FCSTD DOCUMENT  (FreeCAD 0.18.4R)
Label: SRM 2020
License: All rights reserved
LicenseURL: http://en.wikipedia.org/wiki/All_rights_reserved
objects: Part::Feature×163, App::Part×73, Sketcher::SketchObject×30, PartDesign::Pad×19, PartDesign::Body×17, Part::Fillet×15, PartDesign::Pocket×11, Part::MultiFuse×1, Mesh::Feature×1, Part::Cut×1
note: 287 computed .brp shape members not serialized (recipe doc carries the construction recipe); baked Part::Feature solids carry a one-line shape summary decoded from their .brp

FEATURE [Sketcher::SketchObject] Sketch005  label="Sketch_L_Bracket"
  MapMode = 5
  Placement = pos=(-195.5,0,1.5) rot=(0,1,0;3.14159rad)
  sketch-geometry (46):
    g0: LineSegment StartX=0 StartY=36 StartZ=0 EndX=12 EndY=36 EndZ=0
    g1: LineSegment StartX=12 StartY=36 StartZ=0 EndX=28 EndY=12 EndZ=0
    g2: LineSegment StartX=28 StartY=12 StartZ=0 EndX=28 EndY=0 EndZ=0
    g3: LineSegment StartX=28 StartY=0 StartZ=0 EndX=26 EndY=0 EndZ=0
    g4: LineSegment StartX=26 StartY=0 StartZ=0 EndX=26 EndY=-3 EndZ=0
    g5: LineSegment StartX=26 StartY=-3 StartZ=0 EndX=18 EndY=-3 EndZ=0
    g6: LineSegment StartX=18 StartY=-3 StartZ=0 EndX=18 EndY=0 EndZ=0
    g7: LineSegment StartX=18 StartY=0 StartZ=0 EndX=15.5 EndY=0 EndZ=0
    g8: LineSegment StartX=15.5 StartY=0 StartZ=0 EndX=15.5 EndY=4 EndZ=0
    g9: LineSegment StartX=15.5 StartY=4 StartZ=0 EndX=16.75 EndY=4 EndZ=0
    g10: LineSegment StartX=16.75 StartY=4 StartZ=0 EndX=16.75 EndY=6.3 EndZ=0
    g11: LineSegment StartX=11.25 StartY=6.3 StartZ=0 EndX=11.25 EndY=4 EndZ=0
    g12: LineSegment StartX=11.25 StartY=4 StartZ=0 EndX=12.5 EndY=4 EndZ=0
    g13: LineSegment StartX=12.5 StartY=4 StartZ=0 EndX=12.5 EndY=0 EndZ=0
    g14: LineSegment StartX=12.5 StartY=1e-16 StartZ=0 EndX=10 EndY=1e-16 EndZ=0
    g15: LineSegment StartX=10 StartY=1e-16 StartZ=0 EndX=10 EndY=-3 EndZ=0
    g16: LineSegment StartX=10 StartY=-3 StartZ=0 EndX=2 EndY=-3 EndZ=0
    g17: LineSegment StartX=2 StartY=-3 StartZ=0 EndX=2 EndY=0 EndZ=0
    g18: LineSegment StartX=2 StartY=0 StartZ=0 EndX=0 EndY=0 EndZ=0
    g19: LineSegment StartX=0 StartY=0 StartZ=0 EndX=0 EndY=10 EndZ=0
    g20: LineSegment StartX=0 StartY=10 StartZ=0 EndX=-3 EndY=10 EndZ=0
    g21: LineSegment StartX=-3 StartY=10 StartZ=0 EndX=-3 EndY=18 EndZ=0
    g22: LineSegment StartX=-3 StartY=18 StartZ=0 EndX=0 EndY=18 EndZ=0
    g23: LineSegment StartX=0 StartY=18 StartZ=0 EndX=0 EndY=20.5 EndZ=0
    g24: LineSegment StartX=0 StartY=20.5 StartZ=0 EndX=4 EndY=20.5 EndZ=0
    g25: LineSegment StartX=4 StartY=20.5 StartZ=0 EndX=4 EndY=19.25 EndZ=0
    g26: LineSegment StartX=4 StartY=19.25 StartZ=0 EndX=6.3 EndY=19.25 EndZ=0
    g27: LineSegment StartX=6.3 StartY=24.75 StartZ=0 EndX=4 EndY=24.75 EndZ=0
    g28: LineSegment StartX=4 StartY=24.75 StartZ=0 EndX=4 EndY=23.5 EndZ=0
    g29: LineSegment StartX=4 StartY=23.5 StartZ=0 EndX=0 EndY=23.5 EndZ=0
    g30: LineSegment StartX=0 StartY=23.5 StartZ=0 EndX=0 EndY=26 EndZ=0
    g31: LineSegment StartX=0 StartY=26 StartZ=0 EndX=-3 EndY=26 EndZ=0
    g32: LineSegment StartX=-3 StartY=26 StartZ=0 EndX=-3 EndY=34 EndZ=0
    g33: LineSegment StartX=-3 StartY=34 StartZ=0 EndX=0 EndY=34 EndZ=0
    g34: LineSegment StartX=0 StartY=34 StartZ=0 EndX=0 EndY=36 EndZ=0
    g35: LineSegment StartX=12.5 StartY=6.3 StartZ=0 EndX=12.5 EndY=9.3 EndZ=0
    g36: LineSegment StartX=12.5 StartY=9.3 StartZ=0 EndX=15.5 EndY=9.3 EndZ=0
    g37: LineSegment StartX=15.5 StartY=9.3 StartZ=0 EndX=15.5 EndY=6.3 EndZ=0
    g38: LineSegment StartX=11.25 StartY=6.3 StartZ=0 EndX=12.5 EndY=6.3 EndZ=0
    g39: LineSegment StartX=15.5 StartY=6.3 StartZ=0 EndX=16.75 EndY=6.3 EndZ=0
    g40: LineSegment StartX=6.3 StartY=24.75 StartZ=0 EndX=6.3 EndY=23.5 EndZ=0
    g41: LineSegment StartX=6.3 StartY=23.5 StartZ=0 EndX=9.3 EndY=23.5 EndZ=0
    g42: LineSegment StartX=9.3 StartY=23.5 StartZ=0 EndX=9.3 EndY=20.5 EndZ=0
    g43: LineSegment StartX=9.3 StartY=20.5 StartZ=0 EndX=6.3 EndY=20.5 EndZ=0
    g44: LineSegment StartX=6.3 StartY=20.5 StartZ=0 EndX=6.3 EndY=19.25 EndZ=0
    g45: GeomPoint X=0 Y=22 Z=0
  constraints (135):
    c: Horizontal(g0)
    c: Coincident(g1,g0)
    c: Coincident(g2,g1)
    c: Vertical(g2)
    c: Coincident(g3,g2)
    c: Horizontal(g3)
    c: Coincident(g4,g3)
    c: Vertical(g4)
    c: Coincident(g5,g4)
    c: Horizontal(g5)
    c: Coincident(g6,g5)
    c: Vertical(g6)
    c: Horizontal(g7)
    c: Coincident(g8,g7)
    c: Vertical(g8)
    c: Coincident(g9,g8)
    c: Coincident(g10,g9)
    c: Vertical(g10)
    c: Horizontal(g9)
    c: Vertical(g11)
    c: Coincident(g12,g11)
    c: Horizontal(g12)
    c: Coincident(g13,g12)
    c: Vertical(g13)
    c: Horizontal(g14)
    c: Coincident(g15,g14)
    c: Vertical(g15)
    c: Coincident(g16,g15)
    c: Horizontal(g16)
    c: Coincident(g17,g16)
    c: Vertical(g17)
    c: Coincident(g18,g17)
    c: Horizontal(g18)
    c: Coincident(g19,g18)
    c: Vertical(g19)
    c: Coincident(g20,g19)
    c: Horizontal(g20)
    c: Coincident(g21,g20)
    c: Vertical(g21)
    c: Coincident(g22,g21)
    c: Horizontal(g22)
    c: Coincident(g23,g22)
    c: Vertical(g23)
    c: Coincident(g24,g23)
    c: Horizontal(g24)
    c: Coincident(g25,g24)
    c: Vertical(g25)
    c: Coincident(g26,g25)
    c: Horizontal(g26)
    c: Horizontal(g27)
    c: Coincident(g28,g27)
    c: Vertical(g28)
    c: Coincident(g29,g28)
    c: Horizontal(g29)
    c: Coincident(g30,g29)
    c: Vertical(g30)
    c: Coincident(g31,g30)
    c: Coincident(g32,g31)
    c: Vertical(g32)
    c: Coincident(g33,g32)
    c: Coincident(g34,g33)
    c: Coincident(g34,g0)
    c: Horizontal(g33)
    c: Horizontal(g31)
    c: Vertical(g34)
    c: Coincident(g13,g14)
    c: Coincident(g6,g7)
    c: Vertical(g35)
    c: Coincident(g36,g35)
    c: Horizontal(g36)
    c: Coincident(g37,g36)
    c: Vertical(g37)
    c: Coincident(g38,g11)
    c: Coincident(g38,g35)
    c: Horizontal(g38)
    c: Coincident(g39,g10)
    c: Horizontal(g39)
    c: Coincident(g39,g37)
    c: Coincident(g40,g27)
    c: Vertical(g40)
    c: Coincident(g41,g40)
    c: Horizontal(g41)
    c: Coincident(g42,g41)
    c: Vertical(g42)
    c: Coincident(g43,g42)
    c: Horizontal(g43)
    c: Coincident(g44,g43)
    c: Vertical(g44)
    c: Coincident(g44,g26)
    c: DistanceY(g32,g32) = 8
    c: Equal(g32,g21)
    c: Equal(g21,g16)
    c: Equal(g16,g5)
    c: Equal(g42,g36)
    c: Equal(g27,g26)
    c: Equal(g26,g11)
    c: Equal(g11,g10)
    c: Equal(g41,g43)
    c: Equal(g43,g35)
    c: Equal(g35,g37)
    c: Equal(g29,g24)
    c: Equal(g24,g13)
    c: Equal(g13,g8)
    c: Equal(g30,g23)
    c: Equal(g23,g14)
    c: Equal(g14,g7)
    c: DistanceX(g33,g33) = 3
    c: Equal(g33,g31)
    c: Equal(g31,g22)
    c: Equal(g22,g20)
    c: Equal(g20,g17)
    c: Equal(g17,g15)
    c: Equal(g15,g6)
    c: Equal(g6,g4)
    c: Equal(g3,g34)
    c: Equal(g0,g2)
    c: DistanceX(g27,g27) = 2.3
    c: DistanceY(g42,g42) = 3
    c: DistanceX(g41,g41) = 3
    c: Equal(g28,g40)
    c: Equal(g40,g44)
    c: Equal(g44,g25)
    c: Equal(g38,g39)
    c: Equal(g39,g9)
    c: Equal(g9,g12)
    c: Equal(g38,g25)
    c: DistanceY(g28,g28) = 1.25
    c: DistanceX(g29,g29) = 4
    c: DistanceY(g30,g30) = 2.5
    c: DistanceY(g34,g34) = 2
    c: DistanceX(g0,g0) = 12
    c: DistanceX(g18,g18) = 2
    c: Coincident(g18,g-1)
    c: Symmetric(g29,g23,g45)
    c: DistanceY(g18,g45) = 22
FEATURE [PartDesign::Pad] Pad006
  Length = 3
  Length2 = 100
  Placement = pos=(-195.5,0,1.5) rot=(0,1,0;3.14159rad)
  Profile = -> Sketch005
  Refine = true
  Type = 0
FEATURE [PartDesign::Body] Body006  label="Body Bracket L"
  Group = -> [Sketch005,Pad006]
  Origin = -> Origin006
  Tip = -> Pad006
FEATURE [Part::Fillet] Fillet010  label="Fillet001"
  Base = -> Body006
  Edges = 2 edges r=6: [Edge26,Edge29]
FEATURE [Sketcher::SketchObject] Sketch006  label="Sketch_R_Bracket"
  MapMode = 5
  Placement = pos=(195.5,0,-1.5) rot=(0,1,0;0rad)
  sketch-geometry (46):
    g0: LineSegment StartX=0 StartY=36 StartZ=0 EndX=12 EndY=36 EndZ=0
    g1: LineSegment StartX=12 StartY=36 StartZ=0 EndX=28 EndY=12 EndZ=0
    g2: LineSegment StartX=28 StartY=12 StartZ=0 EndX=28 EndY=0 EndZ=0
    g3: LineSegment StartX=28 StartY=0 StartZ=0 EndX=26 EndY=0 EndZ=0
    g4: LineSegment StartX=26 StartY=0 StartZ=0 EndX=26 EndY=-3 EndZ=0
    g5: LineSegment StartX=26 StartY=-3 StartZ=0 EndX=18 EndY=-3 EndZ=0
    g6: LineSegment StartX=18 StartY=-3 StartZ=0 EndX=18 EndY=0 EndZ=0
    g7: LineSegment StartX=18 StartY=0 StartZ=0 EndX=15.5 EndY=0 EndZ=0
    g8: LineSegment StartX=15.5 StartY=0 StartZ=0 EndX=15.5 EndY=4 EndZ=0
    g9: LineSegment StartX=15.5 StartY=4 StartZ=0 EndX=16.75 EndY=4 EndZ=0
    g10: LineSegment StartX=16.75 StartY=4 StartZ=0 EndX=16.75 EndY=6.3 EndZ=0
    g11: LineSegment StartX=11.25 StartY=6.3 StartZ=0 EndX=11.25 EndY=4 EndZ=0
    g12: LineSegment StartX=11.25 StartY=4 StartZ=0 EndX=12.5 EndY=4 EndZ=0
    g13: LineSegment StartX=12.5 StartY=4 StartZ=0 EndX=12.5 EndY=0 EndZ=0
    g14: LineSegment StartX=12.5 StartY=0 StartZ=0 EndX=10 EndY=0 EndZ=0
    g15: LineSegment StartX=10 StartY=0 StartZ=0 EndX=10 EndY=-3 EndZ=0
    g16: LineSegment StartX=10 StartY=-3 StartZ=0 EndX=2 EndY=-3 EndZ=0
    g17: LineSegment StartX=2 StartY=-3 StartZ=0 EndX=2 EndY=0 EndZ=0
    g18: LineSegment StartX=2 StartY=0 StartZ=0 EndX=0 EndY=0 EndZ=0
    g19: LineSegment StartX=0 StartY=0 StartZ=0 EndX=0 EndY=10 EndZ=0
    g20: LineSegment StartX=0 StartY=10 StartZ=0 EndX=-3 EndY=10 EndZ=0
    g21: LineSegment StartX=-3 StartY=10 StartZ=0 EndX=-3 EndY=18 EndZ=0
    g22: LineSegment StartX=-3 StartY=18 StartZ=0 EndX=0 EndY=18 EndZ=0
    g23: LineSegment StartX=0 StartY=18 StartZ=0 EndX=0 EndY=20.5 EndZ=0
    g24: LineSegment StartX=0 StartY=20.5 StartZ=0 EndX=4 EndY=20.5 EndZ=0
    g25: LineSegment StartX=4 StartY=20.5 StartZ=0 EndX=4 EndY=19.25 EndZ=0
    g26: LineSegment StartX=4 StartY=19.25 StartZ=0 EndX=6.3 EndY=19.25 EndZ=0
    g27: LineSegment StartX=6.3 StartY=24.75 StartZ=0 EndX=4 EndY=24.75 EndZ=0
    g28: LineSegment StartX=4 StartY=24.75 StartZ=0 EndX=4 EndY=23.5 EndZ=0
    g29: LineSegment StartX=4 StartY=23.5 StartZ=0 EndX=0 EndY=23.5 EndZ=0
    g30: LineSegment StartX=0 StartY=23.5 StartZ=0 EndX=0 EndY=26 EndZ=0
    g31: LineSegment StartX=0 StartY=26 StartZ=0 EndX=-3 EndY=26 EndZ=0
    g32: LineSegment StartX=-3 StartY=26 StartZ=0 EndX=-3 EndY=34 EndZ=0
    g33: LineSegment StartX=-3 StartY=34 StartZ=0 EndX=0 EndY=34 EndZ=0
    g34: LineSegment StartX=0 StartY=34 StartZ=0 EndX=0 EndY=36 EndZ=0
    g35: LineSegment StartX=12.5 StartY=6.3 StartZ=0 EndX=12.5 EndY=9.3 EndZ=0
    g36: LineSegment StartX=12.5 StartY=9.3 StartZ=0 EndX=15.5 EndY=9.3 EndZ=0
    g37: LineSegment StartX=15.5 StartY=9.3 StartZ=0 EndX=15.5 EndY=6.3 EndZ=0
    g38: LineSegment StartX=11.25 StartY=6.3 StartZ=0 EndX=12.5 EndY=6.3 EndZ=0
    g39: LineSegment StartX=15.5 StartY=6.3 StartZ=0 EndX=16.75 EndY=6.3 EndZ=0
    g40: LineSegment StartX=6.3 StartY=24.75 StartZ=0 EndX=6.3 EndY=23.5 EndZ=0
    g41: LineSegment StartX=6.3 StartY=23.5 StartZ=0 EndX=9.3 EndY=23.5 EndZ=0
    g42: LineSegment StartX=9.3 StartY=23.5 StartZ=0 EndX=9.3 EndY=20.5 EndZ=0
    g43: LineSegment StartX=9.3 StartY=20.5 StartZ=0 EndX=6.3 EndY=20.5 EndZ=0
    g44: LineSegment StartX=6.3 StartY=20.5 StartZ=0 EndX=6.3 EndY=19.25 EndZ=0
    g45: GeomPoint X=0 Y=22 Z=0
  constraints (135):
    c: Horizontal(g0)
    c: Coincident(g1,g0)
    c: Coincident(g2,g1)
    c: Vertical(g2)
    c: Coincident(g3,g2)
    c: Horizontal(g3)
    c: Coincident(g4,g3)
    c: Vertical(g4)
    c: Coincident(g5,g4)
    c: Horizontal(g5)
    c: Coincident(g6,g5)
    c: Vertical(g6)
    c: Horizontal(g7)
    c: Coincident(g8,g7)
    c: Vertical(g8)
    c: Coincident(g9,g8)
    c: Coincident(g10,g9)
    c: Vertical(g10)
    c: Horizontal(g9)
    c: Vertical(g11)
    c: Coincident(g12,g11)
    c: Horizontal(g12)
    c: Coincident(g13,g12)
    c: Vertical(g13)
    c: Horizontal(g14)
    c: Coincident(g15,g14)
    c: Vertical(g15)
    c: Coincident(g16,g15)
    c: Horizontal(g16)
    c: Coincident(g17,g16)
    c: Vertical(g17)
    c: Coincident(g18,g17)
    c: Horizontal(g18)
    c: Coincident(g19,g18)
    c: Vertical(g19)
    c: Coincident(g20,g19)
    c: Horizontal(g20)
    c: Coincident(g21,g20)
    c: Vertical(g21)
    c: Coincident(g22,g21)
    c: Horizontal(g22)
    c: Coincident(g23,g22)
    c: Vertical(g23)
    c: Coincident(g24,g23)
    c: Horizontal(g24)
    c: Coincident(g25,g24)
    c: Vertical(g25)
    c: Coincident(g26,g25)
    c: Horizontal(g26)
    c: Horizontal(g27)
    c: Coincident(g28,g27)
    c: Vertical(g28)
    c: Coincident(g29,g28)
    c: Horizontal(g29)
    c: Coincident(g30,g29)
    c: Vertical(g30)
    c: Coincident(g31,g30)
    c: Coincident(g32,g31)
    c: Vertical(g32)
    c: Coincident(g33,g32)
    c: Coincident(g34,g33)
    c: Coincident(g34,g0)
    c: Horizontal(g33)
    c: Horizontal(g31)
    c: Vertical(g34)
    c: Coincident(g13,g14)
    c: Coincident(g6,g7)
    c: Vertical(g35)
    c: Coincident(g36,g35)
    c: Horizontal(g36)
    c: Coincident(g37,g36)
    c: Vertical(g37)
    c: Coincident(g38,g11)
    c: Coincident(g38,g35)
    c: Horizontal(g38)
    c: Coincident(g39,g10)
    c: Horizontal(g39)
    c: Coincident(g39,g37)
    c: Coincident(g40,g27)
    c: Vertical(g40)
    c: Coincident(g41,g40)
    c: Horizontal(g41)
    c: Coincident(g42,g41)
    c: Vertical(g42)
    c: Coincident(g43,g42)
    c: Horizontal(g43)
    c: Coincident(g44,g43)
    c: Vertical(g44)
    c: Coincident(g44,g26)
    c: DistanceY(g32,g32) = 8
    c: Equal(g32,g21)
    c: Equal(g21,g16)
    c: Equal(g16,g5)
    c: Equal(g42,g36)
    c: Equal(g27,g26)
    c: Equal(g26,g11)
    c: Equal(g11,g10)
    c: Equal(g41,g43)
    c: Equal(g43,g35)
    c: Equal(g35,g37)
    c: Equal(g29,g24)
    c: Equal(g24,g13)
    c: Equal(g13,g8)
    c: Equal(g30,g23)
    c: Equal(g23,g14)
    c: Equal(g14,g7)
    c: DistanceX(g33,g33) = 3
    c: Equal(g33,g31)
    c: Equal(g31,g22)
    c: Equal(g22,g20)
    c: Equal(g20,g17)
    c: Equal(g17,g15)
    c: Equal(g15,g6)
    c: Equal(g6,g4)
    c: Equal(g3,g34)
    c: Equal(g0,g2)
    c: DistanceX(g27,g27) = 2.3
    c: DistanceY(g42,g42) = 3
    c: DistanceX(g41,g41) = 3
    c: Equal(g28,g40)
    c: Equal(g40,g44)
    c: Equal(g44,g25)
    c: Equal(g38,g39)
    c: Equal(g39,g9)
    c: Equal(g9,g12)
    c: Equal(g38,g25)
    c: DistanceY(g28,g28) = 1.25
    c: DistanceX(g29,g29) = 4
    c: DistanceY(g30,g30) = 2.5
    c: DistanceY(g34,g34) = 2
    c: DistanceX(g0,g0) = 12
    c: Coincident(g18,g-1)
    c: Symmetric(g29,g23,g45)
    c: DistanceY(g18,g45) = 22
    c: DistanceX(g18,g18) = 2
FEATURE [PartDesign::Pad] Pad007
  Length = 3
  Length2 = 100
  Placement = pos=(195.5,0,-1.5) rot=(0,1,0;0rad)
  Profile = -> Sketch006
  Refine = true
  Type = 0
FEATURE [PartDesign::Body] Body007  label="Body Bracket R"
  Group = -> [Sketch006,Pad007]
  Origin = -> Origin007
  Tip = -> Pad007
FEATURE [Part::Fillet] Fillet011  label="Fillet"
  Base = -> Body007
  Edges = 2 edges r=6: [Edge26,Edge29]
FEATURE [Part::Fillet] Fillet  label="Bracket L"
  Base = -> Fillet010
  Edges = 4 edges r=1.5: [Edge107,Edge109,Edge139,Edge141]
FEATURE [Part::Fillet] Fillet012  label="Bracket R"
  Base = -> Fillet011
  Edges = 4 edges r=1.5: [Edge107,Edge109,Edge139,Edge141]
FEATURE [Sketcher::SketchObject] Sketch001002007  label="Sketch Seite L001"
  Placement = pos=(-192.5,0,0) rot=(0.707107,0,-0.707107;3.14159rad)
  sketch-geometry (104):
    g0: LineSegment StartX=-22 StartY=0 StartZ=0 EndX=-14 EndY=0 EndZ=0
    g1: LineSegment StartX=-14 StartY=0 StartZ=0 EndX=-14 EndY=3 EndZ=0
    g2: LineSegment StartX=-14 StartY=3 StartZ=0 EndX=-4 EndY=3 EndZ=0
    g3: LineSegment StartX=-4 StartY=3 StartZ=0 EndX=-4 EndY=0 EndZ=0
    g4: LineSegment StartX=-4 StartY=0 StartZ=0 EndX=4 EndY=0 EndZ=0
    g5: LineSegment StartX=4 StartY=0 StartZ=0 EndX=4 EndY=3 EndZ=0
    g6: LineSegment StartX=4 StartY=3 StartZ=0 EndX=14 EndY=3 EndZ=0
    g7: LineSegment StartX=14 StartY=3 StartZ=0 EndX=14 EndY=0 EndZ=0
    g8: LineSegment StartX=14 StartY=0 StartZ=0 EndX=22 EndY=0 EndZ=0
    g9: LineSegment StartX=14 StartY=-106 StartZ=0 EndX=14 EndY=-109 EndZ=0
    g10: LineSegment StartX=14 StartY=-109 StartZ=0 EndX=4 EndY=-109 EndZ=0
    g11: LineSegment StartX=4 StartY=-109 StartZ=0 EndX=4 EndY=-106 EndZ=0
    g12: LineSegment StartX=-4 StartY=-106 StartZ=0 EndX=-4 EndY=-109 EndZ=0
    g13: LineSegment StartX=-4 StartY=-109 StartZ=0 EndX=-14 EndY=-109 EndZ=0
    g14: LineSegment StartX=-14 StartY=-109 StartZ=0 EndX=-14 EndY=-106 EndZ=0
    g15: LineSegment StartX=16.5 StartY=-102 StartZ=0 EndX=19.5 EndY=-102 EndZ=0
    g16: LineSegment StartX=19.5 StartY=-102 StartZ=0 EndX=19.5 EndY=-92 EndZ=0
    g17: LineSegment StartX=19.5 StartY=-92 StartZ=0 EndX=16.5 EndY=-92 EndZ=0
    g18: LineSegment StartX=16.5 StartY=-59 StartZ=0 EndX=19.5 EndY=-59 EndZ=0
    g19: LineSegment StartX=19.5 StartY=-59 StartZ=0 EndX=19.5 EndY=-49 EndZ=0
    g20: LineSegment StartX=19.5 StartY=-49 StartZ=0 EndX=16.5 EndY=-49 EndZ=0
    g21: LineSegment StartX=16.5 StartY=-45 StartZ=0 EndX=22 EndY=-45 EndZ=0
    g22: LineSegment StartX=22 StartY=-45 StartZ=0 EndX=22 EndY=0 EndZ=0
    g23: LineSegment StartX=-4 StartY=-106 StartZ=0 EndX=-1.5 EndY=-106 EndZ=0
    g24: LineSegment StartX=-1.5 StartY=-106 StartZ=0 EndX=-1.5 EndY=-101 EndZ=0
    g25: LineSegment StartX=-1.5 StartY=-101 StartZ=0 EndX=-2.75 EndY=-101 EndZ=0
    g26: LineSegment StartX=-2.75 StartY=-101 StartZ=0 EndX=-2.75 EndY=-98.7 EndZ=0
    g27: LineSegment StartX=-2.75 StartY=-98.7 StartZ=0 EndX=-1.5 EndY=-98.7 EndZ=0
    g28: LineSegment StartX=-1.5 StartY=-98.7 StartZ=0 EndX=-1.5 EndY=-95.7 EndZ=0
    g29: LineSegment StartX=-1.5 StartY=-95.7 StartZ=0 EndX=1.5 EndY=-95.7 EndZ=0
    g30: LineSegment StartX=1.5 StartY=-95.7 StartZ=0 EndX=1.5 EndY=-98.7 EndZ=0
    g31: LineSegment StartX=1.5 StartY=-98.7 StartZ=0 EndX=2.75 EndY=-98.7 EndZ=0
    g32: LineSegment StartX=2.75 StartY=-98.7 StartZ=0 EndX=2.75 EndY=-101 EndZ=0
    g33: LineSegment StartX=2.75 StartY=-101 StartZ=0 EndX=1.5 EndY=-101 EndZ=0
    g34: LineSegment StartX=1.5 StartY=-101 StartZ=0 EndX=1.5 EndY=-106 EndZ=0
    g35: LineSegment StartX=1.5 StartY=-106 StartZ=0 EndX=4 EndY=-106 EndZ=0
    g36: LineSegment StartX=16.5 StartY=-59 StartZ=0 EndX=16.5 EndY=-74 EndZ=0
    g37: LineSegment StartX=16.5 StartY=-45 StartZ=0 EndX=16.5 EndY=-49 EndZ=0
    g38: LineSegment StartX=16.5 StartY=-102 StartZ=0 EndX=16.5 EndY=-106 EndZ=0
    g39: LineSegment StartX=16.5 StartY=-74 StartZ=0 EndX=11.5 EndY=-74 EndZ=0
    g40: LineSegment StartX=11.5 StartY=-74 StartZ=0 EndX=11.5 EndY=-72.75 EndZ=0
    g41: LineSegment StartX=11.5 StartY=-72.75 StartZ=0 EndX=9.2 EndY=-72.75 EndZ=0
    g42: LineSegment StartX=9.2 StartY=-72.75 StartZ=0 EndX=9.2 EndY=-74 EndZ=0
    g43: LineSegment StartX=9.2 StartY=-74 StartZ=0 EndX=6.2 EndY=-74 EndZ=0
    g44: LineSegment StartX=6.2 StartY=-74 StartZ=0 EndX=6.2 EndY=-77 EndZ=0
    g45: LineSegment StartX=6.2 StartY=-77 StartZ=0 EndX=9.2 EndY=-77 EndZ=0
    g46: LineSegment StartX=9.2 StartY=-77 StartZ=0 EndX=9.2 EndY=-78.25 EndZ=0
    g47: LineSegment StartX=9.2 StartY=-78.25 StartZ=0 EndX=11.5 EndY=-78.25 EndZ=0
    g48: LineSegment StartX=11.5 StartY=-78.25 StartZ=0 EndX=11.5 EndY=-77 EndZ=0
    g49: LineSegment StartX=11.5 StartY=-77 StartZ=0 EndX=16.5 EndY=-77 EndZ=0
    g50: Circle CenterX=-17.5 CenterY=-5.5 CenterZ=0 NormalX=0 NormalY=0 NormalZ=1 AngleXU=0 Radius=1.5
    g51: Circle CenterX=17.5 CenterY=-5.5 CenterZ=0 NormalX=0 NormalY=0 NormalZ=1 AngleXU=0 Radius=1.5
    g52: Circle CenterX=-12.5 CenterY=-13 CenterZ=0 NormalX=0 NormalY=0 NormalZ=1 AngleXU=0 Radius=1.5
    g53: Circle CenterX=12.5 CenterY=-13 CenterZ=0 NormalX=0 NormalY=0 NormalZ=1 AngleXU=0 Radius=1.5
    g54: Circle CenterX=-10 CenterY=-18 CenterZ=0 NormalX=0 NormalY=0 NormalZ=1 AngleXU=0 Radius=1.5
    g55: Circle CenterX=10 CenterY=-18 CenterZ=0 NormalX=0 NormalY=0 NormalZ=1 AngleXU=0 Radius=1.5
    g56: Circle CenterX=0 CenterY=-22 CenterZ=0 NormalX=0 NormalY=0 NormalZ=1 AngleXU=0 Radius=1.5
    g57: Circle CenterX=-10 CenterY=-28 CenterZ=0 NormalX=0 NormalY=0 NormalZ=1 AngleXU=0 Radius=1.5
    g58: Circle CenterX=-12.5 CenterY=-33 CenterZ=0 NormalX=0 NormalY=0 NormalZ=1 AngleXU=0 Radius=1.5
    g59: Circle CenterX=-17.5 CenterY=-40.5 CenterZ=0 NormalX=0 NormalY=0 NormalZ=1 AngleXU=0 Radius=1.5
    g60: Circle CenterX=10 CenterY=-28 CenterZ=0 NormalX=0 NormalY=0 NormalZ=1 AngleXU=0 Radius=1.5
    g61: Circle CenterX=12.5 CenterY=-33 CenterZ=0 NormalX=0 NormalY=0 NormalZ=1 AngleXU=0 Radius=1.5
    g62: Circle CenterX=17.5 CenterY=-40.5 CenterZ=0 NormalX=0 NormalY=0 NormalZ=1 AngleXU=0 Radius=1.5
    g63: LineSegment [constr] StartX=-10 StartY=-18 StartZ=0 EndX=10 EndY=-18 EndZ=0
    g64: LineSegment [constr] StartX=10 StartY=-18 StartZ=0 EndX=10 EndY=-28 EndZ=0
    g65: LineSegment [constr] StartX=10 StartY=-28 StartZ=0 EndX=-10 EndY=-28 EndZ=0
    g66: LineSegment [constr] StartX=-10 StartY=-28 StartZ=0 EndX=-10 EndY=-18 EndZ=0
    g67: LineSegment [constr] StartX=-12.5 StartY=-13 StartZ=0 EndX=12.5 EndY=-13 EndZ=0
    g68: LineSegment [constr] StartX=12.5 StartY=-13 StartZ=0 EndX=12.5 EndY=-33 EndZ=0
    g69: LineSegment [constr] StartX=12.5 StartY=-33 StartZ=0 EndX=-12.5 EndY=-33 EndZ=0
    g70: LineSegment [constr] StartX=-12.5 StartY=-33 StartZ=0 EndX=-12.5 EndY=-13 EndZ=0
    g71: LineSegment [constr] StartX=-17.5 StartY=-5.5 StartZ=0 EndX=17.5 EndY=-5.5 EndZ=0
    g72: LineSegment [constr] StartX=17.5 StartY=-5.5 StartZ=0 EndX=17.5 EndY=-40.5 EndZ=0
    g73: LineSegment [constr] StartX=17.5 StartY=-40.5 StartZ=0 EndX=-17.5 EndY=-40.5 EndZ=0
    g74: LineSegment [constr] StartX=-17.5 StartY=-40.5 StartZ=0 EndX=-17.5 EndY=-5.5 EndZ=0
    g75: LineSegment StartX=-1.5 StartY=-10.1 StartZ=0 EndX=1.5 EndY=-10.1 EndZ=0
    g76: LineSegment StartX=1.5 StartY=-10.1 StartZ=0 EndX=1.5 EndY=-17.9 EndZ=0
    g77: LineSegment StartX=1.5 StartY=-17.9 StartZ=0 EndX=-1.5 EndY=-17.9 EndZ=0
    g78: LineSegment StartX=-1.5 StartY=-17.9 StartZ=0 EndX=-1.5 EndY=-10.1 EndZ=0
    g79: LineSegment StartX=-1.5 StartY=-26.1 StartZ=0 EndX=1.5 EndY=-26.1 EndZ=0
    g80: LineSegment StartX=1.5 StartY=-26.1 StartZ=0 EndX=1.5 EndY=-33.9 EndZ=0
    g81: LineSegment StartX=1.5 StartY=-33.9 StartZ=0 EndX=-1.5 EndY=-33.9 EndZ=0
    g82: LineSegment StartX=-1.5 StartY=-33.9 StartZ=0 EndX=-1.5 EndY=-26.1 EndZ=0
    g83: LineSegment [constr] StartX=0 StartY=-22 StartZ=0 EndX=0 EndY=-14 EndZ=0
    g84: LineSegment [constr] StartX=0 StartY=-22 StartZ=0 EndX=0 EndY=-30 EndZ=0
    g85: LineSegment StartX=-22 StartY=0 StartZ=0 EndX=-22 EndY=-45 EndZ=0
    g86: LineSegment StartX=-22 StartY=-45 StartZ=0 EndX=-17.5 EndY=-45 EndZ=0
    g87: LineSegment StartX=-17.5 StartY=-45 StartZ=0 EndX=-17.5 EndY=-70.5 EndZ=0
    g88: LineSegment StartX=-17.5 StartY=-70.5 StartZ=0 EndX=-20.5 EndY=-70.5 EndZ=0
    g89: LineSegment StartX=-20.5 StartY=-70.5 StartZ=0 EndX=-20.5 EndY=-80.5 EndZ=0
    g90: LineSegment StartX=-20.5 StartY=-80.5 StartZ=0 EndX=-17.5 EndY=-80.5 EndZ=0
    g91: LineSegment [constr] StartX=-10 StartY=-18 StartZ=0 EndX=-10 EndY=-13 EndZ=0
    g92: LineSegment [constr] StartX=-10 StartY=-28 StartZ=0 EndX=-10 EndY=-33 EndZ=0
    g93: LineSegment [constr] StartX=-10 StartY=-18 StartZ=0 EndX=-12.5 EndY=-18 EndZ=0
    g94: LineSegment [constr] StartX=10 StartY=-18 StartZ=0 EndX=12.5 EndY=-18 EndZ=0
    g95: LineSegment [constr] StartX=-12.5 StartY=-13 StartZ=0 EndX=-12.5 EndY=-5.5 EndZ=0
    g96: LineSegment [constr] StartX=-12.5 StartY=-33 StartZ=0 EndX=-12.5 EndY=-40.5 EndZ=0
    g97: LineSegment [constr] StartX=-12.5 StartY=-13 StartZ=0 EndX=-17.5 EndY=-13 EndZ=0
    g98: LineSegment [constr] StartX=12.5 StartY=-13 StartZ=0 EndX=17.5 EndY=-13 EndZ=0
    g99: LineSegment StartX=14 StartY=-106 StartZ=0 EndX=16.5 EndY=-106 EndZ=0
    g100: LineSegment StartX=-17.5 StartY=-80.5 StartZ=0 EndX=-17.5 EndY=-106 EndZ=0
    g101: LineSegment StartX=-17.5 StartY=-106 StartZ=0 EndX=-14 EndY=-106 EndZ=0
    g102: LineSegment StartX=16.5 StartY=-92 StartZ=0 EndX=16.5 EndY=-77 EndZ=0
    g103: LineSegment [constr] StartX=-17.5 StartY=-5.5 StartZ=0 EndX=-17.5 EndY=0 EndZ=0
  constraints (297):
    c: Horizontal(g0)
    c: Coincident(g0,g1)
    c: Vertical(g1)
    c: Coincident(g1,g2)
    c: Horizontal(g2)
    c: Coincident(g2,g3)
    c: Vertical(g3)
    c: Coincident(g3,g4)
    c: Horizontal(g4)
    c: Coincident(g4,g5)
    c: Vertical(g5)
    c: Coincident(g5,g6)
    c: Horizontal(g6)
    c: Coincident(g6,g7)
    c: Vertical(g7)
    c: Coincident(g7,g8)
    c: Horizontal(g8)
    c: Vertical(g9)
    c: Coincident(g9,g10)
    c: Horizontal(g10)
    c: Coincident(g10,g11)
    c: Vertical(g11)
    c: Vertical(g12)
    c: Coincident(g12,g13)
    c: Coincident(g13,g14)
    c: Vertical(g14)
    c: Horizontal(g13)
    c: Equal(g2,g6)
    c: Equal(g6,g10)
    c: Equal(g10,g13)
    c: Equal(g0,g8)
    c: Equal(g1,g3)
    c: Equal(g3,g5)
    c: Equal(g5,g7)
    c: Equal(g7,g9)
    c: Equal(g9,g11)
    c: Equal(g11,g12)
    c: Equal(g12,g14)
    c: Horizontal(g15)
    c: Coincident(g15,g16)
    c: Vertical(g16)
    c: Coincident(g16,g17)
    c: Horizontal(g17)
    c: Horizontal(g18)
    c: Coincident(g18,g19)
    c: Vertical(g19)
    c: Coincident(g19,g20)
    c: Horizontal(g20)
    c: Horizontal(g21)
    c: Coincident(g21,g22)
    c: Coincident(g22,g8)
    c: Vertical(g22)
    c: Equal(g20,g18)
    c: Equal(g18,g17)
    c: Equal(g17,g15)
    c: Equal(g16,g19)
    c: DistanceY(g1,g1) = 3
    c: DistanceX(g0,g0) = 8
    c: DistanceX(g4,g4) = 8
    c: DistanceX(g2,g2) = 10
    c: DistanceX(g20,g20) = 3
    c: Coincident(g12,g23)
    c: Horizontal(g23)
    c: Coincident(g23,g24)
    c: Vertical(g24)
    c: Coincident(g24,g25)
    c: Horizontal(g25)
    c: Coincident(g25,g26)
    c: Vertical(g26)
    c: Coincident(g26,g27)
    c: Horizontal(g27)
    c: Coincident(g27,g28)
    c: Coincident(g28,g29)
    c: Horizontal(g29)
    c: Coincident(g29,g30)
    c: Vertical(g30)
    c: Coincident(g30,g31)
    c: Horizontal(g31)
    c: Coincident(g31,g32)
    c: Vertical(g32)
    c: Coincident(g32,g33)
    c: Horizontal(g33)
    c: Coincident(g33,g34)
    c: Vertical(g34)
    c: Coincident(g34,g35)
    c: Coincident(g35,g11)
    c: Horizontal(g35)
    c: Equal(g23,g35)
    c: Equal(g34,g24)
    c: Equal(g25,g27)
    c: Equal(g27,g31)
    c: Equal(g31,g33)
    c: Vertical(g28)
    c: DistanceX(g29,g29) = 3
    c: DistanceY(g19,g19) = 10
    c: Vertical(g36)
    c: Coincident(g37,g20)
    c: Vertical(g37)
    c: Coincident(g15,g38)
    c: Vertical(g38)
    c: Horizontal(g39)
    c: Coincident(g39,g40)
    c: Vertical(g40)
    c: Coincident(g40,g41)
    c: Horizontal(g41)
    c: Coincident(g41,g42)
    c: Vertical(g42)
    c: Coincident(g42,g43)
    c: Horizontal(g43)
    c: Coincident(g43,g44)
    c: Vertical(g44)
    c: Coincident(g44,g45)
    c: Horizontal(g45)
    c: Coincident(g45,g46)
    c: Vertical(g46)
    c: Coincident(g46,g47)
    c: Horizontal(g47)
    c: Coincident(g47,g48)
    c: Vertical(g48)
    c: Coincident(g48,g49)
    c: Horizontal(g49)
    c: Equal(g39,g49)
    c: Equal(g48,g46)
    c: Equal(g46,g42)
    c: Equal(g42,g40)
    c: Equal(g41,g47)
    c: Equal(g26,g32)
    c: Equal(g28,g30)
    c: Equal(g43,g45)
    c: DistanceY(g26,g26) = 2.3
    c: DistanceX(g27,g27) = 1.25
    c: Equal(g32,g47)
    c: DistanceY(g24,g24) = 5
    c: DistanceY(g28,g28) = 3
    c: Equal(g30,g45)
    c: Equal(g34,g49)
    c: Equal(g33,g48)
    c: DistanceX(g21,g21) = 5.5
    c: Equal(g50,g51)
    c: Equal(g51,g53)
    c: Equal(g53,g52)
    c: Equal(g52,g54)
    c: Equal(g54,g55)
    c: Equal(g55,g56)
    c: Equal(g56,g57)
    c: Equal(g57,g60)
    c: Equal(g60,g61)
    c: Equal(g61,g58)
    c: Equal(g58,g59)
    c: Equal(g59,g62)
    c: Coincident(g63,g64)
    c: Coincident(g64,g65)
    c: Coincident(g65,g66)
    c: Coincident(g66,g63)
    c: Horizontal(g63)
    c: Horizontal(g65)
    c: Vertical(g64)
    c: Vertical(g66)
    c: Coincident(g63,g54)
    c: Coincident(g64,g60)
    c: Coincident(g67,g68)
    c: Coincident(g68,g69)
    c: Coincident(g69,g70)
    c: Coincident(g70,g67)
    c: Horizontal(g67)
    c: Horizontal(g69)
    c: Vertical(g68)
    c: Vertical(g70)
    c: Coincident(g67,g52)
    c: Coincident(g68,g61)
    c: Coincident(g71,g72)
    c: Coincident(g72,g73)
    c: Coincident(g73,g74)
    c: Coincident(g74,g71)
    c: Horizontal(g71)
    c: Horizontal(g73)
    c: Vertical(g72)
    c: Vertical(g74)
    c: Coincident(g71,g50)
    c: Coincident(g72,g62)
    c: Coincident(g67,g53)
    c: Coincident(g58,g69)
    c: Coincident(g59,g73)
    c: Coincident(g57,g65)
    c: Coincident(g55,g63)
    c: Coincident(g51,g71)
    c: DistanceX(g67,g67) = 25
    c: DistanceY(g70,g70) = 20
    c: Radius(g50) = 1.5
    c: DistanceY(g66,g66) = 10
    c: DistanceX(g63,g63) = 20
    c: Equal(g74,g71)
    c: DistanceX(g71,g71) = 35
    c: PointOnObject(g56,g-2)
    c: DistanceY(g56,g4) = 22
    c: Coincident(g75,g76)
    c: Coincident(g76,g77)
    c: Coincident(g77,g78)
    c: Coincident(g78,g75)
    c: Horizontal(g75)
    c: Horizontal(g77)
    c: Vertical(g76)
    c: Vertical(g78)
    c: Coincident(g79,g80)
    c: Coincident(g80,g81)
    c: Coincident(g81,g82)
    c: Coincident(g82,g79)
    c: Horizontal(g79)
    c: Horizontal(g81)
    c: Vertical(g80)
    c: Vertical(g82)
    c: Coincident(g83,g56)
    c: Coincident(g84,g56)
    c: Vertical(g84)
    c: Equal(g83,g84)
    c: Symmetric(g79,g80,g84)
    c: Symmetric(g75,g76,g83)
    c: Equal(g78,g82)
    c: Equal(g77,g79)
    c: DistanceX(g75,g75) = 3
    c: DistanceY(g78,g78) = 7.8
    c: DistanceY(g83,g83) = 8
    c: DistanceY(g22,g22) = 45
    c: Coincident(g0,g85)
    c: Vertical(g85)
    c: Coincident(g85,g86)
    c: Horizontal(g86)
    c: Coincident(g86,g87)
    c: Vertical(g87)
    c: Horizontal(g88)
    c: Coincident(g88,g89)
    c: Vertical(g89)
    c: Coincident(g89,g90)
    c: Horizontal(g90)
    c: Equal(g89,g16)
    c: Equal(g85,g22)
    c: Equal(g88,g90)
    c: Equal(g90,g15)
    c: DistanceY(g56,g55) = 4
    c: Coincident(g91,g54)
    c: PointOnObject(g91,g67)
    c: Vertical(g91)
    c: Coincident(g92,g57)
    c: PointOnObject(g92,g69)
    c: Vertical(g92)
    c: Coincident(g93,g54)
    c: PointOnObject(g93,g70)
    c: Horizontal(g93)
    c: Coincident(g94,g55)
    c: PointOnObject(g94,g68)
    c: Horizontal(g94)
    c: Coincident(g95,g52)
    c: PointOnObject(g95,g71)
    c: Vertical(g95)
    c: Coincident(g96,g58)
    c: PointOnObject(g96,g73)
    c: Vertical(g96)
    c: Equal(g92,g91)
    c: Equal(g93,g94)
    c: Equal(g95,g96)
    c: Coincident(g97,g52)
    c: PointOnObject(g97,g74)
    c: Horizontal(g97)
    c: Coincident(g98,g53)
    c: PointOnObject(g98,g72)
    c: Horizontal(g98)
    c: Equal(g97,g98)
    c: Symmetric(g55,g54,g83)
    c: Symmetric(g4,g3,g-1)
    c: Coincident(g9,g99)
    c: Horizontal(g99)
    c: Coincident(g90,g100)
    c: Vertical(g100)
    c: Coincident(g101,g14)
    c: Horizontal(g101)
    c: Coincident(g102,g17)
    c: Coincident(g102,g49)
    c: Vertical(g102)
    c: DistanceY(g44,g44) = 3
    c: DistanceY(g38,g38) = 4
    c: Coincident(g37,g21)
    c: Coincident(g18,g36)
    c: Equal(g36,g102)
    c: DistanceY(g37,g37) = 4
    c: Equal(g87,g100)
    c: DistanceX(g23,g23) = 2.5
    c: Coincident(g103,g50)
    c: PointOnObject(g103,g0)
    c: Vertical(g103)
    c: Coincident(g36,g39)
    c: Coincident(g101,g100)
    c: Coincident(g99,g38)
    c: DistanceY(g100,g0) = 106
    c: Coincident(g87,g88)
    c: DistanceX(g101,g101) = 3.5
    c: DistanceX(g86,g86) = 4.5
    c: DistanceX(g99,g99) = 2.5
FEATURE [PartDesign::Pad] Pad012
  Length = 3
  Length2 = 100
  Placement = pos=(-192.5,0,0) rot=(0.707107,0,-0.707107;3.14159rad)
  Profile = -> Sketch001002007
  Refine = true
  Type = 0
FEATURE [PartDesign::Body] Body012  label="Body L001"
  Group = -> [Sketch001002007,Pad012]
  Origin = -> Origin015
  Tip = -> Pad012
FEATURE [Part::Fillet] Fillet020  label="Fillet L"
  Base = -> Body012
  Edges = 8 edges r=1.5: [Edge5,Edge8,Edge17,Edge20,Edge29,Edge164,Edge167,Edge176]
FEATURE [Sketcher::SketchObject] Sketch001002010  label="Sketch_Back001"
  MapMode = 5
  Placement = pos=(0,106,0) rot=(1,0,0;1.5708rad)
  sketch-geometry (85):
    g0: LineSegment StartX=200.5 StartY=22 StartZ=0 EndX=200.5 EndY=-22 EndZ=0
    g1: LineSegment StartX=-200.5 StartY=22 StartZ=0 EndX=-200.5 EndY=-22 EndZ=0
    g2: LineSegment StartX=-200.5 StartY=22 StartZ=0 EndX=200.5 EndY=22 EndZ=0
    g3: LineSegment StartX=-200.5 StartY=-22 StartZ=0 EndX=200.5 EndY=-22 EndZ=0
    g4: Circle CenterX=-194 CenterY=0 CenterZ=0 NormalX=0 NormalY=0 NormalZ=1 AngleXU=0 Radius=1.5
    g5: Circle CenterX=194 CenterY=0 CenterZ=0 NormalX=0 NormalY=0 NormalZ=1 AngleXU=0 Radius=1.5
    g6: Circle CenterX=-121.5 CenterY=-5.2e-15 CenterZ=0 NormalX=0 NormalY=0 NormalZ=1 AngleXU=0 Radius=15
    g7: LineSegment StartX=192.5 StartY=14 StartZ=0 EndX=195.5 EndY=14 EndZ=0
    g8: LineSegment StartX=195.5 StartY=14 StartZ=0 EndX=195.5 EndY=4.2 EndZ=0
    g9: LineSegment StartX=195.5 StartY=4.2 StartZ=0 EndX=192.5 EndY=4.2 EndZ=0
    g10: LineSegment StartX=192.5 StartY=4.2 StartZ=0 EndX=192.5 EndY=14 EndZ=0
    g11: LineSegment StartX=192.5 StartY=-4.2 StartZ=0 EndX=195.5 EndY=-4.2 EndZ=0
    g12: LineSegment StartX=195.5 StartY=-4.2 StartZ=0 EndX=195.5 EndY=-14 EndZ=0
    g13: LineSegment StartX=195.5 StartY=-14 StartZ=0 EndX=192.5 EndY=-14 EndZ=0
    g14: LineSegment StartX=192.5 StartY=-14 StartZ=0 EndX=192.5 EndY=-4.2 EndZ=0
    g15: LineSegment StartX=-195.5 StartY=14 StartZ=0 EndX=-192.5 EndY=14 EndZ=0
    g16: LineSegment StartX=-192.5 StartY=14 StartZ=0 EndX=-192.5 EndY=4.2 EndZ=0
    g17: LineSegment StartX=-192.5 StartY=4.2 StartZ=0 EndX=-195.5 EndY=4.2 EndZ=0
    g18: LineSegment StartX=-195.5 StartY=4.2 StartZ=0 EndX=-195.5 EndY=14 EndZ=0
    g19: LineSegment StartX=-195.5 StartY=-4.2 StartZ=0 EndX=-192.5 EndY=-4.2 EndZ=0
    g20: LineSegment StartX=-192.5 StartY=-4.2 StartZ=0 EndX=-192.5 EndY=-14 EndZ=0
    g21: LineSegment StartX=-192.5 StartY=-14 StartZ=0 EndX=-195.5 EndY=-14 EndZ=0
    g22: LineSegment StartX=-195.5 StartY=-14 StartZ=0 EndX=-195.5 EndY=-4.2 EndZ=0
    g23: LineSegment [constr] StartX=-194 StartY=0 StartZ=0 EndX=-200.5 EndY=0 EndZ=0
    g24: LineSegment [constr] StartX=194 StartY=0 StartZ=0 EndX=200.5 EndY=0 EndZ=0
    g25: LineSegment [constr] StartX=-194 StartY=4.2 StartZ=0 EndX=-194 EndY=0 EndZ=0
    g26: LineSegment [constr] StartX=-194 StartY=0 StartZ=0 EndX=-194 EndY=-4.2 EndZ=0
    g27: LineSegment [constr] StartX=194 StartY=0 StartZ=0 EndX=194 EndY=4.2 EndZ=0
    g28: LineSegment [constr] StartX=194 StartY=0 StartZ=0 EndX=194 EndY=-4.2 EndZ=0
    g29: LineSegment StartX=-178.4 StartY=-16.5 StartZ=0 EndX=-168.6 EndY=-16.5 EndZ=0
    g30: LineSegment StartX=-168.6 StartY=-16.5 StartZ=0 EndX=-168.6 EndY=-19.5 EndZ=0
    g31: LineSegment StartX=-168.6 StartY=-19.5 StartZ=0 EndX=-178.4 EndY=-19.5 EndZ=0
    g32: LineSegment StartX=-178.4 StartY=-19.5 StartZ=0 EndX=-178.4 EndY=-16.5 EndZ=0
    g33: LineSegment StartX=88.6 StartY=-16.5 StartZ=0 EndX=98.4 EndY=-16.5 EndZ=0
    g34: LineSegment StartX=98.4 StartY=-16.5 StartZ=0 EndX=98.4 EndY=-19.5 EndZ=0
    g35: LineSegment StartX=98.4 StartY=-19.5 StartZ=0 EndX=88.6 EndY=-19.5 EndZ=0
    g36: LineSegment StartX=88.6 StartY=-19.5 StartZ=0 EndX=88.6 EndY=-16.5 EndZ=0
    g37: LineSegment [constr] StartX=-168.6 StartY=-19.5 StartZ=0 EndX=88.6 EndY=-19.5 EndZ=0
    g38: LineSegment StartX=-178.4 StartY=20.5 StartZ=0 EndX=-168.6 EndY=20.5 EndZ=0
    g39: LineSegment StartX=-168.6 StartY=20.5 StartZ=0 EndX=-168.6 EndY=17.5 EndZ=0
    g40: LineSegment StartX=-168.6 StartY=17.5 StartZ=0 EndX=-178.4 EndY=17.5 EndZ=0
    g41: LineSegment StartX=-178.4 StartY=17.5 StartZ=0 EndX=-178.4 EndY=20.5 EndZ=0
    g42: LineSegment StartX=88.6 StartY=20.5 StartZ=0 EndX=98.4 EndY=20.5 EndZ=0
    g43: LineSegment StartX=98.4 StartY=20.5 StartZ=0 EndX=98.4 EndY=17.5 EndZ=0
    g44: LineSegment StartX=98.4 StartY=17.5 StartZ=0 EndX=88.6 EndY=17.5 EndZ=0
    g45: LineSegment StartX=88.6 StartY=17.5 StartZ=0 EndX=88.6 EndY=20.5 EndZ=0
    g46: LineSegment [constr] StartX=-178.4 StartY=17.5 StartZ=0 EndX=-178.4 EndY=-16.5 EndZ=0
    g47: LineSegment [constr] StartX=88.6 StartY=17.5 StartZ=0 EndX=88.6 EndY=-16.5 EndZ=0
    g48: LineSegment [constr] StartX=-178.4 StartY=-19.5 StartZ=0 EndX=-178.4 EndY=-22 EndZ=0
    g49: LineSegment [constr] StartX=-178.4 StartY=20.5 StartZ=0 EndX=-178.4 EndY=22 EndZ=0
    g50: LineSegment [constr] StartX=-186.5 StartY=10 StartZ=0 EndX=-146.5 EndY=10 EndZ=0
    g51: LineSegment [constr] StartX=-146.5 StartY=10 StartZ=0 EndX=-146.5 EndY=-10 EndZ=0
    g52: LineSegment [constr] StartX=-146.5 StartY=-10 StartZ=0 EndX=-186.5 EndY=-10 EndZ=0
    g53: LineSegment [constr] StartX=-186.5 StartY=-10 StartZ=0 EndX=-186.5 EndY=10 EndZ=0
    g54: LineSegment [constr] StartX=87.5 StartY=10 StartZ=0 EndX=147.5 EndY=10 EndZ=0
    g55: LineSegment [constr] StartX=147.5 StartY=10 StartZ=0 EndX=147.5 EndY=-10 EndZ=0
    g56: LineSegment [constr] StartX=147.5 StartY=-10 StartZ=0 EndX=87.5 EndY=-10 EndZ=0
    g57: LineSegment [constr] StartX=87.5 StartY=-10 StartZ=0 EndX=87.5 EndY=10 EndZ=0
    g58: LineSegment [constr] StartX=147.5 StartY=10 StartZ=0 EndX=192.5 EndY=10 EndZ=0
    g59: LineSegment [constr] StartX=-186.5 StartY=10 StartZ=0 EndX=-192.5 EndY=10 EndZ=0
    g60: Circle CenterX=-146.5 CenterY=10 CenterZ=0 NormalX=0 NormalY=0 NormalZ=1 AngleXU=0 Radius=1.5
    g61: Circle CenterX=-186.5 CenterY=-10 CenterZ=0 NormalX=0 NormalY=0 NormalZ=1 AngleXU=0 Radius=1.5
    g62: Circle CenterX=87.5 CenterY=-10 CenterZ=0 NormalX=0 NormalY=0 NormalZ=1 AngleXU=0 Radius=1.5
    g63: Circle CenterX=147.5 CenterY=10 CenterZ=0 NormalX=0 NormalY=0 NormalZ=1 AngleXU=0 Radius=1.5
    g64: Circle CenterX=-38 CenterY=0 CenterZ=0 NormalX=0 NormalY=0 NormalZ=1 AngleXU=0 Radius=1.5
    g65: LineSegment StartX=-39.5 StartY=14 StartZ=0 EndX=-36.5 EndY=14 EndZ=0
    g66: LineSegment StartX=-36.5 StartY=14 StartZ=0 EndX=-36.5 EndY=4.2 EndZ=0
    g67: LineSegment StartX=-36.5 StartY=4.2 StartZ=0 EndX=-39.5 EndY=4.2 EndZ=0
    g68: LineSegment StartX=-39.5 StartY=4.2 StartZ=0 EndX=-39.5 EndY=14 EndZ=0
    g69: LineSegment StartX=-39.5 StartY=-4.2 StartZ=0 EndX=-36.5 EndY=-4.2 EndZ=0
    g70: LineSegment StartX=-36.5 StartY=-4.2 StartZ=0 EndX=-36.5 EndY=-14 EndZ=0
    g71: LineSegment StartX=-36.5 StartY=-14 StartZ=0 EndX=-39.5 EndY=-14 EndZ=0
    g72: LineSegment StartX=-39.5 StartY=-14 StartZ=0 EndX=-39.5 EndY=-4.2 EndZ=0
    g73: LineSegment [constr] StartX=-39.5 StartY=4.2 StartZ=0 EndX=-39.5 EndY=-4.2 EndZ=0
    g74: LineSegment [constr] StartX=-192.5 StartY=4.2 StartZ=0 EndX=-39.5 EndY=4.2 EndZ=0
    g75: LineSegment [constr] StartX=-96.5 StartY=10 StartZ=0 EndX=-46.5 EndY=10 EndZ=0
    g76: LineSegment [constr] StartX=-46.5 StartY=10 StartZ=0 EndX=-46.5 EndY=-10 EndZ=0
    g77: LineSegment [constr] StartX=-46.5 StartY=-10 StartZ=0 EndX=-96.5 EndY=-10 EndZ=0
    g78: LineSegment [constr] StartX=-96.5 StartY=-10 StartZ=0 EndX=-96.5 EndY=10 EndZ=0
    g79: LineSegment [constr] StartX=-146.5 StartY=10 StartZ=0 EndX=-96.5 EndY=10 EndZ=0
    g80: Circle CenterX=-96.5 CenterY=-10 CenterZ=0 NormalX=0 NormalY=0 NormalZ=1 AngleXU=0 Radius=1.5
    g81: Circle CenterX=-46.5 CenterY=10 CenterZ=0 NormalX=0 NormalY=0 NormalZ=1 AngleXU=0 Radius=1.5
    g82: LineSegment [constr] StartX=-121.5 StartY=-5.2e-15 StartZ=0 EndX=-96.5 EndY=-5.2e-15 EndZ=0
    g83: Circle CenterX=62.5 CenterY=-2e-16 CenterZ=0 NormalX=0 NormalY=0 NormalZ=1 AngleXU=0 Radius=10
    g84: LineSegment [constr] StartX=62.5 StartY=-2e-16 StartZ=0 EndX=87.5 EndY=-2e-16 EndZ=0
  constraints (233):
    c: Vertical(g0)
    c: DistanceY(g-1,g0) = 22
    c: Vertical(g1)
    c: Coincident(g2,g1)
    c: Coincident(g2,g0)
    c: Coincident(g3,g1)
    c: Coincident(g3,g0)
    c: Horizontal(g3)
    c: PointOnObject(g5,g-1)
    c: PointOnObject(g4,g-1)
    c: Coincident(g7,g8)
    c: Coincident(g8,g9)
    c: Coincident(g9,g10)
    c: Coincident(g10,g7)
    c: Horizontal(g7)
    c: Horizontal(g9)
    c: Vertical(g8)
    c: Vertical(g10)
    c: Coincident(g11,g12)
    c: Coincident(g12,g13)
    c: Coincident(g13,g14)
    c: Coincident(g14,g11)
    c: Horizontal(g11)
    c: Horizontal(g13)
    c: Vertical(g12)
    c: Vertical(g14)
    c: Coincident(g15,g16)
    c: Coincident(g16,g17)
    c: Coincident(g17,g18)
    c: Coincident(g18,g15)
    c: Horizontal(g15)
    c: Horizontal(g17)
    c: Vertical(g16)
    c: Vertical(g18)
    c: Coincident(g19,g20)
    c: Coincident(g20,g21)
    c: Coincident(g21,g22)
    c: Coincident(g22,g19)
    c: Horizontal(g19)
    c: Horizontal(g21)
    c: Vertical(g20)
    c: Vertical(g22)
    c: Equal(g5,g4)
    c: Radius(g6) = 15
    c: Coincident(g23,g4)
    c: PointOnObject(g23,g1)
    c: Horizontal(g23)
    c: Coincident(g24,g5)
    c: PointOnObject(g24,g0)
    c: Horizontal(g24)
    c: Equal(g24,g23)
    c: DistanceX(g23,g23) = 6.5
    c: DistanceY(g18,g18) = 9.8
    c: DistanceX(g15,g15) = 3
    c: Coincident(g25,g4)
    c: Vertical(g25)
    c: Coincident(g26,g4)
    c: Vertical(g26)
    c: Symmetric(g16,g17,g25)
    c: Symmetric(g19,g19,g26)
    c: DistanceY(g25,g25) = 4.2
    c: Coincident(g27,g5)
    c: Vertical(g27)
    c: Coincident(g28,g5)
    c: Vertical(g28)
    c: Symmetric(g9,g8,g27)
    c: Symmetric(g11,g11,g28)
    c: Equal(g17,g9)
    c: Equal(g9,g11)
    c: Equal(g11,g19)
    c: Equal(g16,g10)
    c: Equal(g10,g14)
    c: Equal(g14,g20)
    c: Equal(g25,g26)
    c: Equal(g26,g27)
    c: Equal(g27,g28)
    c: DistanceY(g1,g1) = 44
    c: DistanceX(g2,g2) = 401
    c: Coincident(g29,g30)
    c: Coincident(g30,g31)
    c: Coincident(g31,g32)
    c: Coincident(g32,g29)
    c: Horizontal(g29)
    c: Horizontal(g31)
    c: Vertical(g30)
    c: Vertical(g32)
    c: Coincident(g33,g34)
    c: Coincident(g34,g35)
    c: Coincident(g35,g36)
    c: Coincident(g36,g33)
    c: Horizontal(g33)
    c: Horizontal(g35)
    c: Vertical(g34)
    c: Vertical(g36)
    c: Equal(g29,g33)
    c: Equal(g20,g29)
    c: Equal(g21,g32)
    c: Coincident(g37,g30)
    c: Coincident(g37,g35)
    c: Horizontal(g37)
    c: DistanceY(g29,g20) = 2.5
    c: Coincident(g38,g39)
    c: Coincident(g39,g40)
    c: Coincident(g40,g41)
    c: Coincident(g41,g38)
    c: Horizontal(g38)
    c: Horizontal(g40)
    c: Vertical(g39)
    c: Vertical(g41)
    c: Coincident(g42,g43)
    c: Coincident(g43,g44)
    c: Coincident(g44,g45)
    c: Coincident(g45,g42)
    c: Horizontal(g42)
    c: Horizontal(g44)
    c: Vertical(g43)
    c: Vertical(g45)
    c: Equal(g33,g44)
    c: Equal(g44,g40)
    c: Equal(g30,g39)
    c: Equal(g39,g45)
    c: Coincident(g46,g40)
    c: Coincident(g46,g29)
    c: Vertical(g46)
    c: Coincident(g47,g44)
    c: Coincident(g47,g33)
    c: Vertical(g47)
    c: Coincident(g48,g31)
    c: PointOnObject(g48,g3)
    c: Vertical(g48)
    c: Coincident(g49,g38)
    c: PointOnObject(g49,g2)
    c: Vertical(g49)
    c: Equal(g47,g46)
    c: Coincident(g50,g51)
    c: Coincident(g51,g52)
    c: Coincident(g52,g53)
    c: Coincident(g53,g50)
    c: Horizontal(g50)
    c: Horizontal(g52)
    c: Vertical(g51)
    c: Coincident(g54,g55)
    c: Coincident(g55,g56)
    c: Coincident(g56,g57)
    c: Coincident(g57,g54)
    c: Horizontal(g54)
    c: Horizontal(g56)
    c: Vertical(g55)
    c: Coincident(g58,g54)
    c: PointOnObject(g58,g10)
    c: Horizontal(g58)
    c: Coincident(g59,g50)
    c: Horizontal(g59)
    c: DistanceY(g53,g53) = 20
    c: Symmetric(g50,g52,g-1)
    c: Coincident(g60,g50)
    c: Coincident(g61,g52)
    c: Coincident(g62,g56)
    c: Coincident(g63,g54)
    c: Radius(g4) = 1.5
    c: Equal(g4,g61)
    c: Equal(g61,g60)
    c: Equal(g60,g62)
    c: Equal(g62,g63)
    c: Equal(g51,g57)
    c: Symmetric(g1,g0,g-1)
    c: PointOnObject(g59,g16)
    c: PointOnObject(g64,g-1)
    c: Coincident(g65,g66)
    c: Coincident(g66,g67)
    c: Coincident(g67,g68)
    c: Coincident(g68,g65)
    c: Horizontal(g65)
    c: Horizontal(g67)
    c: Vertical(g66)
    c: Vertical(g68)
    c: Coincident(g69,g70)
    c: Coincident(g70,g71)
    c: Coincident(g71,g72)
    c: Coincident(g72,g69)
    c: Horizontal(g69)
    c: Horizontal(g71)
    c: Vertical(g70)
    c: Vertical(g72)
    c: Equal(g69,g67)
    c: Equal(g66,g70)
    c: Symmetric(g67,g69,g64)
    c: Coincident(g73,g67)
    c: Coincident(g73,g69)
    c: Vertical(g73)
    c: Coincident(g74,g16)
    c: Coincident(g74,g67)
    c: Horizontal(g74)
    c: Equal(g68,g16)
    c: Equal(g15,g65)
    c: Coincident(g75,g76)
    c: Coincident(g76,g77)
    c: Coincident(g77,g78)
    c: Coincident(g78,g75)
    c: Horizontal(g75)
    c: Horizontal(g77)
    c: Vertical(g76)
    c: Vertical(g78)
    c: Coincident(g79,g60)
    c: Coincident(g79,g75)
    c: Horizontal(g79)
    c: Coincident(g80,g77)
    c: Coincident(g81,g75)
    c: Equal(g60,g80)
    c: Equal(g80,g81)
    c: Symmetric(g60,g80,g6)
    c: Equal(g51,g78)
    c: DistanceX(g50,g50) = 40
    c: DistanceX(g59,g59) = 6
    c: Equal(g64,g4)
    c: DistanceX(g75,g75) = 50
    c: Coincident(g82,g6)
    c: PointOnObject(g82,g78)
    c: Horizontal(g82)
    c: DistanceX(g79,g79) = 50
    c: Symmetric(g54,g62,g-1)
    c: Coincident(g84,g83)
    c: Horizontal(g84)
    c: Symmetric(g54,g62,g84)
    c: Equal(g84,g82)
    c: Radius(g83) = 10
    c: DistanceX(g54,g54) = 60
    c: DistanceX(g58,g58) = 45
    c: DistanceX(g64,g-1) = 38
    c: DistanceY(g49,g49) = 1.5
    c: Equal(g30,g36)
    c: DistanceX(g-1,g33) = 88.6
    c: DistanceX(g37,g37) = 257.2
FEATURE [PartDesign::Pad] Pad015
  Length = 3
  Length2 = 100
  Placement = pos=(0,106,0) rot=(1,0,0;1.5708rad)
  Profile = -> Sketch001002010
  Refine = true
  Reversed = true
  Type = 0
FEATURE [Sketcher::SketchObject] Sketch001002011  label="Sketch Seite R001"
  Placement = pos=(192.5,0,0) rot=(0.707107,0,-0.707107;3.14159rad)
  sketch-geometry (100):
    g0: LineSegment StartX=-22 StartY=0 StartZ=0 EndX=-14 EndY=0 EndZ=0
    g1: LineSegment StartX=-14 StartY=0 StartZ=0 EndX=-14 EndY=3 EndZ=0
    g2: LineSegment StartX=-14 StartY=3 StartZ=0 EndX=-4 EndY=3 EndZ=0
    g3: LineSegment StartX=-4 StartY=3 StartZ=0 EndX=-4 EndY=0 EndZ=0
    g4: LineSegment StartX=-4 StartY=0 StartZ=0 EndX=4 EndY=0 EndZ=0
    g5: LineSegment StartX=4 StartY=0 StartZ=0 EndX=4 EndY=3 EndZ=0
    g6: LineSegment StartX=4 StartY=3 StartZ=0 EndX=14 EndY=3 EndZ=0
    g7: LineSegment StartX=14 StartY=3 StartZ=0 EndX=14 EndY=0 EndZ=0
    g8: LineSegment StartX=14 StartY=0 StartZ=0 EndX=22 EndY=0 EndZ=0
    g9: LineSegment StartX=14 StartY=-106 StartZ=0 EndX=14 EndY=-109 EndZ=0
    g10: LineSegment StartX=14 StartY=-109 StartZ=0 EndX=4 EndY=-109 EndZ=0
    g11: LineSegment StartX=4 StartY=-109 StartZ=0 EndX=4 EndY=-106 EndZ=0
    g12: LineSegment StartX=-4 StartY=-106 StartZ=0 EndX=-4 EndY=-109 EndZ=0
    g13: LineSegment StartX=-4 StartY=-109 StartZ=0 EndX=-14 EndY=-109 EndZ=0
    g14: LineSegment StartX=-14 StartY=-109 StartZ=0 EndX=-14 EndY=-106 EndZ=0
    g15: LineSegment StartX=16.5 StartY=-57 StartZ=0 EndX=19.5 EndY=-57 EndZ=0
    g16: LineSegment StartX=19.5 StartY=-57 StartZ=0 EndX=19.5 EndY=-47 EndZ=0
    g17: LineSegment StartX=19.5 StartY=-47 StartZ=0 EndX=16.5 EndY=-47 EndZ=0
    g18: LineSegment StartX=16.5 StartY=-24 StartZ=0 EndX=19.5 EndY=-24 EndZ=0
    g19: LineSegment StartX=19.5 StartY=-24 StartZ=0 EndX=19.5 EndY=-14 EndZ=0
    g20: LineSegment StartX=19.5 StartY=-14 StartZ=0 EndX=16.5 EndY=-14 EndZ=0
    g21: LineSegment StartX=16.5 StartY=-10 StartZ=0 EndX=22 EndY=-10 EndZ=0
    g22: LineSegment StartX=22 StartY=-10 StartZ=0 EndX=22 EndY=0 EndZ=0
    g23: LineSegment StartX=-4 StartY=-106 StartZ=0 EndX=-1.5 EndY=-106 EndZ=0
    g24: LineSegment StartX=-1.5 StartY=-106 StartZ=0 EndX=-1.5 EndY=-101 EndZ=0
    g25: LineSegment StartX=-1.5 StartY=-101 StartZ=0 EndX=-2.75 EndY=-101 EndZ=0
    g26: LineSegment StartX=-2.75 StartY=-101 StartZ=0 EndX=-2.75 EndY=-98.7 EndZ=0
    g27: LineSegment StartX=-2.75 StartY=-98.7 StartZ=0 EndX=-1.5 EndY=-98.7 EndZ=0
    g28: LineSegment StartX=-1.5 StartY=-98.7 StartZ=0 EndX=-1.5 EndY=-95.7 EndZ=0
    g29: LineSegment StartX=-1.5 StartY=-95.7 StartZ=0 EndX=1.5 EndY=-95.7 EndZ=0
    g30: LineSegment StartX=1.5 StartY=-95.7 StartZ=0 EndX=1.5 EndY=-98.7 EndZ=0
    g31: LineSegment StartX=1.5 StartY=-98.7 StartZ=0 EndX=2.75 EndY=-98.7 EndZ=0
    g32: LineSegment StartX=2.75 StartY=-98.7 StartZ=0 EndX=2.75 EndY=-101 EndZ=0
    g33: LineSegment StartX=2.75 StartY=-101 StartZ=0 EndX=1.5 EndY=-101 EndZ=0
    g34: LineSegment StartX=1.5 StartY=-101 StartZ=0 EndX=1.5 EndY=-106 EndZ=0
    g35: LineSegment StartX=1.5 StartY=-106 StartZ=0 EndX=4 EndY=-106 EndZ=0
    g36: LineSegment StartX=16.5 StartY=-24 StartZ=0 EndX=16.5 EndY=-34 EndZ=0
    g37: LineSegment StartX=16.5 StartY=-34 StartZ=0 EndX=11.5 EndY=-34 EndZ=0
    g38: LineSegment StartX=11.5 StartY=-34 StartZ=0 EndX=11.5 EndY=-32.75 EndZ=0
    g39: LineSegment StartX=11.5 StartY=-32.75 StartZ=0 EndX=9.2 EndY=-32.75 EndZ=0
    g40: LineSegment StartX=9.2 StartY=-32.75 StartZ=0 EndX=9.2 EndY=-34 EndZ=0
    g41: LineSegment StartX=9.2 StartY=-34 StartZ=0 EndX=6.2 EndY=-34 EndZ=0
    g42: LineSegment StartX=6.2 StartY=-34 StartZ=0 EndX=6.2 EndY=-37 EndZ=0
    g43: LineSegment StartX=6.2 StartY=-37 StartZ=0 EndX=9.2 EndY=-37 EndZ=0
    g44: LineSegment StartX=9.2 StartY=-37 StartZ=0 EndX=9.2 EndY=-38.25 EndZ=0
    g45: LineSegment StartX=9.2 StartY=-38.25 StartZ=0 EndX=11.5 EndY=-38.25 EndZ=0
    g46: LineSegment StartX=11.5 StartY=-38.25 StartZ=0 EndX=11.5 EndY=-37 EndZ=0
    g47: LineSegment StartX=11.5 StartY=-37 StartZ=0 EndX=16.5 EndY=-37 EndZ=0
    g48: LineSegment StartX=16.5 StartY=-10 StartZ=0 EndX=16.5 EndY=-14 EndZ=0
    g49: LineSegment StartX=16.5 StartY=-57 StartZ=0 EndX=16.5 EndY=-61 EndZ=0
    g50: Circle CenterX=0 CenterY=-22 CenterZ=0 NormalX=0 NormalY=0 NormalZ=1 AngleXU=0 Radius=1.5
    g51: LineSegment StartX=-1.5 StartY=-10.1 StartZ=0 EndX=1.5 EndY=-10.1 EndZ=0
    g52: LineSegment StartX=1.5 StartY=-10.1 StartZ=0 EndX=1.5 EndY=-17.9 EndZ=0
    g53: LineSegment StartX=1.5 StartY=-17.9 StartZ=0 EndX=-1.5 EndY=-17.9 EndZ=0
    g54: LineSegment StartX=-1.5 StartY=-17.9 StartZ=0 EndX=-1.5 EndY=-10.1 EndZ=0
    g55: LineSegment StartX=-1.5 StartY=-26.1 StartZ=0 EndX=1.5 EndY=-26.1 EndZ=0
    g56: LineSegment StartX=1.5 StartY=-26.1 StartZ=0 EndX=1.5 EndY=-33.9 EndZ=0
    g57: LineSegment StartX=1.5 StartY=-33.9 StartZ=0 EndX=-1.5 EndY=-33.9 EndZ=0
    g58: LineSegment StartX=-1.5 StartY=-33.9 StartZ=0 EndX=-1.5 EndY=-26.1 EndZ=0
    g59: LineSegment [constr] StartX=0 StartY=-22 StartZ=0 EndX=0 EndY=-14 EndZ=0
    g60: LineSegment [constr] StartX=0 StartY=-22 StartZ=0 EndX=0 EndY=-30 EndZ=0
    g61: LineSegment StartX=-22 StartY=0 StartZ=0 EndX=-22 EndY=-10 EndZ=0
    g62: LineSegment StartX=-22 StartY=-10 StartZ=0 EndX=-17.5 EndY=-10 EndZ=0
    g63: LineSegment StartX=-17.5 StartY=-10 StartZ=0 EndX=-17.5 EndY=-30.5 EndZ=0
    g64: LineSegment StartX=-17.5 StartY=-30.5 StartZ=0 EndX=-20.5 EndY=-30.5 EndZ=0
    g65: LineSegment StartX=-20.5 StartY=-30.5 StartZ=0 EndX=-20.5 EndY=-40.5 EndZ=0
    g66: LineSegment StartX=-20.5 StartY=-40.5 StartZ=0 EndX=-17.5 EndY=-40.5 EndZ=0
    g67: LineSegment StartX=-17.5 StartY=-40.5 StartZ=0 EndX=-17.5 EndY=-61 EndZ=0
    g68: LineSegment StartX=14 StartY=-106 StartZ=0 EndX=22 EndY=-106 EndZ=0
    g69: LineSegment StartX=-22 StartY=-106 StartZ=0 EndX=-14 EndY=-106 EndZ=0
    g70: LineSegment StartX=16.5 StartY=-47 StartZ=0 EndX=16.5 EndY=-37 EndZ=0
    g71: LineSegment StartX=-22 StartY=-106 StartZ=0 EndX=-22 EndY=-61 EndZ=0
    g72: LineSegment StartX=-22 StartY=-61 StartZ=0 EndX=-17.5 EndY=-61 EndZ=0
    g73: LineSegment StartX=22 StartY=-106 StartZ=0 EndX=22 EndY=-61 EndZ=0
    g74: LineSegment StartX=22 StartY=-61 StartZ=0 EndX=16.5 EndY=-61 EndZ=0
    g75: Circle CenterX=-17.5 CenterY=-65.5 CenterZ=0 NormalX=0 NormalY=0 NormalZ=1 AngleXU=0 Radius=1.5
    g76: Circle CenterX=17.5 CenterY=-65.5 CenterZ=0 NormalX=0 NormalY=0 NormalZ=1 AngleXU=0 Radius=1.5
    g77: Circle CenterX=12.5 CenterY=-73 CenterZ=0 NormalX=0 NormalY=0 NormalZ=1 AngleXU=0 Radius=1.5
    g78: Circle CenterX=10 CenterY=-78 CenterZ=0 NormalX=0 NormalY=0 NormalZ=1 AngleXU=0 Radius=1.5
    g79: Circle CenterX=-10 CenterY=-78 CenterZ=0 NormalX=0 NormalY=0 NormalZ=1 AngleXU=0 Radius=1.5
    g80: Circle CenterX=-12.5 CenterY=-73 CenterZ=0 NormalX=0 NormalY=0 NormalZ=1 AngleXU=0 Radius=1.5
    g81: Circle CenterX=12.5 CenterY=-93 CenterZ=0 NormalX=0 NormalY=0 NormalZ=1 AngleXU=0 Radius=1.5
    g82: Circle CenterX=10 CenterY=-88 CenterZ=0 NormalX=0 NormalY=0 NormalZ=1 AngleXU=0 Radius=1.5
    g83: Circle CenterX=-10 CenterY=-88 CenterZ=0 NormalX=0 NormalY=0 NormalZ=1 AngleXU=0 Radius=1.5
    g84: Circle CenterX=-12.5 CenterY=-93 CenterZ=0 NormalX=0 NormalY=0 NormalZ=1 AngleXU=0 Radius=1.5
    g85: Circle CenterX=-17.5 CenterY=-100.5 CenterZ=0 NormalX=0 NormalY=0 NormalZ=1 AngleXU=0 Radius=1.5
    g86: Circle CenterX=17.5 CenterY=-100.5 CenterZ=0 NormalX=0 NormalY=0 NormalZ=1 AngleXU=0 Radius=1.5
    g87: LineSegment [constr] StartX=-17.5 StartY=-65.5 StartZ=0 EndX=17.5 EndY=-65.5 EndZ=0
    g88: LineSegment [constr] StartX=17.5 StartY=-65.5 StartZ=0 EndX=17.5 EndY=-100.5 EndZ=0
    g89: LineSegment [constr] StartX=17.5 StartY=-100.5 StartZ=0 EndX=-17.5 EndY=-100.5 EndZ=0
    g90: LineSegment [constr] StartX=-17.5 StartY=-100.5 StartZ=0 EndX=-17.5 EndY=-65.5 EndZ=0
    g91: LineSegment [constr] StartX=-12.5 StartY=-73 StartZ=0 EndX=12.5 EndY=-73 EndZ=0
    g92: LineSegment [constr] StartX=12.5 StartY=-73 StartZ=0 EndX=12.5 EndY=-93 EndZ=0
    g93: LineSegment [constr] StartX=12.5 StartY=-93 StartZ=0 EndX=-12.5 EndY=-93 EndZ=0
    g94: LineSegment [constr] StartX=-12.5 StartY=-93 StartZ=0 EndX=-12.5 EndY=-73 EndZ=0
    g95: LineSegment [constr] StartX=-10 StartY=-78 StartZ=0 EndX=10 EndY=-78 EndZ=0
    g96: LineSegment [constr] StartX=10 StartY=-78 StartZ=0 EndX=10 EndY=-88 EndZ=0
    g97: LineSegment [constr] StartX=10 StartY=-88 StartZ=0 EndX=-10 EndY=-88 EndZ=0
    g98: LineSegment [constr] StartX=-10 StartY=-88 StartZ=0 EndX=-10 EndY=-78 EndZ=0
    g99: GeomPoint X=0 Y=-83 Z=0
  constraints (282):
    c: Horizontal(g0)
    c: Coincident(g0,g1)
    c: Vertical(g1)
    c: Coincident(g1,g2)
    c: Horizontal(g2)
    c: Coincident(g2,g3)
    c: Vertical(g3)
    c: Coincident(g3,g4)
    c: Horizontal(g4)
    c: Coincident(g4,g5)
    c: Vertical(g5)
    c: Coincident(g5,g6)
    c: Horizontal(g6)
    c: Coincident(g6,g7)
    c: Vertical(g7)
    c: Coincident(g7,g8)
    c: Horizontal(g8)
    c: Vertical(g9)
    c: Coincident(g9,g10)
    c: Horizontal(g10)
    c: Coincident(g10,g11)
    c: Vertical(g11)
    c: Vertical(g12)
    c: Coincident(g12,g13)
    c: Coincident(g13,g14)
    c: Vertical(g14)
    c: Horizontal(g13)
    c: Equal(g2,g6)
    c: Equal(g6,g10)
    c: Equal(g10,g13)
    c: Equal(g0,g8)
    c: Equal(g1,g3)
    c: Equal(g3,g5)
    c: Equal(g5,g7)
    c: Equal(g7,g9)
    c: Equal(g9,g11)
    c: Equal(g11,g12)
    c: Equal(g12,g14)
    c: Horizontal(g15)
    c: Coincident(g15,g16)
    c: Vertical(g16)
    c: Coincident(g16,g17)
    c: Horizontal(g17)
    c: Horizontal(g18)
    c: Coincident(g18,g19)
    c: Vertical(g19)
    c: Coincident(g19,g20)
    c: Horizontal(g20)
    c: Horizontal(g21)
    c: Coincident(g21,g22)
    c: Coincident(g22,g8)
    c: Vertical(g22)
    c: Equal(g20,g18)
    c: Equal(g18,g17)
    c: Equal(g17,g15)
    c: Equal(g16,g19)
    c: DistanceY(g1,g1) = 3
    c: DistanceX(g0,g0) = 8
    c: DistanceX(g4,g4) = 8
    c: DistanceX(g2,g2) = 10
    c: DistanceX(g20,g20) = 3
    c: Coincident(g12,g23)
    c: Horizontal(g23)
    c: Coincident(g23,g24)
    c: Vertical(g24)
    c: Coincident(g24,g25)
    c: Horizontal(g25)
    c: Coincident(g25,g26)
    c: Vertical(g26)
    c: Coincident(g26,g27)
    c: Horizontal(g27)
    c: Coincident(g27,g28)
    c: Coincident(g28,g29)
    c: Horizontal(g29)
    c: Coincident(g29,g30)
    c: Vertical(g30)
    c: Coincident(g30,g31)
    c: Horizontal(g31)
    c: Coincident(g31,g32)
    c: Vertical(g32)
    c: Coincident(g32,g33)
    c: Horizontal(g33)
    c: Coincident(g33,g34)
    c: Vertical(g34)
    c: Coincident(g34,g35)
    c: Coincident(g35,g11)
    c: Horizontal(g35)
    c: Equal(g23,g35)
    c: Equal(g34,g24)
    c: Equal(g25,g27)
    c: Equal(g27,g31)
    c: Equal(g31,g33)
    c: Vertical(g28)
    c: DistanceX(g29,g29) = 3
    c: DistanceY(g19,g19) = 10
    c: Vertical(g36)
    c: Coincident(g36,g37)
    c: Horizontal(g37)
    c: Coincident(g37,g38)
    c: Vertical(g38)
    c: Coincident(g38,g39)
    c: Horizontal(g39)
    c: Coincident(g39,g40)
    c: Vertical(g40)
    c: Coincident(g40,g41)
    c: Horizontal(g41)
    c: Coincident(g41,g42)
    c: Vertical(g42)
    c: Coincident(g42,g43)
    c: Horizontal(g43)
    c: Coincident(g43,g44)
    c: Vertical(g44)
    c: Coincident(g44,g45)
    c: Horizontal(g45)
    c: Coincident(g45,g46)
    c: Vertical(g46)
    c: Coincident(g46,g47)
    c: Horizontal(g47)
    c: Coincident(g48,g20)
    c: Vertical(g48)
    c: Equal(g37,g47)
    c: Equal(g46,g44)
    c: Equal(g44,g40)
    c: Equal(g40,g38)
    c: DistanceY(g42,g42) = 3
    c: Coincident(g15,g49)
    c: Vertical(g49)
    c: Equal(g26,g32)
    c: Equal(g39,g45)
    c: Equal(g28,g30)
    c: Equal(g41,g43)
    c: DistanceY(g26,g26) = 2.3
    c: DistanceX(g27,g27) = 1.25
    c: DistanceY(g24,g24) = 5
    c: DistanceY(g28,g28) = 3
    c: DistanceX(g21,g21) = 5.5
    c: PointOnObject(g50,g-2)
    c: DistanceY(g50,g4) = 22
    c: Coincident(g51,g52)
    c: Coincident(g52,g53)
    c: Coincident(g53,g54)
    c: Coincident(g54,g51)
    c: Horizontal(g51)
    c: Horizontal(g53)
    c: Vertical(g52)
    c: Vertical(g54)
    c: Coincident(g55,g56)
    c: Coincident(g56,g57)
    c: Coincident(g57,g58)
    c: Coincident(g58,g55)
    c: Horizontal(g55)
    c: Horizontal(g57)
    c: Vertical(g56)
    c: Vertical(g58)
    c: Coincident(g59,g50)
    c: Coincident(g60,g50)
    c: Vertical(g60)
    c: Equal(g59,g60)
    c: Symmetric(g55,g56,g60)
    c: Symmetric(g51,g52,g59)
    c: Equal(g54,g58)
    c: Equal(g53,g55)
    c: DistanceX(g51,g51) = 3
    c: DistanceY(g54,g54) = 7.8
    c: DistanceY(g59,g59) = 8
    c: DistanceY(g22,g22) = 10
    c: Coincident(g0,g61)
    c: Vertical(g61)
    c: Coincident(g61,g62)
    c: Horizontal(g62)
    c: Coincident(g62,g63)
    c: Vertical(g63)
    c: Coincident(g63,g64)
    c: Horizontal(g64)
    c: Coincident(g64,g65)
    c: Vertical(g65)
    c: Coincident(g65,g66)
    c: Horizontal(g66)
    c: Equal(g61,g22)
    c: Equal(g19,g65)
    c: Equal(g64,g66)
    c: Coincident(g66,g67)
    c: Vertical(g67)
    c: Symmetric(g4,g3,g-1)
    c: Coincident(g9,g68)
    c: Horizontal(g68)
    c: Coincident(g69,g14)
    c: Horizontal(g69)
    c: Coincident(g70,g17)
    c: Vertical(g70)
    c: DistanceY(g49,g49) = 4
    c: Coincident(g48,g21)
    c: Coincident(g18,g36)
    c: Equal(g36,g70)
    c: DistanceY(g48,g48) = 4
    c: Equal(g68,g69)
    c: DistanceX(g23,g23) = 2.5
    c: Vertical(g59)
    c: Radius(g50) = 1.5
    c: DistanceY(g69,g0) = 106
    c: Coincident(g71,g69)
    c: Vertical(g71)
    c: Coincident(g72,g71)
    c: Coincident(g73,g68)
    c: Vertical(g73)
    c: Coincident(g74,g73)
    c: Horizontal(g74)
    c: Horizontal(g72)
    c: Equal(g0,g69)
    c: Coincident(g74,g49)
    c: DistanceY(g73,g73) = 45
    c: Coincident(g47,g70)
    c: Equal(g62,g72)
    c: Equal(g45,g32)
    c: Equal(g43,g30)
    c: Equal(g46,g33)
    c: Equal(g47,g34)
    c: Coincident(g87,g88)
    c: Coincident(g88,g89)
    c: Coincident(g89,g90)
    c: Coincident(g90,g87)
    c: Horizontal(g87)
    c: Horizontal(g89)
    c: Vertical(g88)
    c: Vertical(g90)
    c: Coincident(g87,g75)
    c: Coincident(g86,g88)
    c: Coincident(g85,g89)
    c: Coincident(g76,g87)
    c: Equal(g75,g76)
    c: Equal(g76,g77)
    c: Equal(g77,g80)
    c: Equal(g80,g79)
    c: Equal(g79,g78)
    c: Equal(g78,g82)
    c: Equal(g82,g83)
    c: Equal(g83,g84)
    c: Equal(g84,g81)
    c: Equal(g81,g86)
    c: Equal(g86,g85)
    c: Coincident(g91,g92)
    c: Coincident(g92,g93)
    c: Coincident(g93,g94)
    c: Coincident(g94,g91)
    c: Horizontal(g91)
    c: Horizontal(g93)
    c: Vertical(g92)
    c: Vertical(g94)
    c: Coincident(g91,g80)
    c: Coincident(g92,g81)
    c: Coincident(g95,g96)
    c: Coincident(g96,g97)
    c: Coincident(g97,g98)
    c: Coincident(g98,g95)
    c: Horizontal(g95)
    c: Horizontal(g97)
    c: Vertical(g96)
    c: Vertical(g98)
    c: Coincident(g95,g79)
    c: Coincident(g96,g82)
    c: Coincident(g77,g91)
    c: Coincident(g84,g93)
    c: Coincident(g83,g97)
    c: Coincident(g78,g95)
    c: PointOnObject(g99,g-2)
    c: Symmetric(g79,g82,g99)
    c: Symmetric(g80,g81,g99)
    c: Symmetric(g75,g86,g99)
    c: Equal(g87,g90)
    c: DistanceX(g87,g87) = 35
    c: Radius(g75) = 1.5
    c: DistanceX(g91,g91) = 25
    c: DistanceX(g95,g95) = 20
    c: DistanceY(g98,g98) = 10
    c: DistanceY(g94,g94) = 20
    c: DistanceY(g69,g99) = 23
    c: Coincident(g72,g67)
    c: Equal(g74,g21)
    c: DistanceX(g62,g62) = 4.5
    c: Equal(g64,g1)
    c: Equal(g71,g73)
    c: Equal(g63,g67)
FEATURE [PartDesign::Pad] Pad016
  Length = 3
  Length2 = 100
  Placement = pos=(192.5,0,0) rot=(0.707107,0,-0.707107;3.14159rad)
  Profile = -> Sketch001002011
  Refine = true
  Reversed = true
  Type = 0
FEATURE [PartDesign::Body] Body016  label="Body R001"
  Group = -> [Sketch001002011,Pad016]
  Origin = -> Origin019
  Tip = -> Pad016
FEATURE [Sketcher::SketchObject] Sketch001002018  label="Sketch Deckel"
  Placement = pos=(0,45,17.5) rot=(0,0,-1;1.5708rad)
  sketch-geometry (120):
    g0: LineSegment StartX=-61 StartY=-198.5 StartZ=0 EndX=0 EndY=-198.5 EndZ=0
    g1: LineSegment [constr] StartX=0 StartY=-198.5 StartZ=0 EndX=0 EndY=198.5 EndZ=0
    g2: LineSegment [constr] StartX=0 StartY=198.5 StartZ=0 EndX=-16 EndY=198.5 EndZ=0
    g3: LineSegment StartX=-35.4 StartY=-192.5 StartZ=0 EndX=-25.6 EndY=-192.5 EndZ=0
    g4: LineSegment StartX=-25.6 StartY=-192.5 StartZ=0 EndX=-25.6 EndY=-195.5 EndZ=0
    g5: LineSegment StartX=-25.6 StartY=-195.5 StartZ=0 EndX=-35.4 EndY=-195.5 EndZ=0
    g6: LineSegment StartX=-35.4 StartY=-195.5 StartZ=0 EndX=-35.4 EndY=-192.5 EndZ=0
    g7: LineSegment StartX=4.6 StartY=195.5 StartZ=0 EndX=14.4 EndY=195.5 EndZ=0
    g8: LineSegment StartX=14.4 StartY=195.5 StartZ=0 EndX=14.4 EndY=192.5 EndZ=0
    g9: LineSegment StartX=14.4 StartY=192.5 StartZ=0 EndX=4.6 EndY=192.5 EndZ=0
    g10: LineSegment StartX=4.6 StartY=192.5 StartZ=0 EndX=4.6 EndY=195.5 EndZ=0
    g11: LineSegment [constr] StartX=-16 StartY=198.5 StartZ=0 EndX=-16 EndY=195.5 EndZ=0
    g12: LineSegment [constr] StartX=-16 StartY=195.5 StartZ=0 EndX=4.6 EndY=195.5 EndZ=0
    g13: LineSegment [constr] StartX=14.4 StartY=195.5 StartZ=0 EndX=35 EndY=195.5 EndZ=0
    g14: LineSegment [constr] StartX=35 StartY=195.5 StartZ=0 EndX=35 EndY=198.5 EndZ=0
    g15: LineSegment [constr] StartX=-25.6 StartY=-195.5 StartZ=0 EndX=0 EndY=-195.5 EndZ=0
    g16: LineSegment [constr] StartX=0 StartY=-195.5 StartZ=0 EndX=0 EndY=-198.5 EndZ=0
    g17: LineSegment [constr] StartX=-35.4 StartY=-195.5 StartZ=0 EndX=-61 EndY=-195.5 EndZ=0
    g18: LineSegment [constr] StartX=-61 StartY=-195.5 StartZ=0 EndX=-61 EndY=-198.5 EndZ=0
    g19: LineSegment StartX=-18.6 StartY=-7.5 StartZ=0 EndX=-18.6 EndY=-5.5 EndZ=0
    g20: LineSegment StartX=-18.6 StartY=-5.5 StartZ=0 EndX=9.4 EndY=-5.5 EndZ=0
    g21: LineSegment StartX=9.4 StartY=-5.5 StartZ=0 EndX=9.4 EndY=27.5 EndZ=0
    g22: LineSegment StartX=9.4 StartY=27.5 StartZ=0 EndX=11.4 EndY=27.5 EndZ=0
    g23: LineSegment StartX=11.4 StartY=27.5 StartZ=0 EndX=11.4 EndY=-7.5 EndZ=0
    g24: LineSegment StartX=11.4 StartY=-7.5 StartZ=0 EndX=-18.6 EndY=-7.5 EndZ=0
    g25: LineSegment StartX=-21.6 StartY=-7.5 StartZ=0 EndX=-23.6 EndY=-7.5 EndZ=0
    g26: LineSegment StartX=-23.6 StartY=-7.5 StartZ=0 EndX=-23.6 EndY=27.5 EndZ=0
    g27: LineSegment StartX=-23.6 StartY=27.5 StartZ=0 EndX=6.4 EndY=27.5 EndZ=0
    g28: LineSegment StartX=6.4 StartY=27.5 StartZ=0 EndX=6.4 EndY=25.5 EndZ=0
    g29: LineSegment StartX=6.4 StartY=25.5 StartZ=0 EndX=-21.6 EndY=25.5 EndZ=0
    g30: LineSegment StartX=-21.6 StartY=25.5 StartZ=0 EndX=-21.6 EndY=-7.5 EndZ=0
    g31: LineSegment [constr] StartX=-21.6 StartY=-7.5 StartZ=0 EndX=-18.6 EndY=-7.5 EndZ=0
    g32: LineSegment [constr] StartX=6.4 StartY=27.5 StartZ=0 EndX=9.4 EndY=27.5 EndZ=0
    g33: LineSegment StartX=-13.6 StartY=-1 StartZ=0 EndX=-17.1 EndY=-1 EndZ=0
    g34: LineSegment StartX=-17.1 StartY=-1 StartZ=0 EndX=-17.1 EndY=21 EndZ=0
    g35: LineSegment StartX=-17.1 StartY=21 StartZ=0 EndX=-13.6 EndY=21 EndZ=0
    g36: LineSegment StartX=-13.6 StartY=21 StartZ=0 EndX=-13.6 EndY=8 EndZ=0
    g37: LineSegment StartX=-13.6 StartY=8 StartZ=0 EndX=4.9 EndY=8 EndZ=0
    g38: LineSegment StartX=4.9 StartY=8 StartZ=0 EndX=4.9 EndY=4.5 EndZ=0
    g39: LineSegment StartX=4.9 StartY=4.5 StartZ=0 EndX=-13.6 EndY=4.5 EndZ=0
    g40: LineSegment StartX=-13.6 StartY=4.5 StartZ=0 EndX=-13.6 EndY=-1 EndZ=0
    g41: LineSegment StartX=-9.6 StartY=12 StartZ=0 EndX=4.9 EndY=12 EndZ=0
    g42: LineSegment StartX=4.9 StartY=12 StartZ=0 EndX=4.9 EndY=15.5 EndZ=0
    g43: LineSegment StartX=4.9 StartY=15.5 StartZ=0 EndX=-2.6 EndY=15.5 EndZ=0
    g44: LineSegment StartX=-2.6 StartY=15.5 StartZ=0 EndX=-2.6 EndY=21 EndZ=0
    g45: LineSegment StartX=-2.6 StartY=21 StartZ=0 EndX=-6.1 EndY=21 EndZ=0
    g46: LineSegment StartX=-6.1 StartY=21 StartZ=0 EndX=-6.1 EndY=15.5 EndZ=0
    g47: LineSegment StartX=-6.1 StartY=15.5 StartZ=0 EndX=-9.6 EndY=15.5 EndZ=0
    g48: LineSegment StartX=-9.6 StartY=15.5 StartZ=0 EndX=-9.6 EndY=12 EndZ=0
    g49: LineSegment [constr] StartX=4.9 StartY=12 StartZ=0 EndX=4.9 EndY=8 EndZ=0
    g50: LineSegment [constr] StartX=-17.1 StartY=-1 StartZ=0 EndX=-21.6 EndY=-1 EndZ=0
    g51: LineSegment [constr] StartX=-17.1 StartY=-1 StartZ=0 EndX=-17.1 EndY=-5.5 EndZ=0
    g52: LineSegment [constr] StartX=4.9 StartY=4.5 StartZ=0 EndX=9.4 EndY=4.5 EndZ=0
    g53: LineSegment [constr] StartX=-17.1 StartY=21 StartZ=0 EndX=-17.1 EndY=25.5 EndZ=0
    g54: LineSegment [constr] StartX=-9.6 StartY=12 StartZ=0 EndX=-13.6 EndY=12 EndZ=0
    g55: LineSegment [constr] StartX=-13.6 StartY=21 StartZ=0 EndX=-6.1 EndY=21 EndZ=0
    g56: LineSegment [constr] StartX=-23.6 StartY=-7.5 StartZ=0 EndX=11.4 EndY=-7.5 EndZ=0
    g57: LineSegment StartX=-61 StartY=108.5 StartZ=0 EndX=-61 EndY=98.5 EndZ=0
    g58: LineSegment StartX=-61 StartY=98.5 StartZ=0 EndX=-63.5 EndY=98.5 EndZ=0
    g59: LineSegment StartX=-63.5 StartY=98.5 StartZ=0 EndX=-63.5 EndY=88.5 EndZ=0
    g60: LineSegment StartX=-63.5 StartY=88.5 StartZ=0 EndX=-61 EndY=88.5 EndZ=0
    g61: LineSegment StartX=-61 StartY=88.5 StartZ=0 EndX=-61 EndY=-168.5 EndZ=0
    g62: LineSegment StartX=-61 StartY=-168.5 StartZ=0 EndX=-63.5 EndY=-168.5 EndZ=0
    g63: LineSegment StartX=-63.5 StartY=-168.5 StartZ=0 EndX=-63.5 EndY=-178.5 EndZ=0
    g64: LineSegment StartX=-63.5 StartY=-178.5 StartZ=0 EndX=-61 EndY=-178.5 EndZ=0
    g65: LineSegment StartX=-61 StartY=-178.5 StartZ=0 EndX=-61 EndY=-198.5 EndZ=0
    g66: LineSegment StartX=0 StartY=-198.5 StartZ=0 EndX=0 EndY=-108.5 EndZ=0
    g67: LineSegment StartX=0 StartY=-108.5 StartZ=0 EndX=35 EndY=-108.5 EndZ=0
    g68: LineSegment StartX=35 StartY=-108.5 StartZ=0 EndX=35 EndY=198.5 EndZ=0
    g69: LineSegment StartX=35 StartY=198.5 StartZ=0 EndX=-16 EndY=198.5 EndZ=0
    g70: LineSegment [constr] StartX=35 StartY=10 StartZ=0 EndX=21.4 EndY=10 EndZ=0
    g71: LineSegment [constr] StartX=21.4 StartY=10 StartZ=0 EndX=11.4 EndY=10 EndZ=0
    g72: LineSegment [constr] StartX=-36.6 StartY=34.5 StartZ=0 EndX=21.4 EndY=34.5 EndZ=0
    g73: LineSegment [constr] StartX=21.4 StartY=34.5 StartZ=0 EndX=21.4 EndY=-14.5 EndZ=0
    g74: LineSegment [constr] StartX=21.4 StartY=-14.5 StartZ=0 EndX=-36.6 EndY=-14.5 EndZ=0
    g75: LineSegment [constr] StartX=-36.6 StartY=-14.5 StartZ=0 EndX=-36.6 EndY=34.5 EndZ=0
    g76: Circle [constr] CenterX=-36.6 CenterY=34.5 CenterZ=0 NormalX=0 NormalY=0 NormalZ=1 AngleXU=0 Radius=1.375
    g77: Circle [constr] CenterX=21.4 CenterY=34.5 CenterZ=0 NormalX=0 NormalY=0 NormalZ=1 AngleXU=0 Radius=1.375
    g78: Circle [constr] CenterX=21.4 CenterY=-14.5 CenterZ=0 NormalX=0 NormalY=0 NormalZ=1 AngleXU=0 Radius=1.375
    g79: Circle [constr] CenterX=-36.6 CenterY=-14.5 CenterZ=0 NormalX=0 NormalY=0 NormalZ=1 AngleXU=0 Radius=1.375
    g80: LineSegment StartX=-16 StartY=198.5 StartZ=0 EndX=-16 EndY=108.5 EndZ=0
    g81: LineSegment StartX=-16 StartY=108.5 StartZ=0 EndX=-61 EndY=108.5 EndZ=0
    g82: LineSegment [constr] StartX=22.1 StartY=-13.5 StartZ=0 EndX=31.9 EndY=-13.5 EndZ=0
    g83: LineSegment [constr] StartX=31.9 StartY=-13.5 StartZ=0 EndX=31.9 EndY=-16.5 EndZ=0
    g84: LineSegment [constr] StartX=31.9 StartY=-16.5 StartZ=0 EndX=22.1 EndY=-16.5 EndZ=0
    g85: LineSegment [constr] StartX=22.1 StartY=-16.5 StartZ=0 EndX=22.1 EndY=-13.5 EndZ=0
    g86: LineSegment [constr] StartX=-33.9 StartY=-13.5 StartZ=0 EndX=-24.1 EndY=-13.5 EndZ=0
    g87: LineSegment [constr] StartX=-24.1 StartY=-13.5 StartZ=0 EndX=-24.1 EndY=-16.5 EndZ=0
    g88: LineSegment [constr] StartX=-24.1 StartY=-16.5 StartZ=0 EndX=-33.9 EndY=-16.5 EndZ=0
    g89: LineSegment [constr] StartX=-33.9 StartY=-16.5 StartZ=0 EndX=-33.9 EndY=-13.5 EndZ=0
    g90: LineSegment [constr] StartX=-24.1 StartY=-13.5 StartZ=0 EndX=22.1 EndY=-13.5 EndZ=0
    g91: LineSegment [constr] StartX=-50.1 StartY=-37.5 StartZ=0 EndX=24.9 EndY=-37.5 EndZ=0
    g92: LineSegment [constr] StartX=24.9 StartY=-37.5 StartZ=0 EndX=24.9 EndY=-97.5 EndZ=0
    g93: LineSegment [constr] StartX=24.9 StartY=-97.5 StartZ=0 EndX=-50.1 EndY=-97.5 EndZ=0
    g94: LineSegment [constr] StartX=-50.1 StartY=-97.5 StartZ=0 EndX=-50.1 EndY=-37.5 EndZ=0
    g95: LineSegment [constr] StartX=-5.1 StartY=182.5 StartZ=0 EndX=24.9 EndY=182.5 EndZ=0
    g96: LineSegment [constr] StartX=24.9 StartY=182.5 StartZ=0 EndX=24.9 EndY=77.5 EndZ=0
    g97: LineSegment [constr] StartX=24.9 StartY=77.5 StartZ=0 EndX=-50.1 EndY=77.5 EndZ=0
    g98: LineSegment [constr] StartX=-50.1 StartY=77.5 StartZ=0 EndX=-50.1 EndY=97.5 EndZ=0
    g99: LineSegment [constr] StartX=-50.1 StartY=97.5 StartZ=0 EndX=-5.1 EndY=97.5 EndZ=0
    g100: LineSegment [constr] StartX=-5.1 StartY=97.5 StartZ=0 EndX=-5.1 EndY=182.5 EndZ=0
    g101: Circle CenterX=-50.1 CenterY=97.5 CenterZ=0 NormalX=0 NormalY=0 NormalZ=1 AngleXU=0 Radius=1.5
    g102: Circle CenterX=-5.1 CenterY=182.5 CenterZ=0 NormalX=0 NormalY=0 NormalZ=1 AngleXU=0 Radius=1.5
    g103: Circle CenterX=24.9 CenterY=77.5 CenterZ=0 NormalX=0 NormalY=0 NormalZ=1 AngleXU=0 Radius=1.5
    g104: Circle CenterX=-10.1 CenterY=-182.5 CenterZ=0 NormalX=0 NormalY=0 NormalZ=1 AngleXU=0 Radius=1.5
    g105: Circle CenterX=24.9 CenterY=-97.5 CenterZ=0 NormalX=0 NormalY=0 NormalZ=1 AngleXU=0 Radius=1.5
    g106: LineSegment [constr] StartX=-5.1 StartY=182.5 StartZ=0 EndX=-5.1 EndY=198.5 EndZ=0
    g107: LineSegment [constr] StartX=-50.1 StartY=97.5 StartZ=0 EndX=-50.1 EndY=108.5 EndZ=0
    g108: LineSegment [constr] StartX=24.9 StartY=-97.5 StartZ=0 EndX=24.9 EndY=-108.5 EndZ=0
    g109: LineSegment [constr] StartX=-50.1 StartY=77.5 StartZ=0 EndX=-50.1 EndY=-37.5 EndZ=0
    g110: LineSegment [constr] StartX=-5.1 StartY=182.5 StartZ=0 EndX=-16 EndY=182.5 EndZ=0
    g111: LineSegment [constr] StartX=24.9 StartY=182.5 StartZ=0 EndX=35 EndY=182.5 EndZ=0
    g112: LineSegment [constr] StartX=24.9 StartY=-97.5 StartZ=0 EndX=35 EndY=-97.5 EndZ=0
    g113: LineSegment [constr] StartX=-50.1 StartY=97.5 StartZ=0 EndX=-61 EndY=97.5 EndZ=0
    g114: GeomPoint X=22.1 Y=-15 Z=0
    g115: LineSegment [constr] StartX=-50.1 StartY=-97.5 StartZ=0 EndX=-50.1 EndY=-182.5 EndZ=0
    g116: LineSegment [constr] StartX=-50.1 StartY=-182.5 StartZ=0 EndX=-10.1 EndY=-182.5 EndZ=0
    g117: LineSegment [constr] StartX=-10.1 StartY=-182.5 StartZ=0 EndX=0 EndY=-182.5 EndZ=0
    g118: LineSegment [constr] StartX=-50.1 StartY=-182.5 StartZ=0 EndX=-50.1 EndY=-198.5 EndZ=0
    g119: LineSegment [constr] StartX=31.9 StartY=-13.5 StartZ=0 EndX=35 EndY=-13.5 EndZ=0
  constraints (335):
    c: Coincident(g0,g1)
    c: Horizontal(g0)
    c: Horizontal(g2)
    c: Vertical(g1)
    c: Coincident(g3,g4)
    c: Coincident(g4,g5)
    c: Coincident(g5,g6)
    c: Coincident(g6,g3)
    c: Horizontal(g3)
    c: Horizontal(g5)
    c: Vertical(g4)
    c: Vertical(g6)
    c: Coincident(g7,g8)
    c: Coincident(g8,g9)
    c: Coincident(g9,g10)
    c: Coincident(g10,g7)
    c: Horizontal(g7)
    c: Horizontal(g9)
    c: Vertical(g8)
    c: Vertical(g10)
    c: Equal(g10,g6)
    c: Equal(g9,g3)
    c: Coincident(g12,g11)
    c: Coincident(g13,g7)
    c: Horizontal(g13)
    c: Coincident(g14,g13)
    c: Coincident(g15,g4)
    c: Horizontal(g15)
    c: Coincident(g16,g15)
    c: Coincident(g16,g0)
    c: Coincident(g18,g17)
    c: Horizontal(g12)
    c: Equal(g11,g14)
    c: Equal(g14,g16)
    c: Equal(g16,g18)
    c: Vertical(g11)
    c: Vertical(g14)
    c: Vertical(g16)
    c: Vertical(g18)
    c: Equal(g12,g13)
    c: Equal(g15,g17)
    c: Coincident(g19,g20)
    c: Coincident(g20,g21)
    c: Coincident(g21,g22)
    c: Coincident(g24,g19)
    c: Coincident(g27,g28)
    c: Coincident(g28,g29)
    c: Coincident(g29,g30)
    c: Coincident(g30,g25)
    c: Coincident(g31,g25)
    c: Coincident(g31,g19)
    c: Coincident(g32,g27)
    c: Coincident(g32,g21)
    c: Equal(g25,g19)
    c: Equal(g19,g28)
    c: Equal(g28,g22)
    c: Equal(g31,g32)
    c: Coincident(g33,g34)
    c: Coincident(g34,g35)
    c: Coincident(g35,g36)
    c: Coincident(g36,g37)
    c: Coincident(g37,g38)
    c: Coincident(g38,g39)
    c: Coincident(g39,g40)
    c: Coincident(g40,g33)
    c: Coincident(g41,g42)
    c: Coincident(g42,g43)
    c: Coincident(g43,g44)
    c: Coincident(g44,g45)
    c: Coincident(g45,g46)
    c: Coincident(g46,g47)
    c: Coincident(g47,g48)
    c: Coincident(g48,g41)
    c: Coincident(g49,g41)
    c: Coincident(g49,g37)
    c: Coincident(g50,g33)
    c: PointOnObject(g50,g30)
    c: Coincident(g51,g33)
    c: PointOnObject(g51,g20)
    c: Coincident(g52,g38)
    c: PointOnObject(g52,g21)
    c: Coincident(g53,g34)
    c: PointOnObject(g53,g29)
    c: Equal(g51,g50)
    c: Equal(g50,g53)
    c: Equal(g53,g52)
    c: Coincident(g54,g41)
    c: PointOnObject(g54,g36)
    c: Coincident(g55,g35)
    c: Coincident(g45,g55)
    c: Equal(g54,g49)
    c: Equal(g33,g35)
    c: Equal(g35,g48)
    c: Equal(g48,g45)
    c: Equal(g45,g42)
    c: Equal(g42,g38)
    c: Equal(g40,g46)
    c: Equal(g56,g26)
    c: Coincident(g25,g26)
    c: Coincident(g25,g56)
    c: Coincident(g23,g24)
    c: Coincident(g23,g56)
    c: Coincident(g22,g23)
    c: Coincident(g26,g27)
    c: DistanceY(g26,g26) = 35
    c: Vertical(g26)
    c: Vertical(g30)
    c: Horizontal(g27)
    c: Horizontal(g29)
    c: Horizontal(g32)
    c: Horizontal(g22)
    c: Horizontal(g35)
    c: Horizontal(g55)
    c: Horizontal(g45)
    c: Horizontal(g47)
    c: Horizontal(g43)
    c: Horizontal(g41)
    c: Horizontal(g54)
    c: Horizontal(g52)
    c: Horizontal(g37)
    c: Horizontal(g39)
    c: Horizontal(g33)
    c: Horizontal(g50)
    c: Horizontal(g31)
    c: Horizontal(g25)
    c: Horizontal(g24)
    c: Vertical(g34)
    c: Vertical(g36)
    c: Vertical(g40)
    c: Vertical(g51)
    c: Vertical(g19)
    c: Vertical(g21)
    c: Vertical(g38)
    c: Vertical(g42)
    c: Vertical(g48)
    c: Vertical(g46)
    c: Vertical(g44)
    c: Vertical(g28)
    c: Horizontal(g20)
    c: Vertical(g49)
    c: Vertical(g53)
    c: DistanceX(g22,g22) = 2
    c: DistanceX(g32,g32) = 3
    c: DistanceX(g35,g35) = 3.5
    c: DistanceX(g54,g54) = 4
    c: DistanceX(g47,g47) = 3.5
    c: DistanceY(g53,g53) = 4.5
    c: Symmetric(g1,g0,g-1)
    c: Vertical(g57)
    c: Coincident(g57,g58)
    c: Horizontal(g58)
    c: Coincident(g58,g59)
    c: Vertical(g59)
    c: Coincident(g59,g60)
    c: Horizontal(g60)
    c: Coincident(g60,g61)
    c: Coincident(g61,g62)
    c: Horizontal(g62)
    c: Coincident(g62,g63)
    c: Vertical(g63)
    c: Coincident(g63,g64)
    c: Horizontal(g64)
    c: Coincident(g64,g65)
    c: Vertical(g65)
    c: Equal(g58,g60)
    c: Equal(g60,g62)
    c: Equal(g62,g64)
    c: DistanceY(g59,g59) = 10
    c: DistanceX(g58,g58) = 2.5
    c: Equal(g59,g63)
    c: Coincident(g0,g66)
    c: Vertical(g66)
    c: Coincident(g66,g67)
    c: Horizontal(g67)
    c: Coincident(g67,g68)
    c: Vertical(g68)
    c: Coincident(g68,g69)
    c: Coincident(g1,g2)
    c: Coincident(g14,g68)
    c: Vertical(g23)
    c: PointOnObject(g70,g68)
    c: Horizontal(g70)
    c: DistanceY(g70,g68) = 188.5
    c: DistanceX(g70,g70) = 13.6
    c: Horizontal(g71)
    c: Symmetric(g22,g23,g71)
    c: DistanceX(g71,g71) = 10
    c: Coincident(g72,g73)
    c: Coincident(g73,g74)
    c: Coincident(g74,g75)
    c: Coincident(g75,g72)
    c: Horizontal(g72)
    c: Horizontal(g74)
    c: Vertical(g73)
    c: Vertical(g75)
    c: DistanceX(g72,g72) = 58
    c: DistanceY(g75,g75) = 49
    c: Symmetric(g72,g73,g70)
    c: Coincident(g76,g72)
    c: Coincident(g77,g72)
    c: Coincident(g78,g73)
    c: Coincident(g79,g74)
    c: Equal(g76,g77)
    c: Equal(g77,g78)
    c: Equal(g78,g79)
    c: Radius(g76) = 1.375
    c: DistanceX(g0,g0) = 61
    c: DistanceX(g67,g67) = 35
    c: Vertical(g80)
    c: Coincident(g80,g81)
    c: Horizontal(g81)
    c: DistanceX(g81,g81) = 45
    c: DistanceY(g66,g66) = 90
    c: Coincident(g82,g83)
    c: Coincident(g83,g84)
    c: Coincident(g84,g85)
    c: Coincident(g85,g82)
    c: Horizontal(g82)
    c: Horizontal(g84)
    c: Vertical(g83)
    c: Vertical(g85)
    c: Coincident(g86,g87)
    c: Coincident(g87,g88)
    c: Coincident(g88,g89)
    c: Coincident(g89,g86)
    c: Horizontal(g86)
    c: Horizontal(g88)
    c: Vertical(g87)
    c: Vertical(g89)
    c: Coincident(g90,g86)
    c: Coincident(g90,g82)
    c: Horizontal(g90)
    c: Equal(g86,g82)
    c: Equal(g87,g85)
    c: Coincident(g0,g18)
    c: Coincident(g2,g11)
    c: Coincident(g2,g69)
    c: DistanceY(g-1,g1) = 198.5
    c: Coincident(g57,g81)
    c: Coincident(g80,g69)
    c: Coincident(g65,g0)
    c: Equal(g80,g66)
    c: Coincident(g91,g92)
    c: Coincident(g92,g93)
    c: Coincident(g93,g94)
    c: Horizontal(g91)
    c: Horizontal(g93)
    c: Vertical(g92)
    c: Vertical(g94)
    c: Horizontal(g95)
    c: Coincident(g95,g96)
    c: Vertical(g96)
    c: Coincident(g96,g97)
    c: Horizontal(g97)
    c: Coincident(g97,g98)
    c: Vertical(g98)
    c: Coincident(g98,g99)
    c: Horizontal(g99)
    c: Coincident(g99,g100)
    c: Coincident(g100,g95)
    c: Vertical(g100)
    c: Coincident(g101,g98)
    c: Coincident(g102,g95)
    c: Coincident(g103,g96)
    c: Coincident(g105,g92)
    c: Equal(g102,g101)
    c: Equal(g101,g103)
    c: Equal(g103,g105)
    c: Equal(g105,g104)
    c: DistanceX(g69,g102) = 10.9
    c: Coincident(g106,g102)
    c: PointOnObject(g106,g69)
    c: Vertical(g106)
    c: DistanceY(g106,g106) = 16
    c: Coincident(g107,g101)
    c: PointOnObject(g107,g81)
    c: Vertical(g107)
    c: DistanceY(g98,g98) = 20
    c: Coincident(g108,g105)
    c: PointOnObject(g108,g67)
    c: Vertical(g108)
    c: DistanceY(g94,g94) = 60
    c: Coincident(g109,g97)
    c: Vertical(g109)
    c: Coincident(g110,g102)
    c: PointOnObject(g110,g80)
    c: Horizontal(g110)
    c: Coincident(g111,g95)
    c: PointOnObject(g111,g68)
    c: Horizontal(g111)
    c: Coincident(g112,g105)
    c: PointOnObject(g112,g68)
    c: Horizontal(g112)
    c: Coincident(g113,g101)
    c: PointOnObject(g113,g57)
    c: Horizontal(g113)
    c: Equal(g111,g112)
    c: Equal(g110,g113)
    c: DistanceX(g111,g111) = 10.1
    c: Symmetric(g82,g84,g114)
    c: DistanceY(g114,g-1) = 15
    c: Equal(g107,g108)
    c: Coincident(g71,g70)
    c: DistanceY(g107,g107) = 11
    c: Coincident(g91,g94)
    c: Coincident(g91,g109)
    c: Coincident(g115,g93)
    c: Vertical(g115)
    c: Coincident(g116,g115)
    c: Coincident(g116,g104)
    c: Horizontal(g116)
    c: Coincident(g117,g104)
    c: PointOnObject(g117,g66)
    c: Horizontal(g117)
    c: Coincident(g118,g115)
    c: PointOnObject(g118,g0)
    c: Vertical(g118)
    c: Equal(g117,g112)
    c: Equal(g118,g106)
    c: DistanceX(g86,g86) = 9.8
    c: DistanceX(g90,g90) = 46.2
    c: Coincident(g119,g82)
    c: PointOnObject(g119,g68)
    c: Horizontal(g119)
    c: DistanceX(g119,g119) = 3.1
    c: Coincident(g5,g17)
    c: Radius(g102) = 1.5
    c: Equal(g89,g4)
    c: DistanceX(g7,g7) = 9.8
    c: DistanceY(g10,g10) = 3
    c: Coincident(g7,g12)
    c: DistanceY(g11,g69) = 3
    c: DistanceY(g57,g57) = 10
    c: Vertical(g61)
    c: DistanceY(g65,g65) = 20
FEATURE [PartDesign::Pad] Pad020
  Length = 3
  Length2 = 100
  Placement = pos=(0,45,17.5) rot=(0,0,-1;1.5708rad)
  Profile = -> Sketch001002018
  Refine = true
  Type = 0
FEATURE [PartDesign::Body] Body020  label="Body Deckel"
  Group = -> [Sketch001002018,Pad020]
  Origin = -> Origin026
  Tip = -> Pad020
FEATURE [Part::Fillet] Fillet025  label="Fillet R"
  Base = -> Body016
  Edges = 10 edges r=1.5: [Edge5,Edge8,Edge17,Edge20,Edge29,Edge98,Edge167,Edge176,Edge179,Edge188]
FEATURE [Sketcher::SketchObject] Sketch001002026  label="Sketch Back RP"
  Placement = pos=(0,106,0) rot=(1,0,0;1.5708rad)
  sketch-geometry (84):
    g0: LineSegment [constr] StartX=-241 StartY=22 StartZ=0 EndX=241 EndY=22 EndZ=0
    g1: LineSegment [constr] StartX=241 StartY=22 StartZ=0 EndX=241 EndY=-22 EndZ=0
    g2: LineSegment [constr] StartX=241 StartY=-22 StartZ=0 EndX=-241 EndY=-22 EndZ=0
    g3: LineSegment [constr] StartX=-241 StartY=-22 StartZ=0 EndX=-241 EndY=22 EndZ=0
    g4: LineSegment [constr] StartX=-237 StartY=19 StartZ=0 EndX=-225 EndY=19 EndZ=0
    g5: LineSegment [constr] StartX=-225 StartY=19 StartZ=0 EndX=-225 EndY=13 EndZ=0
    g6: LineSegment [constr] StartX=-225 StartY=13 StartZ=0 EndX=-237 EndY=13 EndZ=0
    g7: LineSegment [constr] StartX=-237 StartY=13 StartZ=0 EndX=-237 EndY=19 EndZ=0
    g8: LineSegment [constr] StartX=-237 StartY=-13 StartZ=0 EndX=-225 EndY=-13 EndZ=0
    g9: LineSegment [constr] StartX=-225 StartY=-13 StartZ=0 EndX=-225 EndY=-19 EndZ=0
    g10: LineSegment [constr] StartX=-225 StartY=-19 StartZ=0 EndX=-237 EndY=-19 EndZ=0
    g11: LineSegment [constr] StartX=-237 StartY=-19 StartZ=0 EndX=-237 EndY=-13 EndZ=0
    g12: LineSegment [constr] StartX=225 StartY=19 StartZ=0 EndX=237 EndY=19 EndZ=0
    g13: LineSegment [constr] StartX=237 StartY=19 StartZ=0 EndX=237 EndY=13 EndZ=0
    g14: LineSegment [constr] StartX=237 StartY=13 StartZ=0 EndX=225 EndY=13 EndZ=0
    g15: LineSegment [constr] StartX=225 StartY=13 StartZ=0 EndX=225 EndY=19 EndZ=0
    g16: LineSegment [constr] StartX=225 StartY=-13 StartZ=0 EndX=237 EndY=-13 EndZ=0
    g17: LineSegment [constr] StartX=237 StartY=-13 StartZ=0 EndX=237 EndY=-19 EndZ=0
    g18: LineSegment [constr] StartX=237 StartY=-19 StartZ=0 EndX=225 EndY=-19 EndZ=0
    g19: LineSegment [constr] StartX=225 StartY=-19 StartZ=0 EndX=225 EndY=-13 EndZ=0
    g20: LineSegment [constr] StartX=-237 StartY=19 StartZ=0 EndX=-237 EndY=22 EndZ=0
    g21: LineSegment [constr] StartX=-237 StartY=19 StartZ=0 EndX=-241 EndY=19 EndZ=0
    g22: LineSegment [constr] StartX=-237 StartY=-19 StartZ=0 EndX=-237 EndY=-22 EndZ=0
    g23: LineSegment [constr] StartX=-237 StartY=-19 StartZ=0 EndX=-241 EndY=-19 EndZ=0
    g24: LineSegment [constr] StartX=237 StartY=-19 StartZ=0 EndX=241 EndY=-19 EndZ=0
    g25: LineSegment [constr] StartX=237 StartY=-19 StartZ=0 EndX=237 EndY=-22 EndZ=0
    g26: LineSegment [constr] StartX=237 StartY=19 StartZ=0 EndX=241 EndY=19 EndZ=0
    g27: LineSegment [constr] StartX=237 StartY=19 StartZ=0 EndX=237 EndY=22 EndZ=0
    g28: LineSegment [constr] StartX=-221.85 StartY=1.55 StartZ=0 EndX=-211.65 EndY=1.55 EndZ=0
    g29: LineSegment [constr] StartX=-211.65 StartY=1.55 StartZ=0 EndX=-211.65 EndY=-1.55 EndZ=0
    g30: LineSegment [constr] StartX=-211.65 StartY=-1.55 StartZ=0 EndX=-221.85 EndY=-1.55 EndZ=0
    g31: LineSegment [constr] StartX=-221.85 StartY=-1.55 StartZ=0 EndX=-221.85 EndY=1.55 EndZ=0
    g32: LineSegment [constr] StartX=-203.65 StartY=1.55 StartZ=0 EndX=-193.45 EndY=1.55 EndZ=0
    g33: LineSegment [constr] StartX=-193.45 StartY=1.55 StartZ=0 EndX=-193.45 EndY=-1.55 EndZ=0
    g34: LineSegment [constr] StartX=-193.45 StartY=-1.55 StartZ=0 EndX=-203.65 EndY=-1.55 EndZ=0
    g35: LineSegment [constr] StartX=-203.65 StartY=-1.55 StartZ=0 EndX=-203.65 EndY=1.55 EndZ=0
    g36: LineSegment [constr] StartX=-185.6 StartY=14.1 StartZ=0 EndX=-182.5 EndY=14.1 EndZ=0
    g37: LineSegment [constr] StartX=-182.5 StartY=14.1 StartZ=0 EndX=-182.5 EndY=3.9 EndZ=0
    g38: LineSegment [constr] StartX=-182.5 StartY=3.9 StartZ=0 EndX=-185.6 EndY=3.9 EndZ=0
    g39: LineSegment [constr] StartX=-185.6 StartY=3.9 StartZ=0 EndX=-185.6 EndY=14.1 EndZ=0
    g40: LineSegment [constr] StartX=-185.6 StartY=-3.9 StartZ=0 EndX=-182.5 EndY=-3.9 EndZ=0
    g41: LineSegment [constr] StartX=-182.5 StartY=-3.9 StartZ=0 EndX=-182.5 EndY=-14.1 EndZ=0
    g42: LineSegment [constr] StartX=-182.5 StartY=-14.1 StartZ=0 EndX=-185.6 EndY=-14.1 EndZ=0
    g43: LineSegment [constr] StartX=-185.6 StartY=-14.1 StartZ=0 EndX=-185.6 EndY=-3.9 EndZ=0
    g44: LineSegment [constr] StartX=221.85 StartY=1.55 StartZ=0 EndX=211.65 EndY=1.55 EndZ=0
    g45: LineSegment [constr] StartX=211.65 StartY=1.55 StartZ=0 EndX=211.65 EndY=-1.55 EndZ=0
    g46: LineSegment [constr] StartX=211.65 StartY=-1.55 StartZ=0 EndX=221.85 EndY=-1.55 EndZ=0
    g47: LineSegment [constr] StartX=221.85 StartY=-1.55 StartZ=0 EndX=221.85 EndY=1.55 EndZ=0
    g48: LineSegment [constr] StartX=203.65 StartY=1.55 StartZ=0 EndX=193.45 EndY=1.55 EndZ=0
    g49: LineSegment [constr] StartX=193.45 StartY=1.55 StartZ=0 EndX=193.45 EndY=-1.55 EndZ=0
    g50: LineSegment [constr] StartX=193.45 StartY=-1.55 StartZ=0 EndX=203.65 EndY=-1.55 EndZ=0
    g51: LineSegment [constr] StartX=203.65 StartY=-1.55 StartZ=0 EndX=203.65 EndY=1.55 EndZ=0
    g52: LineSegment [constr] StartX=182.5 StartY=14.1 StartZ=0 EndX=185.6 EndY=14.1 EndZ=0
    g53: LineSegment [constr] StartX=185.6 StartY=14.1 StartZ=0 EndX=185.6 EndY=3.9 EndZ=0
    g54: LineSegment [constr] StartX=185.6 StartY=3.9 StartZ=0 EndX=182.5 EndY=3.9 EndZ=0
    g55: LineSegment [constr] StartX=182.5 StartY=3.9 StartZ=0 EndX=182.5 EndY=14.1 EndZ=0
    g56: LineSegment [constr] StartX=182.5 StartY=-3.9 StartZ=0 EndX=185.6 EndY=-3.9 EndZ=0
    g57: LineSegment [constr] StartX=185.6 StartY=-3.9 StartZ=0 EndX=185.6 EndY=-14.1 EndZ=0
    g58: LineSegment [constr] StartX=185.6 StartY=-14.1 StartZ=0 EndX=182.5 EndY=-14.1 EndZ=0
    g59: LineSegment [constr] StartX=182.5 StartY=-14.1 StartZ=0 EndX=182.5 EndY=-3.9 EndZ=0
    g60: Circle [constr] CenterX=207.65 CenterY=0 CenterZ=0 NormalX=0 NormalY=0 NormalZ=1 AngleXU=0 Radius=1.6
    g61: Circle [constr] CenterX=-207.65 CenterY=0 CenterZ=0 NormalX=0 NormalY=0 NormalZ=1 AngleXU=0 Radius=1.6
    g62: LineSegment [constr] StartX=-211.65 StartY=1.55 StartZ=0 EndX=-203.65 EndY=1.55 EndZ=0
    g63: LineSegment [constr] StartX=-185.6 StartY=3.9 StartZ=0 EndX=-185.6 EndY=-3.9 EndZ=0
    g64: LineSegment [constr] StartX=203.65 StartY=1.55 StartZ=0 EndX=211.65 EndY=1.55 EndZ=0
    g65: LineSegment [constr] StartX=185.6 StartY=3.9 StartZ=0 EndX=185.6 EndY=-3.9 EndZ=0
    g66: LineSegment [constr] StartX=-193.45 StartY=-8.6e-15 StartZ=0 EndX=-185.6 EndY=-8.6e-15 EndZ=0
    g67: LineSegment [constr] StartX=193.45 StartY=-8e-16 StartZ=0 EndX=185.6 EndY=8.6e-15 EndZ=0
    g68: LineSegment [constr] StartX=-15 StartY=5.05 StartZ=0 EndX=-15 EndY=3.05 EndZ=0
    g69: LineSegment [constr] StartX=-15 StartY=3.05 StartZ=0 EndX=-17 EndY=3.05 EndZ=0
    g70: LineSegment StartX=-17 StartY=3.05 StartZ=0 EndX=-17 EndY=-11.05 EndZ=0
    g71: LineSegment [constr] StartX=-17 StartY=-11.05 StartZ=0 EndX=-15 EndY=-11.05 EndZ=0
    g72: LineSegment [constr] StartX=-15 StartY=-11.05 StartZ=0 EndX=-15 EndY=-13.05 EndZ=0
    g73: LineSegment StartX=-15 StartY=-13.05 StartZ=0 EndX=34.6 EndY=-13.05 EndZ=0
    g74: LineSegment [constr] StartX=34.6 StartY=-13.05 StartZ=0 EndX=34.6 EndY=-11.05 EndZ=0
    g75: LineSegment [constr] StartX=34.6 StartY=-11.05 StartZ=0 EndX=36.6 EndY=-11.05 EndZ=0
    g76: LineSegment StartX=36.6 StartY=-11.05 StartZ=0 EndX=36.6 EndY=3.05 EndZ=0
    g77: LineSegment [constr] StartX=36.6 StartY=3.05 StartZ=0 EndX=34.6 EndY=3.05 EndZ=0
    g78: LineSegment [constr] StartX=34.6 StartY=3.05 StartZ=0 EndX=34.6 EndY=5.05 EndZ=0
    g79: LineSegment StartX=34.6 StartY=5.05 StartZ=0 EndX=-15 EndY=5.05 EndZ=0
    g80: ArcOfCircle CenterX=-15 CenterY=3.05 CenterZ=0 NormalX=0 NormalY=0 NormalZ=1 AngleXU=0 Radius=2 StartAngle=1.5708 EndAngle=3.14159
    g81: ArcOfCircle CenterX=-15 CenterY=-11.05 CenterZ=0 NormalX=0 NormalY=0 NormalZ=1 AngleXU=0 Radius=2 StartAngle=3.14159 EndAngle=4.71239
    g82: ArcOfCircle CenterX=34.6 CenterY=-11.05 CenterZ=0 NormalX=0 NormalY=0 NormalZ=1 AngleXU=0 Radius=2 StartAngle=4.71239 EndAngle=6.28319
    g83: ArcOfCircle CenterX=34.6 CenterY=3.05 CenterZ=0 NormalX=0 NormalY=0 NormalZ=1 AngleXU=0 Radius=2 StartAngle=0 EndAngle=1.5708
  constraints (238):
    c: Coincident(g0,g1)
    c: Coincident(g1,g2)
    c: Coincident(g2,g3)
    c: Coincident(g3,g0)
    c: Horizontal(g0)
    c: Horizontal(g2)
    c: Vertical(g1)
    c: Vertical(g3)
    c: DistanceX(g0,g0) = 482
    c: DistanceY(g3,g3) = 44
    c: Coincident(g4,g5)
    c: Coincident(g5,g6)
    c: Coincident(g6,g7)
    c: Coincident(g7,g4)
    c: Horizontal(g4)
    c: Horizontal(g6)
    c: Vertical(g5)
    c: Vertical(g7)
    c: Coincident(g8,g9)
    c: Coincident(g9,g10)
    c: Coincident(g10,g11)
    c: Coincident(g11,g8)
    c: Horizontal(g8)
    c: Horizontal(g10)
    c: Vertical(g9)
    c: Vertical(g11)
    c: Coincident(g12,g13)
    c: Coincident(g13,g14)
    c: Coincident(g14,g15)
    c: Coincident(g15,g12)
    c: Horizontal(g12)
    c: Horizontal(g14)
    c: Vertical(g13)
    c: Vertical(g15)
    c: Coincident(g16,g17)
    c: Coincident(g17,g18)
    c: Coincident(g18,g19)
    c: Coincident(g19,g16)
    c: Horizontal(g16)
    c: Horizontal(g18)
    c: Vertical(g17)
    c: Vertical(g19)
    c: Equal(g5,g15)
    c: Equal(g15,g19)
    c: Equal(g19,g9)
    c: Equal(g6,g14)
    c: Equal(g14,g16)
    c: Equal(g16,g8)
    c: DistanceX(g4,g4) = 12
    c: DistanceY(g7,g7) = 6
    c: Coincident(g20,g4)
    c: PointOnObject(g20,g0)
    c: Vertical(g20)
    c: Coincident(g21,g4)
    c: PointOnObject(g21,g3)
    c: Horizontal(g21)
    c: Coincident(g22,g10)
    c: PointOnObject(g22,g2)
    c: Vertical(g22)
    c: Coincident(g23,g10)
    c: PointOnObject(g23,g3)
    c: Horizontal(g23)
    c: Coincident(g24,g17)
    c: PointOnObject(g24,g1)
    c: Horizontal(g24)
    c: Coincident(g25,g17)
    c: PointOnObject(g25,g2)
    c: Vertical(g25)
    c: Coincident(g26,g12)
    c: PointOnObject(g26,g1)
    c: Horizontal(g26)
    c: Coincident(g27,g12)
    c: PointOnObject(g27,g0)
    c: Vertical(g27)
    c: Equal(g21,g26)
    c: Equal(g26,g24)
    c: Equal(g24,g23)
    c: Equal(g20,g27)
    c: Equal(g27,g25)
    c: Equal(g25,g22)
    c: DistanceX(g21,g21) = 4
    c: DistanceY(g20,g20) = 3
    c: Coincident(g28,g29)
    c: Coincident(g29,g30)
    c: Coincident(g30,g31)
    c: Coincident(g31,g28)
    c: Horizontal(g28)
    c: Horizontal(g30)
    c: Vertical(g29)
    c: Vertical(g31)
    c: Coincident(g32,g33)
    c: Coincident(g33,g34)
    c: Coincident(g34,g35)
    c: Coincident(g35,g32)
    c: Horizontal(g32)
    c: Horizontal(g34)
    c: Vertical(g33)
    c: Vertical(g35)
    c: Coincident(g36,g37)
    c: Coincident(g37,g38)
    c: Coincident(g38,g39)
    c: Coincident(g39,g36)
    c: Horizontal(g36)
    c: Horizontal(g38)
    c: Vertical(g37)
    c: Vertical(g39)
    c: Coincident(g40,g41)
    c: Coincident(g41,g42)
    c: Coincident(g42,g43)
    c: Coincident(g43,g40)
    c: Horizontal(g40)
    c: Horizontal(g42)
    c: Vertical(g41)
    c: Vertical(g43)
    c: Coincident(g44,g45)
    c: Coincident(g45,g46)
    c: Coincident(g46,g47)
    c: Coincident(g47,g44)
    c: Horizontal(g44)
    c: Horizontal(g46)
    c: Vertical(g45)
    c: Vertical(g47)
    c: Coincident(g48,g49)
    c: Coincident(g49,g50)
    c: Coincident(g50,g51)
    c: Coincident(g51,g48)
    c: Horizontal(g48)
    c: Horizontal(g50)
    c: Vertical(g49)
    c: Vertical(g51)
    c: Coincident(g52,g53)
    c: Coincident(g53,g54)
    c: Coincident(g54,g55)
    c: Coincident(g55,g52)
    c: Horizontal(g52)
    c: Horizontal(g54)
    c: Vertical(g53)
    c: Vertical(g55)
    c: Coincident(g56,g57)
    c: Coincident(g57,g58)
    c: Coincident(g58,g59)
    c: Coincident(g59,g56)
    c: Horizontal(g56)
    c: Horizontal(g58)
    c: Vertical(g57)
    c: Vertical(g59)
    c: PointOnObject(g60,g-1)
    c: PointOnObject(g61,g-1)
    c: Equal(g28,g32)
    c: Equal(g32,g39)
    c: Equal(g39,g43)
    c: Equal(g43,g53)
    c: Equal(g53,g57)
    c: Equal(g57,g48)
    c: Equal(g48,g44)
    c: DistanceX(g28,g28) = 10.2
    c: DistanceY(g31,g31) = 3.1
    c: Equal(g29,g35)
    c: Equal(g35,g38)
    c: Equal(g38,g40)
    c: Equal(g40,g54)
    c: Equal(g54,g56)
    c: Equal(g56,g51)
    c: Equal(g51,g45)
    c: Symmetric(g34,g28,g61)
    c: Coincident(g62,g28)
    c: Coincident(g62,g32)
    c: Horizontal(g62)
    c: Coincident(g63,g38)
    c: Coincident(g63,g40)
    c: Vertical(g63)
    c: Coincident(g64,g48)
    c: Coincident(g64,g44)
    c: Horizontal(g64)
    c: Symmetric(g45,g48,g60)
    c: Coincident(g65,g53)
    c: Coincident(g65,g56)
    c: Vertical(g65)
    c: Equal(g64,g62)
    c: Equal(g65,g63)
    c: Horizontal(g66)
    c: Symmetric(g38,g40,g66)
    c: Symmetric(g32,g33,g66)
    c: Symmetric(g48,g49,g67)
    c: Symmetric(g53,g56,g67)
    c: DistanceX(g62,g62) = 8
    c: DistanceY(g63,g63) = 7.8
    c: Radius(g61) = 1.6
    c: DistanceX(g66,g66) = 7.85
    c: Equal(g66,g67)
    c: DistanceX(g36,g52) = 365
    c: Symmetric(g67,g66,g-1)
    c: Equal(g61,g60)
    c: Symmetric(g0,g1,g-1)
    c: Vertical(g68)
    c: Coincident(g68,g69)
    c: Horizontal(g69)
    c: Coincident(g69,g70)
    c: Vertical(g70)
    c: Coincident(g70,g71)
    c: Horizontal(g71)
    c: Coincident(g71,g72)
    c: Vertical(g72)
    c: Coincident(g72,g73)
    c: Horizontal(g73)
    c: Coincident(g73,g74)
    c: Vertical(g74)
    c: Coincident(g74,g75)
    c: Horizontal(g75)
    c: Coincident(g75,g76)
    c: Vertical(g76)
    c: Coincident(g76,g77)
    c: Horizontal(g77)
    c: Coincident(g77,g78)
    c: Vertical(g78)
    c: Coincident(g78,g79)
    c: Coincident(g79,g68)
    c: Horizontal(g79)
    c: Coincident(g80,g68)
    c: Coincident(g80,g79)
    c: Coincident(g80,g70)
    c: Coincident(g81,g71)
    c: Coincident(g81,g70)
    c: Coincident(g81,g73)
    c: Coincident(g82,g74)
    c: Coincident(g82,g76)
    c: Coincident(g82,g73)
    c: Coincident(g83,g77)
    c: Coincident(g83,g79)
    c: Coincident(g83,g76)
    c: Equal(g80,g83)
    c: Equal(g83,g82)
    c: Equal(g82,g81)
    c: Radius(g80) = 2
    c: DistanceX(g70,g76) = 53.6
    c: DistanceY(g73,g79) = 18.1
    c: DistanceY(g67,g79) = 5.05
    c: DistanceX(g70,g-1) = 17
FEATURE [Sketcher::SketchObject] Sketch001002027  label="Sketch Back Stack"
  Placement = pos=(0,109,0) rot=(0,0.707107,0.707107;3.14159rad)
  sketch-geometry (76):
    g0: LineSegment [constr] StartX=-241 StartY=22 StartZ=0 EndX=241 EndY=22 EndZ=0
    g1: LineSegment [constr] StartX=241 StartY=22 StartZ=0 EndX=241 EndY=-22 EndZ=0
    g2: LineSegment [constr] StartX=241 StartY=-22 StartZ=0 EndX=-241 EndY=-22 EndZ=0
    g3: LineSegment [constr] StartX=-241 StartY=-22 StartZ=0 EndX=-241 EndY=22 EndZ=0
    g4: LineSegment [constr] StartX=-237 StartY=19 StartZ=0 EndX=-225 EndY=19 EndZ=0
    g5: LineSegment [constr] StartX=-225 StartY=19 StartZ=0 EndX=-225 EndY=13 EndZ=0
    g6: LineSegment [constr] StartX=-225 StartY=13 StartZ=0 EndX=-237 EndY=13 EndZ=0
    g7: LineSegment [constr] StartX=-237 StartY=13 StartZ=0 EndX=-237 EndY=19 EndZ=0
    g8: LineSegment [constr] StartX=-237 StartY=-13 StartZ=0 EndX=-225 EndY=-13 EndZ=0
    g9: LineSegment [constr] StartX=-225 StartY=-13 StartZ=0 EndX=-225 EndY=-19 EndZ=0
    g10: LineSegment [constr] StartX=-225 StartY=-19 StartZ=0 EndX=-237 EndY=-19 EndZ=0
    g11: LineSegment [constr] StartX=-237 StartY=-19 StartZ=0 EndX=-237 EndY=-13 EndZ=0
    g12: LineSegment [constr] StartX=225 StartY=19 StartZ=0 EndX=237 EndY=19 EndZ=0
    g13: LineSegment [constr] StartX=237 StartY=19 StartZ=0 EndX=237 EndY=13 EndZ=0
    g14: LineSegment [constr] StartX=237 StartY=13 StartZ=0 EndX=225 EndY=13 EndZ=0
    g15: LineSegment [constr] StartX=225 StartY=13 StartZ=0 EndX=225 EndY=19 EndZ=0
    g16: LineSegment [constr] StartX=225 StartY=-13 StartZ=0 EndX=237 EndY=-13 EndZ=0
    g17: LineSegment [constr] StartX=237 StartY=-13 StartZ=0 EndX=237 EndY=-19 EndZ=0
    g18: LineSegment [constr] StartX=237 StartY=-19 StartZ=0 EndX=225 EndY=-19 EndZ=0
    g19: LineSegment [constr] StartX=225 StartY=-19 StartZ=0 EndX=225 EndY=-13 EndZ=0
    g20: LineSegment [constr] StartX=-237 StartY=19 StartZ=0 EndX=-237 EndY=22 EndZ=0
    g21: LineSegment [constr] StartX=-237 StartY=19 StartZ=0 EndX=-241 EndY=19 EndZ=0
    g22: LineSegment [constr] StartX=-237 StartY=-19 StartZ=0 EndX=-237 EndY=-22 EndZ=0
    g23: LineSegment [constr] StartX=-237 StartY=-19 StartZ=0 EndX=-241 EndY=-19 EndZ=0
    g24: LineSegment [constr] StartX=237 StartY=-19 StartZ=0 EndX=241 EndY=-19 EndZ=0
    g25: LineSegment [constr] StartX=237 StartY=-19 StartZ=0 EndX=237 EndY=-22 EndZ=0
    g26: LineSegment [constr] StartX=237 StartY=19 StartZ=0 EndX=241 EndY=19 EndZ=0
    g27: LineSegment [constr] StartX=237 StartY=19 StartZ=0 EndX=237 EndY=22 EndZ=0
    g28: LineSegment [constr] StartX=-195.6 StartY=14.1 StartZ=0 EndX=-192.5 EndY=14.1 EndZ=0
    g29: LineSegment [constr] StartX=-192.5 StartY=14.1 StartZ=0 EndX=-192.5 EndY=3.9 EndZ=0
    g30: LineSegment [constr] StartX=-192.5 StartY=3.9 StartZ=0 EndX=-195.6 EndY=3.9 EndZ=0
    g31: LineSegment [constr] StartX=-195.6 StartY=3.9 StartZ=0 EndX=-195.6 EndY=14.1 EndZ=0
    g32: LineSegment [constr] StartX=-195.6 StartY=-3.9 StartZ=0 EndX=-192.5 EndY=-3.9 EndZ=0
    g33: LineSegment [constr] StartX=-192.5 StartY=-3.9 StartZ=0 EndX=-192.5 EndY=-14.1 EndZ=0
    g34: LineSegment [constr] StartX=-192.5 StartY=-14.1 StartZ=0 EndX=-195.6 EndY=-14.1 EndZ=0
    g35: LineSegment [constr] StartX=-195.6 StartY=-14.1 StartZ=0 EndX=-195.6 EndY=-3.9 EndZ=0
    g36: LineSegment [constr] StartX=-195.6 StartY=3.9 StartZ=0 EndX=-195.6 EndY=-3.9 EndZ=0
    g37: LineSegment StartX=-185.35 StartY=7 StartZ=0 EndX=-185.35 EndY=-4.5 EndZ=0
    g38: LineSegment [constr] StartX=-185.35 StartY=-4.5 StartZ=0 EndX=-184.35 EndY=-4.5 EndZ=0
    g39: LineSegment [constr] StartX=-184.35 StartY=-4.5 StartZ=0 EndX=-184.35 EndY=-5.5 EndZ=0
    g40: LineSegment StartX=-184.35 StartY=-5.5 StartZ=0 EndX=-175.35 EndY=-5.5 EndZ=0
    g41: LineSegment [constr] StartX=-175.35 StartY=-5.5 StartZ=0 EndX=-175.35 EndY=-4.5 EndZ=0
    g42: LineSegment [constr] StartX=-175.35 StartY=-4.5 StartZ=0 EndX=-174.35 EndY=-4.5 EndZ=0
    g43: LineSegment StartX=-174.35 StartY=-4.5 StartZ=0 EndX=-174.35 EndY=4.5 EndZ=0
    g44: LineSegment [constr] StartX=-174.35 StartY=4.5 StartZ=0 EndX=-175.35 EndY=4.5 EndZ=0
    g45: LineSegment [constr] StartX=-175.35 StartY=4.5 StartZ=0 EndX=-175.35 EndY=5.5 EndZ=0
    g46: LineSegment StartX=-175.35 StartY=5.5 StartZ=0 EndX=-181.35 EndY=5.5 EndZ=0
    g47: LineSegment [constr] StartX=-181.35 StartY=5.5 StartZ=0 EndX=-181.35 EndY=7 EndZ=0
    g48: LineSegment [constr] StartX=-181.35 StartY=7 StartZ=0 EndX=-182.85 EndY=7 EndZ=0
    g49: LineSegment [constr] StartX=-182.85 StartY=7 StartZ=0 EndX=-185.35 EndY=7 EndZ=0
    g50: ArcOfCircle CenterX=-181.35 CenterY=7 CenterZ=0 NormalX=0 NormalY=0 NormalZ=1 AngleXU=0 Radius=1.5 StartAngle=3.14159 EndAngle=4.71239
    g51: ArcOfCircle CenterX=-175.35 CenterY=4.5 CenterZ=0 NormalX=0 NormalY=0 NormalZ=1 AngleXU=0 Radius=1 StartAngle=0 EndAngle=1.5708
    g52: ArcOfCircle CenterX=-175.35 CenterY=-4.5 CenterZ=0 NormalX=0 NormalY=0 NormalZ=1 AngleXU=0 Radius=1 StartAngle=4.71239 EndAngle=6.28319
    g53: ArcOfCircle CenterX=-184.35 CenterY=-4.5 CenterZ=0 NormalX=0 NormalY=0 NormalZ=1 AngleXU=0 Radius=1 StartAngle=3.14159 EndAngle=4.71239
    g54: ArcOfCircle CenterX=-184.1 CenterY=7 CenterZ=0 NormalX=0 NormalY=0 NormalZ=1 AngleXU=0 Radius=1.25 StartAngle=-2.22e-14 EndAngle=3.14159
    g55: Circle CenterX=-179.85 CenterY=11.5 CenterZ=0 NormalX=0 NormalY=0 NormalZ=1 AngleXU=0 Radius=2.5
    g56: Circle CenterX=-179.85 CenterY=-11.5 CenterZ=0 NormalX=0 NormalY=0 NormalZ=1 AngleXU=0 Radius=2.5
    g57: LineSegment [constr] StartX=-179.85 StartY=11.5 StartZ=0 EndX=-179.85 EndY=-11.5 EndZ=0
    g58: LineSegment [constr] StartX=-192.5 StartY=14.1 StartZ=0 EndX=-175.35 EndY=4.5 EndZ=0
    g59: LineSegment [constr] StartX=-175.35 StartY=-4.5 StartZ=0 EndX=-192.5 EndY=-14.1 EndZ=0
    g60: LineSegment StartX=-169.85 StartY=3 StartZ=0 EndX=-169.85 EndY=-11 EndZ=0
    g61: LineSegment [constr] StartX=-169.85 StartY=-11 StartZ=0 EndX=-168.85 EndY=-11 EndZ=0
    g62: LineSegment [constr] StartX=-168.85 StartY=-11 StartZ=0 EndX=-168.85 EndY=-12 EndZ=0
    g63: LineSegment StartX=-168.85 StartY=-12 StartZ=0 EndX=-158.85 EndY=-12 EndZ=0
    g64: LineSegment [constr] StartX=-158.85 StartY=-12 StartZ=0 EndX=-158.85 EndY=-11 EndZ=0
    g65: LineSegment [constr] StartX=-158.85 StartY=-11 StartZ=0 EndX=-157.85 EndY=-11 EndZ=0
    g66: LineSegment StartX=-157.85 StartY=-11 StartZ=0 EndX=-157.85 EndY=3 EndZ=0
    g67: LineSegment [constr] StartX=-157.85 StartY=3 StartZ=0 EndX=-158.85 EndY=3 EndZ=0
    g68: LineSegment [constr] StartX=-158.85 StartY=3 StartZ=0 EndX=-158.85 EndY=4 EndZ=0
    g69: LineSegment StartX=-158.85 StartY=4 StartZ=0 EndX=-168.85 EndY=4 EndZ=0
    g70: LineSegment [constr] StartX=-168.85 StartY=4 StartZ=0 EndX=-168.85 EndY=3 EndZ=0
    g71: LineSegment [constr] StartX=-168.85 StartY=3 StartZ=0 EndX=-169.85 EndY=3 EndZ=0
    g72: ArcOfCircle CenterX=-168.85 CenterY=3 CenterZ=0 NormalX=0 NormalY=0 NormalZ=1 AngleXU=0 Radius=1 StartAngle=1.5708 EndAngle=3.14159
    g73: ArcOfCircle CenterX=-158.85 CenterY=3 CenterZ=0 NormalX=0 NormalY=0 NormalZ=1 AngleXU=0 Radius=1 StartAngle=0 EndAngle=1.5708
    g74: ArcOfCircle CenterX=-158.85 CenterY=-11 CenterZ=0 NormalX=0 NormalY=0 NormalZ=1 AngleXU=0 Radius=1 StartAngle=4.71239 EndAngle=6.28319
    g75: ArcOfCircle CenterX=-168.85 CenterY=-11 CenterZ=0 NormalX=0 NormalY=0 NormalZ=1 AngleXU=0 Radius=1 StartAngle=3.14159 EndAngle=4.71239
  constraints (214):
    c: Coincident(g0,g1)
    c: Coincident(g1,g2)
    c: Coincident(g2,g3)
    c: Coincident(g3,g0)
    c: Horizontal(g0)
    c: Horizontal(g2)
    c: Vertical(g1)
    c: Vertical(g3)
    c: DistanceX(g0,g0) = 482
    c: DistanceY(g3,g3) = 44
    c: Coincident(g4,g5)
    c: Coincident(g5,g6)
    c: Coincident(g6,g7)
    c: Coincident(g7,g4)
    c: Horizontal(g4)
    c: Horizontal(g6)
    c: Vertical(g5)
    c: Vertical(g7)
    c: Coincident(g8,g9)
    c: Coincident(g9,g10)
    c: Coincident(g10,g11)
    c: Coincident(g11,g8)
    c: Horizontal(g8)
    c: Horizontal(g10)
    c: Vertical(g9)
    c: Vertical(g11)
    c: Coincident(g12,g13)
    c: Coincident(g13,g14)
    c: Coincident(g14,g15)
    c: Coincident(g15,g12)
    c: Horizontal(g12)
    c: Horizontal(g14)
    c: Vertical(g13)
    c: Vertical(g15)
    c: Coincident(g16,g17)
    c: Coincident(g17,g18)
    c: Coincident(g18,g19)
    c: Coincident(g19,g16)
    c: Horizontal(g16)
    c: Horizontal(g18)
    c: Vertical(g17)
    c: Vertical(g19)
    c: Equal(g5,g15)
    c: Equal(g15,g19)
    c: Equal(g19,g9)
    c: Equal(g6,g14)
    c: Equal(g14,g16)
    c: Equal(g16,g8)
    c: DistanceX(g4,g4) = 12
    c: DistanceY(g7,g7) = 6
    c: Coincident(g20,g4)
    c: PointOnObject(g20,g0)
    c: Vertical(g20)
    c: Coincident(g21,g4)
    c: PointOnObject(g21,g3)
    c: Horizontal(g21)
    c: Coincident(g22,g10)
    c: PointOnObject(g22,g2)
    c: Vertical(g22)
    c: Coincident(g23,g10)
    c: PointOnObject(g23,g3)
    c: Horizontal(g23)
    c: Coincident(g24,g17)
    c: PointOnObject(g24,g1)
    c: Horizontal(g24)
    c: Coincident(g25,g17)
    c: PointOnObject(g25,g2)
    c: Vertical(g25)
    c: Coincident(g26,g12)
    c: PointOnObject(g26,g1)
    c: Horizontal(g26)
    c: Coincident(g27,g12)
    c: PointOnObject(g27,g0)
    c: Vertical(g27)
    c: Equal(g21,g26)
    c: Equal(g26,g24)
    c: Equal(g24,g23)
    c: Equal(g20,g27)
    c: Equal(g27,g25)
    c: Equal(g25,g22)
    c: DistanceX(g21,g21) = 4
    c: DistanceY(g20,g20) = 3
    c: Coincident(g28,g29)
    c: Coincident(g29,g30)
    c: Coincident(g30,g31)
    c: Coincident(g31,g28)
    c: Horizontal(g28)
    c: Horizontal(g30)
    c: Vertical(g29)
    c: Vertical(g31)
    c: Coincident(g32,g33)
    c: Coincident(g33,g34)
    c: Coincident(g34,g35)
    c: Coincident(g35,g32)
    c: Horizontal(g32)
    c: Horizontal(g34)
    c: Vertical(g33)
    c: Vertical(g35)
    c: Equal(g31,g35)
    c: Equal(g30,g32)
    c: Coincident(g36,g30)
    c: Coincident(g36,g32)
    c: Vertical(g37)
    c: Coincident(g37,g38)
    c: Horizontal(g38)
    c: Coincident(g38,g39)
    c: Vertical(g39)
    c: Coincident(g39,g40)
    c: Horizontal(g40)
    c: Coincident(g40,g41)
    c: Vertical(g41)
    c: Coincident(g41,g42)
    c: Horizontal(g42)
    c: Coincident(g42,g43)
    c: Vertical(g43)
    c: Coincident(g43,g44)
    c: Horizontal(g44)
    c: Coincident(g44,g45)
    c: Vertical(g45)
    c: Coincident(g45,g46)
    c: Horizontal(g46)
    c: Coincident(g46,g47)
    c: Vertical(g47)
    c: Coincident(g47,g48)
    c: Horizontal(g48)
    c: Coincident(g49,g37)
    c: Horizontal(g49)
    c: Coincident(g50,g47)
    c: Coincident(g50,g46)
    c: Coincident(g51,g44)
    c: Coincident(g51,g46)
    c: Coincident(g51,g43)
    c: Coincident(g52,g41)
    c: Coincident(g52,g43)
    c: Coincident(g52,g40)
    c: Coincident(g53,g38)
    c: Coincident(g53,g37)
    c: Coincident(g53,g40)
    c: DistanceY(g40,g46) = 11
    c: DistanceX(g49,g49) = 2.5
    c: Equal(g51,g52)
    c: Equal(g52,g53)
    c: PointOnObject(g54,g49)
    c: Coincident(g54,g37)
    c: Radius(g51) = 1
    c: Radius(g50) = 1.5
    c: Coincident(g57,g55)
    c: Coincident(g57,g56)
    c: Vertical(g57)
    c: DistanceY(g57,g57) = 23
    c: DistanceY(g46,g55) = 6
    c: DistanceX(g55,g43) = 5.5
    c: DistanceX(g37,g43) = 11
    c: Coincident(g58,g28)
    c: Coincident(g58,g51)
    c: Coincident(g59,g52)
    c: Coincident(g59,g33)
    c: Equal(g59,g58)
    c: Radius(g55) = 2.5
    c: Equal(g56,g55)
    c: DistanceX(g32,g37) = 7.15
    c: Vertical(g60)
    c: Coincident(g60,g61)
    c: Horizontal(g61)
    c: Coincident(g61,g62)
    c: Vertical(g62)
    c: Coincident(g62,g63)
    c: Horizontal(g63)
    c: Coincident(g63,g64)
    c: Vertical(g64)
    c: Coincident(g64,g65)
    c: Horizontal(g65)
    c: Coincident(g65,g66)
    c: Vertical(g66)
    c: Coincident(g66,g67)
    c: Coincident(g67,g68)
    c: Vertical(g68)
    c: Coincident(g68,g69)
    c: Horizontal(g69)
    c: Coincident(g69,g70)
    c: Vertical(g70)
    c: Coincident(g70,g71)
    c: Coincident(g71,g60)
    c: Horizontal(g71)
    c: Horizontal(g67)
    c: Coincident(g72,g70)
    c: Coincident(g72,g69)
    c: Coincident(g72,g60)
    c: Coincident(g73,g67)
    c: Coincident(g73,g69)
    c: Coincident(g73,g66)
    c: Coincident(g74,g64)
    c: Coincident(g74,g66)
    c: Coincident(g74,g63)
    c: Coincident(g75,g61)
    c: Coincident(g75,g60)
    c: Coincident(g75,g63)
    c: Equal(g72,g73)
    c: Equal(g73,g74)
    c: Equal(g74,g75)
    c: Equal(g51,g72)
    c: DistanceY(g63,g69) = 16
    c: DistanceX(g60,g66) = 12
    c: DistanceX(g55,g60) = 10
    c: DistanceY(g60,g43) = 1.5
    c: Coincident(g48,g49)
    c: Coincident(g48,g50)
    c: Coincident(g48,g54)
    c: Symmetric(g0,g1,g-1)
    c: DistanceX(g30,g30) = 3.1
    c: DistanceY(g31,g31) = 10.2
    c: DistanceY(g36,g36) = 7.8
    c: Symmetric(g29,g32,g-1)
    c: DistanceX(g5,g28) = 32.5
FEATURE [PartDesign::Pocket] Pocket009  label="Pocket RP001"
  BaseFeature = -> Pad015
  Length = 3
  Length2 = 100
  Placement = pos=(0,106,0) rot=(1,0,0;1.5708rad)
  Profile = -> Sketch001002026
  Type = 0
FEATURE [PartDesign::Pocket] Pocket010  label="Pocket Stack001"
  BaseFeature = -> Pocket009
  Length = 3
  Length2 = 100
  Placement = pos=(0,106,0) rot=(1,0,0;1.5708rad)
  Profile = -> Sketch001002027
  Type = 0
FEATURE [PartDesign::Body] Body015  label="Body Back001"
  Group = -> [Sketch001002010,Pad015,Sketch001002026,Sketch001002027,Pocket009,Pocket010]
  Origin = -> Origin018
  Tip = -> Pocket010
FEATURE [Part::Fillet] Fillet028  label="Fillet Back"
  Base = -> Body015
  Edges = 4 edges r=5: [Edge1,Edge2,Edge5,Edge8]
  Placement = pos=(0,0,0) rot=(-1,0,0;1.5708rad)
FEATURE [Part::Fillet] Fillet031  label="Fillet032"
  Base = -> Body020
  Edges = 3 edges r=3: [Edge2,Edge11,Edge14]
FEATURE [Part::Fillet] Fillet032  label="Fillet Deckel"
  Base = -> Fillet031
  Edges = 3 edges r=10: [Edge125,Edge127,Edge137]
FEATURE [Sketcher::SketchObject] Sketch001002008  label="Sketch Boden001"
  Placement = pos=(0,45,-16.5) rot=(0,0,-1;1.5708rad)
  sketch-geometry (160):
    g0: LineSegment StartX=-61 StartY=-198.5 StartZ=0 EndX=0 EndY=-198.5 EndZ=0
    g1: LineSegment [constr] StartX=0 StartY=-198.5 StartZ=0 EndX=0 EndY=198.5 EndZ=0
    g2: LineSegment [constr] StartX=0 StartY=198.5 StartZ=0 EndX=-16 EndY=198.5 EndZ=0
    g3: LineSegment StartX=-56.9 StartY=-192.5 StartZ=0 EndX=-47.1 EndY=-192.5 EndZ=0
    g4: LineSegment StartX=-47.1 StartY=-192.5 StartZ=0 EndX=-47.1 EndY=-195.5 EndZ=0
    g5: LineSegment StartX=-47.1 StartY=-195.5 StartZ=0 EndX=-56.9 EndY=-195.5 EndZ=0
    g6: LineSegment StartX=-56.9 StartY=-195.5 StartZ=0 EndX=-56.9 EndY=-192.5 EndZ=0
    g7: LineSegment StartX=-13.9 StartY=-192.5 StartZ=0 EndX=-4.1 EndY=-192.5 EndZ=0
    g8: LineSegment StartX=-4.1 StartY=-192.5 StartZ=0 EndX=-4.1 EndY=-195.5 EndZ=0
    g9: LineSegment StartX=-4.1 StartY=-195.5 StartZ=0 EndX=-13.9 EndY=-195.5 EndZ=0
    g10: LineSegment StartX=-13.9 StartY=-195.5 StartZ=0 EndX=-13.9 EndY=-192.5 EndZ=0
    g11: LineSegment StartX=-11.9 StartY=195.5 StartZ=0 EndX=-2.1 EndY=195.5 EndZ=0
    g12: LineSegment StartX=-2.1 StartY=195.5 StartZ=0 EndX=-2.1 EndY=192.5 EndZ=0
    g13: LineSegment StartX=-2.1 StartY=192.5 StartZ=0 EndX=-11.9 EndY=192.5 EndZ=0
    g14: LineSegment StartX=-11.9 StartY=192.5 StartZ=0 EndX=-11.9 EndY=195.5 EndZ=0
    g15: LineSegment StartX=21.1 StartY=195.5 StartZ=0 EndX=30.9 EndY=195.5 EndZ=0
    g16: LineSegment StartX=30.9 StartY=195.5 StartZ=0 EndX=30.9 EndY=192.5 EndZ=0
    g17: LineSegment StartX=30.9 StartY=192.5 StartZ=0 EndX=21.1 EndY=192.5 EndZ=0
    g18: LineSegment StartX=21.1 StartY=192.5 StartZ=0 EndX=21.1 EndY=195.5 EndZ=0
    g19: LineSegment [constr] StartX=-16 StartY=198.5 StartZ=0 EndX=-16 EndY=195.5 EndZ=0
    g20: LineSegment [constr] StartX=-16 StartY=195.5 StartZ=0 EndX=-11.9 EndY=195.5 EndZ=0
    g21: LineSegment [constr] StartX=30.9 StartY=195.5 StartZ=0 EndX=35 EndY=195.5 EndZ=0
    g22: LineSegment [constr] StartX=35 StartY=195.5 StartZ=0 EndX=35 EndY=198.5 EndZ=0
    g23: LineSegment [constr] StartX=-4.1 StartY=-195.5 StartZ=0 EndX=0 EndY=-195.5 EndZ=0
    g24: LineSegment [constr] StartX=0 StartY=-195.5 StartZ=0 EndX=0 EndY=-198.5 EndZ=0
    g25: LineSegment [constr] StartX=-56.9 StartY=-195.5 StartZ=0 EndX=-61 EndY=-195.5 EndZ=0
    g26: LineSegment [constr] StartX=-61 StartY=-195.5 StartZ=0 EndX=-61 EndY=-198.5 EndZ=0
    g27: Circle CenterX=9.5 CenterY=194 CenterZ=0 NormalX=0 NormalY=0 NormalZ=1 AngleXU=0 Radius=1.5
    g28: Circle CenterX=-30.5 CenterY=-194 CenterZ=0 NormalX=0 NormalY=0 NormalZ=1 AngleXU=0 Radius=1.5
    g29: LineSegment [constr] StartX=-30.5 StartY=-194 StartZ=0 EndX=-47.1 EndY=-194 EndZ=0
    g30: LineSegment [constr] StartX=9.5 StartY=194 StartZ=0 EndX=-2.1 EndY=194 EndZ=0
    g31: LineSegment [constr] StartX=21.1 StartY=194 StartZ=0 EndX=9.5 EndY=194 EndZ=0
    g32: LineSegment [constr] StartX=-30.5 StartY=-194 StartZ=0 EndX=-13.9 EndY=-194 EndZ=0
    g33: Circle CenterX=-5.1 CenterY=182.5 CenterZ=0 NormalX=0 NormalY=0 NormalZ=1 AngleXU=0 Radius=1.5
    g34: LineSegment StartX=-16 StartY=198.5 StartZ=0 EndX=35 EndY=198.5 EndZ=0
    g35: LineSegment StartX=35 StartY=198.5 StartZ=0 EndX=35 EndY=-108.5 EndZ=0
    g36: LineSegment StartX=35 StartY=-108.5 StartZ=0 EndX=0 EndY=-108.5 EndZ=0
    g37: LineSegment StartX=0 StartY=-108.5 StartZ=0 EndX=0 EndY=-198.5 EndZ=0
    g38: LineSegment StartX=-61 StartY=108.5 StartZ=0 EndX=-61 EndY=98.5 EndZ=0
    g39: LineSegment StartX=-61 StartY=88.5 StartZ=0 EndX=-61 EndY=-168.5 EndZ=0
    g40: LineSegment StartX=-61 StartY=-178.5 StartZ=0 EndX=-61 EndY=-198.5 EndZ=0
    g41: LineSegment StartX=-61 StartY=98.5 StartZ=0 EndX=-64 EndY=98.5 EndZ=0
    g42: LineSegment StartX=-64 StartY=98.5 StartZ=0 EndX=-64 EndY=88.5 EndZ=0
    g43: LineSegment StartX=-64 StartY=88.5 StartZ=0 EndX=-61 EndY=88.5 EndZ=0
    g44: LineSegment StartX=-61 StartY=-168.5 StartZ=0 EndX=-64 EndY=-168.5 EndZ=0
    g45: LineSegment StartX=-64 StartY=-168.5 StartZ=0 EndX=-64 EndY=-178.5 EndZ=0
    g46: LineSegment StartX=-64 StartY=-178.5 StartZ=0 EndX=-61 EndY=-178.5 EndZ=0
    g47: Circle CenterX=-36.6 CenterY=34.5 CenterZ=0 NormalX=0 NormalY=0 NormalZ=1 AngleXU=0 Radius=2.5
    g48: Circle CenterX=21.4 CenterY=34.5 CenterZ=0 NormalX=0 NormalY=0 NormalZ=1 AngleXU=0 Radius=2.5
    g49: Circle CenterX=21.4 CenterY=-14.5 CenterZ=0 NormalX=0 NormalY=0 NormalZ=1 AngleXU=0 Radius=2.5
    g50: Circle CenterX=-36.6 CenterY=-14.5 CenterZ=0 NormalX=0 NormalY=0 NormalZ=1 AngleXU=0 Radius=2.5
    g51: LineSegment [constr] StartX=-36.6 StartY=34.5 StartZ=0 EndX=21.4 EndY=34.5 EndZ=0
    g52: LineSegment [constr] StartX=21.4 StartY=34.5 StartZ=0 EndX=21.4 EndY=-14.5 EndZ=0
    g53: LineSegment [constr] StartX=21.4 StartY=-14.5 StartZ=0 EndX=-36.6 EndY=-14.5 EndZ=0
    g54: LineSegment [constr] StartX=-36.6 StartY=-14.5 StartZ=0 EndX=-36.6 EndY=34.5 EndZ=0
    g55: Circle CenterX=-50.1 CenterY=97.5 CenterZ=0 NormalX=0 NormalY=0 NormalZ=1 AngleXU=0 Radius=1.5
    g56: Circle CenterX=-50.1 CenterY=-182.5 CenterZ=0 NormalX=0 NormalY=0 NormalZ=1 AngleXU=0 Radius=1.5
    g57: Circle CenterX=24.9 CenterY=-97.5 CenterZ=0 NormalX=0 NormalY=0 NormalZ=1 AngleXU=0 Radius=1.5
    g58: LineSegment [constr] StartX=19.1 StartY=-36.5 StartZ=0 EndX=31.9 EndY=-36.5 EndZ=0
    g59: LineSegment [constr] StartX=31.9 StartY=-36.5 StartZ=0 EndX=31.9 EndY=-33.5 EndZ=0
    g60: LineSegment [constr] StartX=31.9 StartY=-33.5 StartZ=0 EndX=19.1 EndY=-33.5 EndZ=0
    g61: LineSegment [constr] StartX=19.1 StartY=-33.5 StartZ=0 EndX=19.1 EndY=-36.5 EndZ=0
    g62: LineSegment StartX=-50.9 StartY=-36.5 StartZ=0 EndX=-38.1 EndY=-36.5 EndZ=0
    g63: LineSegment StartX=-38.1 StartY=-36.5 StartZ=0 EndX=-38.1 EndY=-39.5 EndZ=0
    g64: LineSegment StartX=-38.1 StartY=-39.5 StartZ=0 EndX=-50.9 EndY=-39.5 EndZ=0
    g65: LineSegment StartX=-50.9 StartY=-39.5 StartZ=0 EndX=-50.9 EndY=-36.5 EndZ=0
    g66: LineSegment [constr] StartX=-38.1 StartY=-36.5 StartZ=0 EndX=19.1 EndY=-36.5 EndZ=0
    g67: Circle CenterX=-50.1 CenterY=32.5 CenterZ=0 NormalX=0 NormalY=0 NormalZ=1 AngleXU=0 Radius=1.5
    g68: LineSegment [constr] StartX=-61 StartY=98.5 StartZ=0 EndX=-61 EndY=88.5 EndZ=0
    g69: LineSegment [constr] StartX=-61 StartY=-168.5 StartZ=0 EndX=-61 EndY=-178.5 EndZ=0
    g70: LineSegment StartX=-61 StartY=108.5 StartZ=0 EndX=-16 EndY=108.5 EndZ=0
    g71: LineSegment StartX=-16 StartY=108.5 StartZ=0 EndX=-16 EndY=198.5 EndZ=0
    g72: Circle CenterX=-10.1 CenterY=-97.5 CenterZ=0 NormalX=0 NormalY=0 NormalZ=1 AngleXU=0 Radius=1.5
    g73: LineSegment [constr] StartX=-50.1 StartY=-182.5 StartZ=0 EndX=-10.1 EndY=-182.5 EndZ=0
    g74: LineSegment [constr] StartX=-10.1 StartY=-182.5 StartZ=0 EndX=-10.1 EndY=-97.5 EndZ=0
    g75: LineSegment [constr] StartX=-10.1 StartY=-97.5 StartZ=0 EndX=24.9 EndY=-97.5 EndZ=0
    g76: LineSegment [constr] StartX=24.9 StartY=-97.5 StartZ=0 EndX=24.9 EndY=32.5 EndZ=0
    g77: LineSegment [constr] StartX=24.9 StartY=32.5 StartZ=0 EndX=-50.1 EndY=32.5 EndZ=0
    g78: LineSegment [constr] StartX=-50.1 StartY=32.5 StartZ=0 EndX=-50.1 EndY=-182.5 EndZ=0
    g79: LineSegment [constr] StartX=-50.1 StartY=-182.5 StartZ=0 EndX=-50.1 EndY=-198.5 EndZ=0
    g80: LineSegment [constr] StartX=-5.1 StartY=182.5 StartZ=0 EndX=24.9 EndY=182.5 EndZ=0
    g81: LineSegment [constr] StartX=24.9 StartY=182.5 StartZ=0 EndX=24.9 EndY=77.5 EndZ=0
    g82: LineSegment [constr] StartX=24.9 StartY=77.5 StartZ=0 EndX=-50.1 EndY=77.5 EndZ=0
    g83: LineSegment [constr] StartX=-50.1 StartY=77.5 StartZ=0 EndX=-50.1 EndY=97.5 EndZ=0
    g84: LineSegment [constr] StartX=-5.1 StartY=97.5 StartZ=0 EndX=-5.1 EndY=182.5 EndZ=0
    g85: LineSegment [constr] StartX=-5.1 StartY=182.5 StartZ=0 EndX=-5.1 EndY=198.5 EndZ=0
    g86: Circle CenterX=24.9 CenterY=77.5 CenterZ=0 NormalX=0 NormalY=0 NormalZ=1 AngleXU=0 Radius=1.5
    g87: LineSegment [constr] StartX=24.9 StartY=-97.5 StartZ=0 EndX=24.9 EndY=-108.5 EndZ=0
    g88: LineSegment [constr] StartX=-50.1 StartY=97.5 StartZ=0 EndX=-45.1 EndY=97.5 EndZ=0
    g89: Circle CenterX=-45.1 CenterY=97.5 CenterZ=0 NormalX=0 NormalY=0 NormalZ=1 AngleXU=0 Radius=1.5
    g90: LineSegment [constr] StartX=-45.1 StartY=97.5 StartZ=0 EndX=-40.1 EndY=97.5 EndZ=0
    g91: Circle CenterX=-40.1 CenterY=97.5 CenterZ=0 NormalX=0 NormalY=0 NormalZ=1 AngleXU=0 Radius=1.5
    g92: LineSegment [constr] StartX=-5.1 StartY=97.5 StartZ=0 EndX=-40.1 EndY=97.5 EndZ=0
    g93: Circle CenterX=24.9 CenterY=97.5 CenterZ=0 NormalX=0 NormalY=0 NormalZ=1 AngleXU=0 Radius=1.5
    g94: LineSegment [constr] StartX=-5.1 StartY=97.5 StartZ=0 EndX=24.9 EndY=97.5 EndZ=0
    g95: LineSegment [constr] StartX=24.9 StartY=182.5 StartZ=0 EndX=35 EndY=182.5 EndZ=0
    g96: LineSegment [constr] StartX=-5.1 StartY=182.5 StartZ=0 EndX=-16 EndY=182.5 EndZ=0
    g97: LineSegment [constr] StartX=-50.1 StartY=97.5 StartZ=0 EndX=-61 EndY=97.5 EndZ=0
    g98: LineSegment [constr] StartX=24.9 StartY=-97.5 StartZ=0 EndX=35 EndY=-97.5 EndZ=0
    g99: LineSegment [constr] StartX=-10.1 StartY=-182.5 StartZ=0 EndX=0 EndY=-182.5 EndZ=0
    g100: LineSegment [constr] StartX=-50.1 StartY=-182.5 StartZ=0 EndX=-61 EndY=-182.5 EndZ=0
    g101: LineSegment [constr] StartX=-50.1 StartY=97.5 StartZ=0 EndX=-50.1 EndY=108.5 EndZ=0
    g102: LineSegment [constr] StartX=-40.1 StartY=97.5 StartZ=0 EndX=-40.1 EndY=42.5 EndZ=0
    g103: Circle CenterX=-40.1 CenterY=42.5 CenterZ=0 NormalX=0 NormalY=0 NormalZ=1 AngleXU=0 Radius=1.5
    g104: LineSegment [constr] StartX=-40.1 StartY=42.5 StartZ=0 EndX=-40.1 EndY=27.5 EndZ=0
    g105: ArcOfCircle CenterX=-35.1 CenterY=27.5 CenterZ=0 NormalX=0 NormalY=0 NormalZ=1 AngleXU=0 Radius=1.5 StartAngle=9e-16 EndAngle=3.14159
    g106: ArcOfCircle CenterX=-35.1 CenterY=-7.5 CenterZ=0 NormalX=0 NormalY=0 NormalZ=1 AngleXU=0 Radius=1.5 StartAngle=3.14159 EndAngle=6.28319
    g107: LineSegment StartX=-36.6 StartY=27.5 StartZ=0 EndX=-36.6 EndY=-7.5 EndZ=0
    g108: LineSegment StartX=-33.6 StartY=27.5 StartZ=0 EndX=-33.6 EndY=-7.5 EndZ=0
    g109: LineSegment [constr] StartX=-40.1 StartY=27.5 StartZ=0 EndX=-35.1 EndY=27.5 EndZ=0
    g110: LineSegment [constr] StartX=-35.1 StartY=27.5 StartZ=0 EndX=-30.1 EndY=27.5 EndZ=0
    g111: LineSegment [constr] StartX=-30.1 StartY=27.5 StartZ=0 EndX=-30.1 EndY=32.5 EndZ=0
    g112: LineSegment [constr] StartX=-30.1 StartY=32.5 StartZ=0 EndX=-25.1 EndY=32.5 EndZ=0
    g113: LineSegment [constr] StartX=-25.1 StartY=32.5 StartZ=0 EndX=-20.1 EndY=32.5 EndZ=0
    g114: LineSegment [constr] StartX=-20.1 StartY=32.5 StartZ=0 EndX=-15.1 EndY=32.5 EndZ=0
    g115: LineSegment [constr] StartX=-15.1 StartY=32.5 StartZ=0 EndX=-10.1 EndY=32.5 EndZ=0
    g116: LineSegment [constr] StartX=-10.1 StartY=32.5 StartZ=0 EndX=-5.1 EndY=32.5 EndZ=0
    g117: LineSegment [constr] StartX=-5.1 StartY=32.5 StartZ=0 EndX=-0.1 EndY=32.5 EndZ=0
    g118: LineSegment [constr] StartX=-0.1 StartY=32.5 StartZ=0 EndX=4.9 EndY=32.5 EndZ=0
    g119: LineSegment [constr] StartX=4.9 StartY=32.5 StartZ=0 EndX=9.9 EndY=32.5 EndZ=0
    g120: LineSegment [constr] StartX=14.9 StartY=32.5 StartZ=0 EndX=9.9 EndY=32.5 EndZ=0
    g121: LineSegment [constr] StartX=14.9 StartY=32.5 StartZ=0 EndX=14.9 EndY=27.5 EndZ=0
    g122: LineSegment [constr] StartX=14.9 StartY=27.5 StartZ=0 EndX=19.9 EndY=27.5 EndZ=0
    g123: ArcOfCircle CenterX=-25.1 CenterY=32.5 CenterZ=0 NormalX=0 NormalY=0 NormalZ=1 AngleXU=0 Radius=1.5 StartAngle=-1.8e-15 EndAngle=3.14159
    g124: ArcOfCircle CenterX=-25.1 CenterY=-12.5 CenterZ=0 NormalX=0 NormalY=0 NormalZ=1 AngleXU=0 Radius=1.5 StartAngle=3.14159 EndAngle=6.28319
    g125: LineSegment StartX=-26.6 StartY=32.5 StartZ=0 EndX=-26.6 EndY=-12.5 EndZ=0
    g126: LineSegment StartX=-23.6 StartY=32.5 StartZ=0 EndX=-23.6 EndY=-12.5 EndZ=0
    g127: ArcOfCircle CenterX=-15.1 CenterY=32.5 CenterZ=0 NormalX=0 NormalY=0 NormalZ=1 AngleXU=0 Radius=1.5 StartAngle=0 EndAngle=3.14159
    g128: ArcOfCircle CenterX=-15.1 CenterY=-12.5 CenterZ=0 NormalX=0 NormalY=0 NormalZ=1 AngleXU=0 Radius=1.5 StartAngle=3.14159 EndAngle=6.28319
    g129: LineSegment StartX=-16.6 StartY=32.5 StartZ=0 EndX=-16.6 EndY=-12.5 EndZ=0
    g130: LineSegment StartX=-13.6 StartY=32.5 StartZ=0 EndX=-13.6 EndY=-12.5 EndZ=0
    g131: ArcOfCircle CenterX=-0.1 CenterY=32.5 CenterZ=0 NormalX=0 NormalY=0 NormalZ=1 AngleXU=0 Radius=1.5 StartAngle=2.2e-15 EndAngle=3.14159
    g132: ArcOfCircle CenterX=-0.1 CenterY=-12.5 CenterZ=0 NormalX=0 NormalY=0 NormalZ=1 AngleXU=0 Radius=1.5 StartAngle=3.14159 EndAngle=6.28319
    g133: LineSegment StartX=-1.6 StartY=32.5 StartZ=0 EndX=-1.6 EndY=-12.5 EndZ=0
    g134: LineSegment StartX=1.4 StartY=32.5 StartZ=0 EndX=1.4 EndY=-12.5 EndZ=0
    g135: ArcOfCircle CenterX=9.9 CenterY=32.5 CenterZ=0 NormalX=0 NormalY=0 NormalZ=1 AngleXU=0 Radius=1.5 StartAngle=-1.8e-15 EndAngle=3.14159
    g136: ArcOfCircle CenterX=9.9 CenterY=-12.5 CenterZ=0 NormalX=0 NormalY=0 NormalZ=1 AngleXU=0 Radius=1.5 StartAngle=3.14159 EndAngle=6.28319
    g137: LineSegment StartX=8.4 StartY=32.5 StartZ=0 EndX=8.4 EndY=-12.5 EndZ=0
    g138: LineSegment StartX=11.4 StartY=32.5 StartZ=0 EndX=11.4 EndY=-12.5 EndZ=0
    g139: ArcOfCircle CenterX=19.9 CenterY=27.5 CenterZ=0 NormalX=0 NormalY=0 NormalZ=1 AngleXU=0 Radius=1.5 StartAngle=1e-15 EndAngle=3.14159
    g140: ArcOfCircle CenterX=19.9 CenterY=-7.5 CenterZ=0 NormalX=0 NormalY=0 NormalZ=1 AngleXU=0 Radius=1.5 StartAngle=3.14159 EndAngle=6.28319
    g141: LineSegment StartX=18.4 StartY=27.5 StartZ=0 EndX=18.4 EndY=-7.5 EndZ=0
    g142: LineSegment StartX=21.4 StartY=27.5 StartZ=0 EndX=21.4 EndY=-7.5 EndZ=0
    g143: LineSegment [constr] StartX=31.9 StartY=-36.5 StartZ=0 EndX=35 EndY=-36.5 EndZ=0
    g144: GeomPoint X=19.1 Y=-35 Z=0
    g145: LineSegment [constr] StartX=-50.9 StartY=-36.5 StartZ=0 EndX=-61 EndY=-36.5 EndZ=0
    g146: GeomPoint X=-7.6 Y=10 Z=0
    g147: ArcOfCircle [constr] CenterX=-10.1 CenterY=32.5 CenterZ=0 NormalX=0 NormalY=0 NormalZ=1 AngleXU=0 Radius=1.5 StartAngle=1.5708 EndAngle=4.71239
    g148: ArcOfCircle [constr] CenterX=-5.1 CenterY=32.5 CenterZ=0 NormalX=0 NormalY=0 NormalZ=1 AngleXU=0 Radius=1.5 StartAngle=4.71239 EndAngle=7.85398
    g149: LineSegment [constr] StartX=-10.1 StartY=31 StartZ=0 EndX=-5.1 EndY=31 EndZ=0
    g150: LineSegment [constr] StartX=-10.1 StartY=34 StartZ=0 EndX=-5.1 EndY=34 EndZ=0
    g151: LineSegment [constr] StartX=-10.1 StartY=32.5 StartZ=0 EndX=-10.1 EndY=27.5 EndZ=0
    g152: LineSegment [constr] StartX=-10.1 StartY=27.5 StartZ=0 EndX=-10.1 EndY=22.5 EndZ=0
    g153: LineSegment [constr] StartX=-10.1 StartY=22.5 StartZ=0 EndX=-10.1 EndY=17.5 EndZ=0
    g154: LineSegment [constr] StartX=-10.1 StartY=17.5 StartZ=0 EndX=-10.1 EndY=12.5 EndZ=0
    g155: LineSegment [constr] StartX=-10.1 StartY=12.5 StartZ=0 EndX=-10.1 EndY=7.5 EndZ=0
    g156: LineSegment [constr] StartX=-10.1 StartY=7.5 StartZ=0 EndX=-10.1 EndY=2.5 EndZ=0
    g157: LineSegment [constr] StartX=-10.1 StartY=2.5 StartZ=0 EndX=-10.1 EndY=-2.5 EndZ=0
    g158: LineSegment [constr] StartX=-10.1 StartY=-2.5 StartZ=0 EndX=-10.1 EndY=-7.5 EndZ=0
    g159: LineSegment [constr] StartX=-10.1 StartY=-7.5 StartZ=0 EndX=-10.1 EndY=-12.5 EndZ=0
  constraints (429):
    c: Coincident(g0,g1)
    c: Horizontal(g0)
    c: Horizontal(g2)
    c: Vertical(g1)
    c: Coincident(g3,g4)
    c: Coincident(g4,g5)
    c: Coincident(g5,g6)
    c: Coincident(g6,g3)
    c: Horizontal(g3)
    c: Horizontal(g5)
    c: Vertical(g4)
    c: Vertical(g6)
    c: Coincident(g7,g8)
    c: Coincident(g8,g9)
    c: Coincident(g9,g10)
    c: Coincident(g10,g7)
    c: Horizontal(g7)
    c: Horizontal(g9)
    c: Vertical(g8)
    c: Vertical(g10)
    c: Coincident(g11,g12)
    c: Coincident(g12,g13)
    c: Coincident(g13,g14)
    c: Coincident(g14,g11)
    c: Horizontal(g11)
    c: Horizontal(g13)
    c: Vertical(g12)
    c: Vertical(g14)
    c: Coincident(g15,g16)
    c: Coincident(g16,g17)
    c: Coincident(g17,g18)
    c: Coincident(g18,g15)
    c: Horizontal(g15)
    c: Horizontal(g17)
    c: Vertical(g16)
    c: Vertical(g18)
    c: Equal(g12,g18)
    c: Equal(g18,g10)
    c: Equal(g10,g4)
    c: Equal(g13,g17)
    c: Equal(g17,g7)
    c: Equal(g7,g3)
    c: Equal(g13,g17)
    c: Equal(g17,g7)
    c: Equal(g7,g3)
    c: Coincident(g20,g19)
    c: Coincident(g20,g11)
    c: Coincident(g21,g15)
    c: Horizontal(g21)
    c: Coincident(g22,g21)
    c: Coincident(g23,g8)
    c: Horizontal(g23)
    c: Coincident(g24,g23)
    c: Coincident(g24,g0)
    c: Coincident(g25,g5)
    c: Horizontal(g25)
    c: Coincident(g26,g25)
    c: Horizontal(g20)
    c: Equal(g19,g22)
    c: Equal(g22,g24)
    c: Equal(g24,g26)
    c: Vertical(g19)
    c: Vertical(g22)
    c: Vertical(g24)
    c: Vertical(g26)
    c: Equal(g20,g21)
    c: Equal(g21,g23)
    c: Equal(g23,g25)
    c: DistanceY(g11,g2) = 3
    c: DistanceX(g20,g20) = 4.1
    c: DistanceX(g11,g11) = 9.8
    c: DistanceY(g14,g14) = 3
    c: Equal(g27,g28)
    c: Radius(g27) = 1.5
    c: Coincident(g29,g28)
    c: Horizontal(g29)
    c: Coincident(g30,g27)
    c: Horizontal(g30)
    c: Symmetric(g1,g0,g-1)
    c: Horizontal(g31)
    c: Equal(g27,g33)
    c: Coincident(g1,g2)
    c: Coincident(g34,g22)
    c: Coincident(g34,g35)
    c: Vertical(g35)
    c: Coincident(g35,g36)
    c: Horizontal(g36)
    c: Coincident(g36,g37)
    c: Coincident(g37,g0)
    c: Vertical(g37)
    c: DistanceY(g37,g37) = 90
    c: Vertical(g38)
    c: Vertical(g40)
    c: Horizontal(g41)
    c: Coincident(g41,g42)
    c: Vertical(g42)
    c: Coincident(g42,g43)
    c: Horizontal(g43)
    c: Horizontal(g44)
    c: Coincident(g44,g45)
    c: Vertical(g45)
    c: Coincident(g45,g46)
    c: Horizontal(g46)
    c: DistanceY(g42,g42) = 10
    c: Equal(g42,g45)
    c: Equal(g44,g43)
    c: DistanceX(g41,g41) = 3
    c: Coincident(g46,g40)
    c: Coincident(g44,g39)
    c: Coincident(g43,g39)
    c: Coincident(g38,g41)
    c: Symmetric(g3,g4,g29)
    c: Symmetric(g7,g9,g32)
    c: Symmetric(g15,g17,g31)
    c: Symmetric(g11,g12,g30)
    c: Equal(g30,g31)
    c: Equal(g32,g29)
    c: Coincident(g51,g52)
    c: Coincident(g52,g53)
    c: Coincident(g53,g54)
    c: Coincident(g54,g51)
    c: Horizontal(g51)
    c: Horizontal(g53)
    c: Vertical(g52)
    c: Vertical(g54)
    c: Coincident(g51,g47)
    c: Coincident(g52,g49)
    c: Coincident(g50,g53)
    c: Coincident(g48,g51)
    c: Equal(g47,g48)
    c: Equal(g48,g49)
    c: Equal(g49,g50)
    c: DistanceY(g54,g54) = 49
    c: DistanceX(g51,g51) = 58
    c: Radius(g47) = 2.5
    c: Equal(g55,g33)
    c: Equal(g56,g55)
    c: Equal(g57,g55)
    c: Coincident(g58,g59)
    c: Coincident(g59,g60)
    c: Coincident(g60,g61)
    c: Coincident(g61,g58)
    c: Horizontal(g58)
    c: Horizontal(g60)
    c: Vertical(g59)
    c: Vertical(g61)
    c: Coincident(g62,g63)
    c: Coincident(g63,g64)
    c: Coincident(g64,g65)
    c: Coincident(g65,g62)
    c: Horizontal(g62)
    c: Horizontal(g64)
    c: Vertical(g63)
    c: Vertical(g65)
    c: Coincident(g66,g62)
    c: Coincident(g66,g58)
    c: Horizontal(g66)
    c: DistanceX(g62,g62) = 12.8
    c: DistanceY(g65,g65) = 3
    c: Equal(g64,g60)
    c: Equal(g63,g61)
    c: DistanceX(g36,g36) = 35
    c: Equal(g67,g56)
    c: DistanceY(g-1,g1) = 198.5
    c: Coincident(g68,g38)
    c: Coincident(g68,g39)
    c: Vertical(g68)
    c: Coincident(g69,g39)
    c: Coincident(g69,g40)
    c: Vertical(g69)
    c: Horizontal(g70)
    c: Coincident(g70,g71)
    c: Vertical(g71)
    c: Equal(g72,g57)
    c: DistanceX(g70,g70) = 45
    c: Coincident(g32,g28)
    c: Coincident(g0,g26)
    c: Coincident(g2,g19)
    c: Coincident(g2,g34)
    c: Coincident(g71,g34)
    c: Coincident(g38,g70)
    c: Equal(g37,g71)
    c: DistanceX(g34,g34) = 51
    c: Coincident(g40,g0)
    c: Coincident(g73,g56)
    c: Horizontal(g73)
    c: Vertical(g74)
    c: Coincident(g74,g75)
    c: Coincident(g75,g57)
    c: Horizontal(g75)
    c: Coincident(g75,g76)
    c: Vertical(g76)
    c: Coincident(g76,g77)
    c: Horizontal(g77)
    c: Coincident(g77,g78)
    c: Coincident(g78,g73)
    c: Vertical(g78)
    c: Coincident(g67,g77)
    c: Coincident(g72,g74)
    c: Coincident(g73,g74)
    c: Coincident(g79,g56)
    c: Vertical(g79)
    c: Coincident(g80,g33)
    c: Horizontal(g80)
    c: Coincident(g80,g81)
    c: Vertical(g81)
    c: Coincident(g81,g82)
    c: Horizontal(g82)
    c: Coincident(g82,g83)
    c: Vertical(g83)
    c: Coincident(g84,g80)
    c: Vertical(g84)
    c: Coincident(g85,g33)
    c: Vertical(g85)
    c: Coincident(g55,g83)
    c: Coincident(g86,g81)
    c: Equal(g86,g55)
    c: Equal(g85,g79)
    c: DistanceY(g83,g83) = 20
    c: Coincident(g27,g31)
    c: PointOnObject(g85,g34)
    c: DistanceY(g3,g56) = 10
    c: DistanceY(g78,g78) = 215
    c: PointOnObject(g79,g0)
    c: Coincident(g87,g57)
    c: PointOnObject(g87,g36)
    c: Vertical(g87)
    c: DistanceX(g38,g55) = 10.9
    c: Coincident(g88,g55)
    c: Horizontal(g88)
    c: Coincident(g89,g88)
    c: DistanceX(g88,g88) = 5
    c: Radius(g89) = 1.5
    c: Coincident(g90,g88)
    c: Horizontal(g90)
    c: Equal(g88,g90)
    c: Coincident(g91,g90)
    c: Equal(g89,g91)
    c: Coincident(g92,g84)
    c: Coincident(g92,g90)
    c: Horizontal(g92)
    c: PointOnObject(g93,g81)
    c: Coincident(g94,g84)
    c: Coincident(g94,g93)
    c: Horizontal(g94)
    c: Equal(g91,g93)
    c: Coincident(g95,g80)
    c: PointOnObject(g95,g35)
    c: Horizontal(g95)
    c: Coincident(g96,g33)
    c: PointOnObject(g96,g71)
    c: Horizontal(g96)
    c: Coincident(g97,g55)
    c: PointOnObject(g97,g38)
    c: Horizontal(g97)
    c: Coincident(g98,g57)
    c: PointOnObject(g98,g35)
    c: Horizontal(g98)
    c: Coincident(g99,g73)
    c: PointOnObject(g99,g37)
    c: Horizontal(g99)
    c: Coincident(g100,g56)
    c: PointOnObject(g100,g40)
    c: Horizontal(g100)
    c: Equal(g100,g97)
    c: Equal(g97,g96)
    c: Equal(g99,g98)
    c: Equal(g98,g95)
    c: DistanceX(g95,g95) = 10.1
    c: Coincident(g101,g55)
    c: PointOnObject(g101,g70)
    c: Vertical(g101)
    c: Equal(g101,g87)
    c: Coincident(g102,g91)
    c: Vertical(g102)
    c: DistanceY(g102,g102) = 55
    c: Coincident(g103,g102)
    c: Equal(g103,g91)
    c: Vertical(g104)
    c: DistanceY(g104,g104) = 15
    c: Tangent(g105,g108) = 1.5708
    c: Tangent(g105,g107) = -1.5708
    c: Tangent(g107,g106) = -1.5708
    c: Tangent(g108,g106) = 1.5708
    c: Vertical(g107)
    c: Equal(g105,g106)
    c: Equal(g103,g105)
    c: DistanceY(g106,g104) = 35
    c: Coincident(g104,g103)
    c: Horizontal(g109)
    c: Coincident(g110,g109)
    c: Horizontal(g110)
    c: Coincident(g111,g110)
    c: Vertical(g111)
    c: Coincident(g112,g111)
    c: Horizontal(g112)
    c: Coincident(g113,g112)
    c: Horizontal(g113)
    c: Coincident(g114,g113)
    c: Horizontal(g114)
    c: Coincident(g115,g114)
    c: Horizontal(g115)
    c: Coincident(g116,g115)
    c: Horizontal(g116)
    c: Coincident(g117,g116)
    c: Horizontal(g117)
    c: Coincident(g118,g117)
    c: Horizontal(g118)
    c: Coincident(g119,g118)
    c: Horizontal(g119)
    c: Coincident(g120,g119)
    c: Horizontal(g120)
    c: Coincident(g121,g120)
    c: Vertical(g121)
    c: Coincident(g122,g121)
    c: Horizontal(g122)
    c: DistanceX(g109,g109) = 5
    c: Equal(g109,g110)
    c: Equal(g110,g111)
    c: Equal(g111,g112)
    c: Equal(g112,g113)
    c: Equal(g113,g114)
    c: Equal(g114,g115)
    c: Equal(g115,g116)
    c: Equal(g116,g117)
    c: Equal(g117,g118)
    c: Equal(g118,g119)
    c: Equal(g119,g120)
    c: Equal(g120,g121)
    c: Equal(g121,g122)
    c: Coincident(g104,g109)
    c: Coincident(g105,g109)
    c: Tangent(g123,g126) = 1.5708
    c: Tangent(g123,g125) = -1.5708
    c: Tangent(g125,g124) = -1.5708
    c: Tangent(g126,g124) = 1.5708
    c: Vertical(g125)
    c: Equal(g123,g124)
    c: Coincident(g123,g112)
    c: Tangent(g127,g130) = 1.5708
    c: Tangent(g127,g129) = -1.5708
    c: Tangent(g129,g128) = -1.5708
    c: Tangent(g130,g128) = 1.5708
    c: Vertical(g129)
    c: Equal(g127,g128)
    c: Coincident(g127,g114)
    c: Tangent(g131,g134) = 1.5708
    c: Tangent(g131,g133) = -1.5708
    c: Tangent(g133,g132) = -1.5708
    c: Tangent(g134,g132) = 1.5708
    c: Vertical(g133)
    c: Equal(g131,g132)
    c: Coincident(g131,g117)
    c: Tangent(g135,g138) = 1.5708
    c: Tangent(g135,g137) = -1.5708
    c: Tangent(g137,g136) = -1.5708
    c: Tangent(g138,g136) = 1.5708
    c: Vertical(g137)
    c: Equal(g135,g136)
    c: Coincident(g135,g119)
    c: Tangent(g139,g142) = 1.5708
    c: Tangent(g139,g141) = -1.5708
    c: Tangent(g141,g140) = -1.5708
    c: Tangent(g142,g140) = 1.5708
    c: Vertical(g141)
    c: Equal(g139,g140)
    c: Coincident(g139,g122)
    c: Equal(g124,g128)
    c: Equal(g128,g132)
    c: Equal(g132,g136)
    c: Equal(g136,g140)
    c: Equal(g108,g141)
    c: Equal(g126,g129)
    c: Equal(g130,g133)
    c: Equal(g134,g137)
    c: Coincident(g143,g58)
    c: PointOnObject(g143,g35)
    c: Horizontal(g143)
    c: DistanceX(g143,g143) = 3.1
    c: DistanceY(g124,g123) = 45
    c: Equal(g106,g124)
    c: Symmetric(g58,g60,g144)
    c: DistanceY(g144,g-1) = 35
    c: Coincident(g145,g62)
    c: PointOnObject(g145,g39)
    c: Horizontal(g145)
    c: DistanceX(g145,g145) = 10.1
    c: Symmetric(g47,g49,g146)
    c: DistanceX(g146,g-1) = 7.6
    c: DistanceY(g-1,g146) = 10
    c: Vertical(g39)
    c: DistanceY(g38,g38) = 10
    c: DistanceY(g101,g101) = 11
    c: DistanceY(g40,g40) = 20
    c: Tangent(g147,g150) = 1.5708
    c: Tangent(g147,g149) = -1.5708
    c: Tangent(g149,g148) = -1.5708
    c: Tangent(g150,g148) = 1.5708
    c: Horizontal(g149)
    c: Coincident(g147,g115)
    c: Equal(g127,g147)
    c: Coincident(g116,g148)
    c: Coincident(g151,g147)
    c: Vertical(g151)
    c: Coincident(g152,g151)
    c: Vertical(g152)
    c: Coincident(g153,g152)
    c: Vertical(g153)
    c: Coincident(g154,g153)
    c: Vertical(g154)
    c: Coincident(g155,g154)
    c: Vertical(g155)
    c: Coincident(g156,g155)
    c: Vertical(g156)
    c: Coincident(g157,g156)
    c: Vertical(g157)
    c: Coincident(g158,g157)
    c: Vertical(g158)
    c: Coincident(g159,g158)
    c: Vertical(g159)
    c: Equal(g116,g151)
    c: Equal(g151,g152)
    c: Equal(g152,g153)
    c: Equal(g153,g154)
    c: Equal(g154,g155)
    c: Equal(g155,g156)
    c: Equal(g156,g157)
    c: Equal(g157,g158)
    c: Equal(g158,g159)
FEATURE [PartDesign::Pad] Pad013
  Length = 3
  Length2 = 100
  Placement = pos=(0,45,-16.5) rot=(0,0,-1;1.5708rad)
  Profile = -> Sketch001002008
  Refine = true
  Reversed = true
  Type = 0
FEATURE [PartDesign::Body] Body013  label="Body Boden"
  Group = -> [Sketch001002008,Pad013]
  Origin = -> Origin016
  Tip = -> Pad013
FEATURE [Part::Fillet] Fillet027  label="Fillet031"
  Base = -> Body013
  Edges = 3 edges r=3: [Edge29,Edge38,Edge41]
FEATURE [Part::Fillet] Fillet030  label="Fillet Boden"
  Base = -> Fillet027
  Edges = 3 edges r=10: [Edge165,Edge167,Edge177]
FEATURE [Sketcher::SketchObject] Sketch001002028  label="Sketch Boden RP"
  Placement = pos=(0,45,-16.5) rot=(0,0,-1;1.5708rad)
  sketch-geometry (86):
    g0: Circle CenterX=-36.6 CenterY=54.6 CenterZ=0 NormalX=0 NormalY=0 NormalZ=1 AngleXU=0 Radius=1.375
    g1: Circle CenterX=21.4 CenterY=54.6 CenterZ=0 NormalX=0 NormalY=0 NormalZ=1 AngleXU=0 Radius=1.375
    g2: Circle [constr] CenterX=21.4 CenterY=5.6 CenterZ=0 NormalX=0 NormalY=0 NormalZ=1 AngleXU=0 Radius=1.375
    g3: Circle [constr] CenterX=-36.6 CenterY=5.6 CenterZ=0 NormalX=0 NormalY=0 NormalZ=1 AngleXU=0 Radius=1.375
    g4: LineSegment [constr] StartX=-36.6 StartY=54.6 StartZ=0 EndX=21.4 EndY=54.6 EndZ=0
    g5: LineSegment [constr] StartX=21.4 StartY=54.6 StartZ=0 EndX=21.4 EndY=5.6 EndZ=0
    g6: LineSegment [constr] StartX=21.4 StartY=5.6 StartZ=0 EndX=-36.6 EndY=5.6 EndZ=0
    g7: LineSegment [constr] StartX=-36.6 StartY=5.6 StartZ=0 EndX=-36.6 EndY=54.6 EndZ=0
    g8: LineSegment [constr] StartX=29.8 StartY=-5.8 StartZ=0 EndX=29.8 EndY=1.2 EndZ=0
    g9: LineSegment [constr] StartX=29.8 StartY=59 StartZ=0 EndX=29.8 EndY=66 EndZ=0
    g10: LineSegment [constr] StartX=29.8 StartY=1.2 StartZ=0 EndX=25.4 EndY=1.2 EndZ=0
    g11: LineSegment [constr] StartX=25.4 StartY=1.2 StartZ=0 EndX=25.4 EndY=5.6 EndZ=0
    g12: LineSegment [constr] StartX=25.4 StartY=5.6 StartZ=0 EndX=17.4 EndY=5.6 EndZ=0
    g13: LineSegment [constr] StartX=17.4 StartY=5.6 StartZ=0 EndX=17.4 EndY=1.2 EndZ=0
    g14: LineSegment [constr] StartX=17.4 StartY=1.2 StartZ=0 EndX=-32.6 EndY=1.2 EndZ=0
    g15: LineSegment [constr] StartX=-32.6 StartY=1.2 StartZ=0 EndX=-32.6 EndY=5.6 EndZ=0
    g16: LineSegment [constr] StartX=-32.6 StartY=5.6 StartZ=0 EndX=-40.6 EndY=5.6 EndZ=0
    g17: LineSegment [constr] StartX=-40.6 StartY=5.6 StartZ=0 EndX=-40.6 EndY=1.2 EndZ=0
    g18: LineSegment [constr] StartX=-40.6 StartY=1.2 StartZ=0 EndX=-58.6 EndY=1.2 EndZ=0
    g19: LineSegment [constr] StartX=-58.6 StartY=1.2 StartZ=0 EndX=-58.6 EndY=59 EndZ=0
    g20: LineSegment [constr] StartX=-58.6 StartY=59 StartZ=0 EndX=-40.6 EndY=59 EndZ=0
    g21: LineSegment [constr] StartX=-40.6 StartY=59 StartZ=0 EndX=-40.6 EndY=54.6 EndZ=0
    g22: LineSegment [constr] StartX=-40.6 StartY=54.6 StartZ=0 EndX=-32.6 EndY=54.6 EndZ=0
    g23: LineSegment [constr] StartX=-32.6 StartY=54.6 StartZ=0 EndX=-32.6 EndY=59 EndZ=0
    g24: LineSegment [constr] StartX=-32.6 StartY=59 StartZ=0 EndX=17.4 EndY=59 EndZ=0
    g25: LineSegment [constr] StartX=17.4 StartY=59 StartZ=0 EndX=17.4 EndY=54.6 EndZ=0
    g26: LineSegment [constr] StartX=17.4 StartY=54.6 StartZ=0 EndX=25.4 EndY=54.6 EndZ=0
    g27: LineSegment [constr] StartX=25.4 StartY=54.6 StartZ=0 EndX=25.4 EndY=59 EndZ=0
    g28: LineSegment [constr] StartX=25.4 StartY=59 StartZ=0 EndX=29.8 EndY=59 EndZ=0
    g29: LineSegment [constr] StartX=-40.6 StartY=59 StartZ=0 EndX=-32.6 EndY=59 EndZ=0
    g30: LineSegment [constr] StartX=-40.6 StartY=1.2 StartZ=0 EndX=-32.6 EndY=1.2 EndZ=0
    g31: LineSegment [constr] StartX=17.4 StartY=1.2 StartZ=0 EndX=25.4 EndY=1.2 EndZ=0
    g32: LineSegment [constr] StartX=17.4 StartY=59 StartZ=0 EndX=25.4 EndY=59 EndZ=0
    g33: ArcOfCircle CenterX=-36.6 CenterY=54.6 CenterZ=0 NormalX=0 NormalY=0 NormalZ=1 AngleXU=0 Radius=4 StartAngle=3.14159 EndAngle=6.28319
    g34: ArcOfCircle [constr] CenterX=21.4 CenterY=5.6 CenterZ=0 NormalX=0 NormalY=0 NormalZ=1 AngleXU=0 Radius=4 StartAngle=1e-16 EndAngle=3.14159
    g35: ArcOfCircle [constr] CenterX=-36.6 CenterY=5.6 CenterZ=0 NormalX=0 NormalY=0 NormalZ=1 AngleXU=0 Radius=4 StartAngle=3e-16 EndAngle=3.14159
    g36: ArcOfCircle CenterX=21.4 CenterY=54.6 CenterZ=0 NormalX=0 NormalY=0 NormalZ=1 AngleXU=0 Radius=4 StartAngle=3.14159 EndAngle=6.28319
    g37: LineSegment [constr] StartX=29.8 StartY=1.2 StartZ=0 EndX=29.8 EndY=5.6 EndZ=0
    g38: LineSegment [constr] StartX=29.8 StartY=5.6 StartZ=0 EndX=25.4 EndY=5.6 EndZ=0
    g39: LineSegment [constr] StartX=17.4 StartY=5.6 StartZ=0 EndX=14.4 EndY=5.6 EndZ=0
    g40: LineSegment [constr] StartX=14.4 StartY=5.6 StartZ=0 EndX=14.4 EndY=2.6 EndZ=0
    g41: LineSegment [constr] StartX=14.4 StartY=2.6 StartZ=0 EndX=-29.6 EndY=2.6 EndZ=0
    g42: LineSegment [constr] StartX=-29.6 StartY=2.6 StartZ=0 EndX=-29.6 EndY=5.6 EndZ=0
    g43: LineSegment [constr] StartX=-29.6 StartY=5.6 StartZ=0 EndX=-32.6 EndY=5.6 EndZ=0
    g44: LineSegment [constr] StartX=-40.6 StartY=5.6 StartZ=0 EndX=-45 EndY=5.6 EndZ=0
    g45: LineSegment [constr] StartX=-45 StartY=5.6 StartZ=0 EndX=-45 EndY=1.2 EndZ=0
    g46: LineSegment [constr] StartX=-45 StartY=59 StartZ=0 EndX=-45 EndY=54.6 EndZ=0
    g47: LineSegment [constr] StartX=-45 StartY=54.6 StartZ=0 EndX=-40.6 EndY=54.6 EndZ=0
    g48: LineSegment [constr] StartX=-32.6 StartY=54.6 StartZ=0 EndX=-29.6 EndY=54.6 EndZ=0
    g49: LineSegment [constr] StartX=-29.6 StartY=54.6 StartZ=0 EndX=-29.6 EndY=57.6 EndZ=0
    g50: LineSegment StartX=-29.6 StartY=57.6 StartZ=0 EndX=14.4 EndY=57.6 EndZ=0
    g51: LineSegment [constr] StartX=14.4 StartY=57.6 StartZ=0 EndX=14.4 EndY=54.6 EndZ=0
    g52: LineSegment [constr] StartX=14.4 StartY=54.6 StartZ=0 EndX=17.4 EndY=54.6 EndZ=0
    g53: LineSegment [constr] StartX=29.8 StartY=59 StartZ=0 EndX=29.8 EndY=54.6 EndZ=0
    g54: LineSegment [constr] StartX=29.8 StartY=54.6 StartZ=0 EndX=25.4 EndY=54.6 EndZ=0
    g55: ArcOfCircle CenterX=29.8 CenterY=54.6 CenterZ=0 NormalX=0 NormalY=0 NormalZ=1 AngleXU=0 Radius=4.4 StartAngle=1.5708 EndAngle=3.14159
    g56: ArcOfCircle CenterX=14.4 CenterY=54.6 CenterZ=0 NormalX=0 NormalY=0 NormalZ=1 AngleXU=0 Radius=3 StartAngle=0 EndAngle=1.5708
    g57: ArcOfCircle CenterX=-29.6 CenterY=54.6 CenterZ=0 NormalX=0 NormalY=0 NormalZ=1 AngleXU=0 Radius=3 StartAngle=1.5708 EndAngle=3.14159
    g58: ArcOfCircle CenterX=-45 CenterY=54.6 CenterZ=0 NormalX=0 NormalY=0 NormalZ=1 AngleXU=0 Radius=4.4 StartAngle=0 EndAngle=1.5708
    g59: ArcOfCircle [constr] CenterX=-45 CenterY=5.6 CenterZ=0 NormalX=0 NormalY=0 NormalZ=1 AngleXU=0 Radius=4.4 StartAngle=4.71239 EndAngle=6.28319
    g60: ArcOfCircle [constr] CenterX=-29.6 CenterY=5.6 CenterZ=0 NormalX=0 NormalY=0 NormalZ=1 AngleXU=0 Radius=3 StartAngle=3.14159 EndAngle=4.71239
    g61: ArcOfCircle [constr] CenterX=14.4 CenterY=5.6 CenterZ=0 NormalX=0 NormalY=0 NormalZ=1 AngleXU=0 Radius=3 StartAngle=4.71239 EndAngle=6.28319
    g62: ArcOfCircle [constr] CenterX=29.8 CenterY=5.6 CenterZ=0 NormalX=0 NormalY=0 NormalZ=1 AngleXU=0 Radius=4.4 StartAngle=3.14159 EndAngle=4.71239
    g63: LineSegment [constr] StartX=-45 StartY=1.2 StartZ=0 EndX=-45 EndY=-5.8 EndZ=0
    g64: LineSegment [constr] StartX=-45 StartY=-5.8 StartZ=0 EndX=29.8 EndY=-5.8 EndZ=0
    g65: LineSegment StartX=29.8 StartY=66 StartZ=0 EndX=-45 EndY=66 EndZ=0
    g66: LineSegment [constr] StartX=-45 StartY=66 StartZ=0 EndX=-45 EndY=59 EndZ=0
    g67: ArcOfCircle CenterX=-45 CenterY=62.5 CenterZ=0 NormalX=0 NormalY=0 NormalZ=1 AngleXU=0 Radius=3.5 StartAngle=1.5708 EndAngle=4.71239
    g68: ArcOfCircle CenterX=29.8 CenterY=62.5 CenterZ=0 NormalX=0 NormalY=0 NormalZ=1 AngleXU=0 Radius=3.5 StartAngle=4.71239 EndAngle=7.85398
    g69: ArcOfCircle [constr] CenterX=29.8 CenterY=-2.3 CenterZ=0 NormalX=0 NormalY=0 NormalZ=1 AngleXU=0 Radius=3.5 StartAngle=4.71239 EndAngle=7.85398
    g70: ArcOfCircle [constr] CenterX=-45 CenterY=-2.3 CenterZ=0 NormalX=0 NormalY=0 NormalZ=1 AngleXU=0 Radius=3.5 StartAngle=1.5708 EndAngle=4.71239
    g71: Circle CenterX=-40.1 CenterY=62.5 CenterZ=0 NormalX=0 NormalY=0 NormalZ=1 AngleXU=0 Radius=1.5
    g72: Circle CenterX=24.9 CenterY=62.5 CenterZ=0 NormalX=0 NormalY=0 NormalZ=1 AngleXU=0 Radius=1.5
    g73: Circle [constr] CenterX=24.9 CenterY=-2.3 CenterZ=0 NormalX=0 NormalY=0 NormalZ=1 AngleXU=0 Radius=1.5
    g74: Circle [constr] CenterX=-40.1 CenterY=-2.3 CenterZ=0 NormalX=0 NormalY=0 NormalZ=1 AngleXU=0 Radius=1.5
    g75: LineSegment [constr] StartX=-40.1 StartY=62.5 StartZ=0 EndX=24.9 EndY=62.5 EndZ=0
    g76: LineSegment [constr] StartX=24.9 StartY=62.5 StartZ=0 EndX=24.9 EndY=-2.3 EndZ=0
    g77: LineSegment [constr] StartX=24.9 StartY=-2.3 StartZ=0 EndX=-40.1 EndY=-2.3 EndZ=0
    g78: LineSegment [constr] StartX=-40.1 StartY=-2.3 StartZ=0 EndX=-40.1 EndY=62.5 EndZ=0
    g79: LineSegment [constr] StartX=-40.1 StartY=62.5 StartZ=0 EndX=-36.6 EndY=54.6 EndZ=0
    g80: LineSegment [constr] StartX=21.4 StartY=54.6 StartZ=0 EndX=24.9 EndY=62.5 EndZ=0
    g81: LineSegment [constr] StartX=21.4 StartY=5.6 StartZ=0 EndX=24.9 EndY=-2.3 EndZ=0
    g82: LineSegment [constr] StartX=-40.1 StartY=-2.3 StartZ=0 EndX=-36.6 EndY=5.6 EndZ=0
    g83: LineSegment [constr] StartX=24.9 StartY=-2.3 StartZ=0 EndX=29.8 EndY=-2.3 EndZ=0
    g84: LineSegment [constr] StartX=-40.1 StartY=62.5 StartZ=0 EndX=-40.1 EndY=64 EndZ=0
    g85: LineSegment [constr] StartX=-40.1 StartY=64 StartZ=0 EndX=-40.1 EndY=66 EndZ=0
  constraints (224):
    c: Coincident(g4,g5)
    c: Coincident(g5,g6)
    c: Coincident(g6,g7)
    c: Coincident(g7,g4)
    c: Horizontal(g4)
    c: Horizontal(g6)
    c: Vertical(g5)
    c: Vertical(g7)
    c: Coincident(g4,g0)
    c: Coincident(g5,g2)
    c: Coincident(g3,g6)
    c: Coincident(g1,g4)
    c: Equal(g0,g1)
    c: Equal(g1,g2)
    c: Equal(g2,g3)
    c: DistanceY(g7,g7) = 49
    c: DistanceX(g4,g4) = 58
    c: Radius(g0) = 1.375
    c: Vertical(g8)
    c: Vertical(g9)
    c: Equal(g8,g9)
    c: Coincident(g8,g10)
    c: Horizontal(g10)
    c: Coincident(g10,g11)
    c: Vertical(g11)
    c: Coincident(g11,g12)
    c: Horizontal(g12)
    c: Coincident(g12,g13)
    c: Vertical(g13)
    c: Coincident(g13,g14)
    c: Horizontal(g14)
    c: Coincident(g14,g15)
    c: Vertical(g15)
    c: Coincident(g15,g16)
    c: Horizontal(g16)
    c: Coincident(g16,g17)
    c: Vertical(g17)
    c: Coincident(g17,g18)
    c: Horizontal(g18)
    c: DistanceX(g18,g3) = 22
    c: Coincident(g18,g19)
    c: Vertical(g19)
    c: Coincident(g19,g20)
    c: Horizontal(g20)
    c: Coincident(g20,g21)
    c: Vertical(g21)
    c: Coincident(g21,g22)
    c: Horizontal(g22)
    c: Coincident(g22,g23)
    c: Vertical(g23)
    c: Coincident(g23,g24)
    c: Horizontal(g24)
    c: Coincident(g24,g25)
    c: Vertical(g25)
    c: Coincident(g25,g26)
    c: Horizontal(g26)
    c: Coincident(g26,g27)
    c: Vertical(g27)
    c: Coincident(g27,g28)
    c: Coincident(g28,g9)
    c: Horizontal(g28)
    c: Coincident(g29,g20)
    c: Coincident(g29,g23)
    c: Horizontal(g29)
    c: Coincident(g30,g17)
    c: Coincident(g30,g14)
    c: Horizontal(g30)
    c: Coincident(g31,g13)
    c: Coincident(g31,g10)
    c: Horizontal(g31)
    c: Coincident(g32,g24)
    c: Coincident(g32,g27)
    c: Horizontal(g32)
    c: PointOnObject(g33,g22)
    c: Coincident(g33,g21)
    c: Coincident(g33,g23)
    c: PointOnObject(g34,g12)
    c: Coincident(g34,g11)
    c: Coincident(g34,g13)
    c: PointOnObject(g35,g16)
    c: Coincident(g35,g17)
    c: Coincident(g35,g15)
    c: PointOnObject(g36,g26)
    c: Coincident(g36,g27)
    c: Coincident(g25,g36)
    c: Coincident(g36,g1)
    c: Radius(g36) = 4
    c: Equal(g33,g36)
    c: Equal(g36,g34)
    c: Equal(g34,g35)
    c: Coincident(g34,g2)
    c: Coincident(g35,g3)
    c: Coincident(g33,g0)
    c: Equal(g27,g11)
    c: Vertical(g37)
    c: Coincident(g37,g38)
    c: Coincident(g38,g34)
    c: Horizontal(g38)
    c: Horizontal(g39)
    c: Coincident(g39,g40)
    c: Vertical(g40)
    c: Coincident(g40,g41)
    c: Horizontal(g41)
    c: Coincident(g41,g42)
    c: Vertical(g42)
    c: Coincident(g42,g43)
    c: Coincident(g43,g35)
    c: Horizontal(g43)
    c: Horizontal(g44)
    c: Coincident(g44,g45)
    c: Vertical(g45)
    c: Vertical(g46)
    c: Coincident(g46,g47)
    c: Coincident(g47,g33)
    c: Horizontal(g47)
    c: Horizontal(g48)
    c: Coincident(g48,g49)
    c: Vertical(g49)
    c: Coincident(g49,g50)
    c: Horizontal(g50)
    c: Coincident(g50,g51)
    c: Vertical(g51)
    c: Coincident(g51,g52)
    c: Coincident(g52,g36)
    c: Horizontal(g52)
    c: Vertical(g53)
    c: Coincident(g53,g54)
    c: Coincident(g54,g36)
    c: Horizontal(g54)
    c: Coincident(g22,g48)
    c: Coincident(g16,g44)
    c: Coincident(g12,g39)
    c: Coincident(g55,g53)
    c: Coincident(g55,g36)
    c: Coincident(g56,g51)
    c: Coincident(g56,g36)
    c: Coincident(g56,g50)
    c: Coincident(g57,g48)
    c: Coincident(g57,g33)
    c: Coincident(g57,g50)
    c: Coincident(g58,g46)
    c: Coincident(g58,g33)
    c: Coincident(g59,g44)
    c: Coincident(g59,g35)
    c: Coincident(g60,g42)
    c: Coincident(g60,g35)
    c: Coincident(g60,g41)
    c: Coincident(g61,g39)
    c: Coincident(g61,g41)
    c: Coincident(g61,g34)
    c: Coincident(g62,g37)
    c: Coincident(g62,g34)
    c: DistanceX(g-1,g2) = 21.4
    c: Vertical(g63)
    c: Horizontal(g64)
    c: Horizontal(g65)
    c: PointOnObject(g67,g66)
    c: PointOnObject(g68,g9)
    c: PointOnObject(g69,g8)
    c: PointOnObject(g70,g63)
    c: Equal(g65,g64)
    c: Coincident(g8,g69)
    c: Coincident(g63,g70)
    c: Coincident(g9,g68)
    c: Coincident(g66,g67)
    c: Equal(g71,g72)
    c: Equal(g72,g73)
    c: Equal(g73,g74)
    c: Radius(g71) = 1.5
    c: Coincident(g65,g66)
    c: Coincident(g63,g64)
    c: Coincident(g64,g69)
    c: Coincident(g9,g65)
    c: Coincident(g75,g76)
    c: Coincident(g76,g77)
    c: Coincident(g77,g78)
    c: Coincident(g78,g75)
    c: Horizontal(g75)
    c: Horizontal(g77)
    c: Vertical(g76)
    c: Coincident(g75,g71)
    c: Coincident(g76,g73)
    c: Coincident(g72,g75)
    c: Coincident(g74,g77)
    c: DistanceY(g78,g78) = 64.8
    c: DistanceX(g75,g75) = 65
    c: Coincident(g79,g71)
    c: Coincident(g79,g0)
    c: Coincident(g80,g1)
    c: Coincident(g80,g72)
    c: Coincident(g81,g2)
    c: Coincident(g81,g73)
    c: Coincident(g82,g74)
    c: Coincident(g82,g3)
    c: Equal(g82,g81)
    c: Equal(g81,g80)
    c: Equal(g80,g79)
    c: Coincident(g8,g37)
    c: Coincident(g8,g62)
    c: Coincident(g8,g69)
    c: Coincident(g9,g53)
    c: Coincident(g9,g55)
    c: Coincident(g9,g68)
    c: Coincident(g46,g58)
    c: Coincident(g46,g66)
    c: Coincident(g46,g67)
    c: Coincident(g45,g59)
    c: Coincident(g45,g63)
    c: Coincident(g45,g70)
    c: DistanceY(g-1,g72) = 62.5
    c: DistanceY(g51,g51) = 3
    c: Equal(g51,g40)
    c: Coincident(g83,g73)
    c: Coincident(g83,g69)
    c: Horizontal(g83)
    c: Equal(g62,g59)
    c: Equal(g59,g58)
    c: Coincident(g84,g71)
    c: PointOnObject(g84,g71)
    c: Vertical(g84)
    c: Coincident(g85,g84)
    c: PointOnObject(g85,g65)
    c: Vertical(g85)
    c: DistanceY(g85,g85) = 2
FEATURE [Sketcher::SketchObject] Sketch001002030  label="Sketch Boden RP001"
  Placement = pos=(0,45,-16.5) rot=(0,0,-1;1.5708rad)
  sketch-geometry (86):
    g0: Circle [constr] CenterX=-36.6 CenterY=54.6 CenterZ=0 NormalX=0 NormalY=0 NormalZ=1 AngleXU=0 Radius=1.375
    g1: Circle [constr] CenterX=21.4 CenterY=54.6 CenterZ=0 NormalX=0 NormalY=0 NormalZ=1 AngleXU=0 Radius=1.375
    g2: Circle CenterX=21.4 CenterY=5.6 CenterZ=0 NormalX=0 NormalY=0 NormalZ=1 AngleXU=0 Radius=1.375
    g3: Circle CenterX=-36.6 CenterY=5.6 CenterZ=0 NormalX=0 NormalY=0 NormalZ=1 AngleXU=0 Radius=1.375
    g4: LineSegment [constr] StartX=-36.6 StartY=54.6 StartZ=0 EndX=21.4 EndY=54.6 EndZ=0
    g5: LineSegment [constr] StartX=21.4 StartY=54.6 StartZ=0 EndX=21.4 EndY=5.6 EndZ=0
    g6: LineSegment [constr] StartX=21.4 StartY=5.6 StartZ=0 EndX=-36.6 EndY=5.6 EndZ=0
    g7: LineSegment [constr] StartX=-36.6 StartY=5.6 StartZ=0 EndX=-36.6 EndY=54.6 EndZ=0
    g8: LineSegment [constr] StartX=29.8 StartY=-5.8 StartZ=0 EndX=29.8 EndY=1.2 EndZ=0
    g9: LineSegment [constr] StartX=29.8 StartY=59 StartZ=0 EndX=29.8 EndY=66 EndZ=0
    g10: LineSegment [constr] StartX=29.8 StartY=1.2 StartZ=0 EndX=25.4 EndY=1.2 EndZ=0
    g11: LineSegment [constr] StartX=25.4 StartY=1.2 StartZ=0 EndX=25.4 EndY=5.6 EndZ=0
    g12: LineSegment [constr] StartX=25.4 StartY=5.6 StartZ=0 EndX=17.4 EndY=5.6 EndZ=0
    g13: LineSegment [constr] StartX=17.4 StartY=5.6 StartZ=0 EndX=17.4 EndY=1.2 EndZ=0
    g14: LineSegment [constr] StartX=17.4 StartY=1.2 StartZ=0 EndX=-32.6 EndY=1.2 EndZ=0
    g15: LineSegment [constr] StartX=-32.6 StartY=1.2 StartZ=0 EndX=-32.6 EndY=5.6 EndZ=0
    g16: LineSegment [constr] StartX=-32.6 StartY=5.6 StartZ=0 EndX=-40.6 EndY=5.6 EndZ=0
    g17: LineSegment [constr] StartX=-40.6 StartY=5.6 StartZ=0 EndX=-40.6 EndY=1.2 EndZ=0
    g18: LineSegment [constr] StartX=-40.6 StartY=1.2 StartZ=0 EndX=-58.6 EndY=1.2 EndZ=0
    g19: LineSegment [constr] StartX=-58.6 StartY=1.2 StartZ=0 EndX=-58.6 EndY=59 EndZ=0
    g20: LineSegment [constr] StartX=-58.6 StartY=59 StartZ=0 EndX=-40.6 EndY=59 EndZ=0
    g21: LineSegment [constr] StartX=-40.6 StartY=59 StartZ=0 EndX=-40.6 EndY=54.6 EndZ=0
    g22: LineSegment [constr] StartX=-40.6 StartY=54.6 StartZ=0 EndX=-32.6 EndY=54.6 EndZ=0
    g23: LineSegment [constr] StartX=-32.6 StartY=54.6 StartZ=0 EndX=-32.6 EndY=59 EndZ=0
    g24: LineSegment [constr] StartX=-32.6 StartY=59 StartZ=0 EndX=17.4 EndY=59 EndZ=0
    g25: LineSegment [constr] StartX=17.4 StartY=59 StartZ=0 EndX=17.4 EndY=54.6 EndZ=0
    g26: LineSegment [constr] StartX=17.4 StartY=54.6 StartZ=0 EndX=25.4 EndY=54.6 EndZ=0
    g27: LineSegment [constr] StartX=25.4 StartY=54.6 StartZ=0 EndX=25.4 EndY=59 EndZ=0
    g28: LineSegment [constr] StartX=25.4 StartY=59 StartZ=0 EndX=29.8 EndY=59 EndZ=0
    g29: LineSegment [constr] StartX=-40.6 StartY=59 StartZ=0 EndX=-32.6 EndY=59 EndZ=0
    g30: LineSegment [constr] StartX=-40.6 StartY=1.2 StartZ=0 EndX=-32.6 EndY=1.2 EndZ=0
    g31: LineSegment [constr] StartX=17.4 StartY=1.2 StartZ=0 EndX=25.4 EndY=1.2 EndZ=0
    g32: LineSegment [constr] StartX=17.4 StartY=59 StartZ=0 EndX=25.4 EndY=59 EndZ=0
    g33: ArcOfCircle [constr] CenterX=-36.6 CenterY=54.6 CenterZ=0 NormalX=0 NormalY=0 NormalZ=1 AngleXU=0 Radius=4 StartAngle=3.14159 EndAngle=6.28319
    g34: ArcOfCircle CenterX=21.4 CenterY=5.6 CenterZ=0 NormalX=0 NormalY=0 NormalZ=1 AngleXU=0 Radius=4 StartAngle=0 EndAngle=3.14159
    g35: ArcOfCircle CenterX=-36.6 CenterY=5.6 CenterZ=0 NormalX=0 NormalY=0 NormalZ=1 AngleXU=0 Radius=4 StartAngle=2e-16 EndAngle=3.14159
    g36: ArcOfCircle [constr] CenterX=21.4 CenterY=54.6 CenterZ=0 NormalX=0 NormalY=0 NormalZ=1 AngleXU=0 Radius=4 StartAngle=3.14159 EndAngle=6.28319
    g37: LineSegment [constr] StartX=29.8 StartY=1.2 StartZ=0 EndX=29.8 EndY=5.6 EndZ=0
    g38: LineSegment [constr] StartX=29.8 StartY=5.6 StartZ=0 EndX=25.4 EndY=5.6 EndZ=0
    g39: LineSegment [constr] StartX=17.4 StartY=5.6 StartZ=0 EndX=14.4 EndY=5.6 EndZ=0
    g40: LineSegment [constr] StartX=14.4 StartY=5.6 StartZ=0 EndX=14.4 EndY=2.6 EndZ=0
    g41: LineSegment StartX=14.4 StartY=2.6 StartZ=0 EndX=-29.6 EndY=2.6 EndZ=0
    g42: LineSegment [constr] StartX=-29.6 StartY=2.6 StartZ=0 EndX=-29.6 EndY=5.6 EndZ=0
    g43: LineSegment [constr] StartX=-29.6 StartY=5.6 StartZ=0 EndX=-32.6 EndY=5.6 EndZ=0
    g44: LineSegment [constr] StartX=-40.6 StartY=5.6 StartZ=0 EndX=-45 EndY=5.6 EndZ=0
    g45: LineSegment [constr] StartX=-45 StartY=5.6 StartZ=0 EndX=-45 EndY=1.2 EndZ=0
    g46: LineSegment [constr] StartX=-45 StartY=59 StartZ=0 EndX=-45 EndY=54.6 EndZ=0
    g47: LineSegment [constr] StartX=-45 StartY=54.6 StartZ=0 EndX=-40.6 EndY=54.6 EndZ=0
    g48: LineSegment [constr] StartX=-32.6 StartY=54.6 StartZ=0 EndX=-29.6 EndY=54.6 EndZ=0
    g49: LineSegment [constr] StartX=-29.6 StartY=54.6 StartZ=0 EndX=-29.6 EndY=57.6 EndZ=0
    g50: LineSegment [constr] StartX=-29.6 StartY=57.6 StartZ=0 EndX=14.4 EndY=57.6 EndZ=0
    g51: LineSegment [constr] StartX=14.4 StartY=57.6 StartZ=0 EndX=14.4 EndY=54.6 EndZ=0
    g52: LineSegment [constr] StartX=14.4 StartY=54.6 StartZ=0 EndX=17.4 EndY=54.6 EndZ=0
    g53: LineSegment [constr] StartX=29.8 StartY=59 StartZ=0 EndX=29.8 EndY=54.6 EndZ=0
    g54: LineSegment [constr] StartX=29.8 StartY=54.6 StartZ=0 EndX=25.4 EndY=54.6 EndZ=0
    g55: ArcOfCircle [constr] CenterX=29.8 CenterY=54.6 CenterZ=0 NormalX=0 NormalY=0 NormalZ=1 AngleXU=0 Radius=4.4 StartAngle=1.5708 EndAngle=3.14159
    g56: ArcOfCircle [constr] CenterX=14.4 CenterY=54.6 CenterZ=0 NormalX=0 NormalY=0 NormalZ=1 AngleXU=0 Radius=3 StartAngle=0 EndAngle=1.5708
    g57: ArcOfCircle [constr] CenterX=-29.6 CenterY=54.6 CenterZ=0 NormalX=0 NormalY=0 NormalZ=1 AngleXU=0 Radius=3 StartAngle=1.5708 EndAngle=3.14159
    g58: ArcOfCircle [constr] CenterX=-45 CenterY=54.6 CenterZ=0 NormalX=0 NormalY=0 NormalZ=1 AngleXU=0 Radius=4.4 StartAngle=0 EndAngle=1.5708
    g59: ArcOfCircle CenterX=-45 CenterY=5.6 CenterZ=0 NormalX=0 NormalY=0 NormalZ=1 AngleXU=0 Radius=4.4 StartAngle=4.71239 EndAngle=6.28319
    g60: ArcOfCircle CenterX=-29.6 CenterY=5.6 CenterZ=0 NormalX=0 NormalY=0 NormalZ=1 AngleXU=0 Radius=3 StartAngle=3.14159 EndAngle=4.71239
    g61: ArcOfCircle CenterX=14.4 CenterY=5.6 CenterZ=0 NormalX=0 NormalY=0 NormalZ=1 AngleXU=0 Radius=3 StartAngle=4.71239 EndAngle=6.28319
    g62: ArcOfCircle CenterX=29.8 CenterY=5.6 CenterZ=0 NormalX=0 NormalY=0 NormalZ=1 AngleXU=0 Radius=4.4 StartAngle=3.14159 EndAngle=4.71239
    g63: LineSegment [constr] StartX=-45 StartY=1.2 StartZ=0 EndX=-45 EndY=-5.8 EndZ=0
    g64: LineSegment StartX=-45 StartY=-5.8 StartZ=0 EndX=29.8 EndY=-5.8 EndZ=0
    g65: LineSegment [constr] StartX=29.8 StartY=66 StartZ=0 EndX=-45 EndY=66 EndZ=0
    g66: LineSegment [constr] StartX=-45 StartY=66 StartZ=0 EndX=-45 EndY=59 EndZ=0
    g67: ArcOfCircle [constr] CenterX=-45 CenterY=62.5 CenterZ=0 NormalX=0 NormalY=0 NormalZ=1 AngleXU=0 Radius=3.5 StartAngle=1.5708 EndAngle=4.71239
    g68: ArcOfCircle [constr] CenterX=29.8 CenterY=62.5 CenterZ=0 NormalX=0 NormalY=0 NormalZ=1 AngleXU=0 Radius=3.5 StartAngle=4.71239 EndAngle=7.85398
    g69: ArcOfCircle CenterX=29.8 CenterY=-2.3 CenterZ=0 NormalX=0 NormalY=0 NormalZ=1 AngleXU=0 Radius=3.5 StartAngle=4.71239 EndAngle=7.85398
    g70: ArcOfCircle CenterX=-45 CenterY=-2.3 CenterZ=0 NormalX=0 NormalY=0 NormalZ=1 AngleXU=0 Radius=3.5 StartAngle=1.5708 EndAngle=4.71239
    g71: Circle [constr] CenterX=-40.1 CenterY=62.5 CenterZ=0 NormalX=0 NormalY=0 NormalZ=1 AngleXU=0 Radius=1.5
    g72: Circle [constr] CenterX=24.9 CenterY=62.5 CenterZ=0 NormalX=0 NormalY=0 NormalZ=1 AngleXU=0 Radius=1.5
    g73: Circle CenterX=24.9 CenterY=-2.3 CenterZ=0 NormalX=0 NormalY=0 NormalZ=1 AngleXU=0 Radius=1.5
    g74: Circle CenterX=-40.1 CenterY=-2.3 CenterZ=0 NormalX=0 NormalY=0 NormalZ=1 AngleXU=0 Radius=1.5
    g75: LineSegment [constr] StartX=-40.1 StartY=62.5 StartZ=0 EndX=24.9 EndY=62.5 EndZ=0
    g76: LineSegment [constr] StartX=24.9 StartY=62.5 StartZ=0 EndX=24.9 EndY=-2.3 EndZ=0
    g77: LineSegment [constr] StartX=24.9 StartY=-2.3 StartZ=0 EndX=-40.1 EndY=-2.3 EndZ=0
    g78: LineSegment [constr] StartX=-40.1 StartY=-2.3 StartZ=0 EndX=-40.1 EndY=62.5 EndZ=0
    g79: LineSegment [constr] StartX=-40.1 StartY=62.5 StartZ=0 EndX=-36.6 EndY=54.6 EndZ=0
    g80: LineSegment [constr] StartX=21.4 StartY=54.6 StartZ=0 EndX=24.9 EndY=62.5 EndZ=0
    g81: LineSegment [constr] StartX=21.4 StartY=5.6 StartZ=0 EndX=24.9 EndY=-2.3 EndZ=0
    g82: LineSegment [constr] StartX=-40.1 StartY=-2.3 StartZ=0 EndX=-36.6 EndY=5.6 EndZ=0
    g83: LineSegment [constr] StartX=24.9 StartY=-2.3 StartZ=0 EndX=29.8 EndY=-2.3 EndZ=0
    g84: LineSegment [constr] StartX=-40.1 StartY=62.5 StartZ=0 EndX=-40.1 EndY=64 EndZ=0
    g85: LineSegment [constr] StartX=-40.1 StartY=64 StartZ=0 EndX=-40.1 EndY=66 EndZ=0
  constraints (224):
    c: Coincident(g4,g5)
    c: Coincident(g5,g6)
    c: Coincident(g6,g7)
    c: Coincident(g7,g4)
    c: Horizontal(g4)
    c: Horizontal(g6)
    c: Vertical(g5)
    c: Vertical(g7)
    c: Coincident(g4,g0)
    c: Coincident(g5,g2)
    c: Coincident(g3,g6)
    c: Coincident(g1,g4)
    c: Equal(g0,g1)
    c: Equal(g1,g2)
    c: Equal(g2,g3)
    c: DistanceY(g7,g7) = 49
    c: DistanceX(g4,g4) = 58
    c: Radius(g0) = 1.375
    c: Vertical(g8)
    c: Vertical(g9)
    c: Equal(g8,g9)
    c: Coincident(g8,g10)
    c: Horizontal(g10)
    c: Coincident(g10,g11)
    c: Vertical(g11)
    c: Coincident(g11,g12)
    c: Horizontal(g12)
    c: Coincident(g12,g13)
    c: Vertical(g13)
    c: Coincident(g13,g14)
    c: Horizontal(g14)
    c: Coincident(g14,g15)
    c: Vertical(g15)
    c: Coincident(g15,g16)
    c: Horizontal(g16)
    c: Coincident(g16,g17)
    c: Vertical(g17)
    c: Coincident(g17,g18)
    c: Horizontal(g18)
    c: DistanceX(g18,g3) = 22
    c: Coincident(g18,g19)
    c: Vertical(g19)
    c: Coincident(g19,g20)
    c: Horizontal(g20)
    c: Coincident(g20,g21)
    c: Vertical(g21)
    c: Coincident(g21,g22)
    c: Horizontal(g22)
    c: Coincident(g22,g23)
    c: Vertical(g23)
    c: Coincident(g23,g24)
    c: Horizontal(g24)
    c: Coincident(g24,g25)
    c: Vertical(g25)
    c: Coincident(g25,g26)
    c: Horizontal(g26)
    c: Coincident(g26,g27)
    c: Vertical(g27)
    c: Coincident(g27,g28)
    c: Coincident(g28,g9)
    c: Horizontal(g28)
    c: Coincident(g29,g20)
    c: Coincident(g29,g23)
    c: Horizontal(g29)
    c: Coincident(g30,g17)
    c: Coincident(g30,g14)
    c: Horizontal(g30)
    c: Coincident(g31,g13)
    c: Coincident(g31,g10)
    c: Horizontal(g31)
    c: Coincident(g32,g24)
    c: Coincident(g32,g27)
    c: Horizontal(g32)
    c: PointOnObject(g33,g22)
    c: Coincident(g33,g21)
    c: Coincident(g33,g23)
    c: PointOnObject(g34,g12)
    c: Coincident(g34,g11)
    c: Coincident(g34,g13)
    c: PointOnObject(g35,g16)
    c: Coincident(g35,g17)
    c: Coincident(g35,g15)
    c: PointOnObject(g36,g26)
    c: Coincident(g36,g27)
    c: Coincident(g25,g36)
    c: Coincident(g36,g1)
    c: Radius(g36) = 4
    c: Equal(g33,g36)
    c: Equal(g36,g34)
    c: Equal(g34,g35)
    c: Coincident(g34,g2)
    c: Coincident(g35,g3)
    c: Coincident(g33,g0)
    c: Equal(g27,g11)
    c: Vertical(g37)
    c: Coincident(g37,g38)
    c: Coincident(g38,g34)
    c: Horizontal(g38)
    c: Horizontal(g39)
    c: Coincident(g39,g40)
    c: Vertical(g40)
    c: Coincident(g40,g41)
    c: Horizontal(g41)
    c: Coincident(g41,g42)
    c: Vertical(g42)
    c: Coincident(g42,g43)
    c: Coincident(g43,g35)
    c: Horizontal(g43)
    c: Horizontal(g44)
    c: Coincident(g44,g45)
    c: Vertical(g45)
    c: Vertical(g46)
    c: Coincident(g46,g47)
    c: Coincident(g47,g33)
    c: Horizontal(g47)
    c: Horizontal(g48)
    c: Coincident(g48,g49)
    c: Vertical(g49)
    c: Coincident(g49,g50)
    c: Horizontal(g50)
    c: Coincident(g50,g51)
    c: Vertical(g51)
    c: Coincident(g51,g52)
    c: Coincident(g52,g36)
    c: Horizontal(g52)
    c: Vertical(g53)
    c: Coincident(g53,g54)
    c: Coincident(g54,g36)
    c: Horizontal(g54)
    c: Coincident(g22,g48)
    c: Coincident(g16,g44)
    c: Coincident(g12,g39)
    c: Coincident(g55,g53)
    c: Coincident(g55,g36)
    c: Coincident(g56,g51)
    c: Coincident(g56,g36)
    c: Coincident(g56,g50)
    c: Coincident(g57,g48)
    c: Coincident(g57,g33)
    c: Coincident(g57,g50)
    c: Coincident(g58,g46)
    c: Coincident(g58,g33)
    c: Coincident(g59,g44)
    c: Coincident(g59,g35)
    c: Coincident(g60,g42)
    c: Coincident(g60,g35)
    c: Coincident(g60,g41)
    c: Coincident(g61,g39)
    c: Coincident(g61,g41)
    c: Coincident(g61,g34)
    c: Coincident(g62,g37)
    c: Coincident(g62,g34)
    c: DistanceX(g-1,g2) = 21.4
    c: Vertical(g63)
    c: Horizontal(g64)
    c: Horizontal(g65)
    c: PointOnObject(g67,g66)
    c: PointOnObject(g68,g9)
    c: PointOnObject(g69,g8)
    c: PointOnObject(g70,g63)
    c: Equal(g65,g64)
    c: Coincident(g8,g69)
    c: Coincident(g63,g70)
    c: Coincident(g9,g68)
    c: Coincident(g66,g67)
    c: Equal(g71,g72)
    c: Equal(g72,g73)
    c: Equal(g73,g74)
    c: Radius(g71) = 1.5
    c: Coincident(g65,g66)
    c: Coincident(g63,g64)
    c: Coincident(g64,g69)
    c: Coincident(g9,g65)
    c: Coincident(g75,g76)
    c: Coincident(g76,g77)
    c: Coincident(g77,g78)
    c: Coincident(g78,g75)
    c: Horizontal(g75)
    c: Horizontal(g77)
    c: Vertical(g76)
    c: Coincident(g75,g71)
    c: Coincident(g76,g73)
    c: Coincident(g72,g75)
    c: Coincident(g74,g77)
    c: DistanceY(g78,g78) = 64.8
    c: DistanceX(g75,g75) = 65
    c: Coincident(g79,g71)
    c: Coincident(g79,g0)
    c: Coincident(g80,g1)
    c: Coincident(g80,g72)
    c: Coincident(g81,g2)
    c: Coincident(g81,g73)
    c: Coincident(g82,g74)
    c: Coincident(g82,g3)
    c: Equal(g82,g81)
    c: Equal(g81,g80)
    c: Equal(g80,g79)
    c: Coincident(g8,g37)
    c: Coincident(g8,g62)
    c: Coincident(g8,g69)
    c: Coincident(g9,g53)
    c: Coincident(g9,g55)
    c: Coincident(g9,g68)
    c: Coincident(g46,g58)
    c: Coincident(g46,g66)
    c: Coincident(g46,g67)
    c: Coincident(g45,g59)
    c: Coincident(g45,g63)
    c: Coincident(g45,g70)
    c: DistanceY(g-1,g72) = 62.5
    c: DistanceY(g51,g51) = 3
    c: Equal(g51,g40)
    c: Coincident(g83,g73)
    c: Coincident(g83,g69)
    c: Horizontal(g83)
    c: Equal(g62,g59)
    c: Equal(g59,g58)
    c: Coincident(g84,g71)
    c: PointOnObject(g84,g71)
    c: Vertical(g84)
    c: Coincident(g85,g84)
    c: PointOnObject(g85,g65)
    c: Vertical(g85)
    c: DistanceY(g85,g85) = 2
FEATURE [PartDesign::Pad] Pad023
  Length = 3
  Length2 = 100
  Placement = pos=(0,45,-16.5) rot=(0,0,-1;1.5708rad)
  Profile = -> Sketch001002028
  Type = 0
FEATURE [PartDesign::Body] Body023
  Group = -> [Sketch001002028,Pad023]
  Origin = -> Origin031
  Tip = -> Pad023
FEATURE [PartDesign::Pad] Pad024
  Length = 3
  Length2 = 100
  Placement = pos=(0,45,-16.5) rot=(0,0,-1;1.5708rad)
  Profile = -> Sketch001002030
  Type = 0
FEATURE [PartDesign::Body] Body024
  Group = -> [Sketch001002030,Pad024]
  Origin = -> Origin032
  Tip = -> Pad024
FEATURE [Part::MultiFuse] Fusion  label="Fusion RP"
  Placement = pos=(-20,0,0) rot=(0,0,1;0rad)
  Refine = true
  Shapes = -> [Body024,Body023]
FEATURE [Sketcher::SketchObject] Sketch001002031  label="Sketch Mitte H"
  Placement = pos=(-39.5,106,0) rot=(0,1,0;1.5708rad)
  sketch-geometry (48):
    g0: LineSegment StartX=-17.5 StartY=0 StartZ=0 EndX=-14 EndY=0 EndZ=0
    g1: LineSegment StartX=-14 StartY=0 StartZ=0 EndX=-14 EndY=3 EndZ=0
    g2: LineSegment StartX=-14 StartY=3 StartZ=0 EndX=-4 EndY=3 EndZ=0
    g3: LineSegment StartX=-4 StartY=3 StartZ=0 EndX=-4 EndY=0 EndZ=0
    g4: LineSegment [constr] StartX=-4 StartY=0 StartZ=0 EndX=4 EndY=0 EndZ=0
    g5: LineSegment StartX=4 StartY=0 StartZ=0 EndX=4 EndY=3 EndZ=0
    g6: LineSegment StartX=4 StartY=3 StartZ=0 EndX=14 EndY=3 EndZ=0
    g7: LineSegment StartX=14 StartY=3 StartZ=0 EndX=14 EndY=0 EndZ=0
    g8: LineSegment StartX=14 StartY=0 StartZ=0 EndX=16.5 EndY=0 EndZ=0
    g9: LineSegment StartX=-4 StartY=0 StartZ=0 EndX=-1.5 EndY=0 EndZ=0
    g10: LineSegment StartX=-1.5 StartY=0 StartZ=0 EndX=-1.5 EndY=-5 EndZ=0
    g11: LineSegment StartX=-1.5 StartY=-5 StartZ=0 EndX=-2.75 EndY=-5 EndZ=0
    g12: LineSegment StartX=-2.75 StartY=-5 StartZ=0 EndX=-2.75 EndY=-7.3 EndZ=0
    g13: LineSegment StartX=-2.75 StartY=-7.3 StartZ=0 EndX=-1.5 EndY=-7.3 EndZ=0
    g14: LineSegment StartX=-1.5 StartY=-7.3 StartZ=0 EndX=-1.5 EndY=-10.3 EndZ=0
    g15: LineSegment StartX=-1.5 StartY=-10.3 StartZ=0 EndX=1.5 EndY=-10.3 EndZ=0
    g16: LineSegment StartX=1.5 StartY=-10.3 StartZ=0 EndX=1.5 EndY=-7.3 EndZ=0
    g17: LineSegment StartX=1.5 StartY=-7.3 StartZ=0 EndX=2.75 EndY=-7.3 EndZ=0
    g18: LineSegment StartX=2.75 StartY=-7.3 StartZ=0 EndX=2.75 EndY=-5 EndZ=0
    g19: LineSegment StartX=2.75 StartY=-5 StartZ=0 EndX=1.5 EndY=-5 EndZ=0
    g20: LineSegment StartX=1.5 StartY=-5 StartZ=0 EndX=1.5 EndY=0 EndZ=0
    g21: LineSegment StartX=1.5 StartY=0 StartZ=0 EndX=4 EndY=0 EndZ=0
    g22: LineSegment StartX=19.4 StartY=-18 StartZ=0 EndX=19.4 EndY=-23 EndZ=0
    g23: LineSegment StartX=19.4 StartY=-23 StartZ=0 EndX=16.5 EndY=-23 EndZ=0
    g24: LineSegment [constr] StartX=16.5 StartY=-15 StartZ=0 EndX=11.5 EndY=-15 EndZ=0
    g25: LineSegment StartX=11.5 StartY=-15 StartZ=0 EndX=11.5 EndY=-13.75 EndZ=0
    g26: LineSegment StartX=11.5 StartY=-13.75 StartZ=0 EndX=9.2 EndY=-13.75 EndZ=0
    g27: LineSegment StartX=9.2 StartY=-13.75 StartZ=0 EndX=9.2 EndY=-15 EndZ=0
    g28: LineSegment StartX=9.2 StartY=-15 StartZ=0 EndX=6.2 EndY=-15 EndZ=0
    g29: LineSegment StartX=6.2 StartY=-15 StartZ=0 EndX=6.2 EndY=-18 EndZ=0
    g30: LineSegment StartX=6.2 StartY=-18 StartZ=0 EndX=9.2 EndY=-18 EndZ=0
    g31: LineSegment StartX=9.2 StartY=-18 StartZ=0 EndX=9.2 EndY=-19.25 EndZ=0
    g32: LineSegment StartX=9.2 StartY=-19.25 StartZ=0 EndX=11.5 EndY=-19.25 EndZ=0
    g33: LineSegment StartX=11.5 StartY=-19.25 StartZ=0 EndX=11.5 EndY=-18 EndZ=0
    g34: LineSegment [constr] StartX=11.5 StartY=-18 StartZ=0 EndX=16.5 EndY=-18 EndZ=0
    g35: LineSegment StartX=16.5 StartY=-23 StartZ=0 EndX=16.5 EndY=-28 EndZ=0
    g36: LineSegment StartX=16.5 StartY=0 StartZ=0 EndX=16.5 EndY=-10 EndZ=0
    g37: LineSegment StartX=16.5 StartY=-10 StartZ=0 EndX=19.4 EndY=-10 EndZ=0
    g38: LineSegment StartX=19.4 StartY=-10 StartZ=0 EndX=19.4 EndY=-15 EndZ=0
    g39: LineSegment StartX=19.4 StartY=-15 StartZ=0 EndX=11.5 EndY=-15 EndZ=0
    g40: LineSegment [constr] StartX=16.5 StartY=-10 StartZ=0 EndX=16.5 EndY=-15 EndZ=0
    g41: LineSegment [constr] StartX=16.5 StartY=-18 StartZ=0 EndX=16.5 EndY=-23 EndZ=0
    g42: LineSegment StartX=19.4 StartY=-18 StartZ=0 EndX=11.5 EndY=-18 EndZ=0
    g43: LineSegment [constr] StartX=-17.5 StartY=0 StartZ=0 EndX=-17.5 EndY=-28 EndZ=0
    g44: LineSegment [constr] StartX=16.5 StartY=-28 StartZ=0 EndX=-17.5 EndY=-28 EndZ=0
    g45: LineSegment StartX=-17.5 StartY=0 StartZ=0 EndX=-17.5 EndY=-12 EndZ=0
    g46: LineSegment StartX=-17.5 StartY=-12 StartZ=0 EndX=4.5 EndY=-28 EndZ=0
    g47: LineSegment StartX=4.5 StartY=-28 StartZ=0 EndX=16.5 EndY=-28 EndZ=0
  constraints (139):
    c: Horizontal(g0)
    c: Coincident(g0,g1)
    c: Vertical(g1)
    c: Coincident(g1,g2)
    c: Horizontal(g2)
    c: Coincident(g2,g3)
    c: Vertical(g3)
    c: Coincident(g3,g4)
    c: Horizontal(g4)
    c: Coincident(g4,g5)
    c: Vertical(g5)
    c: Coincident(g5,g6)
    c: Horizontal(g6)
    c: Coincident(g6,g7)
    c: Vertical(g7)
    c: Coincident(g7,g8)
    c: Horizontal(g8)
    c: Equal(g2,g6)
    c: Equal(g1,g3)
    c: Equal(g3,g5)
    c: Equal(g5,g7)
    c: DistanceY(g1,g1) = 3
    c: DistanceX(g2,g2) = 10
    c: Symmetric(g4,g3,g-1)
    c: Coincident(g3,g9)
    c: Horizontal(g9)
    c: Coincident(g9,g10)
    c: Vertical(g10)
    c: Coincident(g10,g11)
    c: Horizontal(g11)
    c: Coincident(g11,g12)
    c: Vertical(g12)
    c: Coincident(g12,g13)
    c: Horizontal(g13)
    c: Coincident(g13,g14)
    c: Vertical(g14)
    c: Coincident(g14,g15)
    c: Horizontal(g15)
    c: Coincident(g15,g16)
    c: Vertical(g16)
    c: Coincident(g16,g17)
    c: Horizontal(g17)
    c: Coincident(g17,g18)
    c: Vertical(g18)
    c: Coincident(g18,g19)
    c: Horizontal(g19)
    c: Coincident(g19,g20)
    c: Vertical(g20)
    c: Coincident(g20,g21)
    c: Coincident(g21,g5)
    c: Horizontal(g21)
    c: Equal(g9,g21)
    c: Equal(g14,g16)
    c: Equal(g11,g13)
    c: Equal(g13,g17)
    c: Equal(g17,g19)
    c: Equal(g12,g18)
    c: Vertical(g22)
    c: Horizontal(g23)
    c: Horizontal(g24)
    c: Coincident(g24,g25)
    c: Vertical(g25)
    c: Coincident(g25,g26)
    c: Horizontal(g26)
    c: Coincident(g26,g27)
    c: Vertical(g27)
    c: Coincident(g27,g28)
    c: Horizontal(g28)
    c: Coincident(g28,g29)
    c: Vertical(g29)
    c: Coincident(g29,g30)
    c: Horizontal(g30)
    c: Coincident(g30,g31)
    c: Vertical(g31)
    c: Coincident(g31,g32)
    c: Horizontal(g32)
    c: Coincident(g32,g33)
    c: Vertical(g33)
    c: Coincident(g33,g34)
    c: Horizontal(g34)
    c: Vertical(g35)
    c: Equal(g28,g30)
    c: Equal(g27,g25)
    c: Equal(g25,g33)
    c: Equal(g33,g31)
    c: Equal(g24,g34)
    c: Equal(g26,g32)
    c: Coincident(g22,g23)
    c: Coincident(g23,g35)
    c: DistanceX(g15,g15) = 3
    c: DistanceY(g14,g14) = 3
    c: DistanceX(g11,g11) = 1.25
    c: DistanceY(g10,g10) = 5
    c: DistanceY(g12,g12) = 2.3
    c: Vertical(g36)
    c: Coincident(g37,g36)
    c: Horizontal(g37)
    c: Coincident(g38,g37)
    c: Vertical(g38)
    c: DistanceX(g37,g37) = 2.9
    c: Equal(g15,g29)
    c: Equal(g38,g22)
    c: Equal(g18,g26)
    c: Equal(g27,g19)
    c: Equal(g24,g20)
    c: Equal(g28,g16)
    c: Coincident(g39,g25)
    c: Coincident(g38,g39)
    c: Coincident(g40,g36)
    c: Coincident(g40,g24)
    c: Vertical(g40)
    c: Coincident(g41,g34)
    c: Coincident(g41,g23)
    c: Vertical(g41)
    c: Horizontal(g39)
    c: Coincident(g42,g22)
    c: Coincident(g42,g33)
    c: Horizontal(g42)
    c: DistanceY(g38,g38) = 5
    c: Vertical(g43)
    c: Coincident(g44,g35)
    c: Horizontal(g44)
    c: Equal(g39,g42)
    c: DistanceY(g35,g35) = 5
    c: DistanceX(g44,g44) = 34
    c: Coincident(g8,g36)
    c: Coincident(g0,g43)
    c: Coincident(g43,g44)
    c: DistanceX(g8,g8) = 2.5
    c: DistanceX(g3,g5) = 8
    c: Coincident(g0,g45)
    c: Vertical(g45)
    c: Coincident(g45,g46)
    c: Coincident(g46,g47)
    c: Coincident(g47,g35)
    c: Horizontal(g47)
    c: Equal(g47,g45)
    c: DistanceY(g45,g45) = 12
    c: DistanceY(g36,g36) = 10
FEATURE [PartDesign::Pad] Pad025
  Length = 3
  Length2 = 100
  Placement = pos=(-39.5,106,0) rot=(0,1,0;1.5708rad)
  Profile = -> Sketch001002031
  Refine = true
  Type = 0
FEATURE [PartDesign::Body] Body025  label="Body Mitte H"
  Group = -> [Sketch001002031,Pad025]
  Origin = -> Origin033
  Tip = -> Pad025
FEATURE [Part::Fillet] Fillet036  label="Fillet Mitte H"
  Base = -> Body025
  Edges = 2 edges r=6: [Edge116,Edge119]
FEATURE [Sketcher::SketchObject] Sketch001002032  label="Sketch Front002"
  Placement = pos=(0,0,0) rot=(1,0,0;1.5708rad)
  sketch-geometry (142):
    g0: LineSegment StartX=-241 StartY=22 StartZ=0 EndX=241 EndY=22 EndZ=0
    g1: LineSegment StartX=241 StartY=22 StartZ=0 EndX=241 EndY=-22 EndZ=0
    g2: LineSegment StartX=241 StartY=-22 StartZ=0 EndX=-241 EndY=-22 EndZ=0
    g3: LineSegment StartX=-241 StartY=-22 StartZ=0 EndX=-241 EndY=22 EndZ=0
    g4: LineSegment [constr] StartX=-237 StartY=19 StartZ=0 EndX=-225 EndY=19 EndZ=0
    g5: LineSegment [constr] StartX=-225 StartY=19 StartZ=0 EndX=-225 EndY=13 EndZ=0
    g6: LineSegment [constr] StartX=-225 StartY=13 StartZ=0 EndX=-237 EndY=13 EndZ=0
    g7: LineSegment [constr] StartX=-237 StartY=13 StartZ=0 EndX=-237 EndY=19 EndZ=0
    g8: LineSegment [constr] StartX=-237 StartY=-13 StartZ=0 EndX=-225 EndY=-13 EndZ=0
    g9: LineSegment [constr] StartX=-225 StartY=-13 StartZ=0 EndX=-225 EndY=-19 EndZ=0
    g10: LineSegment [constr] StartX=-225 StartY=-19 StartZ=0 EndX=-237 EndY=-19 EndZ=0
    g11: LineSegment [constr] StartX=-237 StartY=-19 StartZ=0 EndX=-237 EndY=-13 EndZ=0
    g12: LineSegment [constr] StartX=225 StartY=19 StartZ=0 EndX=237 EndY=19 EndZ=0
    g13: LineSegment [constr] StartX=237 StartY=19 StartZ=0 EndX=237 EndY=13 EndZ=0
    g14: LineSegment [constr] StartX=237 StartY=13 StartZ=0 EndX=225 EndY=13 EndZ=0
    g15: LineSegment [constr] StartX=225 StartY=13 StartZ=0 EndX=225 EndY=19 EndZ=0
    g16: LineSegment [constr] StartX=225 StartY=-13 StartZ=0 EndX=237 EndY=-13 EndZ=0
    g17: LineSegment [constr] StartX=237 StartY=-13 StartZ=0 EndX=237 EndY=-19 EndZ=0
    g18: LineSegment [constr] StartX=237 StartY=-19 StartZ=0 EndX=225 EndY=-19 EndZ=0
    g19: LineSegment [constr] StartX=225 StartY=-19 StartZ=0 EndX=225 EndY=-13 EndZ=0
    g20: LineSegment [constr] StartX=-237 StartY=19 StartZ=0 EndX=-237 EndY=22 EndZ=0
    g21: LineSegment [constr] StartX=-237 StartY=19 StartZ=0 EndX=-241 EndY=19 EndZ=0
    g22: LineSegment [constr] StartX=-237 StartY=-19 StartZ=0 EndX=-237 EndY=-22 EndZ=0
    g23: LineSegment [constr] StartX=-237 StartY=-19 StartZ=0 EndX=-241 EndY=-19 EndZ=0
    g24: LineSegment [constr] StartX=237 StartY=-19 StartZ=0 EndX=241 EndY=-19 EndZ=0
    g25: LineSegment [constr] StartX=237 StartY=-19 StartZ=0 EndX=237 EndY=-22 EndZ=0
    g26: LineSegment [constr] StartX=237 StartY=19 StartZ=0 EndX=241 EndY=19 EndZ=0
    g27: LineSegment [constr] StartX=237 StartY=19 StartZ=0 EndX=237 EndY=22 EndZ=0
    g28: LineSegment StartX=-221.6 StartY=1.7 StartZ=0 EndX=-213.4 EndY=1.7 EndZ=0
    g29: LineSegment StartX=-213.4 StartY=1.7 StartZ=0 EndX=-213.4 EndY=-1.7 EndZ=0
    g30: LineSegment StartX=-213.4 StartY=-1.7 StartZ=0 EndX=-221.6 EndY=-1.7 EndZ=0
    g31: LineSegment StartX=-221.6 StartY=-1.7 StartZ=0 EndX=-221.6 EndY=1.7 EndZ=0
    g32: LineSegment StartX=-205.6 StartY=1.7 StartZ=0 EndX=-197.4 EndY=1.7 EndZ=0
    g33: LineSegment StartX=-197.4 StartY=1.7 StartZ=0 EndX=-197.4 EndY=-1.7 EndZ=0
    g34: LineSegment StartX=-197.4 StartY=-1.7 StartZ=0 EndX=-205.6 EndY=-1.7 EndZ=0
    g35: LineSegment StartX=-205.6 StartY=-1.7 StartZ=0 EndX=-205.6 EndY=1.7 EndZ=0
    g36: LineSegment StartX=-195.7 StartY=14.1 StartZ=0 EndX=-192.3 EndY=14.1 EndZ=0
    g37: LineSegment StartX=-192.3 StartY=14.1 StartZ=0 EndX=-192.3 EndY=3.9 EndZ=0
    g38: LineSegment StartX=-192.3 StartY=3.9 StartZ=0 EndX=-195.7 EndY=3.9 EndZ=0
    g39: LineSegment StartX=-195.7 StartY=3.9 StartZ=0 EndX=-195.7 EndY=14.1 EndZ=0
    g40: LineSegment StartX=-195.7 StartY=-3.9 StartZ=0 EndX=-192.3 EndY=-3.9 EndZ=0
    g41: LineSegment StartX=-192.3 StartY=-3.9 StartZ=0 EndX=-192.3 EndY=-14.1 EndZ=0
    g42: LineSegment StartX=-192.3 StartY=-14.1 StartZ=0 EndX=-195.7 EndY=-14.1 EndZ=0
    g43: LineSegment StartX=-195.7 StartY=-14.1 StartZ=0 EndX=-195.7 EndY=-3.9 EndZ=0
    g44: LineSegment StartX=221.6 StartY=1.7 StartZ=0 EndX=213.4 EndY=1.7 EndZ=0
    g45: LineSegment StartX=213.4 StartY=1.7 StartZ=0 EndX=213.4 EndY=-1.7 EndZ=0
    g46: LineSegment StartX=213.4 StartY=-1.7 StartZ=0 EndX=221.6 EndY=-1.7 EndZ=0
    g47: LineSegment StartX=221.6 StartY=-1.7 StartZ=0 EndX=221.6 EndY=1.7 EndZ=0
    g48: LineSegment StartX=205.6 StartY=1.7 StartZ=0 EndX=197.4 EndY=1.7 EndZ=0
    g49: LineSegment StartX=197.4 StartY=1.7 StartZ=0 EndX=197.4 EndY=-1.7 EndZ=0
    g50: LineSegment StartX=197.4 StartY=-1.7 StartZ=0 EndX=205.6 EndY=-1.7 EndZ=0
    g51: LineSegment StartX=205.6 StartY=-1.7 StartZ=0 EndX=205.6 EndY=1.7 EndZ=0
    g52: LineSegment StartX=192.3 StartY=14.1 StartZ=0 EndX=195.7 EndY=14.1 EndZ=0
    g53: LineSegment StartX=195.7 StartY=14.1 StartZ=0 EndX=195.7 EndY=3.9 EndZ=0
    g54: LineSegment StartX=195.7 StartY=3.9 StartZ=0 EndX=192.3 EndY=3.9 EndZ=0
    g55: LineSegment StartX=192.3 StartY=3.9 StartZ=0 EndX=192.3 EndY=14.1 EndZ=0
    g56: LineSegment StartX=192.3 StartY=-3.9 StartZ=0 EndX=195.7 EndY=-3.9 EndZ=0
    g57: LineSegment StartX=195.7 StartY=-3.9 StartZ=0 EndX=195.7 EndY=-14.1 EndZ=0
    g58: LineSegment StartX=195.7 StartY=-14.1 StartZ=0 EndX=192.3 EndY=-14.1 EndZ=0
    g59: LineSegment StartX=192.3 StartY=-14.1 StartZ=0 EndX=192.3 EndY=-3.9 EndZ=0
    g60: Circle CenterX=209.5 CenterY=0 CenterZ=0 NormalX=0 NormalY=0 NormalZ=1 AngleXU=0 Radius=1.6
    g61: Circle CenterX=-209.5 CenterY=0 CenterZ=0 NormalX=0 NormalY=0 NormalZ=1 AngleXU=0 Radius=1.6
    g62: LineSegment [constr] StartX=-213.4 StartY=1.7 StartZ=0 EndX=-205.6 EndY=1.7 EndZ=0
    g63: LineSegment [constr] StartX=-194 StartY=3.9 StartZ=0 EndX=-194 EndY=-3.9 EndZ=0
    g64: LineSegment [constr] StartX=205.6 StartY=1.7 StartZ=0 EndX=213.4 EndY=1.7 EndZ=0
    g65: LineSegment [constr] StartX=194 StartY=3.9 StartZ=0 EndX=194 EndY=-3.9 EndZ=0
    g66: LineSegment [constr] StartX=-209.5 StartY=0 StartZ=0 EndX=-194 EndY=0 EndZ=0
    g67: LineSegment [constr] StartX=209.5 StartY=0 StartZ=0 EndX=194 EndY=0 EndZ=0
    g68: LineSegment [constr] StartX=-16.7 StartY=14.1 StartZ=0 EndX=-13.3 EndY=14.1 EndZ=0
    g69: LineSegment [constr] StartX=-13.3 StartY=14.1 StartZ=0 EndX=-13.3 EndY=3.9 EndZ=0
    g70: LineSegment [constr] StartX=-13.3 StartY=3.9 StartZ=0 EndX=-16.7 EndY=3.9 EndZ=0
    g71: LineSegment [constr] StartX=-16.7 StartY=3.9 StartZ=0 EndX=-16.7 EndY=14.1 EndZ=0
    g72: LineSegment [constr] StartX=-16.7 StartY=-3.9 StartZ=0 EndX=-13.3 EndY=-3.9 EndZ=0
    g73: LineSegment [constr] StartX=-13.3 StartY=-3.9 StartZ=0 EndX=-13.3 EndY=-14.1 EndZ=0
    g74: LineSegment [constr] StartX=-13.3 StartY=-14.1 StartZ=0 EndX=-16.7 EndY=-14.1 EndZ=0
    g75: LineSegment [constr] StartX=-16.7 StartY=-14.1 StartZ=0 EndX=-16.7 EndY=-3.9 EndZ=0
    g76: Circle [constr] CenterX=-15 CenterY=0 CenterZ=0 NormalX=0 NormalY=0 NormalZ=1 AngleXU=0 Radius=1.6
    g77: LineSegment [constr] StartX=-16.7 StartY=3.9 StartZ=0 EndX=-16.7 EndY=-3.9 EndZ=0
    g78: LineSegment StartX=-236 StartY=19 StartZ=0 EndX=-226 EndY=19 EndZ=0
    g79: LineSegment [constr] StartX=-226 StartY=19 StartZ=0 EndX=-226 EndY=18 EndZ=0
    g80: LineSegment [constr] StartX=-226 StartY=18 StartZ=0 EndX=-225 EndY=18 EndZ=0
    g81: LineSegment StartX=-225 StartY=18 StartZ=0 EndX=-225 EndY=14 EndZ=0
    g82: LineSegment [constr] StartX=-225 StartY=14 StartZ=0 EndX=-226 EndY=14 EndZ=0
    g83: LineSegment [constr] StartX=-226 StartY=14 StartZ=0 EndX=-226 EndY=13 EndZ=0
    g84: LineSegment StartX=-226 StartY=13 StartZ=0 EndX=-236 EndY=13 EndZ=0
    g85: LineSegment [constr] StartX=-236 StartY=13 StartZ=0 EndX=-236 EndY=14 EndZ=0
    g86: LineSegment [constr] StartX=-236 StartY=14 StartZ=0 EndX=-237 EndY=14 EndZ=0
    g87: LineSegment StartX=-237 StartY=14 StartZ=0 EndX=-237 EndY=18 EndZ=0
    g88: LineSegment [constr] StartX=-237 StartY=18 StartZ=0 EndX=-236 EndY=18 EndZ=0
    g89: LineSegment [constr] StartX=-236 StartY=18 StartZ=0 EndX=-236 EndY=19 EndZ=0
    g90: LineSegment StartX=-236 StartY=-13 StartZ=0 EndX=-226 EndY=-13 EndZ=0
    g91: LineSegment [constr] StartX=-226 StartY=-13 StartZ=0 EndX=-226 EndY=-14 EndZ=0
    g92: LineSegment [constr] StartX=-226 StartY=-14 StartZ=0 EndX=-225 EndY=-14 EndZ=0
    g93: LineSegment StartX=-225 StartY=-14 StartZ=0 EndX=-225 EndY=-18 EndZ=0
    g94: LineSegment [constr] StartX=-225 StartY=-18 StartZ=0 EndX=-226 EndY=-18 EndZ=0
    g95: LineSegment [constr] StartX=-226 StartY=-18 StartZ=0 EndX=-226 EndY=-19 EndZ=0
    g96: LineSegment StartX=-226 StartY=-19 StartZ=0 EndX=-236 EndY=-19 EndZ=0
    g97: LineSegment [constr] StartX=-236 StartY=-19 StartZ=0 EndX=-236 EndY=-18 EndZ=0
    g98: LineSegment [constr] StartX=-236 StartY=-18 StartZ=0 EndX=-237 EndY=-18 EndZ=0
    g99: LineSegment StartX=-237 StartY=-18 StartZ=0 EndX=-237 EndY=-14 EndZ=0
    g100: LineSegment [constr] StartX=-237 StartY=-14 StartZ=0 EndX=-236 EndY=-14 EndZ=0
    g101: LineSegment [constr] StartX=-236 StartY=-14 StartZ=0 EndX=-236 EndY=-13 EndZ=0
    g102: LineSegment StartX=226 StartY=19 StartZ=0 EndX=236 EndY=19 EndZ=0
    g103: LineSegment [constr] StartX=236 StartY=19 StartZ=0 EndX=236 EndY=18 EndZ=0
    g104: LineSegment [constr] StartX=236 StartY=18 StartZ=0 EndX=237 EndY=18 EndZ=0
    g105: LineSegment StartX=237 StartY=18 StartZ=0 EndX=237 EndY=14 EndZ=0
    g106: LineSegment [constr] StartX=237 StartY=14 StartZ=0 EndX=236 EndY=14 EndZ=0
    g107: LineSegment [constr] StartX=236 StartY=14 StartZ=0 EndX=236 EndY=13 EndZ=0
    g108: LineSegment StartX=236 StartY=13 StartZ=0 EndX=226 EndY=13 EndZ=0
    g109: LineSegment [constr] StartX=226 StartY=13 StartZ=0 EndX=226 EndY=14 EndZ=0
    g110: LineSegment [constr] StartX=226 StartY=14 StartZ=0 EndX=225 EndY=14 EndZ=0
    g111: LineSegment StartX=225 StartY=14 StartZ=0 EndX=225 EndY=18 EndZ=0
    g112: LineSegment [constr] StartX=225 StartY=18 StartZ=0 EndX=226 EndY=18 EndZ=0
    g113: LineSegment [constr] StartX=226 StartY=18 StartZ=0 EndX=226 EndY=19 EndZ=0
    g114: LineSegment StartX=226 StartY=-13 StartZ=0 EndX=236 EndY=-13 EndZ=0
    g115: LineSegment [constr] StartX=236 StartY=-13 StartZ=0 EndX=236 EndY=-14 EndZ=0
    g116: LineSegment [constr] StartX=236 StartY=-14 StartZ=0 EndX=237 EndY=-14 EndZ=0
    g117: LineSegment StartX=237 StartY=-14 StartZ=0 EndX=237 EndY=-18 EndZ=0
    g118: LineSegment [constr] StartX=237 StartY=-18 StartZ=0 EndX=236 EndY=-18 EndZ=0
    g119: LineSegment [constr] StartX=236 StartY=-18 StartZ=0 EndX=236 EndY=-19 EndZ=0
    g120: LineSegment StartX=236 StartY=-19 StartZ=0 EndX=226 EndY=-19 EndZ=0
    g121: LineSegment [constr] StartX=226 StartY=-19 StartZ=0 EndX=226 EndY=-18 EndZ=0
    g122: LineSegment [constr] StartX=226 StartY=-18 StartZ=0 EndX=225 EndY=-18 EndZ=0
    g123: LineSegment StartX=225 StartY=-18 StartZ=0 EndX=225 EndY=-14 EndZ=0
    g124: LineSegment [constr] StartX=225 StartY=-14 StartZ=0 EndX=226 EndY=-14 EndZ=0
    g125: LineSegment [constr] StartX=226 StartY=-14 StartZ=0 EndX=226 EndY=-13 EndZ=0
    g126: ArcOfCircle CenterX=226 CenterY=18 CenterZ=0 NormalX=0 NormalY=0 NormalZ=1 AngleXU=0 Radius=1 StartAngle=1.5708 EndAngle=3.14159
    g127: ArcOfCircle CenterX=226 CenterY=14 CenterZ=0 NormalX=0 NormalY=0 NormalZ=1 AngleXU=0 Radius=1 StartAngle=3.14159 EndAngle=4.71239
    g128: ArcOfCircle CenterX=236 CenterY=14 CenterZ=0 NormalX=0 NormalY=0 NormalZ=1 AngleXU=0 Radius=1 StartAngle=4.71239 EndAngle=6.28319
    g129: ArcOfCircle CenterX=236 CenterY=18 CenterZ=0 NormalX=0 NormalY=0 NormalZ=1 AngleXU=0 Radius=1 StartAngle=0 EndAngle=1.5708
    g130: ArcOfCircle CenterX=226 CenterY=-14 CenterZ=0 NormalX=0 NormalY=0 NormalZ=1 AngleXU=0 Radius=1 StartAngle=1.5708 EndAngle=3.14159
    g131: ArcOfCircle CenterX=236 CenterY=-14 CenterZ=0 NormalX=0 NormalY=0 NormalZ=1 AngleXU=0 Radius=1 StartAngle=0 EndAngle=1.5708
    g132: ArcOfCircle CenterX=236 CenterY=-18 CenterZ=0 NormalX=0 NormalY=0 NormalZ=1 AngleXU=0 Radius=1 StartAngle=4.71239 EndAngle=6.28319
    g133: ArcOfCircle CenterX=226 CenterY=-18 CenterZ=0 NormalX=0 NormalY=0 NormalZ=1 AngleXU=0 Radius=1 StartAngle=3.14159 EndAngle=4.71239
    g134: ArcOfCircle CenterX=-236 CenterY=18 CenterZ=0 NormalX=0 NormalY=0 NormalZ=1 AngleXU=0 Radius=1 StartAngle=1.5708 EndAngle=3.14159
    g135: ArcOfCircle CenterX=-226 CenterY=18 CenterZ=0 NormalX=0 NormalY=0 NormalZ=1 AngleXU=0 Radius=1 StartAngle=0 EndAngle=1.5708
    g136: ArcOfCircle CenterX=-226 CenterY=14 CenterZ=0 NormalX=0 NormalY=0 NormalZ=1 AngleXU=0 Radius=1 StartAngle=4.71239 EndAngle=6.28319
    g137: ArcOfCircle CenterX=-236 CenterY=14 CenterZ=0 NormalX=0 NormalY=0 NormalZ=1 AngleXU=0 Radius=1 StartAngle=3.14159 EndAngle=4.71239
    g138: ArcOfCircle CenterX=-236 CenterY=-14 CenterZ=0 NormalX=0 NormalY=0 NormalZ=1 AngleXU=0 Radius=1 StartAngle=1.5708 EndAngle=3.14159
    g139: ArcOfCircle CenterX=-226 CenterY=-14 CenterZ=0 NormalX=0 NormalY=0 NormalZ=1 AngleXU=0 Radius=1 StartAngle=2e-16 EndAngle=1.5708
    g140: ArcOfCircle CenterX=-226 CenterY=-18 CenterZ=0 NormalX=0 NormalY=0 NormalZ=1 AngleXU=0 Radius=1 StartAngle=4.71239 EndAngle=6.28319
    g141: ArcOfCircle CenterX=-236 CenterY=-18 CenterZ=0 NormalX=0 NormalY=0 NormalZ=1 AngleXU=0 Radius=1 StartAngle=3.14159 EndAngle=4.71239
  constraints (398):
    c: Coincident(g0,g1)
    c: Coincident(g1,g2)
    c: Coincident(g2,g3)
    c: Coincident(g3,g0)
    c: Horizontal(g0)
    c: Horizontal(g2)
    c: Vertical(g1)
    c: Vertical(g3)
    c: DistanceX(g0,g0) = 482
    c: DistanceY(g3,g3) = 44
    c: Coincident(g4,g5)
    c: Coincident(g5,g6)
    c: Coincident(g6,g7)
    c: Coincident(g7,g4)
    c: Horizontal(g4)
    c: Horizontal(g6)
    c: Vertical(g5)
    c: Vertical(g7)
    c: Coincident(g8,g9)
    c: Coincident(g9,g10)
    c: Coincident(g10,g11)
    c: Coincident(g11,g8)
    c: Horizontal(g8)
    c: Horizontal(g10)
    c: Vertical(g9)
    c: Vertical(g11)
    c: Coincident(g12,g13)
    c: Coincident(g13,g14)
    c: Coincident(g14,g15)
    c: Coincident(g15,g12)
    c: Horizontal(g12)
    c: Horizontal(g14)
    c: Vertical(g13)
    c: Vertical(g15)
    c: Coincident(g16,g17)
    c: Coincident(g17,g18)
    c: Coincident(g18,g19)
    c: Coincident(g19,g16)
    c: Horizontal(g16)
    c: Horizontal(g18)
    c: Vertical(g17)
    c: Vertical(g19)
    c: Equal(g5,g15)
    c: Equal(g15,g19)
    c: Equal(g19,g9)
    c: Equal(g6,g14)
    c: Equal(g14,g16)
    c: Equal(g16,g8)
    c: DistanceX(g4,g4) = 12
    c: DistanceY(g7,g7) = 6
    c: Coincident(g20,g4)
    c: PointOnObject(g20,g0)
    c: Vertical(g20)
    c: Coincident(g21,g4)
    c: PointOnObject(g21,g3)
    c: Horizontal(g21)
    c: Coincident(g22,g10)
    c: PointOnObject(g22,g2)
    c: Vertical(g22)
    c: Coincident(g23,g10)
    c: PointOnObject(g23,g3)
    c: Horizontal(g23)
    c: Coincident(g24,g17)
    c: PointOnObject(g24,g1)
    c: Horizontal(g24)
    c: Coincident(g25,g17)
    c: PointOnObject(g25,g2)
    c: Vertical(g25)
    c: Coincident(g26,g12)
    c: PointOnObject(g26,g1)
    c: Horizontal(g26)
    c: Coincident(g27,g12)
    c: PointOnObject(g27,g0)
    c: Vertical(g27)
    c: Equal(g21,g26)
    c: Equal(g26,g24)
    c: Equal(g24,g23)
    c: Equal(g20,g27)
    c: Equal(g27,g25)
    c: Equal(g25,g22)
    c: DistanceX(g21,g21) = 4
    c: DistanceY(g20,g20) = 3
    c: Coincident(g28,g29)
    c: Coincident(g29,g30)
    c: Coincident(g30,g31)
    c: Coincident(g31,g28)
    c: Horizontal(g28)
    c: Horizontal(g30)
    c: Vertical(g29)
    c: Vertical(g31)
    c: Coincident(g32,g33)
    c: Coincident(g33,g34)
    c: Coincident(g34,g35)
    c: Coincident(g35,g32)
    c: Horizontal(g32)
    c: Horizontal(g34)
    c: Vertical(g33)
    c: Vertical(g35)
    c: Coincident(g36,g37)
    c: Coincident(g37,g38)
    c: Coincident(g39,g36)
    c: Horizontal(g36)
    c: Horizontal(g38)
    c: Vertical(g37)
    c: Vertical(g39)
    c: Coincident(g40,g41)
    c: Coincident(g41,g42)
    c: Coincident(g42,g43)
    c: Horizontal(g40)
    c: Horizontal(g42)
    c: Vertical(g41)
    c: Vertical(g43)
    c: Coincident(g44,g45)
    c: Coincident(g45,g46)
    c: Coincident(g46,g47)
    c: Coincident(g47,g44)
    c: Horizontal(g44)
    c: Horizontal(g46)
    c: Vertical(g45)
    c: Vertical(g47)
    c: Coincident(g48,g49)
    c: Coincident(g49,g50)
    c: Coincident(g50,g51)
    c: Coincident(g51,g48)
    c: Horizontal(g48)
    c: Horizontal(g50)
    c: Vertical(g49)
    c: Vertical(g51)
    c: Coincident(g52,g53)
    c: Coincident(g54,g55)
    c: Coincident(g55,g52)
    c: Horizontal(g52)
    c: Horizontal(g54)
    c: Vertical(g53)
    c: Vertical(g55)
    c: Coincident(g57,g58)
    c: Coincident(g58,g59)
    c: Coincident(g59,g56)
    c: Horizontal(g56)
    c: Horizontal(g58)
    c: Vertical(g57)
    c: Vertical(g59)
    c: PointOnObject(g60,g-1)
    c: PointOnObject(g61,g-1)
    c: Equal(g39,g43)
    c: Equal(g43,g53)
    c: Equal(g53,g57)
    c: DistanceX(g28,g28) = 8.2
    c: DistanceY(g31,g31) = 3.4
    c: Equal(g29,g35)
    c: Equal(g35,g38)
    c: Equal(g38,g40)
    c: Equal(g40,g54)
    c: Equal(g54,g56)
    c: Equal(g56,g51)
    c: Equal(g51,g45)
    c: Symmetric(g34,g28,g61)
    c: Coincident(g62,g28)
    c: Coincident(g62,g32)
    c: Horizontal(g62)
    c: Vertical(g63)
    c: Coincident(g64,g48)
    c: Coincident(g64,g44)
    c: Horizontal(g64)
    c: Symmetric(g45,g48,g60)
    c: Vertical(g65)
    c: Equal(g64,g62)
    c: Equal(g65,g63)
    c: Horizontal(g66)
    c: DistanceX(g62,g62) = 7.8
    c: Radius(g61) = 1.6
    c: Equal(g66,g67)
    c: Symmetric(g67,g66,g-1)
    c: Equal(g61,g60)
    c: Symmetric(g0,g1,g-1)
    c: Coincident(g68,g69)
    c: Coincident(g69,g70)
    c: Coincident(g70,g71)
    c: Coincident(g71,g68)
    c: Horizontal(g68)
    c: Horizontal(g70)
    c: Vertical(g69)
    c: Vertical(g71)
    c: Coincident(g72,g73)
    c: Coincident(g73,g74)
    c: Coincident(g74,g75)
    c: Coincident(g75,g72)
    c: Horizontal(g72)
    c: Horizontal(g74)
    c: Vertical(g73)
    c: Vertical(g75)
    c: PointOnObject(g76,g-1)
    c: Equal(g69,g73)
    c: Equal(g76,g60)
    c: Equal(g55,g71)
    c: Equal(g70,g72)
    c: Equal(g36,g68)
    c: Symmetric(g72,g70,g76)
    c: Coincident(g77,g70)
    c: Coincident(g77,g72)
    c: Vertical(g77)
    c: Equal(g77,g63)
    c: Equal(g30,g34)
    c: Equal(g34,g50)
    c: Equal(g50,g46)
    c: DistanceY(g39,g39) = 10.2
    c: DistanceY(g63,g63) = 7.8
    c: DistanceX(g76,g-1) = 15
    c: Horizontal(g78)
    c: Coincident(g78,g79)
    c: Vertical(g79)
    c: Coincident(g79,g80)
    c: Horizontal(g80)
    c: Coincident(g80,g81)
    c: Vertical(g81)
    c: Coincident(g81,g82)
    c: Horizontal(g82)
    c: Coincident(g82,g83)
    c: Vertical(g83)
    c: Coincident(g83,g84)
    c: Horizontal(g84)
    c: Coincident(g84,g85)
    c: Vertical(g85)
    c: Coincident(g85,g86)
    c: Horizontal(g86)
    c: Coincident(g86,g87)
    c: Vertical(g87)
    c: Coincident(g87,g88)
    c: Horizontal(g88)
    c: Coincident(g88,g89)
    c: Vertical(g89)
    c: Coincident(g78,g89)
    c: Horizontal(g90)
    c: Coincident(g90,g91)
    c: Vertical(g91)
    c: Coincident(g91,g92)
    c: Horizontal(g92)
    c: Coincident(g92,g93)
    c: Vertical(g93)
    c: Coincident(g93,g94)
    c: Horizontal(g94)
    c: Coincident(g94,g95)
    c: Vertical(g95)
    c: Coincident(g95,g96)
    c: Horizontal(g96)
    c: Coincident(g96,g97)
    c: Vertical(g97)
    c: Coincident(g97,g98)
    c: Horizontal(g98)
    c: Coincident(g98,g99)
    c: Vertical(g99)
    c: Coincident(g99,g100)
    c: Horizontal(g100)
    c: Coincident(g100,g101)
    c: Vertical(g101)
    c: Coincident(g90,g101)
    c: Horizontal(g102)
    c: Coincident(g102,g103)
    c: Vertical(g103)
    c: Coincident(g103,g104)
    c: Horizontal(g104)
    c: Coincident(g104,g105)
    c: Vertical(g105)
    c: Coincident(g105,g106)
    c: Horizontal(g106)
    c: Coincident(g106,g107)
    c: Vertical(g107)
    c: Coincident(g107,g108)
    c: Horizontal(g108)
    c: Coincident(g108,g109)
    c: Vertical(g109)
    c: Coincident(g109,g110)
    c: Horizontal(g110)
    c: Coincident(g110,g111)
    c: Vertical(g111)
    c: Coincident(g111,g112)
    c: Horizontal(g112)
    c: Coincident(g112,g113)
    c: Vertical(g113)
    c: Coincident(g102,g113)
    c: Horizontal(g114)
    c: Coincident(g114,g115)
    c: Vertical(g115)
    c: Coincident(g115,g116)
    c: Horizontal(g116)
    c: Coincident(g116,g117)
    c: Vertical(g117)
    c: Coincident(g117,g118)
    c: Horizontal(g118)
    c: Coincident(g118,g119)
    c: Vertical(g119)
    c: Coincident(g119,g120)
    c: Horizontal(g120)
    c: Coincident(g120,g121)
    c: Vertical(g121)
    c: Coincident(g121,g122)
    c: Horizontal(g122)
    c: Coincident(g122,g123)
    c: Vertical(g123)
    c: Coincident(g123,g124)
    c: Horizontal(g124)
    c: Coincident(g124,g125)
    c: Vertical(g125)
    c: Coincident(g114,g125)
    c: Coincident(g126,g112)
    c: Coincident(g126,g102)
    c: Coincident(g126,g111)
    c: Coincident(g127,g109)
    c: Coincident(g127,g111)
    c: Coincident(g127,g108)
    c: Coincident(g128,g106)
    c: Coincident(g128,g105)
    c: Coincident(g128,g108)
    c: Coincident(g129,g103)
    c: Coincident(g129,g102)
    c: Coincident(g129,g105)
    c: Equal(g126,g129)
    c: Equal(g129,g128)
    c: Equal(g128,g127)
    c: PointOnObject(g102,g12)
    c: PointOnObject(g108,g14)
    c: PointOnObject(g105,g13)
    c: PointOnObject(g111,g15)
    c: Coincident(g130,g124)
    c: Coincident(g130,g114)
    c: Coincident(g130,g123)
    c: Coincident(g131,g115)
    c: Coincident(g131,g114)
    c: Coincident(g131,g117)
    c: Coincident(g132,g118)
    c: Coincident(g132,g117)
    c: Coincident(g132,g120)
    c: Coincident(g133,g121)
    c: Coincident(g133,g123)
    c: Coincident(g133,g120)
    c: Equal(g130,g131)
    c: Equal(g131,g132)
    c: Equal(g132,g133)
    c: PointOnObject(g114,g16)
    c: PointOnObject(g120,g18)
    c: PointOnObject(g117,g17)
    c: PointOnObject(g123,g19)
    c: Coincident(g134,g88)
    c: Coincident(g134,g78)
    c: Coincident(g134,g87)
    c: Coincident(g135,g79)
    c: Coincident(g135,g78)
    c: Coincident(g135,g81)
    c: Coincident(g136,g82)
    c: Coincident(g136,g81)
    c: Coincident(g136,g84)
    c: Coincident(g137,g85)
    c: Coincident(g137,g87)
    c: Coincident(g137,g84)
    c: Equal(g134,g135)
    c: Equal(g135,g136)
    c: Equal(g136,g137)
    c: PointOnObject(g78,g4)
    c: PointOnObject(g84,g6)
    c: PointOnObject(g81,g5)
    c: PointOnObject(g87,g7)
    c: Coincident(g138,g100)
    c: Coincident(g138,g90)
    c: Coincident(g138,g99)
    c: Coincident(g139,g91)
    c: Coincident(g139,g90)
    c: Coincident(g139,g93)
    c: Coincident(g140,g94)
    c: Coincident(g140,g93)
    c: Coincident(g140,g96)
    c: Coincident(g141,g97)
    c: Coincident(g141,g99)
    c: Coincident(g141,g96)
    c: Equal(g138,g139)
    c: Equal(g139,g140)
    c: Equal(g140,g141)
    c: PointOnObject(g90,g8)
    c: PointOnObject(g96,g10)
    c: PointOnObject(g93,g9)
    c: PointOnObject(g99,g11)
    c: Equal(g134,g126)
    c: Equal(g126,g130)
    c: Equal(g130,g138)
    c: Radius(g134) = 1
    c: Symmetric(g63,g63,g66)
    c: Symmetric(g65,g65,g67)
    c: Coincident(g53,g54)
    c: Symmetric(g54,g53,g65)
    c: Coincident(g56,g57)
    c: Symmetric(g56,g56,g65)
    c: Coincident(g38,g39)
    c: Symmetric(g38,g37,g63)
    c: Coincident(g40,g43)
    c: Symmetric(g40,g40,g63)
    c: Coincident(g61,g66)
    c: DistanceX(g5,g61) = 15.5
    c: DistanceX(g66,g66) = 15.5
    c: Coincident(g60,g67)
FEATURE [PartDesign::Pad] Pad026
  Length = 3
  Length2 = 100
  Placement = pos=(0,0,0) rot=(1,0,0;1.5708rad)
  Profile = -> Sketch001002032
  Type = 0
FEATURE [Sketcher::SketchObject] Sketch001002033  label="Sketch Front TF001"
  Placement = pos=(0,-3,0) rot=(1,0,0;1.5708rad)
  sketch-geometry (68):
    g0: LineSegment [constr] StartX=-241 StartY=22 StartZ=0 EndX=241 EndY=22 EndZ=0
    g1: LineSegment [constr] StartX=241 StartY=22 StartZ=0 EndX=241 EndY=-22 EndZ=0
    g2: LineSegment [constr] StartX=241 StartY=-22 StartZ=0 EndX=-241 EndY=-22 EndZ=0
    g3: LineSegment [constr] StartX=-241 StartY=-22 StartZ=0 EndX=-241 EndY=22 EndZ=0
    g4: LineSegment [constr] StartX=-237 StartY=19 StartZ=0 EndX=-225 EndY=19 EndZ=0
    g5: LineSegment [constr] StartX=-225 StartY=19 StartZ=0 EndX=-225 EndY=13 EndZ=0
    g6: LineSegment [constr] StartX=-225 StartY=13 StartZ=0 EndX=-237 EndY=13 EndZ=0
    g7: LineSegment [constr] StartX=-237 StartY=13 StartZ=0 EndX=-237 EndY=19 EndZ=0
    g8: LineSegment [constr] StartX=-237 StartY=-13 StartZ=0 EndX=-225 EndY=-13 EndZ=0
    g9: LineSegment [constr] StartX=-225 StartY=-13 StartZ=0 EndX=-225 EndY=-19 EndZ=0
    g10: LineSegment [constr] StartX=-225 StartY=-19 StartZ=0 EndX=-237 EndY=-19 EndZ=0
    g11: LineSegment [constr] StartX=-237 StartY=-19 StartZ=0 EndX=-237 EndY=-13 EndZ=0
    g12: LineSegment [constr] StartX=225 StartY=19 StartZ=0 EndX=237 EndY=19 EndZ=0
    g13: LineSegment [constr] StartX=237 StartY=19 StartZ=0 EndX=237 EndY=13 EndZ=0
    g14: LineSegment [constr] StartX=237 StartY=13 StartZ=0 EndX=225 EndY=13 EndZ=0
    g15: LineSegment [constr] StartX=225 StartY=13 StartZ=0 EndX=225 EndY=19 EndZ=0
    g16: LineSegment [constr] StartX=225 StartY=-13 StartZ=0 EndX=237 EndY=-13 EndZ=0
    g17: LineSegment [constr] StartX=237 StartY=-13 StartZ=0 EndX=237 EndY=-19 EndZ=0
    g18: LineSegment [constr] StartX=237 StartY=-19 StartZ=0 EndX=225 EndY=-19 EndZ=0
    g19: LineSegment [constr] StartX=225 StartY=-19 StartZ=0 EndX=225 EndY=-13 EndZ=0
    g20: LineSegment [constr] StartX=-237 StartY=19 StartZ=0 EndX=-237 EndY=22 EndZ=0
    g21: LineSegment [constr] StartX=-237 StartY=19 StartZ=0 EndX=-241 EndY=19 EndZ=0
    g22: LineSegment [constr] StartX=-237 StartY=-19 StartZ=0 EndX=-237 EndY=-22 EndZ=0
    g23: LineSegment [constr] StartX=-237 StartY=-19 StartZ=0 EndX=-241 EndY=-19 EndZ=0
    g24: LineSegment [constr] StartX=237 StartY=-19 StartZ=0 EndX=241 EndY=-19 EndZ=0
    g25: LineSegment [constr] StartX=237 StartY=-19 StartZ=0 EndX=237 EndY=-22 EndZ=0
    g26: LineSegment [constr] StartX=237 StartY=19 StartZ=0 EndX=241 EndY=19 EndZ=0
    g27: LineSegment [constr] StartX=237 StartY=19 StartZ=0 EndX=237 EndY=22 EndZ=0
    g28: LineSegment StartX=-153 StartY=15 StartZ=0 EndX=-123 EndY=15 EndZ=0
    g29: LineSegment StartX=-123 StartY=15 StartZ=0 EndX=-123 EndY=-11 EndZ=0
    g30: LineSegment StartX=-123 StartY=-11 StartZ=0 EndX=-125 EndY=-11 EndZ=0
    g31: LineSegment StartX=-125 StartY=-11 StartZ=0 EndX=-125 EndY=13 EndZ=0
    g32: LineSegment StartX=-125 StartY=13 StartZ=0 EndX=-153 EndY=13 EndZ=0
    g33: LineSegment StartX=-153 StartY=13 StartZ=0 EndX=-153 EndY=15 EndZ=0
    g34: LineSegment [constr] StartX=-153 StartY=15 StartZ=0 EndX=-153 EndY=-15 EndZ=0
    g35: LineSegment StartX=-153 StartY=-15 StartZ=0 EndX=-123 EndY=-15 EndZ=0
    g36: LineSegment StartX=-123 StartY=-15 StartZ=0 EndX=-123 EndY=-13 EndZ=0
    g37: LineSegment StartX=-123 StartY=-13 StartZ=0 EndX=-151 EndY=-13 EndZ=0
    g38: LineSegment StartX=-151 StartY=-13 StartZ=0 EndX=-151 EndY=11 EndZ=0
    g39: LineSegment StartX=-151 StartY=11 StartZ=0 EndX=-153 EndY=11 EndZ=0
    g40: LineSegment [constr] StartX=-153 StartY=13 StartZ=0 EndX=-153 EndY=11 EndZ=0
    g41: LineSegment [constr] StartX=-123 StartY=-11 StartZ=0 EndX=-123 EndY=-13 EndZ=0
    g42: LineSegment StartX=-147.5 StartY=9.5 StartZ=0 EndX=-147.5 EndY=6.5 EndZ=0
    g43: LineSegment StartX=-147.5 StartY=6.5 StartZ=0 EndX=-142.5 EndY=6.5 EndZ=0
    g44: LineSegment StartX=-142.5 StartY=6.5 StartZ=0 EndX=-142.5 EndY=-9.5 EndZ=0
    g45: LineSegment StartX=-142.5 StartY=-9.5 StartZ=0 EndX=-139.5 EndY=-9.5 EndZ=0
    g46: LineSegment StartX=-139.5 StartY=-9.5 StartZ=0 EndX=-139.5 EndY=6.5 EndZ=0
    g47: LineSegment StartX=-139.5 StartY=6.5 StartZ=0 EndX=-128.5 EndY=6.5 EndZ=0
    g48: LineSegment StartX=-128.5 StartY=6.5 StartZ=0 EndX=-128.5 EndY=9.5 EndZ=0
    g49: LineSegment StartX=-128.5 StartY=9.5 StartZ=0 EndX=-147.5 EndY=9.5 EndZ=0
    g50: LineSegment StartX=-136.5 StartY=3.5 StartZ=0 EndX=-136.5 EndY=-9.5 EndZ=0
    g51: LineSegment StartX=-136.5 StartY=-9.5 StartZ=0 EndX=-133.5 EndY=-9.5 EndZ=0
    g52: LineSegment StartX=-133.5 StartY=-9.5 StartZ=0 EndX=-133.5 EndY=-2.5 EndZ=0
    g53: LineSegment StartX=-133.5 StartY=-2.5 StartZ=0 EndX=-128.5 EndY=-2.5 EndZ=0
    g54: LineSegment StartX=-128.5 StartY=-2.5 StartZ=0 EndX=-128.5 EndY=0.5 EndZ=0
    g55: LineSegment StartX=-128.5 StartY=0.5 StartZ=0 EndX=-133.5 EndY=0.5 EndZ=0
    g56: LineSegment StartX=-133.5 StartY=0.5 StartZ=0 EndX=-133.5 EndY=3.5 EndZ=0
    g57: LineSegment StartX=-133.5 StartY=3.5 StartZ=0 EndX=-136.5 EndY=3.5 EndZ=0
    g58: LineSegment [constr] StartX=-147.5 StartY=9.5 StartZ=0 EndX=-151 EndY=9.5 EndZ=0
    g59: LineSegment [constr] StartX=-128.5 StartY=9.5 StartZ=0 EndX=-125 EndY=9.5 EndZ=0
    g60: LineSegment [constr] StartX=-139.5 StartY=-9.5 StartZ=0 EndX=-136.5 EndY=-9.5 EndZ=0
    g61: LineSegment [constr] StartX=-128.5 StartY=0.5 StartZ=0 EndX=-128.5 EndY=6.5 EndZ=0
    g62: LineSegment [constr] StartX=-136.5 StartY=3.5 StartZ=0 EndX=-136.5 EndY=6.5 EndZ=0
    g63: LineSegment [constr] StartX=-142.5 StartY=-9.5 StartZ=0 EndX=-142.5 EndY=-13 EndZ=0
    g64: LineSegment [constr] StartX=-147.5 StartY=9.5 StartZ=0 EndX=-147.5 EndY=13 EndZ=0
    g65: LineSegment StartX=-153 StartY=11 StartZ=0 EndX=-153 EndY=-15 EndZ=0
    g66: LineSegment [constr] StartX=-138 StartY=22 StartZ=0 EndX=-138 EndY=15 EndZ=0
    g67: LineSegment [constr] StartX=-138 StartY=-22 StartZ=0 EndX=-138 EndY=-15 EndZ=0
  constraints (198):
    c: Coincident(g0,g1)
    c: Coincident(g1,g2)
    c: Coincident(g2,g3)
    c: Coincident(g3,g0)
    c: Horizontal(g0)
    c: Horizontal(g2)
    c: Vertical(g1)
    c: Vertical(g3)
    c: DistanceX(g0,g0) = 482
    c: DistanceY(g3,g3) = 44
    c: Coincident(g4,g5)
    c: Coincident(g5,g6)
    c: Coincident(g6,g7)
    c: Coincident(g7,g4)
    c: Horizontal(g4)
    c: Horizontal(g6)
    c: Vertical(g5)
    c: Vertical(g7)
    c: Coincident(g8,g9)
    c: Coincident(g9,g10)
    c: Coincident(g10,g11)
    c: Coincident(g11,g8)
    c: Horizontal(g8)
    c: Horizontal(g10)
    c: Vertical(g9)
    c: Vertical(g11)
    c: Coincident(g12,g13)
    c: Coincident(g13,g14)
    c: Coincident(g14,g15)
    c: Coincident(g15,g12)
    c: Horizontal(g12)
    c: Horizontal(g14)
    c: Vertical(g13)
    c: Vertical(g15)
    c: Coincident(g16,g17)
    c: Coincident(g17,g18)
    c: Coincident(g18,g19)
    c: Coincident(g19,g16)
    c: Horizontal(g16)
    c: Horizontal(g18)
    c: Vertical(g17)
    c: Vertical(g19)
    c: Equal(g5,g15)
    c: Equal(g15,g19)
    c: Equal(g19,g9)
    c: Equal(g6,g14)
    c: Equal(g14,g16)
    c: Equal(g16,g8)
    c: DistanceX(g4,g4) = 12
    c: DistanceY(g7,g7) = 6
    c: Coincident(g20,g4)
    c: PointOnObject(g20,g0)
    c: Vertical(g20)
    c: Coincident(g21,g4)
    c: PointOnObject(g21,g3)
    c: Horizontal(g21)
    c: Coincident(g22,g10)
    c: PointOnObject(g22,g2)
    c: Vertical(g22)
    c: Coincident(g23,g10)
    c: PointOnObject(g23,g3)
    c: Horizontal(g23)
    c: Coincident(g24,g17)
    c: PointOnObject(g24,g1)
    c: Horizontal(g24)
    c: Coincident(g25,g17)
    c: PointOnObject(g25,g2)
    c: Vertical(g25)
    c: Coincident(g26,g12)
    c: PointOnObject(g26,g1)
    c: Horizontal(g26)
    c: Coincident(g27,g12)
    c: PointOnObject(g27,g0)
    c: Vertical(g27)
    c: Equal(g21,g26)
    c: Equal(g26,g24)
    c: Equal(g24,g23)
    c: Equal(g20,g27)
    c: Equal(g27,g25)
    c: Equal(g25,g22)
    c: DistanceX(g21,g21) = 4
    c: DistanceY(g20,g20) = 3
    c: Horizontal(g28)
    c: Coincident(g28,g29)
    c: Vertical(g29)
    c: Coincident(g29,g30)
    c: Horizontal(g30)
    c: Vertical(g31)
    c: Coincident(g31,g32)
    c: Horizontal(g32)
    c: Coincident(g32,g33)
    c: Coincident(g33,g28)
    c: Vertical(g33)
    c: Coincident(g34,g35)
    c: Horizontal(g35)
    c: Vertical(g36)
    c: Coincident(g36,g37)
    c: Horizontal(g37)
    c: Coincident(g37,g38)
    c: Vertical(g38)
    c: Coincident(g38,g39)
    c: Horizontal(g39)
    c: Coincident(g40,g32)
    c: Equal(g41,g40)
    c: Equal(g33,g39)
    c: Equal(g39,g36)
    c: Equal(g36,g30)
    c: DistanceY(g33,g33) = 2
    c: DistanceY(g40,g40) = 2
    c: DistanceX(g28,g28) = 30
    c: Equal(g34,g28)
    c: Vertical(g42)
    c: Coincident(g42,g43)
    c: Horizontal(g43)
    c: Coincident(g43,g44)
    c: Vertical(g44)
    c: Coincident(g44,g45)
    c: Horizontal(g45)
    c: Coincident(g45,g46)
    c: Vertical(g46)
    c: Coincident(g46,g47)
    c: Horizontal(g47)
    c: Coincident(g47,g48)
    c: Vertical(g48)
    c: Coincident(g48,g49)
    c: Coincident(g49,g42)
    c: Horizontal(g49)
    c: Vertical(g50)
    c: Coincident(g50,g51)
    c: Horizontal(g51)
    c: Coincident(g51,g52)
    c: Vertical(g52)
    c: Coincident(g52,g53)
    c: Horizontal(g53)
    c: Coincident(g53,g54)
    c: Vertical(g54)
    c: Coincident(g54,g55)
    c: Horizontal(g55)
    c: Coincident(g55,g56)
    c: Coincident(g56,g57)
    c: Coincident(g57,g50)
    c: Horizontal(g57)
    c: Equal(g55,g53)
    c: DistanceY(g42,g42) = 3
    c: Equal(g42,g48)
    c: Equal(g48,g57)
    c: Equal(g57,g54)
    c: Equal(g54,g51)
    c: Equal(g51,g45)
    c: Coincident(g58,g42)
    c: PointOnObject(g58,g38)
    c: Horizontal(g58)
    c: Coincident(g59,g48)
    c: PointOnObject(g59,g31)
    c: Horizontal(g59)
    c: Coincident(g60,g45)
    c: Coincident(g60,g50)
    c: Horizontal(g60)
    c: Coincident(g61,g54)
    c: Coincident(g61,g47)
    c: Vertical(g61)
    c: Coincident(g62,g50)
    c: PointOnObject(g62,g47)
    c: Vertical(g62)
    c: Coincident(g63,g44)
    c: PointOnObject(g63,g37)
    c: Vertical(g63)
    c: Coincident(g64,g42)
    c: PointOnObject(g64,g32)
    c: Vertical(g64)
    c: Equal(g58,g64)
    c: Equal(g64,g59)
    c: Equal(g59,g63)
    c: Equal(g60,g62)
    c: DistanceX(g58,g58) = 3.5
    c: DistanceY(g62,g62) = 3
    c: Equal(g56,g45)
    c: Equal(g43,g55)
    c: Coincident(g30,g31)
    c: Coincident(g35,g36)
    c: Coincident(g29,g41)
    c: Coincident(g41,g36)
    c: Vertical(g41)
    c: Symmetric(g0,g1,g-1)
    c: Coincident(g39,g40)
    c: Coincident(g65,g39)
    c: Coincident(g65,g34)
    c: Vertical(g65)
    c: Coincident(g34,g28)
    c: PointOnObject(g66,g0)
    c: Vertical(g66)
    c: PointOnObject(g67,g2)
    c: Vertical(g67)
    c: Vertical(g34)
    c: Symmetric(g28,g28,g66)
    c: Symmetric(g35,g35,g67)
    c: Equal(g67,g66)
    c: DistanceX(g67,g-1) = 138
FEATURE [Sketcher::SketchObject] Sketch001002034  label="Sketch Front Stack001"
  Placement = pos=(0,-3,0) rot=(1,0,0;1.5708rad)
  sketch-geometry (83):
    g0: LineSegment [constr] StartX=-241 StartY=22 StartZ=0 EndX=241 EndY=22 EndZ=0
    g1: LineSegment [constr] StartX=241 StartY=22 StartZ=0 EndX=241 EndY=-22 EndZ=0
    g2: LineSegment [constr] StartX=241 StartY=-22 StartZ=0 EndX=-241 EndY=-22 EndZ=0
    g3: LineSegment [constr] StartX=-241 StartY=-22 StartZ=0 EndX=-241 EndY=22 EndZ=0
    g4: LineSegment [constr] StartX=-237 StartY=19 StartZ=0 EndX=-225 EndY=19 EndZ=0
    g5: LineSegment [constr] StartX=-225 StartY=19 StartZ=0 EndX=-225 EndY=13 EndZ=0
    g6: LineSegment [constr] StartX=-225 StartY=13 StartZ=0 EndX=-237 EndY=13 EndZ=0
    g7: LineSegment [constr] StartX=-237 StartY=13 StartZ=0 EndX=-237 EndY=19 EndZ=0
    g8: LineSegment [constr] StartX=-237 StartY=-13 StartZ=0 EndX=-225 EndY=-13 EndZ=0
    g9: LineSegment [constr] StartX=-225 StartY=-13 StartZ=0 EndX=-225 EndY=-19 EndZ=0
    g10: LineSegment [constr] StartX=-225 StartY=-19 StartZ=0 EndX=-237 EndY=-19 EndZ=0
    g11: LineSegment [constr] StartX=-237 StartY=-19 StartZ=0 EndX=-237 EndY=-13 EndZ=0
    g12: LineSegment [constr] StartX=225 StartY=19 StartZ=0 EndX=237 EndY=19 EndZ=0
    g13: LineSegment [constr] StartX=237 StartY=19 StartZ=0 EndX=237 EndY=13 EndZ=0
    g14: LineSegment [constr] StartX=237 StartY=13 StartZ=0 EndX=225 EndY=13 EndZ=0
    g15: LineSegment [constr] StartX=225 StartY=13 StartZ=0 EndX=225 EndY=19 EndZ=0
    g16: LineSegment [constr] StartX=225 StartY=-13 StartZ=0 EndX=237 EndY=-13 EndZ=0
    g17: LineSegment [constr] StartX=237 StartY=-13 StartZ=0 EndX=237 EndY=-19 EndZ=0
    g18: LineSegment [constr] StartX=237 StartY=-19 StartZ=0 EndX=225 EndY=-19 EndZ=0
    g19: LineSegment [constr] StartX=225 StartY=-19 StartZ=0 EndX=225 EndY=-13 EndZ=0
    g20: LineSegment [constr] StartX=-237 StartY=19 StartZ=0 EndX=-237 EndY=22 EndZ=0
    g21: LineSegment [constr] StartX=-237 StartY=19 StartZ=0 EndX=-241 EndY=19 EndZ=0
    g22: LineSegment [constr] StartX=-237 StartY=-19 StartZ=0 EndX=-237 EndY=-22 EndZ=0
    g23: LineSegment [constr] StartX=-237 StartY=-19 StartZ=0 EndX=-241 EndY=-19 EndZ=0
    g24: LineSegment [constr] StartX=237 StartY=-19 StartZ=0 EndX=241 EndY=-19 EndZ=0
    g25: LineSegment [constr] StartX=237 StartY=-19 StartZ=0 EndX=237 EndY=-22 EndZ=0
    g26: LineSegment [constr] StartX=237 StartY=19 StartZ=0 EndX=241 EndY=19 EndZ=0
    g27: LineSegment [constr] StartX=237 StartY=19 StartZ=0 EndX=237 EndY=22 EndZ=0
    g28: LineSegment [constr] StartX=-195.5 StartY=14.1 StartZ=0 EndX=-192.5 EndY=14.1 EndZ=0
    g29: LineSegment [constr] StartX=-192.5 StartY=14.1 StartZ=0 EndX=-192.5 EndY=3.9 EndZ=0
    g30: LineSegment [constr] StartX=-192.5 StartY=3.9 StartZ=0 EndX=-195.5 EndY=3.9 EndZ=0
    g31: LineSegment [constr] StartX=-195.5 StartY=3.9 StartZ=0 EndX=-195.5 EndY=14.1 EndZ=0
    g32: LineSegment [constr] StartX=-195.5 StartY=-3.9 StartZ=0 EndX=-192.5 EndY=-3.9 EndZ=0
    g33: LineSegment [constr] StartX=-192.5 StartY=-3.9 StartZ=0 EndX=-192.5 EndY=-14.1 EndZ=0
    g34: LineSegment [constr] StartX=-192.5 StartY=-14.1 StartZ=0 EndX=-195.5 EndY=-14.1 EndZ=0
    g35: LineSegment [constr] StartX=-195.5 StartY=-14.1 StartZ=0 EndX=-195.5 EndY=-3.9 EndZ=0
    g36: LineSegment [constr] StartX=-195.5 StartY=3.9 StartZ=0 EndX=-195.5 EndY=-3.9 EndZ=0
    g37: LineSegment StartX=-185.4 StartY=7.05 StartZ=0 EndX=-185.4 EndY=-4.55 EndZ=0
    g38: LineSegment [constr] StartX=-185.4 StartY=-4.55 StartZ=0 EndX=-184.4 EndY=-4.55 EndZ=0
    g39: LineSegment [constr] StartX=-184.4 StartY=-4.55 StartZ=0 EndX=-184.4 EndY=-5.55 EndZ=0
    g40: LineSegment StartX=-184.4 StartY=-5.55 StartZ=0 EndX=-175.3 EndY=-5.55 EndZ=0
    g41: LineSegment [constr] StartX=-175.3 StartY=-5.55 StartZ=0 EndX=-175.3 EndY=-4.55 EndZ=0
    g42: LineSegment [constr] StartX=-175.3 StartY=-4.55 StartZ=0 EndX=-174.3 EndY=-4.55 EndZ=0
    g43: LineSegment StartX=-174.3 StartY=-4.55 StartZ=0 EndX=-174.3 EndY=4.55 EndZ=0
    g44: LineSegment [constr] StartX=-174.3 StartY=4.55 StartZ=0 EndX=-175.3 EndY=4.55 EndZ=0
    g45: LineSegment [constr] StartX=-175.3 StartY=4.55 StartZ=0 EndX=-175.3 EndY=5.55 EndZ=0
    g46: LineSegment StartX=-175.3 StartY=5.55 StartZ=0 EndX=-181.4 EndY=5.55 EndZ=0
    g47: LineSegment [constr] StartX=-181.4 StartY=5.55 StartZ=0 EndX=-181.4 EndY=7.05 EndZ=0
    g48: LineSegment [constr] StartX=-181.4 StartY=7.05 StartZ=0 EndX=-182.9 EndY=7.05 EndZ=0
    g49: LineSegment [constr] StartX=-182.9 StartY=7.05 StartZ=0 EndX=-185.4 EndY=7.05 EndZ=0
    g50: ArcOfCircle CenterX=-181.4 CenterY=7.05 CenterZ=0 NormalX=0 NormalY=0 NormalZ=1 AngleXU=0 Radius=1.5 StartAngle=3.14159 EndAngle=4.71239
    g51: ArcOfCircle CenterX=-175.3 CenterY=4.55 CenterZ=0 NormalX=0 NormalY=0 NormalZ=1 AngleXU=0 Radius=1 StartAngle=0 EndAngle=1.5708
    g52: ArcOfCircle CenterX=-175.3 CenterY=-4.55 CenterZ=0 NormalX=0 NormalY=0 NormalZ=1 AngleXU=0 Radius=1 StartAngle=4.71239 EndAngle=6.28319
    g53: ArcOfCircle CenterX=-184.4 CenterY=-4.55 CenterZ=0 NormalX=0 NormalY=0 NormalZ=1 AngleXU=0 Radius=1 StartAngle=3.14159 EndAngle=4.71239
    g54: ArcOfCircle CenterX=-184.15 CenterY=7.05 CenterZ=0 NormalX=0 NormalY=0 NormalZ=1 AngleXU=0 Radius=1.25 StartAngle=2.14e-14 EndAngle=3.14159
    g55: Circle CenterX=-179.85 CenterY=11.5 CenterZ=0 NormalX=0 NormalY=0 NormalZ=1 AngleXU=0 Radius=2.5
    g56: Circle CenterX=-179.85 CenterY=-11.5 CenterZ=0 NormalX=0 NormalY=0 NormalZ=1 AngleXU=0 Radius=2.5
    g57: LineSegment [constr] StartX=-179.85 StartY=11.5 StartZ=0 EndX=-179.85 EndY=-11.5 EndZ=0
    g58: LineSegment [constr] StartX=-192.5 StartY=14.1 StartZ=0 EndX=-175.3 EndY=4.55 EndZ=0
    g59: LineSegment [constr] StartX=-175.3 StartY=-4.55 StartZ=0 EndX=-192.5 EndY=-14.1 EndZ=0
    g60: LineSegment StartX=-170.15 StartY=3.05 StartZ=0 EndX=-170.15 EndY=-11.05 EndZ=0
    g61: LineSegment [constr] StartX=-170.15 StartY=-11.05 StartZ=0 EndX=-169.15 EndY=-11.05 EndZ=0
    g62: LineSegment [constr] StartX=-169.15 StartY=-11.05 StartZ=0 EndX=-169.15 EndY=-12.05 EndZ=0
    g63: LineSegment StartX=-169.15 StartY=-12.05 StartZ=0 EndX=-158.55 EndY=-12.05 EndZ=0
    g64: LineSegment [constr] StartX=-158.55 StartY=-12.05 StartZ=0 EndX=-158.55 EndY=-11.05 EndZ=0
    g65: LineSegment [constr] StartX=-158.55 StartY=-11.05 StartZ=0 EndX=-157.55 EndY=-11.05 EndZ=0
    g66: LineSegment StartX=-157.55 StartY=-11.05 StartZ=0 EndX=-157.55 EndY=3.05 EndZ=0
    g67: LineSegment [constr] StartX=-157.55 StartY=3.05 StartZ=0 EndX=-158.55 EndY=3.05 EndZ=0
    g68: LineSegment [constr] StartX=-158.55 StartY=3.05 StartZ=0 EndX=-158.55 EndY=4.05 EndZ=0
    g69: LineSegment StartX=-158.55 StartY=4.05 StartZ=0 EndX=-169.15 EndY=4.05 EndZ=0
    g70: LineSegment [constr] StartX=-169.15 StartY=4.05 StartZ=0 EndX=-169.15 EndY=3.05 EndZ=0
    g71: LineSegment [constr] StartX=-169.15 StartY=3.05 StartZ=0 EndX=-170.15 EndY=3.05 EndZ=0
    g72: ArcOfCircle CenterX=-169.15 CenterY=3.05 CenterZ=0 NormalX=0 NormalY=0 NormalZ=1 AngleXU=0 Radius=1 StartAngle=1.5708 EndAngle=3.14159
    g73: ArcOfCircle CenterX=-158.55 CenterY=3.05 CenterZ=0 NormalX=0 NormalY=0 NormalZ=1 AngleXU=0 Radius=1 StartAngle=0 EndAngle=1.5708
    g74: ArcOfCircle CenterX=-158.55 CenterY=-11.05 CenterZ=0 NormalX=0 NormalY=0 NormalZ=1 AngleXU=0 Radius=1 StartAngle=4.71239 EndAngle=6.28319
    g75: ArcOfCircle CenterX=-169.15 CenterY=-11.05 CenterZ=0 NormalX=0 NormalY=0 NormalZ=1 AngleXU=0 Radius=1 StartAngle=3.14159 EndAngle=4.71239
    g76: LineSegment [constr] StartX=-175.3 StartY=4.55 StartZ=0 EndX=-179.85 EndY=-9e-16 EndZ=0
    g77: LineSegment [constr] StartX=-175.3 StartY=-4.55 StartZ=0 EndX=-179.85 EndY=-9e-16 EndZ=0
    g78: LineSegment [constr] StartX=-184.4 StartY=-4.55 StartZ=0 EndX=-179.85 EndY=-9e-16 EndZ=0
    g79: LineSegment [constr] StartX=-169.15 StartY=3.05 StartZ=0 EndX=-163.85 EndY=-4 EndZ=0
    g80: LineSegment [constr] StartX=-163.85 StartY=-4 StartZ=0 EndX=-158.55 EndY=3.05 EndZ=0
    g81: LineSegment [constr] StartX=-163.85 StartY=-4 StartZ=0 EndX=-158.55 EndY=-11.05 EndZ=0
    g82: LineSegment [constr] StartX=-163.85 StartY=-4 StartZ=0 EndX=-169.15 EndY=-11.05 EndZ=0
  constraints (229):
    c: Coincident(g0,g1)
    c: Coincident(g1,g2)
    c: Coincident(g2,g3)
    c: Coincident(g3,g0)
    c: Horizontal(g0)
    c: Horizontal(g2)
    c: Vertical(g1)
    c: Vertical(g3)
    c: DistanceX(g0,g0) = 482
    c: DistanceY(g3,g3) = 44
    c: Coincident(g4,g5)
    c: Coincident(g5,g6)
    c: Coincident(g6,g7)
    c: Coincident(g7,g4)
    c: Horizontal(g4)
    c: Horizontal(g6)
    c: Vertical(g5)
    c: Vertical(g7)
    c: Coincident(g8,g9)
    c: Coincident(g9,g10)
    c: Coincident(g10,g11)
    c: Coincident(g11,g8)
    c: Horizontal(g8)
    c: Horizontal(g10)
    c: Vertical(g9)
    c: Vertical(g11)
    c: Coincident(g12,g13)
    c: Coincident(g13,g14)
    c: Coincident(g14,g15)
    c: Coincident(g15,g12)
    c: Horizontal(g12)
    c: Horizontal(g14)
    c: Vertical(g13)
    c: Vertical(g15)
    c: Coincident(g16,g17)
    c: Coincident(g17,g18)
    c: Coincident(g18,g19)
    c: Coincident(g19,g16)
    c: Horizontal(g16)
    c: Horizontal(g18)
    c: Vertical(g17)
    c: Vertical(g19)
    c: Equal(g5,g15)
    c: Equal(g15,g19)
    c: Equal(g19,g9)
    c: Equal(g6,g14)
    c: Equal(g14,g16)
    c: Equal(g16,g8)
    c: DistanceX(g4,g4) = 12
    c: DistanceY(g7,g7) = 6
    c: Coincident(g20,g4)
    c: PointOnObject(g20,g0)
    c: Vertical(g20)
    c: Coincident(g21,g4)
    c: PointOnObject(g21,g3)
    c: Horizontal(g21)
    c: Coincident(g22,g10)
    c: PointOnObject(g22,g2)
    c: Vertical(g22)
    c: Coincident(g23,g10)
    c: PointOnObject(g23,g3)
    c: Horizontal(g23)
    c: Coincident(g24,g17)
    c: PointOnObject(g24,g1)
    c: Horizontal(g24)
    c: Coincident(g25,g17)
    c: PointOnObject(g25,g2)
    c: Vertical(g25)
    c: Coincident(g26,g12)
    c: PointOnObject(g26,g1)
    c: Horizontal(g26)
    c: Coincident(g27,g12)
    c: PointOnObject(g27,g0)
    c: Vertical(g27)
    c: Equal(g21,g26)
    c: Equal(g26,g24)
    c: Equal(g24,g23)
    c: Equal(g20,g27)
    c: Equal(g27,g25)
    c: Equal(g25,g22)
    c: DistanceX(g21,g21) = 4
    c: DistanceY(g20,g20) = 3
    c: Coincident(g28,g29)
    c: Coincident(g29,g30)
    c: Coincident(g30,g31)
    c: Coincident(g31,g28)
    c: Horizontal(g28)
    c: Horizontal(g30)
    c: Vertical(g29)
    c: Vertical(g31)
    c: Coincident(g32,g33)
    c: Coincident(g33,g34)
    c: Coincident(g34,g35)
    c: Coincident(g35,g32)
    c: Horizontal(g32)
    c: Horizontal(g34)
    c: Vertical(g33)
    c: Vertical(g35)
    c: Equal(g31,g35)
    c: Equal(g30,g32)
    c: Coincident(g36,g30)
    c: Coincident(g36,g32)
    c: DistanceY(g36,g36) = 7.8
    c: Vertical(g37)
    c: Coincident(g37,g38)
    c: Horizontal(g38)
    c: Coincident(g38,g39)
    c: Vertical(g39)
    c: Coincident(g39,g40)
    c: Horizontal(g40)
    c: Coincident(g40,g41)
    c: Vertical(g41)
    c: Coincident(g41,g42)
    c: Horizontal(g42)
    c: Coincident(g42,g43)
    c: Vertical(g43)
    c: Coincident(g43,g44)
    c: Horizontal(g44)
    c: Coincident(g44,g45)
    c: Vertical(g45)
    c: Coincident(g45,g46)
    c: Horizontal(g46)
    c: Coincident(g46,g47)
    c: Vertical(g47)
    c: Coincident(g47,g48)
    c: Horizontal(g48)
    c: Coincident(g49,g37)
    c: Horizontal(g49)
    c: Coincident(g50,g47)
    c: Coincident(g50,g46)
    c: Coincident(g51,g44)
    c: Coincident(g51,g46)
    c: Coincident(g51,g43)
    c: Coincident(g52,g41)
    c: Coincident(g52,g43)
    c: Coincident(g52,g40)
    c: Coincident(g53,g38)
    c: Coincident(g53,g37)
    c: Coincident(g53,g40)
    c: DistanceY(g40,g46) = 11.1
    c: DistanceX(g49,g49) = 2.5
    c: Equal(g51,g52)
    c: Equal(g52,g53)
    c: PointOnObject(g54,g49)
    c: Coincident(g54,g37)
    c: Radius(g51) = 1
    c: Radius(g50) = 1.5
    c: Coincident(g57,g55)
    c: Coincident(g57,g56)
    c: Vertical(g57)
    c: Coincident(g58,g28)
    c: Coincident(g58,g51)
    c: Coincident(g59,g52)
    c: Coincident(g59,g33)
    c: Equal(g59,g58)
    c: Radius(g55) = 2.5
    c: Equal(g56,g55)
    c: Vertical(g60)
    c: Coincident(g60,g61)
    c: Horizontal(g61)
    c: Coincident(g61,g62)
    c: Vertical(g62)
    c: Coincident(g62,g63)
    c: Horizontal(g63)
    c: Coincident(g63,g64)
    c: Vertical(g64)
    c: Coincident(g64,g65)
    c: Horizontal(g65)
    c: Coincident(g65,g66)
    c: Vertical(g66)
    c: Coincident(g66,g67)
    c: Coincident(g67,g68)
    c: Vertical(g68)
    c: Coincident(g68,g69)
    c: Horizontal(g69)
    c: Coincident(g69,g70)
    c: Vertical(g70)
    c: Coincident(g70,g71)
    c: Coincident(g71,g60)
    c: Horizontal(g71)
    c: Horizontal(g67)
    c: Coincident(g72,g70)
    c: Coincident(g72,g69)
    c: Coincident(g72,g60)
    c: Coincident(g73,g67)
    c: Coincident(g73,g69)
    c: Coincident(g73,g66)
    c: Coincident(g74,g64)
    c: Coincident(g74,g66)
    c: Coincident(g74,g63)
    c: Coincident(g75,g61)
    c: Coincident(g75,g60)
    c: Coincident(g75,g63)
    c: Equal(g72,g73)
    c: Equal(g73,g74)
    c: Equal(g51,g72)
    c: DistanceY(g63,g69) = 16.1
    c: DistanceX(g60,g66) = 12.6
    c: Coincident(g48,g49)
    c: Coincident(g48,g50)
    c: Coincident(g48,g54)
    c: Symmetric(g0,g1,g-1)
    c: DistanceX(g5,g28) = 32.5
    c: DistanceX(g30,g30) = 3
    c: DistanceY(g31,g31) = 10.2
    c: Symmetric(g29,g32,g-1)
    c: Coincident(g76,g51)
    c: Coincident(g77,g52)
    c: Coincident(g77,g76)
    c: Coincident(g78,g53)
    c: Coincident(g78,g76)
    c: Equal(g76,g77)
    c: Equal(g77,g78)
    c: DistanceX(g32,g76) = 12.65
    c: Coincident(g79,g72)
    c: Coincident(g80,g79)
    c: Coincident(g80,g73)
    c: Coincident(g81,g79)
    c: Coincident(g81,g74)
    c: Coincident(g82,g79)
    c: Coincident(g82,g75)
    c: Equal(g79,g80)
    c: Equal(g80,g81)
    c: Equal(g81,g82)
    c: DistanceX(g76,g79) = 16
    c: DistanceY(g79,g76) = 4
    c: Symmetric(g55,g56,g76)
    c: DistanceY(g76,g55) = 11.5
    c: Equal(g40,g43)
FEATURE [PartDesign::Pocket] Pocket011  label="Pocket Stack002"
  BaseFeature = -> Pad026
  Length = 3
  Length2 = 100
  Placement = pos=(0,0,0) rot=(1,0,0;1.5708rad)
  Profile = -> Sketch001002034
  Type = 0
FEATURE [Sketcher::SketchObject] Sketch001002035  label="Sketch Front RP001"
  Placement = pos=(0,-3,0) rot=(1,0,0;1.5708rad)
  sketch-geometry (88):
    g0: LineSegment [constr] StartX=-241 StartY=22 StartZ=0 EndX=241 EndY=22 EndZ=0
    g1: LineSegment [constr] StartX=241 StartY=22 StartZ=0 EndX=241 EndY=-22 EndZ=0
    g2: LineSegment [constr] StartX=241 StartY=-22 StartZ=0 EndX=-241 EndY=-22 EndZ=0
    g3: LineSegment [constr] StartX=-241 StartY=-22 StartZ=0 EndX=-241 EndY=22 EndZ=0
    g4: LineSegment [constr] StartX=-237 StartY=19 StartZ=0 EndX=-225 EndY=19 EndZ=0
    g5: LineSegment [constr] StartX=-225 StartY=19 StartZ=0 EndX=-225 EndY=13 EndZ=0
    g6: LineSegment [constr] StartX=-225 StartY=13 StartZ=0 EndX=-237 EndY=13 EndZ=0
    g7: LineSegment [constr] StartX=-237 StartY=13 StartZ=0 EndX=-237 EndY=19 EndZ=0
    g8: LineSegment [constr] StartX=-237 StartY=-13 StartZ=0 EndX=-225 EndY=-13 EndZ=0
    g9: LineSegment [constr] StartX=-225 StartY=-13 StartZ=0 EndX=-225 EndY=-19 EndZ=0
    g10: LineSegment [constr] StartX=-225 StartY=-19 StartZ=0 EndX=-237 EndY=-19 EndZ=0
    g11: LineSegment [constr] StartX=-237 StartY=-19 StartZ=0 EndX=-237 EndY=-13 EndZ=0
    g12: LineSegment [constr] StartX=225 StartY=19 StartZ=0 EndX=237 EndY=19 EndZ=0
    g13: LineSegment [constr] StartX=237 StartY=19 StartZ=0 EndX=237 EndY=13 EndZ=0
    g14: LineSegment [constr] StartX=237 StartY=13 StartZ=0 EndX=225 EndY=13 EndZ=0
    g15: LineSegment [constr] StartX=225 StartY=13 StartZ=0 EndX=225 EndY=19 EndZ=0
    g16: LineSegment [constr] StartX=225 StartY=-13 StartZ=0 EndX=237 EndY=-13 EndZ=0
    g17: LineSegment [constr] StartX=237 StartY=-13 StartZ=0 EndX=237 EndY=-19 EndZ=0
    g18: LineSegment [constr] StartX=237 StartY=-19 StartZ=0 EndX=225 EndY=-19 EndZ=0
    g19: LineSegment [constr] StartX=225 StartY=-19 StartZ=0 EndX=225 EndY=-13 EndZ=0
    g20: LineSegment [constr] StartX=-237 StartY=19 StartZ=0 EndX=-237 EndY=22 EndZ=0
    g21: LineSegment [constr] StartX=-237 StartY=19 StartZ=0 EndX=-241 EndY=19 EndZ=0
    g22: LineSegment [constr] StartX=-237 StartY=-19 StartZ=0 EndX=-237 EndY=-22 EndZ=0
    g23: LineSegment [constr] StartX=-237 StartY=-19 StartZ=0 EndX=-241 EndY=-19 EndZ=0
    g24: LineSegment [constr] StartX=237 StartY=-19 StartZ=0 EndX=241 EndY=-19 EndZ=0
    g25: LineSegment [constr] StartX=237 StartY=-19 StartZ=0 EndX=237 EndY=-22 EndZ=0
    g26: LineSegment [constr] StartX=237 StartY=19 StartZ=0 EndX=241 EndY=19 EndZ=0
    g27: LineSegment [constr] StartX=237 StartY=19 StartZ=0 EndX=237 EndY=22 EndZ=0
    g28: LineSegment [constr] StartX=-221.85 StartY=1.55 StartZ=0 EndX=-211.65 EndY=1.55 EndZ=0
    g29: LineSegment [constr] StartX=-211.65 StartY=1.55 StartZ=0 EndX=-211.65 EndY=-1.55 EndZ=0
    g30: LineSegment [constr] StartX=-211.65 StartY=-1.55 StartZ=0 EndX=-221.85 EndY=-1.55 EndZ=0
    g31: LineSegment [constr] StartX=-221.85 StartY=-1.55 StartZ=0 EndX=-221.85 EndY=1.55 EndZ=0
    g32: LineSegment [constr] StartX=-203.65 StartY=1.55 StartZ=0 EndX=-193.45 EndY=1.55 EndZ=0
    g33: LineSegment [constr] StartX=-193.45 StartY=1.55 StartZ=0 EndX=-193.45 EndY=-1.55 EndZ=0
    g34: LineSegment [constr] StartX=-193.45 StartY=-1.55 StartZ=0 EndX=-203.65 EndY=-1.55 EndZ=0
    g35: LineSegment [constr] StartX=-203.65 StartY=-1.55 StartZ=0 EndX=-203.65 EndY=1.55 EndZ=0
    g36: LineSegment [constr] StartX=-185.6 StartY=14.1 StartZ=0 EndX=-182.5 EndY=14.1 EndZ=0
    g37: LineSegment [constr] StartX=-182.5 StartY=14.1 StartZ=0 EndX=-182.5 EndY=3.9 EndZ=0
    g38: LineSegment [constr] StartX=-182.5 StartY=3.9 StartZ=0 EndX=-185.6 EndY=3.9 EndZ=0
    g39: LineSegment [constr] StartX=-185.6 StartY=3.9 StartZ=0 EndX=-185.6 EndY=14.1 EndZ=0
    g40: LineSegment [constr] StartX=-185.6 StartY=-3.9 StartZ=0 EndX=-182.5 EndY=-3.9 EndZ=0
    g41: LineSegment [constr] StartX=-182.5 StartY=-3.9 StartZ=0 EndX=-182.5 EndY=-14.1 EndZ=0
    g42: LineSegment [constr] StartX=-182.5 StartY=-14.1 StartZ=0 EndX=-185.6 EndY=-14.1 EndZ=0
    g43: LineSegment [constr] StartX=-185.6 StartY=-14.1 StartZ=0 EndX=-185.6 EndY=-3.9 EndZ=0
    g44: LineSegment [constr] StartX=221.85 StartY=1.55 StartZ=0 EndX=211.65 EndY=1.55 EndZ=0
    g45: LineSegment [constr] StartX=211.65 StartY=1.55 StartZ=0 EndX=211.65 EndY=-1.55 EndZ=0
    g46: LineSegment [constr] StartX=211.65 StartY=-1.55 StartZ=0 EndX=221.85 EndY=-1.55 EndZ=0
    g47: LineSegment [constr] StartX=221.85 StartY=-1.55 StartZ=0 EndX=221.85 EndY=1.55 EndZ=0
    g48: LineSegment [constr] StartX=203.65 StartY=1.55 StartZ=0 EndX=193.45 EndY=1.55 EndZ=0
    g49: LineSegment [constr] StartX=193.45 StartY=1.55 StartZ=0 EndX=193.45 EndY=-1.55 EndZ=0
    g50: LineSegment [constr] StartX=193.45 StartY=-1.55 StartZ=0 EndX=203.65 EndY=-1.55 EndZ=0
    g51: LineSegment [constr] StartX=203.65 StartY=-1.55 StartZ=0 EndX=203.65 EndY=1.55 EndZ=0
    g52: LineSegment [constr] StartX=182.5 StartY=14.1 StartZ=0 EndX=185.6 EndY=14.1 EndZ=0
    g53: LineSegment [constr] StartX=185.6 StartY=14.1 StartZ=0 EndX=185.6 EndY=3.9 EndZ=0
    g54: LineSegment [constr] StartX=185.6 StartY=3.9 StartZ=0 EndX=182.5 EndY=3.9 EndZ=0
    g55: LineSegment [constr] StartX=182.5 StartY=3.9 StartZ=0 EndX=182.5 EndY=14.1 EndZ=0
    g56: LineSegment [constr] StartX=182.5 StartY=-3.9 StartZ=0 EndX=185.6 EndY=-3.9 EndZ=0
    g57: LineSegment [constr] StartX=185.6 StartY=-3.9 StartZ=0 EndX=185.6 EndY=-14.1 EndZ=0
    g58: LineSegment [constr] StartX=185.6 StartY=-14.1 StartZ=0 EndX=182.5 EndY=-14.1 EndZ=0
    g59: LineSegment [constr] StartX=182.5 StartY=-14.1 StartZ=0 EndX=182.5 EndY=-3.9 EndZ=0
    g60: Circle [constr] CenterX=207.65 CenterY=0 CenterZ=0 NormalX=0 NormalY=0 NormalZ=1 AngleXU=0 Radius=1.6
    g61: Circle [constr] CenterX=-207.65 CenterY=0 CenterZ=0 NormalX=0 NormalY=0 NormalZ=1 AngleXU=0 Radius=1.6
    g62: LineSegment [constr] StartX=-211.65 StartY=1.55 StartZ=0 EndX=-203.65 EndY=1.55 EndZ=0
    g63: LineSegment [constr] StartX=-185.6 StartY=3.9 StartZ=0 EndX=-185.6 EndY=-3.9 EndZ=0
    g64: LineSegment [constr] StartX=203.65 StartY=1.55 StartZ=0 EndX=211.65 EndY=1.55 EndZ=0
    g65: LineSegment [constr] StartX=185.6 StartY=3.9 StartZ=0 EndX=185.6 EndY=-3.9 EndZ=0
    g66: LineSegment [constr] StartX=-193.45 StartY=6.6e-15 StartZ=0 EndX=-185.6 EndY=6.6e-15 EndZ=0
    g67: LineSegment [constr] StartX=193.45 StartY=-1.4e-15 StartZ=0 EndX=185.6 EndY=-6.6e-15 EndZ=0
    g68: LineSegment [constr] StartX=-15.05 StartY=5.05 StartZ=0 EndX=-15.05 EndY=3.05 EndZ=0
    g69: LineSegment [constr] StartX=-15.05 StartY=3.05 StartZ=0 EndX=-17.05 EndY=3.05 EndZ=0
    g70: LineSegment StartX=-17.05 StartY=3.05 StartZ=0 EndX=-17.05 EndY=-11.05 EndZ=0
    g71: LineSegment [constr] StartX=-17.05 StartY=-11.05 StartZ=0 EndX=-15.05 EndY=-11.05 EndZ=0
    g72: LineSegment [constr] StartX=-15.05 StartY=-11.05 StartZ=0 EndX=-15.05 EndY=-13.05 EndZ=0
    g73: LineSegment StartX=-15.05 StartY=-13.05 StartZ=0 EndX=34.55 EndY=-13.05 EndZ=0
    g74: LineSegment [constr] StartX=34.55 StartY=-13.05 StartZ=0 EndX=34.55 EndY=-11.05 EndZ=0
    g75: LineSegment [constr] StartX=34.55 StartY=-11.05 StartZ=0 EndX=36.55 EndY=-11.05 EndZ=0
    g76: LineSegment StartX=36.55 StartY=-11.05 StartZ=0 EndX=36.55 EndY=3.05 EndZ=0
    g77: LineSegment [constr] StartX=36.55 StartY=3.05 StartZ=0 EndX=34.55 EndY=3.05 EndZ=0
    g78: LineSegment [constr] StartX=34.55 StartY=3.05 StartZ=0 EndX=34.55 EndY=5.05 EndZ=0
    g79: LineSegment StartX=34.55 StartY=5.05 StartZ=0 EndX=-15.05 EndY=5.05 EndZ=0
    g80: ArcOfCircle CenterX=-15.05 CenterY=3.05 CenterZ=0 NormalX=0 NormalY=0 NormalZ=1 AngleXU=0 Radius=2 StartAngle=1.5708 EndAngle=3.14159
    g81: ArcOfCircle CenterX=-15.05 CenterY=-11.05 CenterZ=0 NormalX=0 NormalY=0 NormalZ=1 AngleXU=0 Radius=2 StartAngle=3.14159 EndAngle=4.71239
    g82: ArcOfCircle CenterX=34.55 CenterY=-11.05 CenterZ=0 NormalX=0 NormalY=0 NormalZ=1 AngleXU=0 Radius=2 StartAngle=4.71239 EndAngle=6.28319
    g83: ArcOfCircle CenterX=34.55 CenterY=3.05 CenterZ=0 NormalX=0 NormalY=0 NormalZ=1 AngleXU=0 Radius=2 StartAngle=0 EndAngle=1.5708
    g84: LineSegment [constr] StartX=-15.05 StartY=3.05 StartZ=0 EndX=9.75 EndY=-4 EndZ=0
    g85: LineSegment [constr] StartX=34.55 StartY=3.05 StartZ=0 EndX=9.75 EndY=-4 EndZ=0
    g86: LineSegment [constr] StartX=34.55 StartY=-11.05 StartZ=0 EndX=9.75 EndY=-4 EndZ=0
    g87: LineSegment [constr] StartX=9.75 StartY=-4 StartZ=0 EndX=-15.05 EndY=-11.05 EndZ=0
  constraints (247):
    c: Coincident(g0,g1)
    c: Coincident(g1,g2)
    c: Coincident(g2,g3)
    c: Coincident(g3,g0)
    c: Horizontal(g0)
    c: Horizontal(g2)
    c: Vertical(g1)
    c: Vertical(g3)
    c: DistanceX(g0,g0) = 482
    c: DistanceY(g3,g3) = 44
    c: Coincident(g4,g5)
    c: Coincident(g5,g6)
    c: Coincident(g6,g7)
    c: Coincident(g7,g4)
    c: Horizontal(g4)
    c: Horizontal(g6)
    c: Vertical(g5)
    c: Vertical(g7)
    c: Coincident(g8,g9)
    c: Coincident(g9,g10)
    c: Coincident(g10,g11)
    c: Coincident(g11,g8)
    c: Horizontal(g8)
    c: Horizontal(g10)
    c: Vertical(g9)
    c: Vertical(g11)
    c: Coincident(g12,g13)
    c: Coincident(g13,g14)
    c: Coincident(g14,g15)
    c: Coincident(g15,g12)
    c: Horizontal(g12)
    c: Horizontal(g14)
    c: Vertical(g13)
    c: Vertical(g15)
    c: Coincident(g16,g17)
    c: Coincident(g17,g18)
    c: Coincident(g18,g19)
    c: Coincident(g19,g16)
    c: Horizontal(g16)
    c: Horizontal(g18)
    c: Vertical(g17)
    c: Vertical(g19)
    c: Equal(g5,g15)
    c: Equal(g15,g19)
    c: Equal(g19,g9)
    c: Equal(g6,g14)
    c: Equal(g14,g16)
    c: Equal(g16,g8)
    c: DistanceX(g4,g4) = 12
    c: DistanceY(g7,g7) = 6
    c: Coincident(g20,g4)
    c: PointOnObject(g20,g0)
    c: Vertical(g20)
    c: Coincident(g21,g4)
    c: PointOnObject(g21,g3)
    c: Horizontal(g21)
    c: Coincident(g22,g10)
    c: PointOnObject(g22,g2)
    c: Vertical(g22)
    c: Coincident(g23,g10)
    c: PointOnObject(g23,g3)
    c: Horizontal(g23)
    c: Coincident(g24,g17)
    c: PointOnObject(g24,g1)
    c: Horizontal(g24)
    c: Coincident(g25,g17)
    c: PointOnObject(g25,g2)
    c: Vertical(g25)
    c: Coincident(g26,g12)
    c: PointOnObject(g26,g1)
    c: Horizontal(g26)
    c: Coincident(g27,g12)
    c: PointOnObject(g27,g0)
    c: Vertical(g27)
    c: Equal(g21,g26)
    c: Equal(g26,g24)
    c: Equal(g24,g23)
    c: Equal(g20,g27)
    c: Equal(g27,g25)
    c: Equal(g25,g22)
    c: DistanceX(g21,g21) = 4
    c: DistanceY(g20,g20) = 3
    c: Coincident(g28,g29)
    c: Coincident(g29,g30)
    c: Coincident(g30,g31)
    c: Coincident(g31,g28)
    c: Horizontal(g28)
    c: Horizontal(g30)
    c: Vertical(g29)
    c: Vertical(g31)
    c: Coincident(g32,g33)
    c: Coincident(g33,g34)
    c: Coincident(g34,g35)
    c: Coincident(g35,g32)
    c: Horizontal(g32)
    c: Horizontal(g34)
    c: Vertical(g33)
    c: Vertical(g35)
    c: Coincident(g36,g37)
    c: Coincident(g37,g38)
    c: Coincident(g38,g39)
    c: Coincident(g39,g36)
    c: Horizontal(g36)
    c: Horizontal(g38)
    c: Vertical(g37)
    c: Vertical(g39)
    c: Coincident(g40,g41)
    c: Coincident(g41,g42)
    c: Coincident(g42,g43)
    c: Coincident(g43,g40)
    c: Horizontal(g40)
    c: Horizontal(g42)
    c: Vertical(g41)
    c: Vertical(g43)
    c: Coincident(g44,g45)
    c: Coincident(g45,g46)
    c: Coincident(g46,g47)
    c: Coincident(g47,g44)
    c: Horizontal(g44)
    c: Horizontal(g46)
    c: Vertical(g45)
    c: Vertical(g47)
    c: Coincident(g48,g49)
    c: Coincident(g49,g50)
    c: Coincident(g50,g51)
    c: Coincident(g51,g48)
    c: Horizontal(g48)
    c: Horizontal(g50)
    c: Vertical(g49)
    c: Vertical(g51)
    c: Coincident(g52,g53)
    c: Coincident(g53,g54)
    c: Coincident(g54,g55)
    c: Coincident(g55,g52)
    c: Horizontal(g52)
    c: Horizontal(g54)
    c: Vertical(g53)
    c: Vertical(g55)
    c: Coincident(g56,g57)
    c: Coincident(g57,g58)
    c: Coincident(g58,g59)
    c: Coincident(g59,g56)
    c: Horizontal(g56)
    c: Horizontal(g58)
    c: Vertical(g57)
    c: Vertical(g59)
    c: PointOnObject(g60,g-1)
    c: PointOnObject(g61,g-1)
    c: Equal(g28,g32)
    c: Equal(g32,g39)
    c: Equal(g39,g43)
    c: Equal(g43,g53)
    c: Equal(g53,g57)
    c: Equal(g57,g48)
    c: Equal(g48,g44)
    c: DistanceX(g28,g28) = 10.2
    c: DistanceY(g31,g31) = 3.1
    c: Equal(g29,g35)
    c: Equal(g35,g38)
    c: Equal(g38,g40)
    c: Equal(g40,g54)
    c: Equal(g54,g56)
    c: Equal(g56,g51)
    c: Equal(g51,g45)
    c: Symmetric(g34,g28,g61)
    c: Coincident(g62,g28)
    c: Coincident(g62,g32)
    c: Horizontal(g62)
    c: Coincident(g63,g38)
    c: Coincident(g63,g40)
    c: Vertical(g63)
    c: Coincident(g64,g48)
    c: Coincident(g64,g44)
    c: Horizontal(g64)
    c: Symmetric(g45,g48,g60)
    c: Coincident(g65,g53)
    c: Coincident(g65,g56)
    c: Vertical(g65)
    c: Equal(g64,g62)
    c: Equal(g65,g63)
    c: Horizontal(g66)
    c: Symmetric(g38,g40,g66)
    c: Symmetric(g32,g33,g66)
    c: Symmetric(g48,g49,g67)
    c: Symmetric(g53,g56,g67)
    c: DistanceX(g62,g62) = 8
    c: DistanceY(g63,g63) = 7.8
    c: Radius(g61) = 1.6
    c: DistanceX(g66,g66) = 7.85
    c: Equal(g66,g67)
    c: DistanceX(g36,g52) = 365
    c: Symmetric(g67,g66,g-1)
    c: Equal(g61,g60)
    c: Symmetric(g0,g1,g-1)
    c: Vertical(g68)
    c: Coincident(g68,g69)
    c: Horizontal(g69)
    c: Coincident(g69,g70)
    c: Vertical(g70)
    c: Coincident(g70,g71)
    c: Horizontal(g71)
    c: Coincident(g71,g72)
    c: Vertical(g72)
    c: Coincident(g72,g73)
    c: Horizontal(g73)
    c: Coincident(g73,g74)
    c: Vertical(g74)
    c: Coincident(g74,g75)
    c: Horizontal(g75)
    c: Coincident(g75,g76)
    c: Vertical(g76)
    c: Coincident(g76,g77)
    c: Horizontal(g77)
    c: Coincident(g77,g78)
    c: Vertical(g78)
    c: Coincident(g78,g79)
    c: Coincident(g79,g68)
    c: Horizontal(g79)
    c: Coincident(g80,g68)
    c: Coincident(g80,g79)
    c: Coincident(g80,g70)
    c: Coincident(g81,g71)
    c: Coincident(g81,g70)
    c: Coincident(g81,g73)
    c: Coincident(g82,g74)
    c: Coincident(g82,g76)
    c: Coincident(g82,g73)
    c: Coincident(g83,g77)
    c: Coincident(g83,g79)
    c: Coincident(g83,g76)
    c: Equal(g80,g83)
    c: Equal(g83,g82)
    c: Radius(g80) = 2
    c: DistanceX(g70,g76) = 53.6
    c: DistanceY(g73,g79) = 18.1
    c: Coincident(g84,g80)
    c: Coincident(g85,g83)
    c: Coincident(g85,g84)
    c: Coincident(g86,g82)
    c: Coincident(g84,g86)
    c: Coincident(g87,g84)
    c: Coincident(g87,g81)
    c: Equal(g84,g85)
    c: Equal(g85,g86)
    c: Equal(g86,g87)
    c: DistanceX(g-1,g84) = 9.75
    c: DistanceY(g84,g-1) = 4
FEATURE [Sketcher::SketchObject] Sketch001002036  label="Sketch Front E-Paper001"
  Placement = pos=(0,-3,0) rot=(1,0,0;1.5708rad)
  sketch-geometry (54):
    g0: LineSegment [constr] StartX=-241 StartY=22 StartZ=0 EndX=241 EndY=22 EndZ=0
    g1: LineSegment [constr] StartX=241 StartY=22 StartZ=0 EndX=241 EndY=-22 EndZ=0
    g2: LineSegment [constr] StartX=241 StartY=-22 StartZ=0 EndX=-241 EndY=-22 EndZ=0
    g3: LineSegment [constr] StartX=-241 StartY=-22 StartZ=0 EndX=-241 EndY=22 EndZ=0
    g4: LineSegment [constr] StartX=-237 StartY=19 StartZ=0 EndX=-225 EndY=19 EndZ=0
    g5: LineSegment [constr] StartX=-225 StartY=19 StartZ=0 EndX=-225 EndY=13 EndZ=0
    g6: LineSegment [constr] StartX=-225 StartY=13 StartZ=0 EndX=-237 EndY=13 EndZ=0
    g7: LineSegment [constr] StartX=-237 StartY=13 StartZ=0 EndX=-237 EndY=19 EndZ=0
    g8: LineSegment [constr] StartX=-237 StartY=-13 StartZ=0 EndX=-225 EndY=-13 EndZ=0
    g9: LineSegment [constr] StartX=-225 StartY=-13 StartZ=0 EndX=-225 EndY=-19 EndZ=0
    g10: LineSegment [constr] StartX=-225 StartY=-19 StartZ=0 EndX=-237 EndY=-19 EndZ=0
    g11: LineSegment [constr] StartX=-237 StartY=-19 StartZ=0 EndX=-237 EndY=-13 EndZ=0
    g12: LineSegment [constr] StartX=225 StartY=19 StartZ=0 EndX=237 EndY=19 EndZ=0
    g13: LineSegment [constr] StartX=237 StartY=19 StartZ=0 EndX=237 EndY=13 EndZ=0
    g14: LineSegment [constr] StartX=237 StartY=13 StartZ=0 EndX=225 EndY=13 EndZ=0
    g15: LineSegment [constr] StartX=225 StartY=13 StartZ=0 EndX=225 EndY=19 EndZ=0
    g16: LineSegment [constr] StartX=225 StartY=-13 StartZ=0 EndX=237 EndY=-13 EndZ=0
    g17: LineSegment [constr] StartX=237 StartY=-13 StartZ=0 EndX=237 EndY=-19 EndZ=0
    g18: LineSegment [constr] StartX=237 StartY=-19 StartZ=0 EndX=225 EndY=-19 EndZ=0
    g19: LineSegment [constr] StartX=225 StartY=-19 StartZ=0 EndX=225 EndY=-13 EndZ=0
    g20: LineSegment [constr] StartX=-237 StartY=19 StartZ=0 EndX=-237 EndY=22 EndZ=0
    g21: LineSegment [constr] StartX=-237 StartY=19 StartZ=0 EndX=-241 EndY=19 EndZ=0
    g22: LineSegment [constr] StartX=-237 StartY=-19 StartZ=0 EndX=-237 EndY=-22 EndZ=0
    g23: LineSegment [constr] StartX=-237 StartY=-19 StartZ=0 EndX=-241 EndY=-19 EndZ=0
    g24: LineSegment [constr] StartX=237 StartY=-19 StartZ=0 EndX=241 EndY=-19 EndZ=0
    g25: LineSegment [constr] StartX=237 StartY=-19 StartZ=0 EndX=237 EndY=-22 EndZ=0
    g26: LineSegment [constr] StartX=237 StartY=19 StartZ=0 EndX=241 EndY=19 EndZ=0
    g27: LineSegment [constr] StartX=237 StartY=19 StartZ=0 EndX=237 EndY=22 EndZ=0
    g28: LineSegment StartX=-38 StartY=15 StartZ=0 EndX=-103.5 EndY=15 EndZ=0
    g29: LineSegment StartX=-105 StartY=13.5 StartZ=0 EndX=-105 EndY=-13.5 EndZ=0
    g30: LineSegment StartX=-103.5 StartY=-15 StartZ=0 EndX=-38 EndY=-15 EndZ=0
    g31: LineSegment StartX=-36.5 StartY=-13.5 StartZ=0 EndX=-36.5 EndY=13.5 EndZ=0
    g32: LineSegment [constr] StartX=-103.5 StartY=15 StartZ=0 EndX=-103.5 EndY=13.5 EndZ=0
    g33: LineSegment [constr] StartX=-103.5 StartY=13.5 StartZ=0 EndX=-105 EndY=13.5 EndZ=0
    g34: LineSegment [constr] StartX=-38 StartY=15 StartZ=0 EndX=-38 EndY=13.5 EndZ=0
    g35: LineSegment [constr] StartX=-38 StartY=13.5 StartZ=0 EndX=-36.5 EndY=13.5 EndZ=0
    g36: LineSegment [constr] StartX=-36.5 StartY=-13.5 StartZ=0 EndX=-38 EndY=-13.5 EndZ=0
    g37: LineSegment [constr] StartX=-38 StartY=-13.5 StartZ=0 EndX=-38 EndY=-15 EndZ=0
    g38: LineSegment [constr] StartX=-103.5 StartY=-15 StartZ=0 EndX=-103.5 EndY=-13.5 EndZ=0
    g39: LineSegment [constr] StartX=-103.5 StartY=-13.5 StartZ=0 EndX=-105 EndY=-13.5 EndZ=0
    g40: ArcOfCircle CenterX=-103.5 CenterY=13.5 CenterZ=0 NormalX=0 NormalY=0 NormalZ=1 AngleXU=0 Radius=1.5 StartAngle=1.5708 EndAngle=3.14159
    g41: ArcOfCircle CenterX=-38 CenterY=13.5 CenterZ=0 NormalX=0 NormalY=0 NormalZ=1 AngleXU=0 Radius=1.5 StartAngle=0 EndAngle=1.5708
    g42: ArcOfCircle CenterX=-38 CenterY=-13.5 CenterZ=0 NormalX=0 NormalY=0 NormalZ=1 AngleXU=0 Radius=1.5 StartAngle=4.71239 EndAngle=6.28319
    g43: ArcOfCircle CenterX=-103.5 CenterY=-13.5 CenterZ=0 NormalX=0 NormalY=0 NormalZ=1 AngleXU=0 Radius=1.5 StartAngle=3.14159 EndAngle=4.71239
    g44: Circle CenterX=-118.5 CenterY=-17.5 CenterZ=0 NormalX=0 NormalY=0 NormalZ=1 AngleXU=0 Radius=1.6
    g45: Circle CenterX=-28.5 CenterY=-17.5 CenterZ=0 NormalX=0 NormalY=0 NormalZ=1 AngleXU=0 Radius=1.6
    g46: Circle CenterX=-28.5 CenterY=17.5 CenterZ=0 NormalX=0 NormalY=0 NormalZ=1 AngleXU=0 Radius=1.6
    g47: Circle CenterX=-118.5 CenterY=17.5 CenterZ=0 NormalX=0 NormalY=0 NormalZ=1 AngleXU=0 Radius=1.6
    g48: LineSegment [constr] StartX=-118.5 StartY=-17.5 StartZ=0 EndX=-118.5 EndY=17.5 EndZ=0
    g49: LineSegment [constr] StartX=-28.5 StartY=17.5 StartZ=0 EndX=-28.5 EndY=-17.5 EndZ=0
    g50: LineSegment [constr] StartX=-28.5 StartY=17.5 StartZ=0 EndX=-38 EndY=13.5 EndZ=0
    g51: LineSegment [constr] StartX=-28.5 StartY=-17.5 StartZ=0 EndX=-38 EndY=-13.5 EndZ=0
    g52: LineSegment [constr] StartX=-118.5 StartY=17.5 StartZ=0 EndX=-28.5 EndY=17.5 EndZ=0
    g53: LineSegment [constr] StartX=-118.5 StartY=-17.5 StartZ=0 EndX=-28.5 EndY=-17.5 EndZ=0
  constraints (150):
    c: Coincident(g0,g1)
    c: Coincident(g1,g2)
    c: Coincident(g2,g3)
    c: Coincident(g3,g0)
    c: Horizontal(g0)
    c: Horizontal(g2)
    c: Vertical(g1)
    c: Vertical(g3)
    c: DistanceX(g0,g0) = 482
    c: DistanceY(g3,g3) = 44
    c: Coincident(g4,g5)
    c: Coincident(g5,g6)
    c: Coincident(g6,g7)
    c: Coincident(g7,g4)
    c: Horizontal(g4)
    c: Horizontal(g6)
    c: Vertical(g5)
    c: Vertical(g7)
    c: Coincident(g8,g9)
    c: Coincident(g9,g10)
    c: Coincident(g10,g11)
    c: Coincident(g11,g8)
    c: Horizontal(g8)
    c: Horizontal(g10)
    c: Vertical(g9)
    c: Vertical(g11)
    c: Coincident(g12,g13)
    c: Coincident(g13,g14)
    c: Coincident(g14,g15)
    c: Coincident(g15,g12)
    c: Horizontal(g12)
    c: Horizontal(g14)
    c: Vertical(g13)
    c: Vertical(g15)
    c: Coincident(g16,g17)
    c: Coincident(g17,g18)
    c: Coincident(g18,g19)
    c: Coincident(g19,g16)
    c: Horizontal(g16)
    c: Horizontal(g18)
    c: Vertical(g17)
    c: Vertical(g19)
    c: Equal(g5,g15)
    c: Equal(g15,g19)
    c: Equal(g19,g9)
    c: Equal(g6,g14)
    c: Equal(g14,g16)
    c: Equal(g16,g8)
    c: DistanceX(g4,g4) = 12
    c: DistanceY(g7,g7) = 6
    c: Coincident(g20,g4)
    c: PointOnObject(g20,g0)
    c: Vertical(g20)
    c: Coincident(g21,g4)
    c: PointOnObject(g21,g3)
    c: Horizontal(g21)
    c: Coincident(g22,g10)
    c: PointOnObject(g22,g2)
    c: Vertical(g22)
    c: Coincident(g23,g10)
    c: PointOnObject(g23,g3)
    c: Horizontal(g23)
    c: Coincident(g24,g17)
    c: PointOnObject(g24,g1)
    c: Horizontal(g24)
    c: Coincident(g25,g17)
    c: PointOnObject(g25,g2)
    c: Vertical(g25)
    c: Coincident(g26,g12)
    c: PointOnObject(g26,g1)
    c: Horizontal(g26)
    c: Coincident(g27,g12)
    c: PointOnObject(g27,g0)
    c: Vertical(g27)
    c: Equal(g21,g26)
    c: Equal(g26,g24)
    c: Equal(g24,g23)
    c: Equal(g20,g27)
    c: Equal(g27,g25)
    c: Equal(g25,g22)
    c: DistanceX(g21,g21) = 4
    c: DistanceY(g20,g20) = 3
    c: Vertical(g29)
    c: Vertical(g31)
    c: Horizontal(g28)
    c: Horizontal(g30)
    c: Coincident(g28,g32)
    c: Vertical(g32)
    c: Coincident(g32,g33)
    c: Coincident(g33,g29)
    c: Horizontal(g33)
    c: Coincident(g28,g34)
    c: Vertical(g34)
    c: Coincident(g34,g35)
    c: Coincident(g35,g31)
    c: Horizontal(g35)
    c: Coincident(g31,g36)
    c: Horizontal(g36)
    c: Coincident(g36,g37)
    c: Coincident(g37,g30)
    c: Vertical(g37)
    c: Coincident(g30,g38)
    c: Vertical(g38)
    c: Coincident(g38,g39)
    c: Coincident(g39,g29)
    c: Horizontal(g39)
    c: Coincident(g40,g28)
    c: Coincident(g40,g29)
    c: Coincident(g41,g34)
    c: Coincident(g41,g28)
    c: Coincident(g41,g31)
    c: Coincident(g42,g36)
    c: Coincident(g42,g31)
    c: Coincident(g42,g30)
    c: Coincident(g43,g38)
    c: Coincident(g43,g29)
    c: Coincident(g43,g30)
    c: Coincident(g32,g40)
    c: DistanceY(g30,g28) = 30
    c: DistanceX(g29,g31) = 68.5
    c: Radius(g40) = 1.5
    c: Symmetric(g0,g1,g-1)
    c: Vertical(g49)
    c: DistanceX(g47,g46) = 90
    c: DistanceY(g48,g48) = 35
    c: Radius(g47) = 1.6
    c: Coincident(g50,g41)
    c: Coincident(g51,g42)
    c: Equal(g51,g50)
    c: Coincident(g46,g49)
    c: Coincident(g46,g50)
    c: Coincident(g45,g49)
    c: Coincident(g45,g51)
    c: Coincident(g44,g48)
    c: Coincident(g47,g48)
    c: Coincident(g52,g47)
    c: Horizontal(g52)
    c: Coincident(g53,g44)
    c: Horizontal(g53)
    c: Symmetric(g47,g44,g-1)
    c: Coincident(g52,g46)
    c: Coincident(g53,g45)
    c: Equal(g47,g46)
    c: Equal(g46,g45)
    c: Equal(g45,g44)
    c: DistanceX(g44,g-1) = 118.5
    c: DistanceX(g31,g45) = 8
    c: Equal(g40,g41)
    c: Equal(g41,g42)
    c: Equal(g42,g43)
FEATURE [Sketcher::SketchObject] Sketch001002037  label="Sketch Front Segment&Ambiente001"
  Placement = pos=(0,-3,0) rot=(1,0,0;1.5708rad)
  sketch-geometry (90):
    g0: LineSegment [constr] StartX=-241 StartY=22 StartZ=0 EndX=241 EndY=22 EndZ=0
    g1: LineSegment [constr] StartX=241 StartY=22 StartZ=0 EndX=241 EndY=-22 EndZ=0
    g2: LineSegment [constr] StartX=241 StartY=-22 StartZ=0 EndX=-241 EndY=-22 EndZ=0
    g3: LineSegment [constr] StartX=-241 StartY=-22 StartZ=0 EndX=-241 EndY=22 EndZ=0
    g4: LineSegment [constr] StartX=-237 StartY=19 StartZ=0 EndX=-225 EndY=19 EndZ=0
    g5: LineSegment [constr] StartX=-225 StartY=19 StartZ=0 EndX=-225 EndY=13 EndZ=0
    g6: LineSegment [constr] StartX=-225 StartY=13 StartZ=0 EndX=-237 EndY=13 EndZ=0
    g7: LineSegment [constr] StartX=-237 StartY=13 StartZ=0 EndX=-237 EndY=19 EndZ=0
    g8: LineSegment [constr] StartX=-237 StartY=-13 StartZ=0 EndX=-225 EndY=-13 EndZ=0
    g9: LineSegment [constr] StartX=-225 StartY=-13 StartZ=0 EndX=-225 EndY=-19 EndZ=0
    g10: LineSegment [constr] StartX=-225 StartY=-19 StartZ=0 EndX=-237 EndY=-19 EndZ=0
    g11: LineSegment [constr] StartX=-237 StartY=-19 StartZ=0 EndX=-237 EndY=-13 EndZ=0
    g12: LineSegment [constr] StartX=225 StartY=19 StartZ=0 EndX=237 EndY=19 EndZ=0
    g13: LineSegment [constr] StartX=237 StartY=19 StartZ=0 EndX=237 EndY=13 EndZ=0
    g14: LineSegment [constr] StartX=237 StartY=13 StartZ=0 EndX=225 EndY=13 EndZ=0
    g15: LineSegment [constr] StartX=225 StartY=13 StartZ=0 EndX=225 EndY=19 EndZ=0
    g16: LineSegment [constr] StartX=225 StartY=-13 StartZ=0 EndX=237 EndY=-13 EndZ=0
    g17: LineSegment [constr] StartX=237 StartY=-13 StartZ=0 EndX=237 EndY=-19 EndZ=0
    g18: LineSegment [constr] StartX=237 StartY=-19 StartZ=0 EndX=225 EndY=-19 EndZ=0
    g19: LineSegment [constr] StartX=225 StartY=-19 StartZ=0 EndX=225 EndY=-13 EndZ=0
    g20: LineSegment [constr] StartX=-237 StartY=19 StartZ=0 EndX=-237 EndY=22 EndZ=0
    g21: LineSegment [constr] StartX=-237 StartY=19 StartZ=0 EndX=-241 EndY=19 EndZ=0
    g22: LineSegment [constr] StartX=-237 StartY=-19 StartZ=0 EndX=-237 EndY=-22 EndZ=0
    g23: LineSegment [constr] StartX=-237 StartY=-19 StartZ=0 EndX=-241 EndY=-19 EndZ=0
    g24: LineSegment [constr] StartX=237 StartY=-19 StartZ=0 EndX=241 EndY=-19 EndZ=0
    g25: LineSegment [constr] StartX=237 StartY=-19 StartZ=0 EndX=237 EndY=-22 EndZ=0
    g26: LineSegment [constr] StartX=237 StartY=19 StartZ=0 EndX=241 EndY=19 EndZ=0
    g27: LineSegment [constr] StartX=237 StartY=19 StartZ=0 EndX=237 EndY=22 EndZ=0
    g28: LineSegment [constr] StartX=128 StartY=12.95 StartZ=0 EndX=188 EndY=12.95 EndZ=0
    g29: LineSegment [constr] StartX=188 StartY=12.95 StartZ=0 EndX=188 EndY=-7.05 EndZ=0
    g30: LineSegment [constr] StartX=188 StartY=-7.05 StartZ=0 EndX=128 EndY=-7.05 EndZ=0
    g31: LineSegment [constr] StartX=128 StartY=-7.05 StartZ=0 EndX=128 EndY=12.95 EndZ=0
    g32: Circle CenterX=128 CenterY=12.95 CenterZ=0 NormalX=0 NormalY=0 NormalZ=1 AngleXU=0 Radius=1.6
    g33: Circle CenterX=188 CenterY=12.95 CenterZ=0 NormalX=0 NormalY=0 NormalZ=1 AngleXU=0 Radius=1.6
    g34: Circle CenterX=188 CenterY=-7.05 CenterZ=0 NormalX=0 NormalY=0 NormalZ=1 AngleXU=0 Radius=1.6
    g35: Circle CenterX=128 CenterY=-7.05 CenterZ=0 NormalX=0 NormalY=0 NormalZ=1 AngleXU=0 Radius=1.6
    g36: LineSegment [constr] StartX=146.45 StartY=10 StartZ=0 EndX=188.55 EndY=10 EndZ=0
    g37: LineSegment [constr] StartX=188.55 StartY=10 StartZ=0 EndX=188.55 EndY=-4.1 EndZ=0
    g38: LineSegment [constr] StartX=188.55 StartY=-4.1 StartZ=0 EndX=146.45 EndY=-4.1 EndZ=0
    g39: LineSegment [constr] StartX=146.45 StartY=-4.1 StartZ=0 EndX=146.45 EndY=10 EndZ=0
    g40: LineSegment [constr] StartX=146.45 StartY=10 StartZ=0 EndX=146.45 EndY=12.95 EndZ=0
    g41: LineSegment [constr] StartX=146.45 StartY=-4.1 StartZ=0 EndX=146.45 EndY=-7.05 EndZ=0
    g42: LineSegment [constr] StartX=96.35 StartY=-7.05 StartZ=0 EndX=116.35 EndY=-7.05 EndZ=0
    g43: LineSegment [constr] StartX=116.35 StartY=-7.05 StartZ=0 EndX=116.35 EndY=-17.05 EndZ=0
    g44: LineSegment [constr] StartX=116.35 StartY=-17.05 StartZ=0 EndX=96.35 EndY=-17.05 EndZ=0
    g45: LineSegment [constr] StartX=96.35 StartY=-17.05 StartZ=0 EndX=96.35 EndY=-7.05 EndZ=0
    g46: LineSegment [constr] StartX=106.35 StartY=-14.55 StartZ=0 EndX=111.35 EndY=-14.55 EndZ=0
    g47: LineSegment [constr] StartX=111.35 StartY=-14.55 StartZ=0 EndX=111.35 EndY=-18.05 EndZ=0
    g48: LineSegment [constr] StartX=111.35 StartY=-18.05 StartZ=0 EndX=106.35 EndY=-18.05 EndZ=0
    g49: LineSegment [constr] StartX=106.35 StartY=-18.05 StartZ=0 EndX=106.35 EndY=-14.55 EndZ=0
    g50: Circle CenterX=96.35 CenterY=-7.05 CenterZ=0 NormalX=0 NormalY=0 NormalZ=1 AngleXU=0 Radius=1.6
    g51: Circle CenterX=116.35 CenterY=-7.05 CenterZ=0 NormalX=0 NormalY=0 NormalZ=1 AngleXU=0 Radius=1.6
    g52: Circle CenterX=116.35 CenterY=-17.05 CenterZ=0 NormalX=0 NormalY=0 NormalZ=1 AngleXU=0 Radius=1.6
    g53: Circle CenterX=96.35 CenterY=-17.05 CenterZ=0 NormalX=0 NormalY=0 NormalZ=1 AngleXU=0 Radius=1.6
    g54: LineSegment StartX=107.85 StartY=-14.55 StartZ=0 EndX=109.85 EndY=-14.55 EndZ=0
    g55: LineSegment [constr] StartX=109.85 StartY=-14.55 StartZ=0 EndX=109.85 EndY=-16.05 EndZ=0
    g56: LineSegment [constr] StartX=109.85 StartY=-16.05 StartZ=0 EndX=111.35 EndY=-16.05 EndZ=0
    g57: LineSegment StartX=111.35 StartY=-16.05 StartZ=0 EndX=111.35 EndY=-16.55 EndZ=0
    g58: LineSegment [constr] StartX=111.35 StartY=-16.55 StartZ=0 EndX=109.85 EndY=-16.55 EndZ=0
    g59: LineSegment [constr] StartX=109.85 StartY=-16.55 StartZ=0 EndX=109.85 EndY=-18.05 EndZ=0
    g60: LineSegment StartX=109.85 StartY=-18.05 StartZ=0 EndX=107.85 EndY=-18.05 EndZ=0
    g61: LineSegment [constr] StartX=107.85 StartY=-18.05 StartZ=0 EndX=107.85 EndY=-16.55 EndZ=0
    g62: LineSegment [constr] StartX=107.85 StartY=-16.55 StartZ=0 EndX=106.35 EndY=-16.55 EndZ=0
    g63: LineSegment StartX=106.35 StartY=-16.55 StartZ=0 EndX=106.35 EndY=-16.05 EndZ=0
    g64: LineSegment [constr] StartX=106.35 StartY=-16.05 StartZ=0 EndX=107.85 EndY=-16.05 EndZ=0
    g65: LineSegment [constr] StartX=107.85 StartY=-16.05 StartZ=0 EndX=107.85 EndY=-14.55 EndZ=0
    g66: ArcOfCircle CenterX=107.85 CenterY=-16.05 CenterZ=0 NormalX=0 NormalY=0 NormalZ=1 AngleXU=0 Radius=1.5 StartAngle=1.5708 EndAngle=3.14159
    g67: ArcOfCircle CenterX=109.85 CenterY=-16.05 CenterZ=0 NormalX=0 NormalY=0 NormalZ=1 AngleXU=0 Radius=1.5 StartAngle=0 EndAngle=1.5708
    g68: ArcOfCircle CenterX=109.85 CenterY=-16.55 CenterZ=0 NormalX=0 NormalY=0 NormalZ=1 AngleXU=0 Radius=1.5 StartAngle=4.71239 EndAngle=6.28319
    g69: ArcOfCircle CenterX=107.85 CenterY=-16.55 CenterZ=0 NormalX=0 NormalY=0 NormalZ=1 AngleXU=0 Radius=1.5 StartAngle=3.14159 EndAngle=4.71239
    g70: LineSegment StartX=147.45 StartY=10 StartZ=0 EndX=187.55 EndY=10 EndZ=0
    g71: LineSegment [constr] StartX=187.55 StartY=10 StartZ=0 EndX=187.55 EndY=9 EndZ=0
    g72: LineSegment [constr] StartX=187.55 StartY=9 StartZ=0 EndX=188.55 EndY=9 EndZ=0
    g73: LineSegment StartX=188.55 StartY=9 StartZ=0 EndX=188.55 EndY=-3.1 EndZ=0
    g74: LineSegment [constr] StartX=188.55 StartY=-3.1 StartZ=0 EndX=187.55 EndY=-3.1 EndZ=0
    g75: LineSegment [constr] StartX=187.55 StartY=-3.1 StartZ=0 EndX=187.55 EndY=-4.1 EndZ=0
    g76: LineSegment StartX=187.55 StartY=-4.1 StartZ=0 EndX=147.45 EndY=-4.1 EndZ=0
    g77: LineSegment [constr] StartX=147.45 StartY=-4.1 StartZ=0 EndX=147.45 EndY=-3.1 EndZ=0
    g78: LineSegment [constr] StartX=147.45 StartY=-3.1 StartZ=0 EndX=146.45 EndY=-3.1 EndZ=0
    g79: LineSegment StartX=146.45 StartY=-3.1 StartZ=0 EndX=146.45 EndY=9 EndZ=0
    g80: LineSegment [constr] StartX=146.45 StartY=9 StartZ=0 EndX=147.45 EndY=9 EndZ=0
    g81: LineSegment [constr] StartX=147.45 StartY=9 StartZ=0 EndX=147.45 EndY=10 EndZ=0
    g82: ArcOfCircle CenterX=147.45 CenterY=9 CenterZ=0 NormalX=0 NormalY=0 NormalZ=1 AngleXU=0 Radius=1 StartAngle=1.5708 EndAngle=3.14159
    g83: ArcOfCircle CenterX=187.55 CenterY=9 CenterZ=0 NormalX=0 NormalY=0 NormalZ=1 AngleXU=0 Radius=1 StartAngle=0 EndAngle=1.5708
    g84: ArcOfCircle CenterX=187.55 CenterY=-3.1 CenterZ=0 NormalX=0 NormalY=0 NormalZ=1 AngleXU=0 Radius=1 StartAngle=4.71239 EndAngle=6.28319
    g85: ArcOfCircle CenterX=147.45 CenterY=-3.1 CenterZ=0 NormalX=0 NormalY=0 NormalZ=1 AngleXU=0 Radius=1 StartAngle=3.14159 EndAngle=4.71239
    g86: LineSegment [constr] StartX=147.45 StartY=9 StartZ=0 EndX=167.5 EndY=2.95 EndZ=0
    g87: LineSegment [constr] StartX=167.5 StartY=2.95 StartZ=0 EndX=187.55 EndY=9 EndZ=0
    g88: LineSegment [constr] StartX=167.5 StartY=2.95 StartZ=0 EndX=187.55 EndY=-3.1 EndZ=0
    g89: LineSegment [constr] StartX=167.5 StartY=2.95 StartZ=0 EndX=147.45 EndY=-3.1 EndZ=0
  constraints (250):
    c: Coincident(g0,g1)
    c: Coincident(g1,g2)
    c: Coincident(g2,g3)
    c: Coincident(g3,g0)
    c: Horizontal(g0)
    c: Horizontal(g2)
    c: Vertical(g1)
    c: Vertical(g3)
    c: DistanceX(g0,g0) = 482
    c: DistanceY(g3,g3) = 44
    c: Coincident(g4,g5)
    c: Coincident(g5,g6)
    c: Coincident(g6,g7)
    c: Coincident(g7,g4)
    c: Horizontal(g4)
    c: Horizontal(g6)
    c: Vertical(g5)
    c: Vertical(g7)
    c: Coincident(g8,g9)
    c: Coincident(g9,g10)
    c: Coincident(g10,g11)
    c: Coincident(g11,g8)
    c: Horizontal(g8)
    c: Horizontal(g10)
    c: Vertical(g9)
    c: Vertical(g11)
    c: Coincident(g12,g13)
    c: Coincident(g13,g14)
    c: Coincident(g14,g15)
    c: Coincident(g15,g12)
    c: Horizontal(g12)
    c: Horizontal(g14)
    c: Vertical(g13)
    c: Vertical(g15)
    c: Coincident(g16,g17)
    c: Coincident(g17,g18)
    c: Coincident(g18,g19)
    c: Coincident(g19,g16)
    c: Horizontal(g16)
    c: Horizontal(g18)
    c: Vertical(g17)
    c: Vertical(g19)
    c: Equal(g5,g15)
    c: Equal(g15,g19)
    c: Equal(g19,g9)
    c: Equal(g6,g14)
    c: Equal(g14,g16)
    c: Equal(g16,g8)
    c: DistanceX(g4,g4) = 12
    c: DistanceY(g7,g7) = 6
    c: Coincident(g20,g4)
    c: PointOnObject(g20,g0)
    c: Vertical(g20)
    c: Coincident(g21,g4)
    c: PointOnObject(g21,g3)
    c: Horizontal(g21)
    c: Coincident(g22,g10)
    c: PointOnObject(g22,g2)
    c: Vertical(g22)
    c: Coincident(g23,g10)
    c: PointOnObject(g23,g3)
    c: Horizontal(g23)
    c: Coincident(g24,g17)
    c: PointOnObject(g24,g1)
    c: Horizontal(g24)
    c: Coincident(g25,g17)
    c: PointOnObject(g25,g2)
    c: Vertical(g25)
    c: Coincident(g26,g12)
    c: PointOnObject(g26,g1)
    c: Horizontal(g26)
    c: Coincident(g27,g12)
    c: PointOnObject(g27,g0)
    c: Vertical(g27)
    c: Equal(g21,g26)
    c: Equal(g26,g24)
    c: Equal(g24,g23)
    c: Equal(g20,g27)
    c: Equal(g27,g25)
    c: Equal(g25,g22)
    c: DistanceX(g21,g21) = 4
    c: DistanceY(g20,g20) = 3
    c: Symmetric(g0,g1,g-1)
    c: Coincident(g29,g30)
    c: Coincident(g30,g31)
    c: Horizontal(g28)
    c: Horizontal(g30)
    c: Vertical(g29)
    c: Coincident(g34,g29)
    c: Coincident(g35,g30)
    c: Equal(g32,g33)
    c: Equal(g33,g34)
    c: Equal(g34,g35)
    c: DistanceX(g28,g28) = 60
    c: Coincident(g36,g37)
    c: Coincident(g37,g38)
    c: Coincident(g38,g39)
    c: Coincident(g39,g36)
    c: Horizontal(g36)
    c: Horizontal(g38)
    c: Vertical(g37)
    c: Vertical(g39)
    c: Coincident(g40,g36)
    c: PointOnObject(g40,g28)
    c: Vertical(g40)
    c: Coincident(g41,g38)
    c: PointOnObject(g41,g30)
    c: Vertical(g41)
    c: Equal(g40,g41)
    c: DistanceX(g36,g36) = 42.1
    c: DistanceY(g39,g39) = 14.1
    c: Coincident(g28,g33)
    c: Coincident(g28,g29)
    c: Coincident(g28,g31)
    c: Coincident(g28,g32)
    c: Vertical(g31)
    c: Coincident(g42,g43)
    c: Coincident(g43,g44)
    c: Coincident(g44,g45)
    c: Coincident(g45,g42)
    c: Horizontal(g42)
    c: Horizontal(g44)
    c: Vertical(g43)
    c: Vertical(g45)
    c: DistanceY(g45,g45) = 10
    c: DistanceX(g42,g42) = 20
    c: Coincident(g46,g47)
    c: Coincident(g47,g48)
    c: Coincident(g48,g49)
    c: Coincident(g49,g46)
    c: Horizontal(g46)
    c: Horizontal(g48)
    c: Vertical(g47)
    c: Vertical(g49)
    c: Coincident(g50,g42)
    c: Coincident(g51,g42)
    c: Coincident(g52,g43)
    c: Coincident(g53,g44)
    c: DistanceX(g46,g46) = 5
    c: DistanceY(g49,g49) = 3.5
    c: DistanceY(g47,g52) = 1
    c: DistanceX(g46,g52) = 5
    c: Equal(g50,g51)
    c: Equal(g51,g52)
    c: Equal(g52,g53)
    c: Equal(g35,g50)
    c: DistanceY(g51,g35) = 0
    c: Radius(g32) = 1.6
    c: DistanceY(g31,g31) = 20
    c: DistanceX(g51,g34) = 71.65
    c: DistanceY(g-1,g33) = 12.95
    c: DistanceX(g-1,g35) = 128
    c: PointOnObject(g54,g46)
    c: Horizontal(g54)
    c: Coincident(g54,g55)
    c: Vertical(g55)
    c: Coincident(g55,g56)
    c: PointOnObject(g56,g47)
    c: Horizontal(g56)
    c: Coincident(g56,g57)
    c: Vertical(g57)
    c: Coincident(g57,g58)
    c: Horizontal(g58)
    c: Coincident(g58,g59)
    c: PointOnObject(g59,g48)
    c: Vertical(g59)
    c: Coincident(g59,g60)
    c: Horizontal(g60)
    c: Coincident(g60,g61)
    c: Vertical(g61)
    c: Coincident(g61,g62)
    c: PointOnObject(g62,g49)
    c: Horizontal(g62)
    c: Coincident(g62,g63)
    c: Vertical(g63)
    c: Coincident(g63,g64)
    c: Horizontal(g64)
    c: Coincident(g64,g65)
    c: Coincident(g65,g54)
    c: Vertical(g65)
    c: Coincident(g66,g64)
    c: Coincident(g66,g54)
    c: Coincident(g66,g63)
    c: Coincident(g67,g55)
    c: Coincident(g67,g54)
    c: Coincident(g67,g57)
    c: Coincident(g68,g58)
    c: Coincident(g68,g57)
    c: Coincident(g68,g60)
    c: Coincident(g69,g61)
    c: Coincident(g69,g63)
    c: Coincident(g69,g60)
    c: Equal(g66,g67)
    c: Equal(g67,g68)
    c: Equal(g68,g69)
    c: Radius(g66) = 1.5
    c: PointOnObject(g70,g36)
    c: Horizontal(g70)
    c: Coincident(g70,g71)
    c: Vertical(g71)
    c: Coincident(g71,g72)
    c: PointOnObject(g72,g37)
    c: Horizontal(g72)
    c: Coincident(g72,g73)
    c: Vertical(g73)
    c: Coincident(g73,g74)
    c: Horizontal(g74)
    c: Coincident(g74,g75)
    c: PointOnObject(g75,g38)
    c: Vertical(g75)
    c: Coincident(g75,g76)
    c: Horizontal(g76)
    c: Coincident(g76,g77)
    c: Vertical(g77)
    c: Coincident(g77,g78)
    c: PointOnObject(g78,g39)
    c: Horizontal(g78)
    c: Coincident(g78,g79)
    c: Vertical(g79)
    c: Coincident(g79,g80)
    c: Horizontal(g80)
    c: Coincident(g80,g81)
    c: Coincident(g81,g70)
    c: Vertical(g81)
    c: Coincident(g82,g80)
    c: Coincident(g82,g70)
    c: Coincident(g82,g79)
    c: Coincident(g83,g71)
    c: Coincident(g83,g70)
    c: Coincident(g83,g73)
    c: Coincident(g84,g74)
    c: Coincident(g84,g73)
    c: Coincident(g84,g76)
    c: Coincident(g85,g77)
    c: Coincident(g85,g79)
    c: Coincident(g85,g76)
    c: Equal(g82,g83)
    c: Equal(g83,g84)
    c: Radius(g82) = 1
    c: Coincident(g86,g82)
    c: Coincident(g87,g86)
    c: Coincident(g87,g83)
    c: Coincident(g88,g86)
    c: Coincident(g88,g84)
    c: Coincident(g89,g86)
    c: Coincident(g89,g85)
    c: Equal(g86,g87)
    c: Equal(g87,g88)
    c: Equal(g88,g89)
    c: DistanceX(g35,g86) = 39.5
FEATURE [Sketcher::SketchObject] Sketch001002038  label="Sketch Front Motion001"
  Placement = pos=(0,-3,0) rot=(1,0,0;1.5708rad)
  sketch-geometry (60):
    g0: LineSegment [constr] StartX=-241 StartY=22 StartZ=0 EndX=241 EndY=22 EndZ=0
    g1: LineSegment [constr] StartX=241 StartY=22 StartZ=0 EndX=241 EndY=-22 EndZ=0
    g2: LineSegment [constr] StartX=241 StartY=-22 StartZ=0 EndX=-241 EndY=-22 EndZ=0
    g3: LineSegment [constr] StartX=-241 StartY=-22 StartZ=0 EndX=-241 EndY=22 EndZ=0
    g4: LineSegment [constr] StartX=-237 StartY=19 StartZ=0 EndX=-225 EndY=19 EndZ=0
    g5: LineSegment [constr] StartX=-225 StartY=19 StartZ=0 EndX=-225 EndY=13 EndZ=0
    g6: LineSegment [constr] StartX=-225 StartY=13 StartZ=0 EndX=-237 EndY=13 EndZ=0
    g7: LineSegment [constr] StartX=-237 StartY=13 StartZ=0 EndX=-237 EndY=19 EndZ=0
    g8: LineSegment [constr] StartX=-237 StartY=-13 StartZ=0 EndX=-225 EndY=-13 EndZ=0
    g9: LineSegment [constr] StartX=-225 StartY=-13 StartZ=0 EndX=-225 EndY=-19 EndZ=0
    g10: LineSegment [constr] StartX=-225 StartY=-19 StartZ=0 EndX=-237 EndY=-19 EndZ=0
    g11: LineSegment [constr] StartX=-237 StartY=-19 StartZ=0 EndX=-237 EndY=-13 EndZ=0
    g12: LineSegment [constr] StartX=225 StartY=19 StartZ=0 EndX=237 EndY=19 EndZ=0
    g13: LineSegment [constr] StartX=237 StartY=19 StartZ=0 EndX=237 EndY=13 EndZ=0
    g14: LineSegment [constr] StartX=237 StartY=13 StartZ=0 EndX=225 EndY=13 EndZ=0
    g15: LineSegment [constr] StartX=225 StartY=13 StartZ=0 EndX=225 EndY=19 EndZ=0
    g16: LineSegment [constr] StartX=225 StartY=-13 StartZ=0 EndX=237 EndY=-13 EndZ=0
    g17: LineSegment [constr] StartX=237 StartY=-13 StartZ=0 EndX=237 EndY=-19 EndZ=0
    g18: LineSegment [constr] StartX=237 StartY=-19 StartZ=0 EndX=225 EndY=-19 EndZ=0
    g19: LineSegment [constr] StartX=225 StartY=-19 StartZ=0 EndX=225 EndY=-13 EndZ=0
    g20: LineSegment [constr] StartX=-237 StartY=19 StartZ=0 EndX=-237 EndY=22 EndZ=0
    g21: LineSegment [constr] StartX=-237 StartY=19 StartZ=0 EndX=-241 EndY=19 EndZ=0
    g22: LineSegment [constr] StartX=-237 StartY=-19 StartZ=0 EndX=-237 EndY=-22 EndZ=0
    g23: LineSegment [constr] StartX=-237 StartY=-19 StartZ=0 EndX=-241 EndY=-19 EndZ=0
    g24: LineSegment [constr] StartX=237 StartY=-19 StartZ=0 EndX=241 EndY=-19 EndZ=0
    g25: LineSegment [constr] StartX=237 StartY=-19 StartZ=0 EndX=237 EndY=-22 EndZ=0
    g26: LineSegment [constr] StartX=237 StartY=19 StartZ=0 EndX=241 EndY=19 EndZ=0
    g27: LineSegment [constr] StartX=237 StartY=19 StartZ=0 EndX=237 EndY=22 EndZ=0
    g28: LineSegment [constr] StartX=45 StartY=12.95 StartZ=0 EndX=85 EndY=12.95 EndZ=0
    g29: LineSegment [constr] StartX=85 StartY=12.95 StartZ=0 EndX=85 EndY=-7.05 EndZ=0
    g30: LineSegment [constr] StartX=85 StartY=-7.05 StartZ=0 EndX=45 EndY=-7.05 EndZ=0
    g31: LineSegment [constr] StartX=45 StartY=-7.05 StartZ=0 EndX=45 EndY=12.95 EndZ=0
    g32: Circle CenterX=45 CenterY=12.95 CenterZ=0 NormalX=0 NormalY=0 NormalZ=1 AngleXU=0 Radius=1.6
    g33: Circle CenterX=85 CenterY=12.95 CenterZ=0 NormalX=0 NormalY=0 NormalZ=1 AngleXU=0 Radius=1.6
    g34: Circle CenterX=85 CenterY=-7.05 CenterZ=0 NormalX=0 NormalY=0 NormalZ=1 AngleXU=0 Radius=1.6
    g35: Circle CenterX=45 CenterY=-7.05 CenterZ=0 NormalX=0 NormalY=0 NormalZ=1 AngleXU=0 Radius=1.6
    g36: LineSegment [constr] StartX=52.95 StartY=15 StartZ=0 EndX=77.05 EndY=15 EndZ=0
    g37: LineSegment [constr] StartX=77.05 StartY=15 StartZ=0 EndX=77.05 EndY=-9.1 EndZ=0
    g38: LineSegment [constr] StartX=77.05 StartY=-9.1 StartZ=0 EndX=52.95 EndY=-9.1 EndZ=0
    g39: LineSegment [constr] StartX=52.95 StartY=-9.1 StartZ=0 EndX=52.95 EndY=15 EndZ=0
    g40: LineSegment [constr] StartX=45 StartY=12.95 StartZ=0 EndX=52.95 EndY=15 EndZ=0
    g41: LineSegment [constr] StartX=85 StartY=12.95 StartZ=0 EndX=77.05 EndY=15 EndZ=0
    g42: LineSegment [constr] StartX=85 StartY=-7.05 StartZ=0 EndX=77.05 EndY=-9.1 EndZ=0
    g43: LineSegment [constr] StartX=45 StartY=-7.05 StartZ=0 EndX=52.95 EndY=-9.1 EndZ=0
    g44: LineSegment StartX=53.95 StartY=15 StartZ=0 EndX=76.05 EndY=15 EndZ=0
    g45: LineSegment [constr] StartX=76.05 StartY=15 StartZ=0 EndX=76.05 EndY=14 EndZ=0
    g46: LineSegment [constr] StartX=76.05 StartY=14 StartZ=0 EndX=77.05 EndY=14 EndZ=0
    g47: LineSegment StartX=77.05 StartY=14 StartZ=0 EndX=77.05 EndY=-8.1 EndZ=0
    g48: LineSegment [constr] StartX=77.05 StartY=-8.1 StartZ=0 EndX=76.05 EndY=-8.1 EndZ=0
    g49: LineSegment [constr] StartX=76.05 StartY=-8.1 StartZ=0 EndX=76.05 EndY=-9.1 EndZ=0
    g50: LineSegment StartX=76.05 StartY=-9.1 StartZ=0 EndX=53.95 EndY=-9.1 EndZ=0
    g51: LineSegment [constr] StartX=53.95 StartY=-9.1 StartZ=0 EndX=53.95 EndY=-8.1 EndZ=0
    g52: LineSegment [constr] StartX=53.95 StartY=-8.1 StartZ=0 EndX=52.95 EndY=-8.1 EndZ=0
    g53: LineSegment StartX=52.95 StartY=-8.1 StartZ=0 EndX=52.95 EndY=14 EndZ=0
    g54: LineSegment [constr] StartX=52.95 StartY=14 StartZ=0 EndX=53.95 EndY=14 EndZ=0
    g55: LineSegment [constr] StartX=53.95 StartY=14 StartZ=0 EndX=53.95 EndY=15 EndZ=0
    g56: ArcOfCircle CenterX=53.95 CenterY=14 CenterZ=0 NormalX=0 NormalY=0 NormalZ=1 AngleXU=0 Radius=1 StartAngle=1.5708 EndAngle=3.14159
    g57: ArcOfCircle CenterX=76.05 CenterY=14 CenterZ=0 NormalX=0 NormalY=0 NormalZ=1 AngleXU=0 Radius=1 StartAngle=0 EndAngle=1.5708
    g58: ArcOfCircle CenterX=76.05 CenterY=-8.1 CenterZ=0 NormalX=0 NormalY=0 NormalZ=1 AngleXU=0 Radius=1 StartAngle=4.71239 EndAngle=6.28319
    g59: ArcOfCircle CenterX=53.95 CenterY=-8.1 CenterZ=0 NormalX=0 NormalY=0 NormalZ=1 AngleXU=0 Radius=1 StartAngle=3.14159 EndAngle=4.71239
  constraints (167):
    c: Coincident(g0,g1)
    c: Coincident(g1,g2)
    c: Coincident(g2,g3)
    c: Coincident(g3,g0)
    c: Horizontal(g0)
    c: Horizontal(g2)
    c: Vertical(g1)
    c: Vertical(g3)
    c: DistanceX(g0,g0) = 482
    c: DistanceY(g3,g3) = 44
    c: Coincident(g4,g5)
    c: Coincident(g5,g6)
    c: Coincident(g6,g7)
    c: Coincident(g7,g4)
    c: Horizontal(g4)
    c: Horizontal(g6)
    c: Vertical(g5)
    c: Vertical(g7)
    c: Coincident(g8,g9)
    c: Coincident(g9,g10)
    c: Coincident(g10,g11)
    c: Coincident(g11,g8)
    c: Horizontal(g8)
    c: Horizontal(g10)
    c: Vertical(g9)
    c: Vertical(g11)
    c: Coincident(g12,g13)
    c: Coincident(g13,g14)
    c: Coincident(g14,g15)
    c: Coincident(g15,g12)
    c: Horizontal(g12)
    c: Horizontal(g14)
    c: Vertical(g13)
    c: Vertical(g15)
    c: Coincident(g16,g17)
    c: Coincident(g17,g18)
    c: Coincident(g18,g19)
    c: Coincident(g19,g16)
    c: Horizontal(g16)
    c: Horizontal(g18)
    c: Vertical(g17)
    c: Vertical(g19)
    c: Equal(g5,g15)
    c: Equal(g15,g19)
    c: Equal(g19,g9)
    c: Equal(g6,g14)
    c: Equal(g14,g16)
    c: Equal(g16,g8)
    c: DistanceX(g4,g4) = 12
    c: DistanceY(g7,g7) = 6
    c: Coincident(g20,g4)
    c: PointOnObject(g20,g0)
    c: Vertical(g20)
    c: Coincident(g21,g4)
    c: PointOnObject(g21,g3)
    c: Horizontal(g21)
    c: Coincident(g22,g10)
    c: PointOnObject(g22,g2)
    c: Vertical(g22)
    c: Coincident(g23,g10)
    c: PointOnObject(g23,g3)
    c: Horizontal(g23)
    c: Coincident(g24,g17)
    c: PointOnObject(g24,g1)
    c: Horizontal(g24)
    c: Coincident(g25,g17)
    c: PointOnObject(g25,g2)
    c: Vertical(g25)
    c: Coincident(g26,g12)
    c: PointOnObject(g26,g1)
    c: Horizontal(g26)
    c: Coincident(g27,g12)
    c: PointOnObject(g27,g0)
    c: Vertical(g27)
    c: Equal(g21,g26)
    c: Equal(g26,g24)
    c: Equal(g24,g23)
    c: Equal(g20,g27)
    c: Equal(g27,g25)
    c: Equal(g25,g22)
    c: DistanceX(g21,g21) = 4
    c: DistanceY(g20,g20) = 3
    c: Symmetric(g0,g1,g-1)
    c: Coincident(g29,g30)
    c: Coincident(g30,g31)
    c: Coincident(g31,g28)
    c: Horizontal(g28)
    c: Horizontal(g30)
    c: Vertical(g29)
    c: Coincident(g32,g28)
    c: Coincident(g34,g29)
    c: Coincident(g35,g30)
    c: DistanceY(g31,g31) = 20
    c: Coincident(g36,g37)
    c: Coincident(g37,g38)
    c: Coincident(g38,g39)
    c: Coincident(g39,g36)
    c: Horizontal(g36)
    c: Horizontal(g38)
    c: Vertical(g37)
    c: DistanceX(g36,g36) = 24.1
    c: Equal(g39,g36)
    c: Coincident(g40,g32)
    c: Coincident(g40,g36)
    c: Coincident(g41,g36)
    c: Coincident(g42,g34)
    c: Coincident(g42,g37)
    c: Coincident(g43,g35)
    c: Coincident(g43,g38)
    c: Equal(g40,g41)
    c: Equal(g41,g42)
    c: Equal(g42,g43)
    c: Coincident(g28,g29)
    c: Coincident(g28,g33)
    c: Coincident(g28,g41)
    c: DistanceX(g-1,g32) = 45
    c: DistanceX(g28,g28) = 40
    c: Equal(g32,g33)
    c: Equal(g33,g34)
    c: Equal(g34,g35)
    c: Radius(g32) = 1.6
    c: Vertical(g31)
    c: Horizontal(g44)
    c: Coincident(g44,g45)
    c: Vertical(g45)
    c: Coincident(g45,g46)
    c: Horizontal(g46)
    c: Coincident(g46,g47)
    c: Vertical(g47)
    c: Coincident(g47,g48)
    c: Horizontal(g48)
    c: Coincident(g48,g49)
    c: Vertical(g49)
    c: Coincident(g49,g50)
    c: Horizontal(g50)
    c: Coincident(g50,g51)
    c: Vertical(g51)
    c: Coincident(g51,g52)
    c: Horizontal(g52)
    c: Coincident(g52,g53)
    c: Vertical(g53)
    c: Coincident(g53,g54)
    c: Horizontal(g54)
    c: Coincident(g54,g55)
    c: Coincident(g55,g44)
    c: Vertical(g55)
    c: Coincident(g56,g54)
    c: Coincident(g56,g44)
    c: Coincident(g56,g53)
    c: Coincident(g57,g45)
    c: Coincident(g57,g44)
    c: Coincident(g57,g47)
    c: Coincident(g58,g48)
    c: Coincident(g58,g47)
    c: Coincident(g58,g50)
    c: Coincident(g59,g51)
    c: Coincident(g59,g53)
    c: Coincident(g59,g50)
    c: Equal(g56,g57)
    c: Equal(g57,g58)
    c: Equal(g58,g59)
    c: PointOnObject(g44,g36)
    c: PointOnObject(g50,g38)
    c: PointOnObject(g47,g37)
    c: PointOnObject(g53,g39)
    c: Radius(g56) = 1
    c: DistanceY(g-1,g33) = 12.95
FEATURE [PartDesign::Pocket] Pocket012  label="Pocket TF001"
  BaseFeature = -> Pocket011
  Length = 3
  Length2 = 100
  Placement = pos=(0,0,0) rot=(1,0,0;1.5708rad)
  Profile = -> Sketch001002033
  Type = 0
FEATURE [PartDesign::Pocket] Pocket013  label="Pocket E-Paper001"
  BaseFeature = -> Pocket012
  Length = 3
  Length2 = 100
  Placement = pos=(0,0,0) rot=(1,0,0;1.5708rad)
  Profile = -> Sketch001002036
  Type = 0
FEATURE [PartDesign::Pocket] Pocket014  label="Pocket RP002"
  BaseFeature = -> Pocket013
  Length = 3
  Length2 = 100
  Placement = pos=(0,0,0) rot=(1,0,0;1.5708rad)
  Profile = -> Sketch001002035
  Type = 0
FEATURE [PartDesign::Pocket] Pocket015  label="Pocket Segment&Ambiente001"
  BaseFeature = -> Pocket014
  Length = 3
  Length2 = 100
  Placement = pos=(0,0,0) rot=(1,0,0;1.5708rad)
  Profile = -> Sketch001002037
  Type = 0
FEATURE [PartDesign::Pocket] Pocket016  label="Pocket Motion001"
  BaseFeature = -> Pocket015
  Length = 3
  Length2 = 100
  Placement = pos=(0,0,0) rot=(1,0,0;1.5708rad)
  Profile = -> Sketch001002038
  Type = 0
FEATURE [PartDesign::Body] Body026  label="Body Front002"
  Group = -> [Sketch001002032,Pad026,Sketch001002034,Pocket011,Sketch001002033,Sketch001002035,Sketch001002036,Sketch001002037,Sketch001002038,Pocket012,Pocket013,Pocket014,Pocket015,Pocket016]
  Origin = -> Origin034
  Tip = -> Pocket016
FEATURE [Part::Fillet] Fillet037  label="Front "
  Base = -> Body026
  Edges = 4 edges r=4: [Edge1,Edge2,Edge5,Edge8]
FEATURE [Part::Feature] Part__Feature001002002001001050001001002001002001002001002001002001002001001002001002004001001001001002001002001093  label="Screw ptc002"
  Placement = pos=(-72.5,87.5,-4.9) rot=(0,1,0;0rad)
  shape: bbox 5.6 x 5.6 x 7.4 mm, 23 faces (baked)
FEATURE [Part::Feature] Part__Feature001002002001001050001001002001002001002001002001002001002001001002001002004001001001001002001002001094  label="Screw ptc001"
  Placement = pos=(-72.5,62.5,-4.9) rot=(0,1,0;0rad)
  shape: bbox 5.6 x 5.6 x 7.4 mm, 23 faces (baked)
FEATURE [Part::Feature] Part__Feature001002002001001050001001002001002001002001002001002001002001001002001002004001001001001002001002001095  label="Screw ptc003"
  Placement = pos=(-102.5,87.5,-4.9) rot=(0,1,0;0rad)
  shape: bbox 5.6 x 5.6 x 7.4 mm, 23 faces (baked)
FEATURE [Part::Feature] Part__Feature001002002001001050001001002001002001002001002001002001002001001002001002004001001001001002001002001096  label="Screw ptc004"
  Placement = pos=(-102.5,62.5,-4.9) rot=(0,1,0;0rad)
  shape: bbox 5.6 x 5.6 x 7.4 mm, 23 faces (baked)
FEATURE [App::Part] Part021  label="ptc schrauben oben"
  Group = -> [Part__Feature001002002001001050001001002001002001002001002001002001002001001002001002004001001001001002001002001094,Part__Feature001002002001001050001001002001002001002001002001002001002001001002001002004001001001001002001002001093,Part__Feature001002002001001050001001002001002001002001002001002001002001001002001002004001001001001002001002001095,+1 more]
  Origin = -> Origin049
FEATURE [Part::Feature] Part__Feature001002002001001050001001002001002001002001002001002001002001001002001002004001001001001002001002001097  label="Screw ptc007"
  Placement = pos=(-102.5,87.5,-19.5) rot=(1,0,0;3.14159rad)
  shape: bbox 5.6 x 5.6 x 7.4 mm, 23 faces (baked)
FEATURE [Part::Feature] Part__Feature001002002001001050001001002001002001002001002001002001002001001002001002004001001001001002001002001098  label="Screw ptc005"
  Placement = pos=(-72.5,62.5,-19.5) rot=(1,0,0;3.14159rad)
  shape: bbox 5.6 x 5.6 x 7.4 mm, 23 faces (baked)
FEATURE [Part::Feature] Part__Feature001002002001001050001001002001002001002001002001002001002001001002001002004001001001001002001002001099  label="Screw ptc008"
  Placement = pos=(-102.5,62.5,-19.5) rot=(1,0,0;3.14159rad)
  shape: bbox 5.6 x 5.6 x 7.4 mm, 23 faces (baked)
FEATURE [Part::Feature] Part__Feature001002002001001050001001002001002001002001002001002001002001001002001002004001001001001002001002001100  label="Screw ptc006"
  Placement = pos=(-72.5,87.5,-19.5) rot=(1,0,0;3.14159rad)
  shape: bbox 5.6 x 5.6 x 7.4 mm, 23 faces (baked)
FEATURE [App::Part] Part022  label="ptc schrauben unten"
  Group = -> [Part__Feature001002002001001050001001002001002001002001002001002001002001001002001002004001001001001002001002001098,Part__Feature001002002001001050001001002001002001002001002001002001002001001002001002004001001001001002001002001100,Part__Feature001002002001001050001001002001002001002001002001002001002001001002001002004001001001001002001002001097,+1 more]
  Origin = -> Origin050
FEATURE [Part::Feature] Part__Feature001002002001001050001001002001002001002001002001002001002001001002001002004001001001001002001002001101  label="ptc002"
  Placement = pos=(-72.5,87.5,-16.5) rot=(0,-1,0;0rad)
  shape: bbox 6 x 6.928 x 10 mm, 22 faces (baked)
FEATURE [Part::Feature] Part__Feature001002002001001050001001002001002001002001002001002001002001001002001002004001001001001002001002001102  label="ptc004"
  Placement = pos=(-102.5,62.5,-16.5) rot=(0,-1,0;0rad)
  shape: bbox 6 x 6.928 x 10 mm, 22 faces (baked)
FEATURE [Part::Feature] Part__Feature001002002001001050001001002001002001002001002001002001002001001002001002004001001001001002001002001103  label="ptc001"
  Placement = pos=(-72.5,62.5,-16.5) rot=(0,-1,0;0rad)
  shape: bbox 6 x 6.928 x 10 mm, 22 faces (baked)
FEATURE [Part::Feature] Part__Feature001002002001001050001001002001002001002001002001002001002001001002001002004001001001001002001002001104  label="ptc003"
  Placement = pos=(-102.5,87.5,-16.5) rot=(0,-1,0;0rad)
  shape: bbox 6 x 6.928 x 10 mm, 22 faces (baked)
FEATURE [App::Part] Part023  label="ptc abstandsbolzen 10mm"
  Group = -> [Part__Feature001002002001001050001001002001002001002001002001002001002001001002001002004001001001001002001002001103,Part__Feature001002002001001050001001002001002001002001002001002001002001001002001002004001001001001002001002001101,Part__Feature001002002001001050001001002001002001002001002001002001002001001002001002004001001001001002001002001104,+1 more]
  Origin = -> Origin051
FEATURE [Sketcher::SketchObject] Sketch001002039  label="Sketch Circuit Board001"
  MapMode = 5
  sketch-geometry (36):
    g0: LineSegment StartX=2.5 StartY=15 StartZ=0 EndX=22.5 EndY=15 EndZ=0
    g1: LineSegment StartX=25 StartY=12.5 StartZ=0 EndX=25 EndY=2.5 EndZ=0
    g2: LineSegment StartX=22.5 StartY=0 StartZ=0 EndX=2.5 EndY=0 EndZ=0
    g3: LineSegment StartX=0 StartY=2.5 StartZ=0 EndX=0 EndY=12.5 EndZ=0
    g4: ArcOfCircle CenterX=2.5 CenterY=12.5 CenterZ=0 NormalX=0 NormalY=0 NormalZ=1 AngleXU=0 Radius=2.5 StartAngle=1.5708 EndAngle=3.14159
    g5: ArcOfCircle CenterX=22.5 CenterY=12.5 CenterZ=0 NormalX=0 NormalY=0 NormalZ=1 AngleXU=0 Radius=2.5 StartAngle=0 EndAngle=1.5708
    g6: ArcOfCircle CenterX=22.5 CenterY=2.5 CenterZ=0 NormalX=0 NormalY=0 NormalZ=1 AngleXU=0 Radius=2.5 StartAngle=4.71239 EndAngle=6.28319
    g7: ArcOfCircle CenterX=2.5 CenterY=2.5 CenterZ=0 NormalX=0 NormalY=0 NormalZ=1 AngleXU=0 Radius=2.5 StartAngle=3.14159 EndAngle=4.71239
    g8: Circle CenterX=2.5 CenterY=12.5 CenterZ=0 NormalX=0 NormalY=0 NormalZ=1 AngleXU=0 Radius=1.5
    g9: Circle CenterX=22.5 CenterY=12.5 CenterZ=0 NormalX=0 NormalY=0 NormalZ=1 AngleXU=0 Radius=1.5
    g10: Circle CenterX=2.5 CenterY=2.5 CenterZ=0 NormalX=0 NormalY=0 NormalZ=1 AngleXU=0 Radius=1.5
    g11: Circle CenterX=22.5 CenterY=2.5 CenterZ=0 NormalX=0 NormalY=0 NormalZ=1 AngleXU=0 Radius=1.5
    g12: LineSegment [constr] StartX=2.5 StartY=12.5 StartZ=0 EndX=22.5 EndY=12.5 EndZ=0
    g13: LineSegment [constr] StartX=22.5 StartY=12.5 StartZ=0 EndX=22.5 EndY=2.5 EndZ=0
    g14: LineSegment [constr] StartX=22.5 StartY=2.5 StartZ=0 EndX=2.5 EndY=2.5 EndZ=0
    g15: LineSegment [constr] StartX=2.5 StartY=2.5 StartZ=0 EndX=2.5 EndY=12.5 EndZ=0
    g16: LineSegment [constr] StartX=0 StartY=2.5 StartZ=0 EndX=2.5 EndY=2.5 EndZ=0
    g17: LineSegment [constr] StartX=2.5 StartY=2.5 StartZ=0 EndX=2.5 EndY=0 EndZ=0
    g18: LineSegment [constr] StartX=2.5 StartY=0 StartZ=0 EndX=0 EndY=0 EndZ=0
    g19: LineSegment [constr] StartX=0 StartY=0 StartZ=0 EndX=0 EndY=2.5 EndZ=0
    g20: LineSegment [constr] StartX=25 StartY=2.5 StartZ=0 EndX=22.5 EndY=2.5 EndZ=0
    g21: LineSegment [constr] StartX=22.5 StartY=2.5 StartZ=0 EndX=22.5 EndY=0 EndZ=0
    g22: LineSegment [constr] StartX=22.5 StartY=0 StartZ=0 EndX=25 EndY=0 EndZ=0
    g23: LineSegment [constr] StartX=25 StartY=0 StartZ=0 EndX=25 EndY=2.5 EndZ=0
    g24: LineSegment [constr] StartX=22.5 StartY=15 StartZ=0 EndX=25 EndY=15 EndZ=0
    g25: LineSegment [constr] StartX=25 StartY=15 StartZ=0 EndX=25 EndY=12.5 EndZ=0
    g26: LineSegment [constr] StartX=25 StartY=12.5 StartZ=0 EndX=22.5 EndY=12.5 EndZ=0
    g27: LineSegment [constr] StartX=22.5 StartY=12.5 StartZ=0 EndX=22.5 EndY=15 EndZ=0
    g28: LineSegment [constr] StartX=2.5 StartY=15 StartZ=0 EndX=0 EndY=15 EndZ=0
    g29: LineSegment [constr] StartX=0 StartY=15 StartZ=0 EndX=0 EndY=12.5 EndZ=0
    g30: LineSegment [constr] StartX=0 StartY=12.5 StartZ=0 EndX=2.5 EndY=12.5 EndZ=0
    g31: LineSegment [constr] StartX=2.5 StartY=12.5 StartZ=0 EndX=2.5 EndY=15 EndZ=0
    g32: LineSegment [constr] StartX=2.5 StartY=12.5 StartZ=0 EndX=0 EndY=15 EndZ=0
    g33: LineSegment [constr] StartX=22.5 StartY=12.5 StartZ=0 EndX=25 EndY=15 EndZ=0
    g34: LineSegment [constr] StartX=22.5 StartY=2.5 StartZ=0 EndX=25 EndY=0 EndZ=0
    g35: LineSegment [constr] StartX=0 StartY=0 StartZ=0 EndX=2.5 EndY=2.5 EndZ=0
  constraints (96):
    c: Horizontal(g0)
    c: Horizontal(g2)
    c: Vertical(g1)
    c: Vertical(g3)
    c: Radius(g8) = 1.5
    c: Equal(g8,g9)
    c: Equal(g9,g11)
    c: Equal(g11,g10)
    c: Coincident(g1,g5)
    c: Coincident(g0,g5)
    c: Coincident(g0,g4)
    c: Coincident(g3,g4)
    c: Coincident(g1,g6)
    c: Coincident(g2,g6)
    c: Coincident(g2,g7)
    c: Coincident(g3,g7)
    c: Coincident(g12,g13)
    c: Coincident(g13,g14)
    c: Coincident(g14,g15)
    c: Coincident(g15,g12)
    c: Horizontal(g12)
    c: Horizontal(g14)
    c: Vertical(g13)
    c: Vertical(g15)
    c: Coincident(g12,g8)
    c: Coincident(g13,g11)
    c: Coincident(g9,g12)
    c: Coincident(g10,g14)
    c: Coincident(g16,g17)
    c: Coincident(g17,g18)
    c: Coincident(g18,g19)
    c: Coincident(g19,g16)
    c: Horizontal(g16)
    c: Horizontal(g18)
    c: Vertical(g17)
    c: Vertical(g19)
    c: Coincident(g16,g3)
    c: Coincident(g17,g2)
    c: Coincident(g20,g21)
    c: Coincident(g21,g22)
    c: Coincident(g22,g23)
    c: Coincident(g23,g20)
    c: Horizontal(g20)
    c: Horizontal(g22)
    c: Vertical(g21)
    c: Vertical(g23)
    c: Coincident(g20,g1)
    c: Coincident(g21,g2)
    c: Coincident(g24,g25)
    c: Coincident(g25,g26)
    c: Coincident(g26,g27)
    c: Coincident(g27,g24)
    c: Horizontal(g24)
    c: Horizontal(g26)
    c: Vertical(g25)
    c: Vertical(g27)
    c: Coincident(g24,g0)
    c: Coincident(g25,g1)
    c: Coincident(g28,g29)
    c: Coincident(g29,g30)
    c: Coincident(g30,g31)
    c: Coincident(g31,g28)
    c: Horizontal(g28)
    c: Horizontal(g30)
    c: Vertical(g29)
    c: Vertical(g31)
    c: Coincident(g28,g0)
    c: Coincident(g29,g3)
    c: DistanceY(g27,g27) = 2.5
    c: DistanceX(g20,g20) = 2.5
    c: DistanceY(g21,g21) = 2.5
    c: DistanceX(g16,g16) = 2.5
    c: Radius(g7) = 2.5
    c: Equal(g7,g6)
    c: Equal(g6,g5)
    c: Equal(g5,g4)
    c: Coincident(g18,g-1)
    c: Coincident(g32,g8)
    c: Coincident(g32,g28)
    c: Coincident(g33,g9)
    c: Coincident(g33,g24)
    c: Coincident(g34,g11)
    c: Coincident(g34,g22)
    c: Coincident(g35,g-1)
    c: Coincident(g35,g10)
    c: Equal(g35,g34)
    c: Equal(g33,g32)
    c: DistanceX(g12,g12) = 20
    c: DistanceX(g24,g24) = 2.5
    c: DistanceX(g28,g28) = 2.5
    c: DistanceY(g29,g29) = 2.5
    c: DistanceY(g19,g19) = 2.5
    c: DistanceX(g28,g24) = 25
    c: DistanceY(g28) = 15
    c: DistanceY(g2,g10) = 2.5
    c: DistanceY(g15,g15) = 10
FEATURE [PartDesign::Pad] Pad027  label="Pad Circuit Board"
  Length = 1.6
  Length2 = 100
  Profile = -> Sketch001002039
  Refine = true
  Type = 0
FEATURE [Sketcher::SketchObject] Sketch001002040  label="Sketch Silk002"
  MapMode = 5
  Placement = pos=(0,0,-0.01) rot=(0,0,1;0rad)
  sketch-geometry (12):
    g0: Circle CenterX=2.5 CenterY=2.5 CenterZ=0 NormalX=0 NormalY=0 NormalZ=1 AngleXU=0 Radius=1.6
    g1: Circle CenterX=2.5 CenterY=2.5 CenterZ=0 NormalX=0 NormalY=0 NormalZ=1 AngleXU=0 Radius=2.4
    g2: Circle CenterX=22.5 CenterY=2.5 CenterZ=0 NormalX=0 NormalY=0 NormalZ=1 AngleXU=0 Radius=1.6
    g3: Circle CenterX=22.5 CenterY=2.5 CenterZ=0 NormalX=0 NormalY=0 NormalZ=1 AngleXU=0 Radius=2.4
    g4: Circle CenterX=22.5 CenterY=12.5 CenterZ=0 NormalX=0 NormalY=0 NormalZ=1 AngleXU=0 Radius=2.4
    g5: Circle CenterX=22.5 CenterY=12.5 CenterZ=0 NormalX=0 NormalY=0 NormalZ=1 AngleXU=0 Radius=1.6
    g6: Circle CenterX=2.5 CenterY=12.5 CenterZ=0 NormalX=0 NormalY=0 NormalZ=1 AngleXU=0 Radius=1.6
    g7: Circle CenterX=2.5 CenterY=12.5 CenterZ=0 NormalX=0 NormalY=0 NormalZ=1 AngleXU=0 Radius=2.4
    g8: LineSegment [constr] StartX=2.5 StartY=12.5 StartZ=0 EndX=22.5 EndY=12.5 EndZ=0
    g9: LineSegment [constr] StartX=22.5 StartY=12.5 StartZ=0 EndX=22.5 EndY=2.5 EndZ=0
    g10: LineSegment [constr] StartX=22.5 StartY=2.5 StartZ=0 EndX=2.5 EndY=2.5 EndZ=0
    g11: LineSegment [constr] StartX=2.5 StartY=2.5 StartZ=0 EndX=2.5 EndY=12.5 EndZ=0
  constraints (28):
    c: Coincident(g1,g0)
    c: Coincident(g2,g3)
    c: Coincident(g4,g5)
    c: Coincident(g6,g7)
    c: Coincident(g8,g9)
    c: Coincident(g9,g10)
    c: Coincident(g10,g11)
    c: Coincident(g11,g8)
    c: Horizontal(g8)
    c: Horizontal(g10)
    c: Vertical(g9)
    c: Vertical(g11)
    c: Coincident(g8,g6)
    c: Coincident(g9,g2)
    c: DistanceX(g8,g8) = 20
    c: DistanceY(g11,g11) = 10
    c: Coincident(g4,g8)
    c: Coincident(g0,g10)
    c: DistanceX(g0) = 2.5
    c: DistanceY(g0) = 2.5
    c: Radius(g0) = 1.6
    c: Radius(g3) = 2.4
    c: Equal(g0,g2)
    c: Equal(g2,g5)
    c: Equal(g5,g6)
    c: Equal(g1,g3)
    c: Equal(g3,g4)
    c: Equal(g4,g7)
FEATURE [Part::Feature] Part__Feature001002002001001050001001002001002001002001002001002001002001001002001002004001001001001002001002001060  label="Master_Brick"
  Placement = pos=(-180.9,23,0) rot=(0.707107,0,0.707107;3.14159rad)
  shape: bbox 15.7 x 40.87 x 40 mm, 8354 faces (baked)
FEATURE [Part::Feature] Part__Feature001002002001001050001001002001002001002001002001002001002001001002001002004001001001001002001002001062  label="Ethernet_Buchse"
  shape: bbox 26.47 x 22.26 x 12.3 mm, 1543 faces, 3 solids (baked)
FEATURE [PartDesign::Pad] Pad028  label="Pad Silk"
  Length = 1.62
  Length2 = 100
  Placement = pos=(0,0,-0.01) rot=(0,0,1;0rad)
  Profile = -> Sketch001002040
  Refine = true
  Type = 0
FEATURE [Part::Feature] Part__Feature001002002001001050001001002001002001002001002001002001002001001002001002004001001001001002001002001061  label="Fusion001"
  shape: bbox 40 x 40 x 15.7 mm, 6790 faces (baked)
FEATURE [App::Part] Part012  label="Ethernet"
  Group = -> [Part__Feature001002002001001050001001002001002001002001002001002001002001001002001002004001001001001002001002001061,Part__Feature001002002001001050001001002001002001002001002001002001002001001002001002004001001001001002001002001062]
  License = CC BY 3.0
  LicenseURL = http://creativecommons.org/licenses/by/3.0/
  Origin = -> Origin039
  Placement = pos=(-168.6,3,20) rot=(0,-1,0;4.71239rad)
FEATURE [Part::Feature] Part__Feature001002002001001050001001002001002001002001002001002001002001001002001002004001001001001002001002001068  label="PTC001"
  Placement = pos=(-70,60,-6.5) rot=(0,0,1;1.5708rad)
  shape: bbox 35 x 30 x 15 mm, 1992 faces (baked)
FEATURE [Part::Feature] Part__Feature001002002001001050001001002001002001002001002001002001002001001002001002004001001001001002001002001064  label="PinsArrayLR"
  shape: bbox 2.6 x 1.75 x 0.1125 mm, 48 faces, 8 solids (baked)
FEATURE [Part::Feature] Part__Feature017  label="ThermalPin"
  Placement = pos=(-0.55,-0.9,0) rot=(0,0,1;0rad)
  shape: bbox 1.1 x 1.8 x 0.1125 mm, 6 faces (baked)
FEATURE [Part::Feature] Part__Feature001002002001001050001001002001002001002001002001002001002001001002001002004001001001001002001002001067  label="Ambiente_Light_3.0_Board"
  Placement = pos=(118.85,6.4,-4.55) rot=(0,0.707107,-0.707107;3.14159rad)
  shape: bbox 25 x 5.71 x 15 mm, 1278 faces (baked)
FEATURE [Part::Feature] Part__Feature001002002001001050001001002001002001002001002001002001002001001002001002004001001001001002001002001063  label="Humidity_2.0"
  Placement = pos=(-99,119,-12.5) rot=(0.57735,0.57735,0.57735;4.18879rad)
  shape: bbox 15 x 5.71 x 25 mm, 1254 faces (baked)
FEATURE [Part::Feature] Part__Feature018  label="Body005"
  shape: bbox 2.5 x 2.5 x 0.85 mm, 8 faces (baked)
FEATURE [App::Part] ASSEMBLY  label="SHT31-DIS-B"
  Group = -> [Part__Feature018,Part__Feature017,Part__Feature001002002001001050001001002001002001002001002001002001002001001002001002004001001001001002001002001064]
  License = CC BY 3.0
  LicenseURL = http://creativecommons.org/licenses/by/3.0/
  Origin = -> Origin038
  Placement = pos=(6,8,1.6) rot=(0,0,1;1.5708rad)
FEATURE [Part::Feature] Part__Feature001002002001001050001001002001002001002001002001002001002001001002001002004001001001001002001002001065  label="7Pin_Stecker001"
  Placement = pos=(12.5,2,1.6) rot=(0,0,1;0rad)
  shape: bbox 12 x 4.98 x 4.1 mm, 457 faces (baked)
FEATURE [Part::Feature] Part__Feature001002002001001050001001002001002001002001002001002001002001001002001002004001001001001002001002001066  label="XMC_1100_Pad"
  Placement = pos=(15.6,11,1.6) rot=(0,0,1;0.785398rad)
  shape: bbox 5.657 x 5.657 x 0.901 mm, 823 faces (baked)
FEATURE [App::Part] Part011  label="Temperatur 2.0"
  Group = -> [Sketch001002039,Pad027,Sketch001002040,Pad028,Part__Feature001002002001001050001001002001002001002001002001002001002001001002001002004001001001001002001002001065,Part__Feature001002002001001050001001002001002001002001002001002001002001001002001002004001001001001002001002001066,ASSEMBLY]
  License = CC BY 3.0
  LicenseURL = http://creativecommons.org/licenses/by/3.0/
  Origin = -> Origin040
  Placement = pos=(-144,119,12.5) rot=(-0.57735,0.57735,0.57735;2.0944rad)
FEATURE [Part::Feature] Part__Feature001002002001001050001001002001002001002001002001002001002001001002001002004001001001001002001002001129  label="Motion_Detector_V2"
  Placement = pos=(87.5,1.6,-9.55) rot=(0.57735,-0.57735,0.57735;2.0944rad)
  shape: bbox 45 x 20.58 x 25 mm, 1382 faces (baked)
FEATURE [Sketcher::SketchObject] Sketch001002042  label="Cut008"
  Placement = pos=(0,0,0.8) rot=(0,0,1;0rad)
  sketch-geometry (27):
    g0: LineSegment StartX=-16 StartY=38 StartZ=0 EndX=16 EndY=38 EndZ=0
    g1: LineSegment StartX=16 StartY=38 StartZ=0 EndX=16 EndY=-35 EndZ=0
    g2: LineSegment [constr] StartX=16 StartY=-35 StartZ=0 EndX=-16 EndY=-35 EndZ=0
    g3: LineSegment StartX=-16 StartY=-35 StartZ=0 EndX=-16 EndY=38 EndZ=0
    g4: LineSegment StartX=-16 StartY=-35 StartZ=0 EndX=-11 EndY=-35 EndZ=0
    g5: LineSegment StartX=-11 StartY=-35 StartZ=0 EndX=-11 EndY=-33 EndZ=0
    g6: LineSegment [constr] StartX=-11 StartY=-33 StartZ=0 EndX=-10 EndY=-33 EndZ=0
    g7: LineSegment [constr] StartX=-10 StartY=-33 StartZ=0 EndX=-10 EndY=-32 EndZ=0
    g8: LineSegment StartX=-10 StartY=-32 StartZ=0 EndX=10 EndY=-32 EndZ=0
    g9: LineSegment [constr] StartX=10 StartY=-32 StartZ=0 EndX=10 EndY=-33 EndZ=0
    g10: LineSegment [constr] StartX=10 StartY=-33 StartZ=0 EndX=11 EndY=-33 EndZ=0
    g11: LineSegment StartX=11 StartY=-33 StartZ=0 EndX=11 EndY=-35 EndZ=0
    g12: LineSegment StartX=11 StartY=-35 StartZ=0 EndX=16 EndY=-35 EndZ=0
    g13: ArcOfCircle CenterX=-10 CenterY=-33 CenterZ=0 NormalX=0 NormalY=0 NormalZ=1 AngleXU=0 Radius=1 StartAngle=1.5708 EndAngle=3.14159
    g14: ArcOfCircle CenterX=10 CenterY=-33 CenterZ=0 NormalX=0 NormalY=0 NormalZ=1 AngleXU=0 Radius=1 StartAngle=0 EndAngle=1.5708
    g15: Circle CenterX=-13.5 CenterY=-33 CenterZ=0 NormalX=0 NormalY=0 NormalZ=1 AngleXU=0 Radius=1
    g16: Circle CenterX=13.5 CenterY=-33 CenterZ=0 NormalX=0 NormalY=0 NormalZ=1 AngleXU=0 Radius=1
    g17: LineSegment StartX=-15 StartY=37 StartZ=0 EndX=15 EndY=37 EndZ=0
    g18: LineSegment StartX=15 StartY=37 StartZ=0 EndX=15 EndY=-31 EndZ=0
    g19: LineSegment StartX=15 StartY=-31 StartZ=0 EndX=-15 EndY=-31 EndZ=0
    g20: LineSegment StartX=-15 StartY=-31 StartZ=0 EndX=-15 EndY=37 EndZ=0
    g21: LineSegment [constr] StartX=-16 StartY=38 StartZ=0 EndX=-15 EndY=37 EndZ=0
    g22: LineSegment [constr] StartX=15 StartY=37 StartZ=0 EndX=16 EndY=38 EndZ=0
    g23: LineSegment [constr] StartX=-16 StartY=-35 StartZ=0 EndX=-13.5 EndY=-33 EndZ=0
    g24: LineSegment [constr] StartX=-13.5 StartY=-33 StartZ=0 EndX=-11 EndY=-35 EndZ=0
    g25: LineSegment [constr] StartX=13.5 StartY=-33 StartZ=0 EndX=11 EndY=-35 EndZ=0
    g26: LineSegment [constr] StartX=13.5 StartY=-33 StartZ=0 EndX=16 EndY=-35 EndZ=0
  constraints (72):
    c: Coincident(g0,g1)
    c: Coincident(g1,g2)
    c: Coincident(g2,g3)
    c: Coincident(g3,g0)
    c: Horizontal(g0)
    c: Horizontal(g2)
    c: Vertical(g1)
    c: Vertical(g3)
    c: Coincident(g2,g4)
    c: Horizontal(g4)
    c: Coincident(g4,g5)
    c: Vertical(g5)
    c: Coincident(g5,g6)
    c: Horizontal(g6)
    c: Coincident(g6,g7)
    c: Vertical(g7)
    c: Coincident(g7,g8)
    c: Horizontal(g8)
    c: Coincident(g8,g9)
    c: Vertical(g9)
    c: Coincident(g9,g10)
    c: Horizontal(g10)
    c: Coincident(g10,g11)
    c: Vertical(g11)
    c: Coincident(g11,g12)
    c: Coincident(g12,g1)
    c: Horizontal(g12)
    c: Coincident(g13,g6)
    c: Coincident(g13,g7)
    c: Coincident(g13,g5)
    c: Coincident(g14,g9)
    c: Coincident(g14,g8)
    c: Coincident(g14,g10)
    c: Equal(g14,g13)
    c: Equal(g4,g12)
    c: Coincident(g17,g18)
    c: Coincident(g18,g19)
    c: Coincident(g19,g20)
    c: Coincident(g20,g17)
    c: Horizontal(g17)
    c: Horizontal(g19)
    c: Vertical(g18)
    c: Vertical(g20)
    c: Coincident(g21,g0)
    c: Coincident(g21,g17)
    c: Coincident(g22,g17)
    c: Coincident(g22,g0)
    c: Equal(g21,g22)
    c: DistanceY(g17,g0) = 1
    c: DistanceX(g17,g0) = 1
    c: DistanceY(g18,g18) = 68
    c: DistanceY(g8,g18) = 1
    c: DistanceY(g3,g3) = 73
    c: DistanceX(g4,g4) = 5
    c: Coincident(g23,g2)
    c: Coincident(g23,g15)
    c: Coincident(g24,g15)
    c: Coincident(g24,g4)
    c: Coincident(g25,g16)
    c: Coincident(g25,g11)
    c: Coincident(g26,g16)
    c: Coincident(g26,g1)
    c: Equal(g23,g24)
    c: Equal(g24,g25)
    c: Equal(g25,g26)
    c: Radius(g13) = 1
    c: Equal(g15,g16)
    c: Radius(g15) = 1
    c: DistanceY(g4,g15) = 2
    c: DistanceX(g0,g0) = 32
    c: DistanceY(g-1,g17) = 37
    c: Symmetric(g17,g17,g-2)
FEATURE [Sketcher::SketchObject] Sketch001002043
  Placement = pos=(0,0,0.8) rot=(0,0,1;0rad)
  sketch-geometry (18):
    g0: LineSegment StartX=-18.5 StartY=-39.5 StartZ=0 EndX=18.5 EndY=-39.5 EndZ=0
    g1: LineSegment StartX=18.5 StartY=-39.5 StartZ=0 EndX=18.5 EndY=-36.5 EndZ=0
    g2: LineSegment StartX=18.5 StartY=-36.5 StartZ=0 EndX=10.5 EndY=-36.5 EndZ=0
    g3: LineSegment StartX=10.5 StartY=-36.5 StartZ=0 EndX=10.5 EndY=-33.5 EndZ=0
    g4: LineSegment [constr] StartX=10.5 StartY=-33.5 StartZ=0 EndX=9.5 EndY=-33.5 EndZ=0
    g5: LineSegment [constr] StartX=9.5 StartY=-33.5 StartZ=0 EndX=9.5 EndY=-32.5 EndZ=0
    g6: LineSegment StartX=9.5 StartY=-32.5 StartZ=0 EndX=-9.5 EndY=-32.5 EndZ=0
    g7: LineSegment StartX=-9.5 StartY=-32.5 StartZ=0 EndX=-10.5 EndY=-36.5 EndZ=0
    g8: LineSegment StartX=-10.5 StartY=-36.5 StartZ=0 EndX=-18.5 EndY=-36.5 EndZ=0
    g9: LineSegment StartX=-18.5 StartY=-36.5 StartZ=0 EndX=-18.5 EndY=-39.5 EndZ=0
    g10: LineSegment StartX=-4.75 StartY=-36.5 StartZ=0 EndX=4.75 EndY=-36.5 EndZ=0
    g11: LineSegment StartX=4.75 StartY=-36.5 StartZ=0 EndX=4.75 EndY=-37.5 EndZ=0
    g12: LineSegment StartX=4.75 StartY=-37.5 StartZ=0 EndX=-4.75 EndY=-37.5 EndZ=0
    g13: LineSegment StartX=-4.75 StartY=-37.5 StartZ=0 EndX=-4.75 EndY=-36.5 EndZ=0
    g14: ArcOfCircle CenterX=9.5 CenterY=-33.5 CenterZ=0 NormalX=0 NormalY=0 NormalZ=1 AngleXU=0 Radius=1 StartAngle=0 EndAngle=1.5708
    g15: LineSegment [constr] StartX=-18.5 StartY=-39.5 StartZ=0 EndX=-18.5 EndY=39.5 EndZ=0
    g16: LineSegment [constr] StartX=-18.5 StartY=39.5 StartZ=0 EndX=18.5 EndY=39.5 EndZ=0
    g17: LineSegment [constr] StartX=18.5 StartY=39.5 StartZ=0 EndX=18.5 EndY=-39.5 EndZ=0
  constraints (51):
    c: Horizontal(g0)
    c: Coincident(g0,g1)
    c: Vertical(g1)
    c: Coincident(g1,g2)
    c: Horizontal(g2)
    c: Coincident(g2,g3)
    c: Vertical(g3)
    c: Coincident(g3,g4)
    c: Horizontal(g4)
    c: Coincident(g4,g5)
    c: Vertical(g5)
    c: Coincident(g5,g6)
    c: Horizontal(g6)
    c: Coincident(g6,g7)
    c: Coincident(g7,g8)
    c: Horizontal(g8)
    c: Coincident(g8,g9)
    c: Coincident(g9,g0)
    c: Vertical(g9)
    c: Coincident(g10,g11)
    c: Coincident(g11,g12)
    c: Coincident(g12,g13)
    c: Coincident(g13,g10)
    c: Horizontal(g10)
    c: Horizontal(g12)
    c: Vertical(g11)
    c: Vertical(g13)
    c: Equal(g9,g1)
    c: Coincident(g14,g4)
    c: Coincident(g14,g5)
    c: Coincident(g14,g3)
    c: DistanceY(g9,g9) = 3
    c: Coincident(g0,g15)
    c: Vertical(g15)
    c: Coincident(g15,g16)
    c: Horizontal(g16)
    c: Coincident(g16,g17)
    c: Coincident(g17,g0)
    c: Vertical(g17)
    c: DistanceY(g17,g17) = 79
    c: DistanceX(g16,g16) = 37
    c: Symmetric(g0,g15,g-1)
    c: DistanceX(g8,g8) = 8
    c: Equal(g8,g2)
    c: DistanceY(g7,g6) = 4
    c: DistanceX(g6,g6) = 19
    c: Radius(g14) = 1
    c: DistanceX(g10,g10) = 9.5
    c: DistanceY(g13,g13) = 1
    c: Symmetric(g12,g11,g-2)
    c: DistanceY(g0,g12) = 2
FEATURE [Sketcher::SketchObject] Sketch001002044
  Placement = pos=(0,0,0.8) rot=(0,0,1;0rad)
  sketch-geometry (27):
    g0: LineSegment StartX=-16 StartY=38 StartZ=0 EndX=16 EndY=38 EndZ=0
    g1: LineSegment StartX=16 StartY=38 StartZ=0 EndX=16 EndY=-35 EndZ=0
    g2: LineSegment [constr] StartX=16 StartY=-35 StartZ=0 EndX=-16 EndY=-35 EndZ=0
    g3: LineSegment StartX=-16 StartY=-35 StartZ=0 EndX=-16 EndY=38 EndZ=0
    g4: LineSegment StartX=-16 StartY=-35 StartZ=0 EndX=-11 EndY=-35 EndZ=0
    g5: LineSegment StartX=-11 StartY=-35 StartZ=0 EndX=-11 EndY=-33 EndZ=0
    g6: LineSegment [constr] StartX=-11 StartY=-33 StartZ=0 EndX=-10 EndY=-33 EndZ=0
    g7: LineSegment [constr] StartX=-10 StartY=-33 StartZ=0 EndX=-10 EndY=-32 EndZ=0
    g8: LineSegment StartX=-10 StartY=-32 StartZ=0 EndX=10 EndY=-32 EndZ=0
    g9: LineSegment [constr] StartX=10 StartY=-32 StartZ=0 EndX=10 EndY=-33 EndZ=0
    g10: LineSegment [constr] StartX=10 StartY=-33 StartZ=0 EndX=11 EndY=-33 EndZ=0
    g11: LineSegment StartX=11 StartY=-33 StartZ=0 EndX=11 EndY=-35 EndZ=0
    g12: LineSegment StartX=11 StartY=-35 StartZ=0 EndX=16 EndY=-35 EndZ=0
    g13: ArcOfCircle CenterX=-10 CenterY=-33 CenterZ=0 NormalX=0 NormalY=0 NormalZ=1 AngleXU=0 Radius=1 StartAngle=1.5708 EndAngle=3.14159
    g14: ArcOfCircle CenterX=10 CenterY=-33 CenterZ=0 NormalX=0 NormalY=0 NormalZ=1 AngleXU=0 Radius=1 StartAngle=0 EndAngle=1.5708
    g15: Circle CenterX=-13.5 CenterY=-33 CenterZ=0 NormalX=0 NormalY=0 NormalZ=1 AngleXU=0 Radius=1
    g16: Circle CenterX=13.5 CenterY=-33 CenterZ=0 NormalX=0 NormalY=0 NormalZ=1 AngleXU=0 Radius=1
    g17: LineSegment StartX=-15 StartY=37 StartZ=0 EndX=15 EndY=37 EndZ=0
    g18: LineSegment StartX=15 StartY=37 StartZ=0 EndX=15 EndY=-31 EndZ=0
    g19: LineSegment StartX=15 StartY=-31 StartZ=0 EndX=-15 EndY=-31 EndZ=0
    g20: LineSegment StartX=-15 StartY=-31 StartZ=0 EndX=-15 EndY=37 EndZ=0
    g21: LineSegment [constr] StartX=-16 StartY=38 StartZ=0 EndX=-15 EndY=37 EndZ=0
    g22: LineSegment [constr] StartX=15 StartY=37 StartZ=0 EndX=16 EndY=38 EndZ=0
    g23: LineSegment [constr] StartX=-16 StartY=-35 StartZ=0 EndX=-13.5 EndY=-33 EndZ=0
    g24: LineSegment [constr] StartX=-13.5 StartY=-33 StartZ=0 EndX=-11 EndY=-35 EndZ=0
    g25: LineSegment [constr] StartX=13.5 StartY=-33 StartZ=0 EndX=11 EndY=-35 EndZ=0
    g26: LineSegment [constr] StartX=13.5 StartY=-33 StartZ=0 EndX=16 EndY=-35 EndZ=0
  constraints (72):
    c: Coincident(g0,g1)
    c: Coincident(g1,g2)
    c: Coincident(g2,g3)
    c: Coincident(g3,g0)
    c: Horizontal(g0)
    c: Horizontal(g2)
    c: Vertical(g1)
    c: Vertical(g3)
    c: Coincident(g2,g4)
    c: Horizontal(g4)
    c: Coincident(g4,g5)
    c: Vertical(g5)
    c: Coincident(g5,g6)
    c: Horizontal(g6)
    c: Coincident(g6,g7)
    c: Vertical(g7)
    c: Coincident(g7,g8)
    c: Horizontal(g8)
    c: Coincident(g8,g9)
    c: Vertical(g9)
    c: Coincident(g9,g10)
    c: Horizontal(g10)
    c: Coincident(g10,g11)
    c: Vertical(g11)
    c: Coincident(g11,g12)
    c: Coincident(g12,g1)
    c: Horizontal(g12)
    c: Coincident(g13,g6)
    c: Coincident(g13,g7)
    c: Coincident(g13,g5)
    c: Coincident(g14,g9)
    c: Coincident(g14,g8)
    c: Coincident(g14,g10)
    c: Equal(g14,g13)
    c: Equal(g4,g12)
    c: Coincident(g17,g18)
    c: Coincident(g18,g19)
    c: Coincident(g19,g20)
    c: Coincident(g20,g17)
    c: Horizontal(g17)
    c: Horizontal(g19)
    c: Vertical(g18)
    c: Vertical(g20)
    c: Coincident(g21,g0)
    c: Coincident(g21,g17)
    c: Coincident(g22,g17)
    c: Coincident(g22,g0)
    c: Equal(g21,g22)
    c: DistanceY(g17,g0) = 1
    c: DistanceX(g17,g0) = 1
    c: DistanceY(g18,g18) = 68
    c: DistanceY(g8,g18) = 1
    c: DistanceY(g3,g3) = 73
    c: DistanceX(g4,g4) = 5
    c: Coincident(g23,g2)
    c: Coincident(g23,g15)
    c: Coincident(g24,g15)
    c: Coincident(g24,g4)
    c: Coincident(g25,g16)
    c: Coincident(g25,g11)
    c: Coincident(g26,g16)
    c: Coincident(g26,g1)
    c: Equal(g23,g24)
    c: Equal(g24,g25)
    c: Equal(g25,g26)
    c: Radius(g13) = 1
    c: Equal(g15,g16)
    c: Radius(g15) = 1
    c: DistanceY(g4,g15) = 2
    c: DistanceX(g0,g0) = 32
    c: DistanceY(g-1,g17) = 37
    c: Symmetric(g17,g17,g-2)
FEATURE [Sketcher::SketchObject] Sketch001002045  label="Sketch Silk003"
  MapMode = 5
  Placement = pos=(0,0,-0.01) rot=(0,0,1;0rad)
  sketch-geometry (16):
    g0: Circle CenterX=2.5 CenterY=2.5 CenterZ=0 NormalX=0 NormalY=0 NormalZ=1 AngleXU=0 Radius=1.6
    g1: Circle [constr] CenterX=2.5 CenterY=2.5 CenterZ=0 NormalX=0 NormalY=0 NormalZ=1 AngleXU=0 Radius=2.4
    g2: Circle CenterX=37.5 CenterY=2.5 CenterZ=0 NormalX=0 NormalY=0 NormalZ=1 AngleXU=0 Radius=1.6
    g3: Circle [constr] CenterX=37.5 CenterY=2.5 CenterZ=0 NormalX=0 NormalY=0 NormalZ=1 AngleXU=0 Radius=2.4
    g4: Circle [constr] CenterX=37.5 CenterY=92.5 CenterZ=0 NormalX=0 NormalY=0 NormalZ=1 AngleXU=0 Radius=2.4
    g5: Circle CenterX=37.5 CenterY=92.5 CenterZ=0 NormalX=0 NormalY=0 NormalZ=1 AngleXU=0 Radius=1.6
    g6: Circle CenterX=2.5 CenterY=92.5 CenterZ=0 NormalX=0 NormalY=0 NormalZ=1 AngleXU=0 Radius=1.6
    g7: Circle [constr] CenterX=2.5 CenterY=92.5 CenterZ=0 NormalX=0 NormalY=0 NormalZ=1 AngleXU=0 Radius=2.4
    g8: LineSegment [constr] StartX=2.5 StartY=92.5 StartZ=0 EndX=37.5 EndY=92.5 EndZ=0
    g9: LineSegment [constr] StartX=37.5 StartY=92.5 StartZ=0 EndX=37.5 EndY=2.5 EndZ=0
    g10: LineSegment [constr] StartX=37.5 StartY=2.5 StartZ=0 EndX=2.5 EndY=2.5 EndZ=0
    g11: LineSegment [constr] StartX=2.5 StartY=2.5 StartZ=0 EndX=2.5 EndY=92.5 EndZ=0
    g12: LineSegment StartX=-0.5 StartY=95.5 StartZ=0 EndX=40.5 EndY=95.5 EndZ=0
    g13: LineSegment StartX=40.5 StartY=95.5 StartZ=0 EndX=40.5 EndY=-0.5 EndZ=0
    g14: LineSegment StartX=40.5 StartY=-0.5 StartZ=0 EndX=-0.5 EndY=-0.5 EndZ=0
    g15: LineSegment StartX=-0.5 StartY=-0.5 StartZ=0 EndX=-0.5 EndY=95.5 EndZ=0
  constraints (40):
    c: Coincident(g1,g0)
    c: Coincident(g2,g3)
    c: Coincident(g4,g5)
    c: Coincident(g6,g7)
    c: Coincident(g8,g9)
    c: Coincident(g9,g10)
    c: Coincident(g10,g11)
    c: Coincident(g11,g8)
    c: Horizontal(g8)
    c: Horizontal(g10)
    c: Vertical(g9)
    c: Vertical(g11)
    c: Coincident(g8,g6)
    c: Coincident(g9,g2)
    c: DistanceX(g8,g8) = 35
    c: DistanceY(g11,g11) = 90
    c: Coincident(g4,g8)
    c: Coincident(g0,g10)
    c: DistanceX(g0) = 2.5
    c: DistanceY(g0) = 2.5
    c: Radius(g0) = 1.6
    c: Radius(g3) = 2.4
    c: Equal(g0,g2)
    c: Equal(g2,g5)
    c: Equal(g5,g6)
    c: Equal(g1,g3)
    c: Equal(g3,g4)
    c: Equal(g4,g7)
    c: Coincident(g12,g13)
    c: Coincident(g13,g14)
    c: Coincident(g14,g15)
    c: Coincident(g15,g12)
    c: Horizontal(g12)
    c: Horizontal(g14)
    c: Vertical(g13)
    c: Vertical(g15)
    c: DistanceX(g12,g6) = 3
    c: DistanceY(g6,g12) = 3
    c: DistanceY(g13,g2) = 3
    c: DistanceX(g2,g13) = 3
FEATURE [Sketcher::SketchObject] Sketch001002046
  sketch-geometry (4):
    g0: LineSegment StartX=-18.5 StartY=39.5 StartZ=0 EndX=18.5 EndY=39.5 EndZ=0
    g1: LineSegment StartX=18.5 StartY=39.5 StartZ=0 EndX=18.5 EndY=-39.5 EndZ=0
    g2: LineSegment StartX=18.5 StartY=-39.5 StartZ=0 EndX=-18.5 EndY=-39.5 EndZ=0
    g3: LineSegment StartX=-18.5 StartY=-39.5 StartZ=0 EndX=-18.5 EndY=39.5 EndZ=0
  constraints (11):
    c: Coincident(g0,g1)
    c: Coincident(g1,g2)
    c: Coincident(g2,g3)
    c: Coincident(g3,g0)
    c: Horizontal(g0)
    c: Horizontal(g2)
    c: Vertical(g1)
    c: Vertical(g3)
    c: DistanceY(g3,g3) = 79
    c: DistanceX(g0,g0) = 37
    c: Symmetric(g0,g1,g-1)
FEATURE [PartDesign::Pad] Pad030
  Length = 0.45
  Length2 = 100
  Placement = pos=(0,0,0.8) rot=(0,0,1;0rad)
  Profile = -> Sketch001002044
  Refine = true
  Type = 0
FEATURE [Sketcher::SketchObject] Sketch001002047  label="Sketch Silk004"
  MapMode = 5
  Placement = pos=(0,0,-0.01) rot=(0,0,1;0rad)
  sketch-geometry (16):
    g0: Circle [constr] CenterX=2.5 CenterY=2.5 CenterZ=0 NormalX=0 NormalY=0 NormalZ=1 AngleXU=0 Radius=1.6
    g1: Circle CenterX=2.5 CenterY=2.5 CenterZ=0 NormalX=0 NormalY=0 NormalZ=1 AngleXU=0 Radius=2.4
    g2: Circle [constr] CenterX=37.5 CenterY=2.5 CenterZ=0 NormalX=0 NormalY=0 NormalZ=1 AngleXU=0 Radius=1.6
    g3: Circle CenterX=37.5 CenterY=2.5 CenterZ=0 NormalX=0 NormalY=0 NormalZ=1 AngleXU=0 Radius=2.4
    g4: Circle CenterX=37.5 CenterY=92.5 CenterZ=0 NormalX=0 NormalY=0 NormalZ=1 AngleXU=0 Radius=2.4
    g5: Circle [constr] CenterX=37.5 CenterY=92.5 CenterZ=0 NormalX=0 NormalY=0 NormalZ=1 AngleXU=0 Radius=1.6
    g6: Circle [constr] CenterX=2.5 CenterY=92.5 CenterZ=0 NormalX=0 NormalY=0 NormalZ=1 AngleXU=0 Radius=1.6
    g7: Circle CenterX=2.5 CenterY=92.5 CenterZ=0 NormalX=0 NormalY=0 NormalZ=1 AngleXU=0 Radius=2.4
    g8: LineSegment [constr] StartX=2.5 StartY=92.5 StartZ=0 EndX=37.5 EndY=92.5 EndZ=0
    g9: LineSegment [constr] StartX=37.5 StartY=92.5 StartZ=0 EndX=37.5 EndY=2.5 EndZ=0
    g10: LineSegment [constr] StartX=37.5 StartY=2.5 StartZ=0 EndX=2.5 EndY=2.5 EndZ=0
    g11: LineSegment [constr] StartX=2.5 StartY=2.5 StartZ=0 EndX=2.5 EndY=92.5 EndZ=0
    g12: LineSegment StartX=-0.5 StartY=95.5 StartZ=0 EndX=40.5 EndY=95.5 EndZ=0
    g13: LineSegment StartX=40.5 StartY=95.5 StartZ=0 EndX=40.5 EndY=-0.5 EndZ=0
    g14: LineSegment StartX=40.5 StartY=-0.5 StartZ=0 EndX=-0.5 EndY=-0.5 EndZ=0
    g15: LineSegment StartX=-0.5 StartY=-0.5 StartZ=0 EndX=-0.5 EndY=95.5 EndZ=0
  constraints (40):
    c: Coincident(g1,g0)
    c: Coincident(g2,g3)
    c: Coincident(g4,g5)
    c: Coincident(g6,g7)
    c: Coincident(g8,g9)
    c: Coincident(g9,g10)
    c: Coincident(g10,g11)
    c: Coincident(g11,g8)
    c: Horizontal(g8)
    c: Horizontal(g10)
    c: Vertical(g9)
    c: Vertical(g11)
    c: Coincident(g8,g6)
    c: Coincident(g9,g2)
    c: DistanceX(g8,g8) = 35
    c: DistanceY(g11,g11) = 90
    c: Coincident(g4,g8)
    c: Coincident(g0,g10)
    c: DistanceX(g0) = 2.5
    c: DistanceY(g0) = 2.5
    c: Radius(g0) = 1.6
    c: Radius(g3) = 2.4
    c: Equal(g0,g2)
    c: Equal(g2,g5)
    c: Equal(g5,g6)
    c: Equal(g1,g3)
    c: Equal(g3,g4)
    c: Equal(g4,g7)
    c: Coincident(g12,g13)
    c: Coincident(g13,g14)
    c: Coincident(g14,g15)
    c: Coincident(g15,g12)
    c: Horizontal(g12)
    c: Horizontal(g14)
    c: Vertical(g13)
    c: Vertical(g15)
    c: DistanceX(g12,g6) = 3
    c: DistanceY(g6,g12) = 3
    c: DistanceY(g13,g2) = 3
    c: DistanceX(g2,g13) = 3
FEATURE [PartDesign::Pad] Pad031
  Length = 0.45
  Length2 = 100
  Placement = pos=(0,0,0.8) rot=(0,0,1;0rad)
  Profile = -> Sketch001002043
  Refine = true
  Type = 0
FEATURE [Sketcher::SketchObject] Sketch001002048  label="Sketch Circuit Board002"
  MapMode = 5
  sketch-geometry (53):
    g0: LineSegment [constr] StartX=2.5 StartY=95 StartZ=0 EndX=37.5 EndY=95 EndZ=0
    g1: LineSegment StartX=40 StartY=92.5 StartZ=0 EndX=40 EndY=2.5 EndZ=0
    g2: LineSegment StartX=37.5 StartY=0 StartZ=0 EndX=2.5 EndY=0 EndZ=0
    g3: LineSegment StartX=0 StartY=2.5 StartZ=0 EndX=0 EndY=92.5 EndZ=0
    g4: ArcOfCircle CenterX=2.5 CenterY=92.5 CenterZ=0 NormalX=0 NormalY=0 NormalZ=1 AngleXU=0 Radius=2.5 StartAngle=1.5708 EndAngle=3.14159
    g5: ArcOfCircle CenterX=37.5 CenterY=92.5 CenterZ=0 NormalX=0 NormalY=0 NormalZ=1 AngleXU=0 Radius=2.5 StartAngle=0 EndAngle=1.5708
    g6: ArcOfCircle CenterX=37.5 CenterY=2.5 CenterZ=0 NormalX=0 NormalY=0 NormalZ=1 AngleXU=0 Radius=2.5 StartAngle=4.71239 EndAngle=6.28319
    g7: ArcOfCircle CenterX=2.5 CenterY=2.5 CenterZ=0 NormalX=0 NormalY=0 NormalZ=1 AngleXU=0 Radius=2.5 StartAngle=3.14159 EndAngle=4.71239
    g8: Circle CenterX=2.5 CenterY=92.5 CenterZ=0 NormalX=0 NormalY=0 NormalZ=1 AngleXU=0 Radius=1.5
    g9: Circle CenterX=37.5 CenterY=92.5 CenterZ=0 NormalX=0 NormalY=0 NormalZ=1 AngleXU=0 Radius=1.5
    g10: Circle CenterX=2.5 CenterY=2.5 CenterZ=0 NormalX=0 NormalY=0 NormalZ=1 AngleXU=0 Radius=1.5
    g11: Circle CenterX=37.5 CenterY=2.5 CenterZ=0 NormalX=0 NormalY=0 NormalZ=1 AngleXU=0 Radius=1.5
    g12: LineSegment [constr] StartX=2.5 StartY=92.5 StartZ=0 EndX=37.5 EndY=92.5 EndZ=0
    g13: LineSegment [constr] StartX=37.5 StartY=92.5 StartZ=0 EndX=37.5 EndY=2.5 EndZ=0
    g14: LineSegment [constr] StartX=37.5 StartY=2.5 StartZ=0 EndX=2.5 EndY=2.5 EndZ=0
    g15: LineSegment [constr] StartX=2.5 StartY=2.5 StartZ=0 EndX=2.5 EndY=92.5 EndZ=0
    g16: LineSegment [constr] StartX=0 StartY=2.5 StartZ=0 EndX=2.5 EndY=2.5 EndZ=0
    g17: LineSegment [constr] StartX=2.5 StartY=2.5 StartZ=0 EndX=2.5 EndY=0 EndZ=0
    g18: LineSegment [constr] StartX=2.5 StartY=0 StartZ=0 EndX=0 EndY=0 EndZ=0
    g19: LineSegment [constr] StartX=0 StartY=0 StartZ=0 EndX=0 EndY=2.5 EndZ=0
    g20: LineSegment [constr] StartX=40 StartY=2.5 StartZ=0 EndX=37.5 EndY=2.5 EndZ=0
    g21: LineSegment [constr] StartX=37.5 StartY=2.5 StartZ=0 EndX=37.5 EndY=0 EndZ=0
    g22: LineSegment [constr] StartX=37.5 StartY=0 StartZ=0 EndX=40 EndY=0 EndZ=0
    g23: LineSegment [constr] StartX=40 StartY=0 StartZ=0 EndX=40 EndY=2.5 EndZ=0
    g24: LineSegment [constr] StartX=37.5 StartY=95 StartZ=0 EndX=40 EndY=95 EndZ=0
    g25: LineSegment [constr] StartX=40 StartY=95 StartZ=0 EndX=40 EndY=92.5 EndZ=0
    g26: LineSegment [constr] StartX=40 StartY=92.5 StartZ=0 EndX=37.5 EndY=92.5 EndZ=0
    g27: LineSegment [constr] StartX=37.5 StartY=92.5 StartZ=0 EndX=37.5 EndY=95 EndZ=0
    g28: LineSegment [constr] StartX=2.5 StartY=95 StartZ=0 EndX=0 EndY=95 EndZ=0
    g29: LineSegment [constr] StartX=0 StartY=95 StartZ=0 EndX=0 EndY=92.5 EndZ=0
    g30: LineSegment [constr] StartX=0 StartY=92.5 StartZ=0 EndX=2.5 EndY=92.5 EndZ=0
    g31: LineSegment [constr] StartX=2.5 StartY=92.5 StartZ=0 EndX=2.5 EndY=95 EndZ=0
    g32: LineSegment [constr] StartX=2.5 StartY=92.5 StartZ=0 EndX=0 EndY=95 EndZ=0
    g33: LineSegment [constr] StartX=37.5 StartY=92.5 StartZ=0 EndX=40 EndY=95 EndZ=0
    g34: LineSegment [constr] StartX=37.5 StartY=2.5 StartZ=0 EndX=40 EndY=0 EndZ=0
    g35: LineSegment [constr] StartX=0 StartY=0 StartZ=0 EndX=2.5 EndY=2.5 EndZ=0
    g36: LineSegment StartX=2.5 StartY=95 StartZ=0 EndX=10 EndY=95 EndZ=0
    g37: LineSegment [constr] StartX=10 StartY=95 StartZ=0 EndX=10 EndY=94 EndZ=0
    g38: LineSegment [constr] StartX=10 StartY=94 StartZ=0 EndX=11 EndY=94 EndZ=0
    g39: LineSegment StartX=11 StartY=94 StartZ=0 EndX=11 EndY=90 EndZ=0
    g40: LineSegment [constr] StartX=11 StartY=90 StartZ=0 EndX=12 EndY=90 EndZ=0
    g41: LineSegment [constr] StartX=12 StartY=90 StartZ=0 EndX=12 EndY=89 EndZ=0
    g42: LineSegment StartX=12 StartY=89 StartZ=0 EndX=28 EndY=89 EndZ=0
    g43: LineSegment [constr] StartX=28 StartY=89 StartZ=0 EndX=28 EndY=90 EndZ=0
    g44: LineSegment [constr] StartX=28 StartY=90 StartZ=0 EndX=29 EndY=90 EndZ=0
    g45: LineSegment StartX=29 StartY=90 StartZ=0 EndX=29 EndY=94 EndZ=0
    g46: LineSegment [constr] StartX=29 StartY=94 StartZ=0 EndX=30 EndY=94 EndZ=0
    g47: LineSegment [constr] StartX=30 StartY=94 StartZ=0 EndX=30 EndY=95 EndZ=0
    g48: LineSegment StartX=30 StartY=95 StartZ=0 EndX=37.5 EndY=95 EndZ=0
    g49: ArcOfCircle CenterX=10 CenterY=94 CenterZ=0 NormalX=0 NormalY=0 NormalZ=1 AngleXU=0 Radius=1 StartAngle=0 EndAngle=1.5708
    g50: ArcOfCircle CenterX=12 CenterY=90 CenterZ=0 NormalX=0 NormalY=0 NormalZ=1 AngleXU=0 Radius=1 StartAngle=3.14159 EndAngle=4.71239
    g51: ArcOfCircle CenterX=28 CenterY=90 CenterZ=0 NormalX=0 NormalY=0 NormalZ=1 AngleXU=0 Radius=1 StartAngle=4.71239 EndAngle=6.28319
    g52: ArcOfCircle CenterX=30 CenterY=94 CenterZ=0 NormalX=0 NormalY=0 NormalZ=1 AngleXU=0 Radius=1 StartAngle=1.5708 EndAngle=3.14159
  constraints (142):
    c: Horizontal(g0)
    c: Horizontal(g2)
    c: Vertical(g1)
    c: Vertical(g3)
    c: Radius(g8) = 1.5
    c: Equal(g8,g9)
    c: Equal(g9,g11)
    c: Equal(g11,g10)
    c: Coincident(g1,g5)
    c: Coincident(g0,g5)
    c: Coincident(g0,g4)
    c: Coincident(g3,g4)
    c: Coincident(g1,g6)
    c: Coincident(g2,g6)
    c: Coincident(g2,g7)
    c: Coincident(g3,g7)
    c: Coincident(g12,g13)
    c: Coincident(g13,g14)
    c: Coincident(g14,g15)
    c: Coincident(g15,g12)
    c: Horizontal(g12)
    c: Horizontal(g14)
    c: Vertical(g13)
    c: Vertical(g15)
    c: Coincident(g12,g8)
    c: Coincident(g13,g11)
    c: Coincident(g9,g12)
    c: Coincident(g10,g14)
    c: Coincident(g16,g17)
    c: Coincident(g17,g18)
    c: Coincident(g18,g19)
    c: Coincident(g19,g16)
    c: Horizontal(g16)
    c: Horizontal(g18)
    c: Vertical(g17)
    c: Vertical(g19)
    c: Coincident(g16,g3)
    c: Coincident(g17,g2)
    c: Coincident(g20,g21)
    c: Coincident(g21,g22)
    c: Coincident(g22,g23)
    c: Coincident(g23,g20)
    c: Horizontal(g20)
    c: Horizontal(g22)
    c: Vertical(g21)
    c: Vertical(g23)
    c: Coincident(g20,g1)
    c: Coincident(g21,g2)
    c: Coincident(g24,g25)
    c: Coincident(g25,g26)
    c: Coincident(g26,g27)
    c: Coincident(g27,g24)
    c: Horizontal(g24)
    c: Horizontal(g26)
    c: Vertical(g25)
    c: Vertical(g27)
    c: Coincident(g24,g0)
    c: Coincident(g25,g1)
    c: Coincident(g28,g29)
    c: Coincident(g29,g30)
    c: Coincident(g30,g31)
    c: Coincident(g31,g28)
    c: Horizontal(g28)
    c: Horizontal(g30)
    c: Vertical(g29)
    c: Vertical(g31)
    c: Coincident(g28,g0)
    c: Coincident(g29,g3)
    c: DistanceY(g27,g27) = 2.5
    c: DistanceX(g20,g20) = 2.5
    c: DistanceY(g21,g21) = 2.5
    c: DistanceX(g16,g16) = 2.5
    c: Radius(g7) = 2.5
    c: Equal(g7,g6)
    c: Equal(g6,g5)
    c: Equal(g5,g4)
    c: Coincident(g18,g-1)
    c: Coincident(g32,g8)
    c: Coincident(g32,g28)
    c: Coincident(g33,g9)
    c: Coincident(g33,g24)
    c: Coincident(g34,g11)
    c: Coincident(g34,g22)
    c: Coincident(g35,g-1)
    c: Coincident(g35,g10)
    c: Equal(g35,g34)
    c: Equal(g33,g32)
    c: DistanceX(g24,g24) = 2.5
    c: DistanceX(g28,g28) = 2.5
    c: DistanceY(g29,g29) = 2.5
    c: DistanceY(g19,g19) = 2.5
    c: DistanceX(g28,g24) = 40
    c: DistanceY(g28) = 95
    c: DistanceY(g2,g10) = 2.5
    c: DistanceX(g3,g8) = 2.5
    c: DistanceY(g8,g0) = 2.5
    c: Coincident(g0,g36)
    c: Horizontal(g36)
    c: Coincident(g36,g37)
    c: Vertical(g37)
    c: Coincident(g37,g38)
    c: Horizontal(g38)
    c: Coincident(g38,g39)
    c: Vertical(g39)
    c: Coincident(g39,g40)
    c: Horizontal(g40)
    c: Coincident(g40,g41)
    c: Vertical(g41)
    c: Coincident(g41,g42)
    c: Horizontal(g42)
    c: Coincident(g42,g43)
    c: Vertical(g43)
    c: Coincident(g43,g44)
    c: Horizontal(g44)
    c: Coincident(g44,g45)
    c: Vertical(g45)
    c: Coincident(g45,g46)
    c: Horizontal(g46)
    c: Coincident(g46,g47)
    c: Vertical(g47)
    c: Coincident(g47,g48)
    c: Coincident(g48,g0)
    c: Horizontal(g48)
    c: Coincident(g49,g37)
    c: Coincident(g49,g36)
    c: Coincident(g49,g38)
    c: Coincident(g50,g40)
    c: Coincident(g50,g39)
    c: Coincident(g50,g41)
    c: Coincident(g51,g43)
    c: Coincident(g51,g44)
    c: Coincident(g51,g42)
    c: Coincident(g52,g46)
    c: Coincident(g52,g47)
    c: Coincident(g52,g45)
    c: Equal(g49,g52)
    c: Equal(g52,g51)
    c: Equal(g51,g50)
    c: Equal(g36,g48)
    c: Radius(g49) = 1
    c: DistanceY(g42,g47) = 6
    c: DistanceX(g39,g44) = 18
FEATURE [PartDesign::Pad] Pad029
  Length = 1.6
  Length2 = 100
  Profile = -> Sketch001002048
  Type = 0
FEATURE [PartDesign::Body] Body028  label="Body Circuit Board001"
  Group = -> [Sketch001002048,Pad029]
  Origin = -> Origin066
  Tip = -> Pad029
FEATURE [Sketcher::SketchObject] Sketch001002049  label="Cut009"
  Placement = pos=(0,0,0.8) rot=(0,0,1;0rad)
  sketch-geometry (18):
    g0: LineSegment StartX=-18.5 StartY=-39.5 StartZ=0 EndX=18.5 EndY=-39.5 EndZ=0
    g1: LineSegment StartX=18.5 StartY=-39.5 StartZ=0 EndX=18.5 EndY=-36.5 EndZ=0
    g2: LineSegment StartX=18.5 StartY=-36.5 StartZ=0 EndX=10.5 EndY=-36.5 EndZ=0
    g3: LineSegment StartX=10.5 StartY=-36.5 StartZ=0 EndX=10.5 EndY=-33.5 EndZ=0
    g4: LineSegment [constr] StartX=10.5 StartY=-33.5 StartZ=0 EndX=9.5 EndY=-33.5 EndZ=0
    g5: LineSegment [constr] StartX=9.5 StartY=-33.5 StartZ=0 EndX=9.5 EndY=-32.5 EndZ=0
    g6: LineSegment StartX=9.5 StartY=-32.5 StartZ=0 EndX=-9.5 EndY=-32.5 EndZ=0
    g7: LineSegment StartX=-9.5 StartY=-32.5 StartZ=0 EndX=-10.5 EndY=-36.5 EndZ=0
    g8: LineSegment StartX=-10.5 StartY=-36.5 StartZ=0 EndX=-18.5 EndY=-36.5 EndZ=0
    g9: LineSegment StartX=-18.5 StartY=-36.5 StartZ=0 EndX=-18.5 EndY=-39.5 EndZ=0
    g10: LineSegment StartX=-4.75 StartY=-36.5 StartZ=0 EndX=4.75 EndY=-36.5 EndZ=0
    g11: LineSegment StartX=4.75 StartY=-36.5 StartZ=0 EndX=4.75 EndY=-37.5 EndZ=0
    g12: LineSegment StartX=4.75 StartY=-37.5 StartZ=0 EndX=-4.75 EndY=-37.5 EndZ=0
    g13: LineSegment StartX=-4.75 StartY=-37.5 StartZ=0 EndX=-4.75 EndY=-36.5 EndZ=0
    g14: ArcOfCircle CenterX=9.5 CenterY=-33.5 CenterZ=0 NormalX=0 NormalY=0 NormalZ=1 AngleXU=0 Radius=1 StartAngle=0 EndAngle=1.5708
    g15: LineSegment [constr] StartX=-18.5 StartY=-39.5 StartZ=0 EndX=-18.5 EndY=39.5 EndZ=0
    g16: LineSegment [constr] StartX=-18.5 StartY=39.5 StartZ=0 EndX=18.5 EndY=39.5 EndZ=0
    g17: LineSegment [constr] StartX=18.5 StartY=39.5 StartZ=0 EndX=18.5 EndY=-39.5 EndZ=0
  constraints (51):
    c: Horizontal(g0)
    c: Coincident(g0,g1)
    c: Vertical(g1)
    c: Coincident(g1,g2)
    c: Horizontal(g2)
    c: Coincident(g2,g3)
    c: Vertical(g3)
    c: Coincident(g3,g4)
    c: Horizontal(g4)
    c: Coincident(g4,g5)
    c: Vertical(g5)
    c: Coincident(g5,g6)
    c: Horizontal(g6)
    c: Coincident(g6,g7)
    c: Coincident(g7,g8)
    c: Horizontal(g8)
    c: Coincident(g8,g9)
    c: Coincident(g9,g0)
    c: Vertical(g9)
    c: Coincident(g10,g11)
    c: Coincident(g11,g12)
    c: Coincident(g12,g13)
    c: Coincident(g13,g10)
    c: Horizontal(g10)
    c: Horizontal(g12)
    c: Vertical(g11)
    c: Vertical(g13)
    c: Equal(g9,g1)
    c: Coincident(g14,g4)
    c: Coincident(g14,g5)
    c: Coincident(g14,g3)
    c: DistanceY(g9,g9) = 3
    c: Coincident(g0,g15)
    c: Vertical(g15)
    c: Coincident(g15,g16)
    c: Horizontal(g16)
    c: Coincident(g16,g17)
    c: Coincident(g17,g0)
    c: Vertical(g17)
    c: DistanceY(g17,g17) = 79
    c: DistanceX(g16,g16) = 37
    c: Symmetric(g0,g15,g-1)
    c: DistanceX(g8,g8) = 8
    c: Equal(g8,g2)
    c: DistanceY(g7,g6) = 4
    c: DistanceX(g6,g6) = 19
    c: Radius(g14) = 1
    c: DistanceX(g10,g10) = 9.5
    c: DistanceY(g13,g13) = 1
    c: Symmetric(g12,g11,g-2)
    c: DistanceY(g0,g12) = 2
FEATURE [Sketcher::SketchObject] Sketch001002050  label="Sketch001002042"
  Placement = pos=(19,0,0) rot=(0.57735,0.57735,0.57735;2.0944rad)
  sketch-geometry (8):
    g0: ArcOfEllipse CenterX=-37.3772 CenterY=0.960868 CenterZ=0 NormalX=0 NormalY=0 NormalZ=1 MajorRadius=2.12996 MinorRadius=0.3 AngleXU=0.076069 StartAngle=1.5708 EndAngle=3.14159
    g1: LineSegment [constr] StartX=-35.2534 StartY=1.12274 StartZ=0 EndX=-39.501 EndY=0.799 EndZ=0
    g2: LineSegment [constr] StartX=-37.4 StartY=1.26 StartZ=0 EndX=-37.3544 EndY=0.661735 EndZ=0
    g3: GeomPoint X=-35.2746 Y=1.12112 Z=0
    g4: GeomPoint X=-39.4798 Y=0.800614 Z=0
    g5: LineSegment StartX=-39.501 StartY=0.799 StartZ=0 EndX=-39.501 EndY=1.76 EndZ=0
    g6: LineSegment StartX=-39.501 StartY=1.76 StartZ=0 EndX=-37.4 EndY=1.76 EndZ=0
    g7: LineSegment StartX=-37.4 StartY=1.76 StartZ=0 EndX=-37.4 EndY=1.26 EndZ=0
  constraints (16):
    c: InternalAlignment(g1-g4 -> g0) x4
    c: Coincident(g0,g1)
    c: DistanceX(g0,g-1) = 39.501
    c: DistanceY(g-1,g0) = 0.799
    c: Coincident(g0,g2)
    c: Distance(g2) = 0.6
    c: DistanceX(g0,g-1) = 37.4
    c: DistanceY(g-1,g0) = 1.26
    c: Coincident(g5,g0)
    c: Coincident(g5,g6)
    c: Coincident(g6,g7)
    c: Coincident(g7,g0)
    c: Vertical(g7)
    c: Vertical(g5)
    c: Horizontal(g6)
    c: DistanceY(g7,g7) = 0.5
FEATURE [Part::Feature] Part__Feature001002002001001050001001002001002001002001002001002001002001001002001002004001001001001002001002001130  label="OLED_Buchse001"
  Placement = pos=(20,80,1.6) rot=(0,0,1;0rad)
  shape: bbox 20.65 x 5.65 x 2.2 mm, 1342 faces (baked)
FEATURE [Part::Feature] Part__Feature001002002001001050001001002001002001002001002001002001002001001002001002004001001001001002001002001131  label="7Pin_Stecker002"
  Placement = pos=(20,2,1.6) rot=(0,0,1;0rad)
  shape: bbox 12 x 4.98 x 4.1 mm, 457 faces (baked)
FEATURE [PartDesign::Pad] Pad032
  Length = 1.62
  Length2 = 100
  Placement = pos=(0,0,-0.01) rot=(0,0,1;0rad)
  Profile = -> Sketch001002045
  Type = 0
FEATURE [PartDesign::Body] Body030  label="Body029"
  Group = -> [Sketch001002045,Pad032]
  Origin = -> Origin064
  Tip = -> Pad032
FEATURE [PartDesign::Pad] Pad033
  Length = 1.25
  Length2 = 100
  Profile = -> Sketch001002046
  Refine = true
  Type = 0
FEATURE [PartDesign::Pocket] Pocket017
  BaseFeature = -> Pad033
  Length = 1
  Length2 = 100
  Profile = -> Sketch001002042
  Refine = true
  Reversed = true
  Type = 0
FEATURE [PartDesign::Pocket] Pocket018
  BaseFeature = -> Pocket017
  Length = 1
  Length2 = 100
  Profile = -> Sketch001002049
  Refine = true
  Reversed = true
  Type = 0
FEATURE [PartDesign::Body] Body029  label="Body028"
  Group = -> [Sketch001002046,Pad033,Sketch001002042,Pocket017,Sketch001002049,Pocket018]
  Origin = -> Origin061
  Tip = -> Pocket018
FEATURE [Part::Fillet] Fillet038  label="Fillet033"
  Base = -> Body029
  Edges = 3 edges r=0.3: [Edge4,Edge6,Edge14]
FEATURE [Part::Feature] Part__Feature001002002001001050001001002001002001002001002001002001002001001002001002004001001001001002001002001132  label="XMC_Pad001"
  Placement = pos=(20,35,1.6) rot=(0,0,1;3.92699rad)
  shape: bbox 9.899 x 9.899 x 0.901 mm, 1389 faces (baked)
FEATURE [Mesh::Feature] Logo003
  Placement = pos=(-9.5,-49,0.551) rot=(0,0,-1;4.71239rad)
FEATURE [PartDesign::Pad] Pad034
  Length = 1.62
  Length2 = 100
  Placement = pos=(0,0,-0.01) rot=(0,0,1;0rad)
  Profile = -> Sketch001002047
  Type = 0
FEATURE [PartDesign::Body] Body027
  Group = -> [Sketch001002047,Pad034]
  Origin = -> Origin065
  Tip = -> Pad034
FEATURE [Part::Cut] Cut001  label="Cut010"
  Base = -> Body030
  Refine = true
  Tool = -> Body027
FEATURE [PartDesign::Body] Body032
  Group = -> [Sketch001002044,Pad030]
  Origin = -> Origin060
  Tip = -> Pad030
FEATURE [Part::Feature] Part__Feature001002002001001050001001002001002001002001002001002001002001001002001002004001001001001002001002001133  label="Fusion007"
  Placement = pos=(0,-28,0.18) rot=(0,0,1;0rad)
  shape: bbox 15.52 x 8.91 x 3.7 mm, 772 faces (baked)
FEATURE [App::Part] Part032  label="E Paper Board001"
  Group = -> [Body028,Body030,Body027,Cut001]
  License = CC BY 3.0
  LicenseURL = http://creativecommons.org/licenses/by/3.0/
  Origin = -> Origin059
FEATURE [PartDesign::Pocket] Pocket019
  BaseFeature = -> Pad031
  Length = 38
  Length2 = 100
  Placement = pos=(0,0,0.8) rot=(0,0,1;0rad)
  Profile = -> Sketch001002050
  Refine = true
  Type = 0
FEATURE [PartDesign::Body] Body031
  Group = -> [Sketch001002043,Pad031,Sketch001002050,Pocket019]
  Origin = -> Origin058
  Tip = -> Pocket019
FEATURE [Part::Fillet] Fillet039
  Base = -> Body031
  Edges = 2 edges r=0.3: [Edge19,Edge20]
FEATURE [App::Part] Part031  label="E Paper Display001"
  Group = -> [Body032,Body031,Fillet039,Body029,Fillet038,Logo003,Part__Feature001002002001001050001001002001002001002001002001002001002001001002001002004001001001001002001002001133]
  License = CC BY 3.0
  LicenseURL = http://creativecommons.org/licenses/by/3.0/
  Origin = -> Origin062
  Placement = pos=(20,47,0) rot=(1,0,0;3.14159rad)
FEATURE [App::Part] Part030  label="E Paper"
  Group = -> [Part032,Part__Feature001002002001001050001001002001002001002001002001002001002001001002001002004001001001001002001002001132,Part031,Part__Feature001002002001001050001001002001002001002001002001002001002001001002001002004001001001001002001002001131,Part__Feature001002002001001050001001002001002001002001002001002001002001001002001002004001001001001002001002001130]
  License = CC BY 3.0
  LicenseURL = http://creativecommons.org/licenses/by/3.0/
  Origin = -> Origin063
  Placement = pos=(-26,2.3,20) rot=(-0.57735,0.57735,0.57735;2.0944rad)
FEATURE [Part::Feature] Part__Feature001002002001001050001001002001002001002001002001002001002001001002001002004001001001001002001002001134  label="Segment_Display_4X7_V2"
  Placement = pos=(125.5,6.4,15.45) rot=(0.57735,0.57735,-0.57735;2.0944rad)
  shape: bbox 65 x 10.4 x 25 mm, 2042 faces, 2 solids (baked)
FEATURE [Part::Feature] Part__Feature001002002001001050001001002001002  label="Screw Stack001"
  Placement = pos=(-167,5.5,-17.5) rot=(0,1,0;1.5708rad)
  shape: bbox 7.4 x 5.6 x 5.6 mm, 23 faces (baked)
FEATURE [Part::Feature] Part__Feature001002002001001050001001002001002001  label="Screw Stack002"
  Placement = pos=(-167,40.5,-17.5) rot=(0,1,0;1.5708rad)
  shape: bbox 7.4 x 5.6 x 5.6 mm, 23 faces (baked)
FEATURE [Part::Feature] Part__Feature001002002001001050001001002001002002  label="Screw Stack003"
  Placement = pos=(-167,40.5,17.5) rot=(0,1,0;1.5708rad)
  shape: bbox 7.4 x 5.6 x 5.6 mm, 23 faces (baked)
FEATURE [Part::Feature] Part__Feature001002002001001050001001002001002001001  label="Screw Stack004"
  Placement = pos=(-167,5.5,17.5) rot=(0,1,0;1.5708rad)
  shape: bbox 7.4 x 5.6 x 5.6 mm, 23 faces (baked)
FEATURE [Part::Feature] Part__Feature001002002001001050001001002001002001002001002001002001002001001002001002004001001001001002001002001089  label="Screw Stack005"
  Placement = pos=(-195.5,40.5,-17.5) rot=(0,-1,0;1.5708rad)
  shape: bbox 7.4 x 5.6 x 5.6 mm, 23 faces (baked)
FEATURE [Part::Feature] Part__Feature001002002001001050001001002001002001002001002001002001002001001002001002004001001001001002001002001090  label="Screw Stack006"
  Placement = pos=(-195.5,5.5,-17.5) rot=(0,-1,0;1.5708rad)
  shape: bbox 7.4 x 5.6 x 5.6 mm, 23 faces (baked)
FEATURE [Part::Feature] Part__Feature001002002001001050001001002001002001002001002001002001002001001002001002004001001001001002001002001091  label="Screw Stack007"
  Placement = pos=(-195.5,40.5,17.5) rot=(0,-1,0;1.5708rad)
  shape: bbox 7.4 x 5.6 x 5.6 mm, 23 faces (baked)
FEATURE [Part::Feature] Part__Feature001002002001001050001001002001002001002001002001002001002001001002001002004001001001001002001002001092  label="Screw Stack008"
  Placement = pos=(-195.5,5.5,17.5) rot=(0,-1,0;1.5708rad)
  shape: bbox 7.4 x 5.6 x 5.6 mm, 23 faces (baked)
FEATURE [App::Part] Part018  label="stack schrauben unten"
  Group = -> [Part__Feature001002002001001050001001002001002001002001002001002001002001001002001002004001001001001002001002001090,Part__Feature001002002001001050001001002001002001002001002001002001002001001002001002004001001001001002001002001089,Part__Feature001002002001001050001001002001002001002001002001002001002001001002001002004001001001001002001002001091,+1 more]
  Origin = -> Origin046
FEATURE [Part::Feature] Part__Feature001002002001001050  label="Standoff Stack003"
  Placement = pos=(-180.7,40.5,17.5) rot=(0,1,0;1.5708rad)
  shape: bbox 18.1 x 6.928 x 6 mm, 24 faces (baked)
FEATURE [Part::Feature] Part__Feature001002002001001050001  label="Standoff Stack004"
  Placement = pos=(-180.7,5.5,17.5) rot=(0,1,0;1.5708rad)
  shape: bbox 18.1 x 6.928 x 6 mm, 24 faces (baked)
FEATURE [Part::Feature] Part__Feature001002002001001050001001  label="Standoff Stack001"
  Placement = pos=(-180.7,5.5,-17.5) rot=(0,1,0;1.5708rad)
  shape: bbox 18.1 x 6.928 x 6 mm, 24 faces (baked)
FEATURE [Part::Feature] Part__Feature001002002001001050001001001  label="Standoff Stack002"
  Placement = pos=(-180.7,40.5,-17.5) rot=(0,1,0;1.5708rad)
  shape: bbox 18.1 x 6.928 x 6 mm, 24 faces (baked)
FEATURE [App::Part] Part019  label="stack abstandsbolzen 12mm"
  Group = -> [Part__Feature001002002001001050001001,Part__Feature001002002001001050001001001,Part__Feature001002002001001050,Part__Feature001002002001001050001]
  Origin = -> Origin047
FEATURE [Part::Feature] Part__Feature001002002001001050001001002001002001002001002001002001002001001002001002004001001001001002001002001033  label="Cut004"
  Placement = pos=(-192.5,5.5,-17.5) rot=(0,1,0;1.5708rad)
  shape: bbox 10 x 6.928 x 6 mm, 22 faces (baked)
FEATURE [Part::Feature] Part__Feature001002002001001050001001002001002001002001002001002001002001001002001002004001001001001002001002001034  label="Cut005"
  Placement = pos=(-192.5,40.5,-17.5) rot=(0,1,0;1.5708rad)
  shape: bbox 10 x 6.928 x 6 mm, 22 faces (baked)
FEATURE [Part::Feature] Part__Feature001002002001001050001001002001002001002001002001002001002001001002001002004001001001001002001002001035  label="Cut006"
  Placement = pos=(-192.5,40.5,17.5) rot=(0,1,0;1.5708rad)
  shape: bbox 10 x 6.928 x 6 mm, 22 faces (baked)
FEATURE [Part::Feature] Part__Feature001002002001001050001001002001002001002001002001002001002001001002001002004001001001001002001002001036  label="Cut007"
  Placement = pos=(-192.5,5.5,17.5) rot=(0,1,0;1.5708rad)
  shape: bbox 10 x 6.928 x 6 mm, 22 faces (baked)
FEATURE [App::Part] Part020  label="stack abstandsbolzen 10mm"
  Group = -> [Part__Feature001002002001001050001001002001002001002001002001002001002001001002001002004001001001001002001002001033,Part__Feature001002002001001050001001002001002001002001002001002001002001001002001002004001001001001002001002001034,Part__Feature001002002001001050001001002001002001002001002001002001002001001002001002004001001001001002001002001035,+1 more]
  Origin = -> Origin048
FEATURE [Part::Feature] Part__Feature001002002001001050001001002001002001002001002001002001002001001002001002004001001001001002001002001167  label="Nut E-Pap006"
  Placement = pos=(-28.5,6.3,-17.5) rot=(1,0,0;1.5708rad)
  shape: bbox 6.352 x 2.4 x 6.351 mm, 30 faces (baked)
FEATURE [Part::Feature] Part__Feature001002002001001050001001002001002001002001002001002001002001001002001002004001001001001002001002001168  label="Nut E-Pap007"
  Placement = pos=(-28.5,6.3,17.5) rot=(1,0,0;1.5708rad)
  shape: bbox 6.352 x 2.4 x 6.351 mm, 30 faces (baked)
FEATURE [Part::Feature] Part__Feature001002002001001050001001002001002001002001002001002001002001001002001002004001001001001002001002001169  label="Nut E-Pap008"
  Placement = pos=(-118.5,6.3,17.5) rot=(1,0,0;1.5708rad)
  shape: bbox 6.352 x 2.4 x 6.351 mm, 30 faces (baked)
FEATURE [Part::Feature] Part__Feature001002002001001050001001002001002001002001002001002001002001001002001002004001001001001002001002001171  label="Nut E-Pap001"
  Placement = pos=(-118.5,2.4,-17.5) rot=(1,0,0;1.5708rad)
  shape: bbox 6.352 x 2.4 x 6.351 mm, 30 faces (baked)
FEATURE [Part::Feature] Part__Feature001002002001001050001001002001002001002001002001002001002001001002001002004001001001001002001002001172  label="Screw Long E-Pap001"
  Placement = pos=(-118.5,-3,-17.5) rot=(1,0,0;1.5708rad)
  shape: bbox 5.6 x 12.4 x 5.6 mm, 20 faces (baked)
FEATURE [Part::Feature] Part__Feature001002002001001050001001002001002001002001002001002001002001001002001002004001001001001002001002001174  label="Nut E-Pap003"
  Placement = pos=(-28.5,2.4,17.5) rot=(1,0,0;1.5708rad)
  shape: bbox 6.352 x 2.4 x 6.351 mm, 30 faces (baked)
FEATURE [Part::Feature] Part__Feature001002002001001050001001002001002001002001002001002001002001001002001002004001001001001002001002001175  label="Nut E-Pap004"
  Placement = pos=(-118.5,2.4,17.5) rot=(1,0,0;1.5708rad)
  shape: bbox 6.352 x 2.4 x 6.351 mm, 30 faces (baked)
FEATURE [Part::Feature] Part__Feature001002002001001050001001002001002001002001002001002001002001001002001002004001001001001002001002001176  label="Nut E-Pap002"
  Placement = pos=(-28.5,2.4,-17.5) rot=(1,0,0;1.5708rad)
  shape: bbox 6.352 x 2.4 x 6.351 mm, 30 faces (baked)
FEATURE [Part::Feature] Part__Feature001002002001001050001001002001002001002001002001002001002001001002001002004001001001001002001002001170  label="Screw Long E-Pap002"
  Placement = pos=(-28.5,-3,-17.5) rot=(1,0,0;1.5708rad)
  shape: bbox 5.6 x 12.4 x 5.6 mm, 20 faces (baked)
FEATURE [Part::Feature] Part__Feature001002002001001050001001002001002001002001002001002001002001001002001002004001001001001002001002001178  label="Screw Long E-Pap003"
  Placement = pos=(-28.5,-3,17.5) rot=(1,0,0;1.5708rad)
  shape: bbox 5.6 x 12.4 x 5.6 mm, 20 faces (baked)
FEATURE [App::Part] Part041  label="E-Pap muttern 001"
  Group = -> [Part__Feature001002002001001050001001002001002001002001002001002001002001001002001002004001001001001002001002001171,Part__Feature001002002001001050001001002001002001002001002001002001002001001002001002004001001001001002001002001176,Part__Feature001002002001001050001001002001002001002001002001002001002001001002001002004001001001001002001002001174,+1 more]
  Origin = -> Origin077
FEATURE [Part::Feature] Part__Feature001002002001001050001001002001002001002001002001002001002001001002001002004001001001001002001002001180  label="Nut E-Pap005"
  Placement = pos=(-118.5,6.3,-17.5) rot=(1,0,0;1.5708rad)
  shape: bbox 6.352 x 2.4 x 6.351 mm, 30 faces (baked)
FEATURE [App::Part] Part043  label="E-Pap muttern 002"
  Group = -> [Part__Feature001002002001001050001001002001002001002001002001002001002001001002001002004001001001001002001002001180,Part__Feature001002002001001050001001002001002001002001002001002001002001001002001002004001001001001002001002001167,Part__Feature001002002001001050001001002001002001002001002001002001002001001002001002004001001001001002001002001168,+1 more]
  Origin = -> Origin076
FEATURE [Part::Feature] Part__Feature001002002001001050001001002001002001002001002001002001002001001002001002004001001001001002001002001182  label="Screw Long E-Pap004"
  Placement = pos=(-118.5,-3,17.5) rot=(1,0,0;1.5708rad)
  shape: bbox 5.6 x 12.4 x 5.6 mm, 20 faces (baked)
FEATURE [App::Part] Part040  label="E-Pap schrauben"
  Group = -> [Part__Feature001002002001001050001001002001002001002001002001002001002001001002001002004001001001001002001002001172,Part__Feature001002002001001050001001002001002001002001002001002001002001001002001002004001001001001002001002001170,Part__Feature001002002001001050001001002001002001002001002001002001002001001002001002004001001001001002001002001178,+1 more]
  Origin = -> Origin075
FEATURE [Part::Feature] Part__Feature001002002001001050001001002001002001002001002001002001002001001002001002004001001001001002001002001152  label="Screw Long motion004"
  Placement = pos=(85,-3,12.95) rot=(1,0,0;1.5708rad)
  shape: bbox 5.6 x 12.4 x 5.6 mm, 20 faces (baked)
FEATURE [Part::Feature] Part__Feature001002002001001050001001002001002001002001002001002001002001001002001002004001001001001002001002001153  label="Screw Long motion001"
  Placement = pos=(45,-3,-7.05) rot=(1,0,0;1.5708rad)
  shape: bbox 5.6 x 12.4 x 5.6 mm, 20 faces (baked)
FEATURE [Part::Feature] Part__Feature001002002001001050001001002001002001002001002001002001002001001002001002004001001001001002001002001154  label="Nut motion002"
  Placement = pos=(85,4,-7.05) rot=(1,0,0;1.5708rad)
  shape: bbox 6.352 x 2.4 x 6.351 mm, 30 faces (baked)
FEATURE [Part::Feature] Part__Feature001002002001001050001001002001002001002001002001002001002001001002001002004001001001001002001002001156  label="Screw Long motion003"
  Placement = pos=(45,-3,12.95) rot=(1,0,0;1.5708rad)
  shape: bbox 5.6 x 12.4 x 5.6 mm, 20 faces (baked)
FEATURE [Part::Feature] Part__Feature001002002001001050001001002001002001002001002001002001002001001002001002004001001001001002001002001157  label="Nut motion004"
  Placement = pos=(85,4,12.95) rot=(1,0,0;1.5708rad)
  shape: bbox 6.352 x 2.4 x 6.351 mm, 30 faces (baked)
FEATURE [Part::Feature] Part__Feature001002002001001050001001002001002001002001002001002001002001001002001002004001001001001002001002001159  label="Nut motion003"
  Placement = pos=(45,4,12.95) rot=(1,0,0;1.5708rad)
  shape: bbox 6.352 x 2.4 x 6.351 mm, 30 faces (baked)
FEATURE [Part::Feature] Part__Feature001002002001001050001001002001002001002001002001002001002001001002001002004001001001001002001002001162  label="Screw Long motion002"
  Placement = pos=(85,-3,-7.05) rot=(1,0,0;1.5708rad)
  shape: bbox 5.6 x 12.4 x 5.6 mm, 20 faces (baked)
FEATURE [App::Part] Part039  label="Motion schrauben"
  Group = -> [Part__Feature001002002001001050001001002001002001002001002001002001002001001002001002004001001001001002001002001153,Part__Feature001002002001001050001001002001002001002001002001002001002001001002001002004001001001001002001002001162,Part__Feature001002002001001050001001002001002001002001002001002001002001001002001002004001001001001002001002001156,+1 more]
  Origin = -> Origin074
FEATURE [Part::Feature] Part__Feature001002002001001050001001002001002001002001002001002001002001001002001002004001001001001002001002001166  label="Nut motion001"
  Placement = pos=(45,4,-7.05) rot=(1,0,0;1.5708rad)
  shape: bbox 6.352 x 2.4 x 6.351 mm, 30 faces (baked)
FEATURE [App::Part] Part037  label="Motion muttern"
  Group = -> [Part__Feature001002002001001050001001002001002001002001002001002001002001001002001002004001001001001002001002001166,Part__Feature001002002001001050001001002001002001002001002001002001002001001002001002004001001001001002001002001154,Part__Feature001002002001001050001001002001002001002001002001002001002001001002001002004001001001001002001002001159,+1 more]
  Origin = -> Origin071
FEATURE [Part::Feature] Part__Feature001002002001001050001001002001002001002001002  label="Screw Long001"
  Placement = pos=(96.35,-3,-17.05) rot=(1,0,0;1.5708rad)
  shape: bbox 5.6 x 12.4 x 5.6 mm, 20 faces (baked)
FEATURE [Part::Feature] Part__Feature001002002001001050001001002001002001002001002001  label="Screw Long002"
  Placement = pos=(116.35,-3,-17.05) rot=(1,0,0;1.5708rad)
  shape: bbox 5.6 x 12.4 x 5.6 mm, 20 faces (baked)
FEATURE [Part::Feature] Part__Feature001002002001001050001001002001002001002001002002  label="Screw Long003"
  Placement = pos=(96.35,-3,-7.05) rot=(1,0,0;1.5708rad)
  shape: bbox 5.6 x 12.4 x 5.6 mm, 20 faces (baked)
FEATURE [Part::Feature] Part__Feature001002002001001050001001002001002001002001002001001  label="Screw Long004"
  Placement = pos=(116.35,-3,-7.05) rot=(1,0,0;1.5708rad)
  shape: bbox 5.6 x 12.4 x 5.6 mm, 20 faces (baked)
FEATURE [App::Part] Part014  label="ambiente schrauben"
  Group = -> [Part__Feature001002002001001050001001002001002001002001002,Part__Feature001002002001001050001001002001002001002001002001,Part__Feature001002002001001050001001002001002001002001002002,Part__Feature001002002001001050001001002001002001002001002001001]
  Origin = -> Origin042
FEATURE [Part::Feature] Part__Feature001002002001001050001001002001002001002001002001002001002  label="Nut006"
  Placement = pos=(96.35,2.4,-17.05) rot=(1,0,0;1.5708rad)
  shape: bbox 6.352 x 2.4 x 6.351 mm, 30 faces (baked)
FEATURE [Part::Feature] Part__Feature001002002001001050001001002001002001002001002001002001002001  label="Nut007"
  Placement = pos=(116.35,2.4,-17.05) rot=(1,0,0;1.5708rad)
  shape: bbox 6.352 x 2.4 x 6.351 mm, 30 faces (baked)
FEATURE [Part::Feature] Part__Feature001002002001001050001001002001002001002001002001002001002002  label="Nut008"
  Placement = pos=(96.35,2.4,-7.05) rot=(1,0,0;1.5708rad)
  shape: bbox 6.352 x 2.4 x 6.351 mm, 30 faces (baked)
FEATURE [Part::Feature] Part__Feature001002002001001050001001002001002001002001002001002001002001001  label="Nut009"
  Placement = pos=(116.35,2.4,-7.05) rot=(1,0,0;1.5708rad)
  shape: bbox 6.352 x 2.4 x 6.351 mm, 30 faces (baked)
FEATURE [App::Part] Part013  label="ambiente muttern 001"
  Group = -> [Part__Feature001002002001001050001001002001002001002001002001002001002,Part__Feature001002002001001050001001002001002001002001002001002001002001,Part__Feature001002002001001050001001002001002001002001002001002001002002,Part__Feature001002002001001050001001002001002001002001002001002001002001001]
  Origin = -> Origin041
FEATURE [Part::Feature] Part__Feature001002002001001050001001002001002001002001002001002001002001001002001002004001001001001002001002001081  label="Nut010"
  Placement = pos=(96.35,4.8,-17.05) rot=(1,0,0;1.5708rad)
  shape: bbox 6.352 x 2.4 x 6.351 mm, 30 faces (baked)
FEATURE [Part::Feature] Part__Feature001002002001001050001001002001002001002001002001002001002001001002001002004001001001001002001002001082  label="Nut012"
  Placement = pos=(116.35,4.8,-7.05) rot=(1,0,0;1.5708rad)
  shape: bbox 6.352 x 2.4 x 6.351 mm, 30 faces (baked)
FEATURE [Part::Feature] Part__Feature001002002001001050001001002001002001002001002001002001002001001002001002004001001001001002001002001083  label="Nut013"
  Placement = pos=(96.35,4.8,-7.05) rot=(1,0,0;1.5708rad)
  shape: bbox 6.352 x 2.4 x 6.351 mm, 30 faces (baked)
FEATURE [Part::Feature] Part__Feature001002002001001050001001002001002001002001002001002001002001001002001002004001001001001002001002001084  label="Nut011"
  Placement = pos=(116.35,4.8,-17.05) rot=(1,0,0;1.5708rad)
  shape: bbox 6.352 x 2.4 x 6.351 mm, 30 faces (baked)
FEATURE [App::Part] Part015  label="ambiente muttern 002"
  Group = -> [Part__Feature001002002001001050001001002001002001002001002001002001002001001002001002004001001001001002001002001081,Part__Feature001002002001001050001001002001002001002001002001002001002001001002001002004001001001001002001002001084,Part__Feature001002002001001050001001002001002001002001002001002001002001001002001002004001001001001002001002001082,+1 more]
  Origin = -> Origin043
FEATURE [Part::Feature] Part__Feature001002002001001050001001002001002001002001002001002001002001001002001002004001001001001002001002001088  label="Nut017"
  Placement = pos=(116.35,8.8,-7.05) rot=(1,0,0;1.5708rad)
  shape: bbox 6.352 x 2.4 x 6.351 mm, 30 faces (baked)
FEATURE [Part::Feature] Part__Feature001002002001001050001001002001002001002001002001002001002001001002001002004001001001001002001002001085  label="Nut014"
  Placement = pos=(96.35,8.8,-17.05) rot=(1,0,0;1.5708rad)
  shape: bbox 6.352 x 2.4 x 6.351 mm, 30 faces (baked)
FEATURE [Part::Feature] Part__Feature001002002001001050001001002001002001002001002001002001002001001002001002004001001001001002001002001086  label="Nut015"
  Placement = pos=(116.35,8.8,-17.05) rot=(1,0,0;1.5708rad)
  shape: bbox 6.352 x 2.4 x 6.351 mm, 30 faces (baked)
FEATURE [Part::Feature] Part__Feature001002002001001050001001002001002001002001002001002001002001001002001002004001001001001002001002001087  label="Nut016"
  Placement = pos=(96.35,8.8,-7.05) rot=(1,0,0;1.5708rad)
  shape: bbox 6.352 x 2.4 x 6.351 mm, 30 faces (baked)
FEATURE [App::Part] Part016  label="ambiente muttern 003"
  Group = -> [Part__Feature001002002001001050001001002001002001002001002001002001002001001002001002004001001001001002001002001085,Part__Feature001002002001001050001001002001002001002001002001002001002001001002001002004001001001001002001002001086,Part__Feature001002002001001050001001002001002001002001002001002001002001001002001002004001001001001002001002001087,+1 more]
  Origin = -> Origin044
FEATURE [Part::Feature] Part__Feature001002002001001050001001002001002001002001002001002001002001001002001002004001001001001002001002001135  label="Nut SegD006"
  Placement = pos=(188,4.8,-7.05) rot=(1,0,0;1.5708rad)
  shape: bbox 6.352 x 2.4 x 6.351 mm, 30 faces (baked)
FEATURE [Part::Feature] Part__Feature001002002001001050001001002001002001002001002001002001002001001002001002004001001001001002001002001136  label="Nut SegD007"
  Placement = pos=(188,4.8,12.95) rot=(1,0,0;1.5708rad)
  shape: bbox 6.352 x 2.4 x 6.351 mm, 30 faces (baked)
FEATURE [Part::Feature] Part__Feature001002002001001050001001002001002001002001002001002001002001001002001002004001001001001002001002001137  label="Nut SegD008"
  Placement = pos=(128,4.8,12.95) rot=(1,0,0;1.5708rad)
  shape: bbox 6.352 x 2.4 x 6.351 mm, 30 faces (baked)
FEATURE [Part::Feature] Part__Feature001002002001001050001001002001002001002001002001002001002001001002001002004001001001001002001002001138  label="Screw Long SegD002"
  Placement = pos=(188,-3,-7.05) rot=(1,0,0;1.5708rad)
  shape: bbox 5.6 x 12.4 x 5.6 mm, 20 faces (baked)
FEATURE [Part::Feature] Part__Feature001002002001001050001001002001002001002001002001002001002001001002001002004001001001001002001002001139  label="Nut SegD001"
  Placement = pos=(128,2.4,-7.05) rot=(1,0,0;1.5708rad)
  shape: bbox 6.352 x 2.4 x 6.351 mm, 30 faces (baked)
FEATURE [Part::Feature] Part__Feature001002002001001050001001002001002001002001002001002001002001001002001002004001001001001002001002001140  label="Screw Long SegD001"
  Placement = pos=(128,-3,-7.05) rot=(1,0,0;1.5708rad)
  shape: bbox 5.6 x 12.4 x 5.6 mm, 20 faces (baked)
FEATURE [Part::Feature] Part__Feature001002002001001050001001002001002001002001002001002001002001001002001002004001001001001002001002001141  label="Nut SegD012"
  Placement = pos=(128,8.8,12.95) rot=(1,0,0;1.5708rad)
  shape: bbox 6.352 x 2.4 x 6.351 mm, 30 faces (baked)
FEATURE [Part::Feature] Part__Feature001002002001001050001001002001002001002001002001002001002001001002001002004001001001001002001002001142  label="Nut SegD003"
  Placement = pos=(188,2.4,12.95) rot=(1,0,0;1.5708rad)
  shape: bbox 6.352 x 2.4 x 6.351 mm, 30 faces (baked)
FEATURE [Part::Feature] Part__Feature001002002001001050001001002001002001002001002001002001002001001002001002004001001001001002001002001143  label="Nut SegD004"
  Placement = pos=(128,2.4,12.95) rot=(1,0,0;1.5708rad)
  shape: bbox 6.352 x 2.4 x 6.351 mm, 30 faces (baked)
FEATURE [Part::Feature] Part__Feature001002002001001050001001002001002001002001002001002001002001001002001002004001001001001002001002001144  label="Nut SegD002"
  Placement = pos=(188,2.4,-7.05) rot=(1,0,0;1.5708rad)
  shape: bbox 6.352 x 2.4 x 6.351 mm, 30 faces (baked)
FEATURE [App::Part] Part034  label="SegD muttern 001"
  Group = -> [Part__Feature001002002001001050001001002001002001002001002001002001002001001002001002004001001001001002001002001139,Part__Feature001002002001001050001001002001002001002001002001002001002001001002001002004001001001001002001002001144,Part__Feature001002002001001050001001002001002001002001002001002001002001001002001002004001001001001002001002001142,+1 more]
  Origin = -> Origin069
FEATURE [Part::Feature] Part__Feature001002002001001050001001002001002001002001002001002001002001001002001002004001001001001002001002001145  label="Nut SegD011"
  Placement = pos=(188,8.8,12.95) rot=(1,0,0;1.5708rad)
  shape: bbox 6.352 x 2.4 x 6.351 mm, 30 faces (baked)
FEATURE [Part::Feature] Part__Feature001002002001001050001001002001002001002001002001002001002001001002001002004001001001001002001002001146  label="Screw Long SegD003"
  Placement = pos=(188,-3,12.95) rot=(1,0,0;1.5708rad)
  shape: bbox 5.6 x 12.4 x 5.6 mm, 20 faces (baked)
FEATURE [Part::Feature] Part__Feature001002002001001050001001002001002001002001002001002001002001001002001002004001001001001002001002001147  label="Nut SegD010"
  Placement = pos=(188,8.8,-7.05) rot=(1,0,0;1.5708rad)
  shape: bbox 6.352 x 2.4 x 6.351 mm, 30 faces (baked)
FEATURE [Part::Feature] Part__Feature001002002001001050001001002001002001002001002001002001002001001002001002004001001001001002001002001148  label="Nut SegD005"
  Placement = pos=(128,4.8,-7.05) rot=(1,0,0;1.5708rad)
  shape: bbox 6.352 x 2.4 x 6.351 mm, 30 faces (baked)
FEATURE [Part::Feature] Part__Feature001002002001001050001001002001002001002001002001002001002001001002001002004001001001001002001002001149  label="Nut SegD009"
  Placement = pos=(128,8.8,-7.05) rot=(1,0,0;1.5708rad)
  shape: bbox 6.352 x 2.4 x 6.351 mm, 30 faces (baked)
FEATURE [Part::Feature] Part__Feature001002002001001050001001002001002001002001002001002001002001001002001002004001001001001002001002001150  label="Screw Long SegD004"
  Placement = pos=(128,-3,12.95) rot=(1,0,0;1.5708rad)
  shape: bbox 5.6 x 12.4 x 5.6 mm, 20 faces (baked)
FEATURE [App::Part] Part033  label="SegD schrauben"
  Group = -> [Part__Feature001002002001001050001001002001002001002001002001002001002001001002001002004001001001001002001002001140,Part__Feature001002002001001050001001002001002001002001002001002001002001001002001002004001001001001002001002001138,Part__Feature001002002001001050001001002001002001002001002001002001002001001002001002004001001001001002001002001146,+1 more]
  Origin = -> Origin067
FEATURE [App::Part] Part035  label="SegD muttern 003"
  Group = -> [Part__Feature001002002001001050001001002001002001002001002001002001002001001002001002004001001001001002001002001149,Part__Feature001002002001001050001001002001002001002001002001002001002001001002001002004001001001001002001002001147,Part__Feature001002002001001050001001002001002001002001002001002001002001001002001002004001001001001002001002001145,+1 more]
  Origin = -> Origin070
FEATURE [App::Part] Part036  label="SegD muttern 002"
  Group = -> [Part__Feature001002002001001050001001002001002001002001002001002001002001001002001002004001001001001002001002001148,Part__Feature001002002001001050001001002001002001002001002001002001002001001002001002004001001001001002001002001135,Part__Feature001002002001001050001001002001002001002001002001002001002001001002001002004001001001001002001002001136,+1 more]
  Origin = -> Origin068
FEATURE [Part::Feature] Part__Feature001002002001001050001001002001002001002001002001002001002001001002001002004001001001001002001002001105  label="Screw humidity001"
  Placement = pos=(-86.5,120.6,-10) rot=(-1,0,0;1.5708rad)
  shape: bbox 5.6 x 7.4 x 5.6 mm, 23 faces (baked)
FEATURE [Part::Feature] Part__Feature001002002001001050001001002001002001002001002001002001002001001002001002004001001001001002001002001106  label="Screw humidity006"
  Placement = pos=(-96.5,106,-10) rot=(1,0,0;1.5708rad)
  shape: bbox 5.6 x 7.4 x 5.6 mm, 23 faces (baked)
FEATURE [Part::Feature] Part__Feature001002002001001050001001002001002001002001002001002001002001001002001002004001001001001002001002001107  label="humidity004"
  Placement = pos=(-86.5,109,10) rot=(-1,0,0;1.5708rad)
  shape: bbox 6 x 10 x 6.928 mm, 22 faces (baked)
FEATURE [Part::Feature] Part__Feature001002002001001050001001002001002001002001002001002001002001001002001002004001001001001002001002001108  label="Screw humidity003"
  Placement = pos=(-96.5,120.6,10) rot=(-1,0,0;1.5708rad)
  shape: bbox 5.6 x 7.4 x 5.6 mm, 23 faces (baked)
FEATURE [Part::Feature] Part__Feature001002002001001050001001002001002001002001002001002001002001001002001002004001001001001002001002001109  label="Screw humidity002"
  Placement = pos=(-96.5,120.6,-10) rot=(-1,0,0;1.5708rad)
  shape: bbox 5.6 x 7.4 x 5.6 mm, 23 faces (baked)
FEATURE [Part::Feature] Part__Feature001002002001001050001001002001002001002001002001002001002001001002001002004001001001001002001002001110  label="Screw humidity007"
  Placement = pos=(-86.5,106,10) rot=(1,0,0;1.5708rad)
  shape: bbox 5.6 x 7.4 x 5.6 mm, 23 faces (baked)
FEATURE [Part::Feature] Part__Feature001002002001001050001001002001002001002001002001002001002001001002001002004001001001001002001002001111  label="Screw humidity005"
  Placement = pos=(-86.5,106,-10) rot=(1,0,0;1.5708rad)
  shape: bbox 5.6 x 7.4 x 5.6 mm, 23 faces (baked)
FEATURE [Part::Feature] Part__Feature001002002001001050001001002001002001002001002001002001002001001002001002004001001001001002001002001112  label="Screw humidity004"
  Placement = pos=(-86.5,120.6,10) rot=(-1,0,0;1.5708rad)
  shape: bbox 5.6 x 7.4 x 5.6 mm, 23 faces (baked)
FEATURE [App::Part] Part026  label="humidity schrauben oben"
  Group = -> [Part__Feature001002002001001050001001002001002001002001002001002001002001001002001002004001001001001002001002001105,Part__Feature001002002001001050001001002001002001002001002001002001002001001002001002004001001001001002001002001109,Part__Feature001002002001001050001001002001002001002001002001002001002001001002001002004001001001001002001002001108,+1 more]
  Origin = -> Origin052
FEATURE [Part::Feature] Part__Feature001002002001001050001001002001002001002001002001002001002001001002001002004001001001001002001002001113  label="Screw humidity008"
  Placement = pos=(-96.5,106,10) rot=(1,0,0;1.5708rad)
  shape: bbox 5.6 x 7.4 x 5.6 mm, 23 faces (baked)
FEATURE [App::Part] Part024  label="humidity schrauben unten"
  Group = -> [Part__Feature001002002001001050001001002001002001002001002001002001002001001002001002004001001001001002001002001111,Part__Feature001002002001001050001001002001002001002001002001002001002001001002001002004001001001001002001002001106,Part__Feature001002002001001050001001002001002001002001002001002001002001001002001002004001001001001002001002001110,+1 more]
  Origin = -> Origin054
FEATURE [Part::Feature] Part__Feature001002002001001050001001002001002001002001002001002001002001001002001002004001001001001002001002001114  label="humidity003"
  Placement = pos=(-96.5,109,10) rot=(-1,0,0;1.5708rad)
  shape: bbox 6 x 10 x 6.928 mm, 22 faces (baked)
FEATURE [Part::Feature] Part__Feature001002002001001050001001002001002001002001002001002001002001001002001002004001001001001002001002001115  label="humidity001"
  Placement = pos=(-86.5,109,-10) rot=(-1,0,0;1.5708rad)
  shape: bbox 6 x 10 x 6.928 mm, 22 faces (baked)
FEATURE [Part::Feature] Part__Feature001002002001001050001001002001002001002001002001002001002001001002001002004001001001001002001002001116  label="humidity002"
  Placement = pos=(-96.5,109,-10) rot=(-1,0,0;1.5708rad)
  shape: bbox 6 x 10 x 6.928 mm, 22 faces (baked)
FEATURE [App::Part] Part025  label="humidity abstandsbolzen 10mm"
  Group = -> [Part__Feature001002002001001050001001002001002001002001002001002001002001001002001002004001001001001002001002001115,Part__Feature001002002001001050001001002001002001002001002001002001002001001002001002004001001001001002001002001116,Part__Feature001002002001001050001001002001002001002001002001002001002001001002001002004001001001001002001002001114,+1 more]
  Origin = -> Origin053
FEATURE [Part::Feature] Part__Feature001002002001001050001001002001002001002001002001002001002001001002001002004001001001001002001002001117  label="Screw temp002"
  Placement = pos=(-156.5,120.6,-10) rot=(-1,0,0;1.5708rad)
  shape: bbox 5.6 x 7.4 x 5.6 mm, 23 faces (baked)
FEATURE [Part::Feature] Part__Feature001002002001001050001001002001002001002001002001002001002001001002001002004001001001001002001002001118  label="Screw temp004"
  Placement = pos=(-146.5,120.6,10) rot=(-1,0,0;1.5708rad)
  shape: bbox 5.6 x 7.4 x 5.6 mm, 23 faces (baked)
FEATURE [Part::Feature] Part__Feature001002002001001050001001002001002001002001002001002001002001001002001002004001001001001002001002001119  label="Screw temp001"
  Placement = pos=(-146.5,120.6,-10) rot=(-1,0,0;1.5708rad)
  shape: bbox 5.6 x 7.4 x 5.6 mm, 23 faces (baked)
FEATURE [Part::Feature] Part__Feature001002002001001050001001002001002001002001002001002001002001001002001002004001001001001002001002001120  label="Screw temp003"
  Placement = pos=(-156.5,120.6,10) rot=(-1,0,0;1.5708rad)
  shape: bbox 5.6 x 7.4 x 5.6 mm, 23 faces (baked)
FEATURE [App::Part] Part027  label="temp schrauben oben"
  Group = -> [Part__Feature001002002001001050001001002001002001002001002001002001002001001002001002004001001001001002001002001119,Part__Feature001002002001001050001001002001002001002001002001002001002001001002001002004001001001001002001002001117,Part__Feature001002002001001050001001002001002001002001002001002001002001001002001002004001001001001002001002001120,+1 more]
  Origin = -> Origin055
FEATURE [Part::Feature] Part__Feature001002002001001050001001002001002001002001002001002001002001001002001002004001001001001002001002001121  label="Screw temp005"
  Placement = pos=(-146.5,106,-10) rot=(1,0,0;1.5708rad)
  shape: bbox 5.6 x 7.4 x 5.6 mm, 23 faces (baked)
FEATURE [Part::Feature] Part__Feature001002002001001050001001002001002001002001002001002001002001001002001002004001001001001002001002001122  label="Screw temp007"
  Placement = pos=(-156.5,106,10) rot=(1,0,0;1.5708rad)
  shape: bbox 5.6 x 7.4 x 5.6 mm, 23 faces (baked)
FEATURE [Part::Feature] Part__Feature001002002001001050001001002001002001002001002001002001002001001002001002004001001001001002001002001123  label="temp004"
  Placement = pos=(-146.5,109,10) rot=(-1,0,0;1.5708rad)
  shape: bbox 6 x 10 x 6.928 mm, 22 faces (baked)
FEATURE [Part::Feature] Part__Feature001002002001001050001001002001002001002001002001002001002001001002001002004001001001001002001002001124  label="Screw temp006"
  Placement = pos=(-156.5,106,-10) rot=(1,0,0;1.5708rad)
  shape: bbox 5.6 x 7.4 x 5.6 mm, 23 faces (baked)
FEATURE [Part::Feature] Part__Feature001002002001001050001001002001002001002001002001002001002001001002001002004001001001001002001002001125  label="Screw temp008"
  Placement = pos=(-146.5,106,10) rot=(1,0,0;1.5708rad)
  shape: bbox 5.6 x 7.4 x 5.6 mm, 23 faces (baked)
FEATURE [Part::Feature] Part__Feature001002002001001050001001002001002001002001002001002001002001001002001002004001001001001002001002001126  label="temp003"
  Placement = pos=(-156.5,109,10) rot=(-1,0,0;1.5708rad)
  shape: bbox 6 x 10 x 6.928 mm, 22 faces (baked)
FEATURE [Part::Feature] Part__Feature001002002001001050001001002001002001002001002001002001002001001002001002004001001001001002001002001127  label="temp001"
  Placement = pos=(-146.5,109,-10) rot=(-1,0,0;1.5708rad)
  shape: bbox 6 x 10 x 6.928 mm, 22 faces (baked)
FEATURE [Part::Feature] Part__Feature001002002001001050001001002001002001002001002001002001002001001002001002004001001001001002001002001128  label="temp002"
  Placement = pos=(-156.5,109,-10) rot=(-1,0,0;1.5708rad)
  shape: bbox 6 x 10 x 6.928 mm, 22 faces (baked)
FEATURE [App::Part] Part028  label="temp abstandsbolzen 10mm"
  Group = -> [Part__Feature001002002001001050001001002001002001002001002001002001002001001002001002004001001001001002001002001127,Part__Feature001002002001001050001001002001002001002001002001002001002001001002001002004001001001001002001002001128,Part__Feature001002002001001050001001002001002001002001002001002001002001001002001002004001001001001002001002001126,+1 more]
  Origin = -> Origin056
FEATURE [App::Part] Part029  label="temp schrauben unten"
  Group = -> [Part__Feature001002002001001050001001002001002001002001002001002001002001001002001002004001001001001002001002001121,Part__Feature001002002001001050001001002001002001002001002001002001002001001002001002004001001001001002001002001124,Part__Feature001002002001001050001001002001002001002001002001002001002001001002001002004001001001001002001002001122,+1 more]
  Origin = -> Origin057
FEATURE [App::Part] Part051  label="PTC Mounting"
  Group = -> [Part021,Part023,Part022]
  Origin = -> Origin085
FEATURE [App::Part] Part  label="PTC"
  Group = -> [Part__Feature001002002001001050001001002001002001002001002001002001002001001002001002004001001001001002001002001068,Part051]
  Origin = -> Origin
FEATURE [App::Part] Part053  label="E-Paper Mounting"
  Group = -> [Part040,Part041,Part043]
  Origin = -> Origin087
FEATURE [App::Part] Part045  label="E-Paper"
  Group = -> [Part030,Part053]
  Origin = -> Origin079
FEATURE [App::Part] Part054  label="Motion Detector Mounting"
  Group = -> [Part039,Part037]
  Origin = -> Origin088
FEATURE [App::Part] Part046  label="Motion Detector"
  Group = -> [Part__Feature001002002001001050001001002001002001002001002001002001002001001002001002004001001001001002001002001129,Part054]
  Origin = -> Origin080
FEATURE [App::Part] Part055  label="Ambiente Light Mounting"
  Group = -> [Part014,Part013,Part015,Part016]
  Origin = -> Origin089
FEATURE [App::Part] Part047  label="Ambiente Light"
  Group = -> [Part__Feature001002002001001050001001002001002001002001002001002001002001001002001002004001001001001002001002001067,Part055]
  Origin = -> Origin081
FEATURE [App::Part] Part056  label="Segment Display Mounting"
  Group = -> [Part033,Part034,Part036,Part035]
  Origin = -> Origin090
FEATURE [App::Part] Part048  label="Segment Display"
  Group = -> [Part__Feature001002002001001050001001002001002001002001002001002001002001001002001002004001001001001002001002001134,Part056]
  Origin = -> Origin082
FEATURE [App::Part] Part057  label="Humidity Mounting"
  Group = -> [Part026,Part025,Part024]
  Origin = -> Origin091
FEATURE [App::Part] Part049  label="Humidity"
  Group = -> [Part__Feature001002002001001050001001002001002001002001002001002001002001001002001002004001001001001002001002001063,Part057]
  Origin = -> Origin083
FEATURE [App::Part] Part058  label="Temperature Mounting"
  Group = -> [Part027,Part028,Part029]
  Origin = -> Origin092
FEATURE [App::Part] Part050  label="Temperature"
  Group = -> [Part011,Part058]
  Origin = -> Origin084
FEATURE [Part::Feature] Part__Feature001002002001001050001001002001002001002001002001002001002001001002001002004001001001001002001002001183  label="Screw Stack009"
  Placement = pos=(195.5,100.5,-17.5) rot=(0.707107,0,0.707107;3.14159rad)
  shape: bbox 7.4 x 5.6 x 5.6 mm, 23 faces (baked)
FEATURE [Part::Feature] Part__Feature001002002001001050001001002001002001002001002001002001002001001002001002004001001001001002001002001184  label="Screw Stack010"
  Placement = pos=(195.5,65.5,-17.5) rot=(0.707107,0,0.707107;3.14159rad)
  shape: bbox 7.4 x 5.6 x 5.6 mm, 23 faces (baked)
FEATURE [Part::Feature] Part__Feature001002002001001050001001002001002001002001002001002001002001001002001002004001001001001002001002001185  label="Screw Stack011"
  Placement = pos=(195.5,65.5,17.5) rot=(0.707107,0,0.707107;3.14159rad)
  shape: bbox 7.4 x 5.6 x 5.6 mm, 23 faces (baked)
FEATURE [Part::Feature] Part__Feature001002002001001050001001002001002001002001002001002001002001001002001002004001001001001002001002001186  label="Screw Stack012"
  Placement = pos=(195.5,100.5,17.5) rot=(0.707107,0,0.707107;3.14159rad)
  shape: bbox 7.4 x 5.6 x 5.6 mm, 23 faces (baked)
FEATURE [App::Part] Part065  label="stack schrauben unten001"
  Group = -> [Part__Feature001002002001001050001001002001002001002001002001002001002001001002001002004001001001001002001002001183,Part__Feature001002002001001050001001002001002001002001002001002001002001001002001002004001001001001002001002001184,Part__Feature001002002001001050001001002001002001002001002001002001002001001002001002004001001001001002001002001185,+1 more]
  Origin = -> Origin095
FEATURE [Part::Feature] Part__Feature001002002001001050001001002001002001002001002001002001002001001002001002004001001001001002001002001187  label="Screw Stack013"
  Placement = pos=(167,100.5,-17.5) rot=(0,-1,0;1.5708rad)
  shape: bbox 7.4 x 5.6 x 5.6 mm, 23 faces (baked)
FEATURE [Part::Feature] Part__Feature001002002001001050001001002001002001002001002001002001002001001002001002004001001001001002001002001188  label="Master_Brick001"
  Placement = pos=(180.9,83,0) rot=(0,-1,0;1.5708rad)
  shape: bbox 15.7 x 40.87 x 40 mm, 8354 faces (baked)
FEATURE [Part::Feature] Part__Feature001002002001001050001001002001002001002001002001002001002001001002001002004001001001001002001002001189  label="Screw Stack014"
  Placement = pos=(167,65.5,-17.5) rot=(0,-1,0;1.5708rad)
  shape: bbox 7.4 x 5.6 x 5.6 mm, 23 faces (baked)
FEATURE [Part::Feature] Part__Feature001002002001001050001001002001002001002001002001002001002001001002001002004001001001001002001002001190  label="Standoff Stack005"
  Placement = pos=(180.7,100.5,-17.5) rot=(0,-1,0;1.5708rad)
  shape: bbox 18.1 x 6.928 x 6 mm, 24 faces (baked)
FEATURE [Part::Feature] Part__Feature001002002001001050001001002001002001002001002001002001002001001002001002004001001001001002001002001191  label="Fusion008"
  shape: bbox 40 x 40 x 15.7 mm, 6790 faces (baked)
FEATURE [Part::Feature] Part__Feature001002002001001050001001002001002001002001002001002001002001001002001002004001001001001002001002001192  label="Standoff Stack006"
  Placement = pos=(180.7,65.5,17.5) rot=(0,-1,0;1.5708rad)
  shape: bbox 18.1 x 6.928 x 6 mm, 24 faces (baked)
FEATURE [Part::Feature] Part__Feature001002002001001050001001002001002001002001002001002001002001001002001002004001001001001002001002001193  label="Cut011"
  Placement = pos=(192.5,100.5,-17.5) rot=(0,-1,0;1.5708rad)
  shape: bbox 10 x 6.928 x 6 mm, 22 faces (baked)
FEATURE [Part::Feature] Part__Feature001002002001001050001001002001002001002001002001002001002001001002001002004001001001001002001002001194  label="Screw Stack015"
  Placement = pos=(167,65.5,17.5) rot=(0,-1,0;1.5708rad)
  shape: bbox 7.4 x 5.6 x 5.6 mm, 23 faces (baked)
FEATURE [Part::Feature] Part__Feature001002002001001050001001002001002001002001002001002001002001001002001002004001001001001002001002001195  label="Cut012"
  Placement = pos=(192.5,65.5,-17.5) rot=(0,-1,0;1.5708rad)
  shape: bbox 10 x 6.928 x 6 mm, 22 faces (baked)
FEATURE [Part::Feature] Part__Feature001002002001001050001001002001002001002001002001002001002001001002001002004001001001001002001002001196  label="Standoff Stack007"
  Placement = pos=(180.7,100.5,17.5) rot=(0,-1,0;1.5708rad)
  shape: bbox 18.1 x 6.928 x 6 mm, 24 faces (baked)
FEATURE [Part::Feature] Part__Feature001002002001001050001001002001002001002001002001002001002001001002001002004001001001001002001002001197  label="Cut013"
  Placement = pos=(192.5,65.5,17.5) rot=(0,-1,0;1.5708rad)
  shape: bbox 10 x 6.928 x 6 mm, 22 faces (baked)
FEATURE [Part::Feature] Part__Feature001002002001001050001001002001002001002001002001002001002001001002001002004001001001001002001002001198  label="Ethernet_Buchse001"
  shape: bbox 26.47 x 22.26 x 12.3 mm, 1543 faces, 3 solids (baked)
FEATURE [App::Part] Part064  label="Ethernet001"
  Group = -> [Part__Feature001002002001001050001001002001002001002001002001002001002001001002001002004001001001001002001002001191,Part__Feature001002002001001050001001002001002001002001002001002001002001001002001002004001001001001002001002001198]
  License = CC BY 3.0
  LicenseURL = http://creativecommons.org/licenses/by/3.0/
  Origin = -> Origin096
  Placement = pos=(168.6,103,20) rot=(-0.707107,0,0.707107;3.14159rad)
FEATURE [Part::Feature] Part__Feature001002002001001050001001002001002001002001002001002001002001001002001002004001001001001002001002001199  label="Cut014"
  Placement = pos=(192.5,100.5,17.5) rot=(0,-1,0;1.5708rad)
  shape: bbox 10 x 6.928 x 6 mm, 22 faces (baked)
FEATURE [App::Part] Part063  label="stack abstandsbolzen 10mm001"
  Group = -> [Part__Feature001002002001001050001001002001002001002001002001002001002001001002001002004001001001001002001002001193,Part__Feature001002002001001050001001002001002001002001002001002001002001001002001002004001001001001002001002001195,Part__Feature001002002001001050001001002001002001002001002001002001002001001002001002004001001001001002001002001197,+1 more]
  Origin = -> Origin097
FEATURE [Part::Feature] Part__Feature001002002001001050001001002001002001002001002001002001002001001002001002004001001001001002001002001200  label="Standoff Stack008"
  Placement = pos=(180.7,65.5,-17.5) rot=(0,-1,0;1.5708rad)
  shape: bbox 18.1 x 6.928 x 6 mm, 24 faces (baked)
FEATURE [App::Part] Part062  label="stack abstandsbolzen 12mm001"
  Group = -> [Part__Feature001002002001001050001001002001002001002001002001002001002001001002001002004001001001001002001002001190,Part__Feature001002002001001050001001002001002001002001002001002001002001001002001002004001001001001002001002001200,Part__Feature001002002001001050001001002001002001002001002001002001002001001002001002004001001001001002001002001192,+1 more]
  Origin = -> Origin101
FEATURE [Part::Feature] Part__Feature001002002001001050001001002001002001002001002001002001002001001002001002004001001001001002001002001201  label="Screw Stack016"
  Placement = pos=(167,100.5,17.5) rot=(0,-1,0;1.5708rad)
  shape: bbox 7.4 x 5.6 x 5.6 mm, 23 faces (baked)
FEATURE [App::Part] Part061  label="stack schrauben oben001"
  Group = -> [Part__Feature001002002001001050001001002001002001002001002001002001002001001002001002004001001001001002001002001187,Part__Feature001002002001001050001001002001002001002001002001002001002001001002001002004001001001001002001002001189,Part__Feature001002002001001050001001002001002001002001002001002001002001001002001002004001001001001002001002001194,+1 more]
  Origin = -> Origin098
FEATURE [App::Part] Part067  label="Stack Mounting001"
  Group = -> [Part061,Part062,Part063,Part065]
  Origin = -> Origin100
FEATURE [App::Part] Part066  label="Stack hinten"
  Group = -> [Part__Feature001002002001001050001001002001002001002001002001002001002001001002001002004001001001001002001002001188,Part064,Part067]
  Origin = -> Origin099
FEATURE [Part::Feature] Part__Feature001002002001001050001001002001002001002001002001002001002001001002001002004001001001001002001002001202  label="Screw Long SRM vorn l"
  Placement = pos=(-209.5,-3,0) rot=(1,0,0;1.5708rad)
  shape: bbox 5.6 x 12.4 x 5.6 mm, 20 faces (baked)
FEATURE [Part::Feature] Part__Feature001002002001001050001001002001002001002001002001002001002001001002001002004001001001001002001002001203  label="Screw Long SRM vorn r"
  Placement = pos=(209.5,-3,0) rot=(1,0,0;1.5708rad)
  shape: bbox 5.6 x 12.4 x 5.6 mm, 20 faces (baked)
FEATURE [App::Part] Part068  label="SRM schrauben vorne"
  Group = -> [Part__Feature001002002001001050001001002001002001002001002001002001002001001002001002004001001001001002001002001202,Part__Feature001002002001001050001001002001002001002001002001002001002001001002001002004001001001001002001002001203]
  Origin = -> Origin102
FEATURE [App::Part] Part069  label="Master Brick vorne"
  Group = -> [Part__Feature001002002001001050001001002001002001002001002001002001002001001002001002004001001001001002001002001060]
  Origin = -> Origin103
FEATURE [App::Part] Part017  label="stack schrauben oben"
  Group = -> [Part__Feature001002002001001050001001002001002,Part__Feature001002002001001050001001002001002001,Part__Feature001002002001001050001001002001002002,Part__Feature001002002001001050001001002001002001001]
  Origin = -> Origin045
FEATURE [App::Part] Part052  label="Stack Mounting"
  Group = -> [Part017,Part019,Part020,Part018]
  Origin = -> Origin086
FEATURE [App::Part] Part070  label="Ethernet vorne"
  Group = -> [Part012]
  Origin = -> Origin104
FEATURE [App::Part] Part044  label="Stack vorne"
  Group = -> [Part052,Part069,Part070]
  Origin = -> Origin078
FEATURE [App::Part] Part060  label="Bricks/Bricklets"
  Group = -> [Part044,Part,Part045,Part046,Part047,Part048,Part049,Part050,Part066]
  Origin = -> Origin094
FEATURE [Part::Feature] Part__Feature  label="Boden"
  Placement = pos=(0,0,-19.5) rot=(0,0,1;0rad)
  shape: bbox 397 x 99 x 3 mm, 902 faces (baked)
FEATURE [Part::Feature] Part__Feature001002002001001050001001002001002001002001002001002001002001001002001002004001001001001002001002001205  label="Deckel"
  Placement = pos=(-1.78e-14,0,17.5) rot=(0,0,1;0rad)
  shape: bbox 397 x 98.5 x 3 mm, 908 faces (baked)
FEATURE [Part::Feature] Part__Feature001002002001001050001001002001002001002001002001002001002001001002001002004001001001001002001002001206  label="Hinten"
  Placement = pos=(0,109,0) rot=(1,0,0;1.5708rad)
  shape: bbox 405 x 3 x 44 mm, 247 faces (baked)
FEATURE [App::Part] Part071  label="Deckel001"
  Group = -> [Part__Feature001002002001001050001001002001002001002001002001002001002001001002001002004001001001001002001002001205]
  Origin = -> Origin105
FEATURE [App::Part] Part072  label="Boden001"
  Group = -> [Part__Feature]
  Origin = -> Origin106
FEATURE [App::Part] Part073  label="Hinten001"
  Group = -> [Part__Feature001002002001001050001001002001002001002001002001002001002001001002001002004001001001001002001002001206]
  Origin = -> Origin107
FEATURE [Part::Feature] Part__Feature001002002001001050001001002001002001002001002001002001002001001002001002004001001001001002001002001207  label="Screw Long SRM seite l"
  Placement = pos=(-192.5,22,0) rot=(0.57735,0.57735,0.57735;2.0944rad)
  shape: bbox 12.4 x 5.6 x 5.6 mm, 20 faces (baked)
FEATURE [Part::Feature] Part__Feature001002002001001050001001002001002001002001002001002001002001001002001002004001001001001002001002001208  label="Screw Long SRM seite r"
  Placement = pos=(192.5,22,0) rot=(0.57735,-0.57735,-0.57735;2.0944rad)
  shape: bbox 12.4 x 5.6 x 5.6 mm, 20 faces (baked)
FEATURE [App::Part] Part074  label="SRM schrauben seiten"
  Group = -> [Part__Feature001002002001001050001001002001002001002001002001002001002001001002001002004001001001001002001002001207,Part__Feature001002002001001050001001002001002001002001002001002001002001001002001002004001001001001002001002001208]
  Origin = -> Origin108
FEATURE [Part::Feature] Part__Feature001002002001001050001001002001002001002001002001002001002001001002001002004001001001001002001002001209  label="Screw Long SRM hinten l"
  Placement = pos=(-194,109,0) rot=(0,0.707107,0.707107;3.14159rad)
  shape: bbox 5.6 x 12.4 x 5.6 mm, 20 faces (baked)
FEATURE [Part::Feature] Part__Feature001002002001001050001001002001002001002001002001002001002001001002001002004001001001001002001002001210  label="Screw Long SRM hinten r"
  Placement = pos=(194,109,0) rot=(0,0.707107,0.707107;3.14159rad)
  shape: bbox 5.6 x 12.4 x 5.6 mm, 20 faces (baked)
FEATURE [Part::Feature] Part__Feature001002002001001050001001002001002001002001002001002001002001001002001002004001001001001002001002001211  label="Screw Long SRM umten l"
  Placement = pos=(-194,75.5,-19.5) rot=(0,1,0;3.14159rad)
  shape: bbox 5.6 x 5.6 x 12.4 mm, 20 faces (baked)
FEATURE [Part::Feature] Part__Feature001002002001001050001001002001002001002001002001002001002001001002001002004001001001001002001002001212  label="Screw Long SRM unten r"
  Placement = pos=(194,35.5,-19.5) rot=(0,1,0;3.14159rad)
  shape: bbox 5.6 x 5.6 x 12.4 mm, 20 faces (baked)
FEATURE [App::Part] Part077  label="RP schiene"
  Group = -> [Body023,Body024,Fusion]
  Origin = -> Origin111
FEATURE [Part::Feature] Part__Feature001002002001001050001001002001002001002001002001002001002001001002001002004001001001001002001002001213  label="Nut SRM vorne r"
  Placement = pos=(209.5,6.35,0) rot=(1,0,0;1.5708rad)
  shape: bbox 6.352 x 2.4 x 6.351 mm, 30 faces (baked)
FEATURE [Part::Feature] Part__Feature001002002001001050001001002001002001002001002001002001002001001002001002004001001001001002001002001216  label="Nut SRM vorne l"
  Placement = pos=(-209.5,6.35,0) rot=(1,0,0;1.5708rad)
  shape: bbox 6.352 x 2.4 x 6.351 mm, 30 faces (baked)
FEATURE [App::Part] Part079  label="SRM muttern vorne"
  Group = -> [Part__Feature001002002001001050001001002001002001002001002001002001002001001002001002004001001001001002001002001216,Part__Feature001002002001001050001001002001002001002001002001002001002001001002001002004001001001001002001002001213]
  Origin = -> Origin113
FEATURE [Part::Feature] Part__Feature001002002001001050001001002001002001002001002001002001002001001002001002004001001001001002001002001217  label="Nut SRM seiten r"
  Placement = pos=(201.85,22,0) rot=(0.57735,-0.57735,-0.57735;2.0944rad)
  shape: bbox 2.4 x 6.352 x 6.351 mm, 30 faces (baked)
FEATURE [Part::Feature] Part__Feature001002002001001050001001002001002001002001002001002001002001001002001002004001001001001002001002001218  label="Nut SRM seiten l"
  Placement = pos=(-201.85,22,0) rot=(0.57735,0.57735,0.57735;2.0944rad)
  shape: bbox 2.4 x 6.352 x 6.351 mm, 30 faces (baked)
FEATURE [App::Part] Part080  label="SRM muttern seiten"
  Group = -> [Part__Feature001002002001001050001001002001002001002001002001002001002001001002001002004001001001001002001002001218,Part__Feature001002002001001050001001002001002001002001002001002001002001001002001002004001001001001002001002001217]
  Origin = -> Origin114
FEATURE [Part::Feature] Part__Feature001002002001001050001001002001002001002001002001002001002001001002001002004001001001001002001002001219  label="Nut SRM unten l"
  Placement = pos=(-194,75.5,-11.55) rot=(0.57735,0.57735,0.57735;0rad)
  shape: bbox 6.352 x 6.351 x 2.4 mm, 30 faces (baked)
FEATURE [Part::Feature] Part__Feature001002002001001050001001002001002001002001002001002001002001001002001002004001001001001002001002001220  label="Nut SRM unten r"
  Placement = pos=(194,35.5,-11.55) rot=(0.57735,-0.57735,-0.57735;0rad)
  shape: bbox 6.352 x 6.351 x 2.4 mm, 30 faces (baked)
FEATURE [Part::Feature] Part__Feature001002002001001050001001002001002001002001002001002001002001001002001002004001001001001002001002001221  label="Nut SRM hinten r"
  Placement = pos=(194,101.05,0) rot=(1,0,0;1.5708rad)
  shape: bbox 6.352 x 2.4 x 6.351 mm, 30 faces (baked)
FEATURE [Part::Feature] Part__Feature001002002001001050001001002001002001002001002001002001002001001002001002004001001001001002001002001222  label="Nut SRM hinten l"
  Placement = pos=(-194,101.05,0) rot=(1,0,0;1.5708rad)
  shape: bbox 6.352 x 2.4 x 6.351 mm, 30 faces (baked)
FEATURE [Part::Feature] Part__Feature001002002001001050001001002001002001002001002001002001002001001002001002004001001001001002001002001223  label="Screw Long SRM mitte"
  Placement = pos=(-38,109,0) rot=(0,0.707107,0.707107;3.14159rad)
  shape: bbox 5.6 x 12.4 x 5.6 mm, 20 faces (baked)
FEATURE [App::Part] Part075  label="SRM schrauben hinten"
  Group = -> [Part__Feature001002002001001050001001002001002001002001002001002001002001001002001002004001001001001002001002001209,Part__Feature001002002001001050001001002001002001002001002001002001002001001002001002004001001001001002001002001210,Part__Feature001002002001001050001001002001002001002001002001002001002001001002001002004001001001001002001002001223]
  Origin = -> Origin109
FEATURE [Part::Feature] Part__Feature001002002001001050001001002001002001002001002001002001002001001002001002004001001001001002001002001224  label="Nut SRM hinten mitte"
  Placement = pos=(-38,101.05,0) rot=(1,0,0;1.5708rad)
  shape: bbox 6.352 x 2.4 x 6.351 mm, 30 faces (baked)
FEATURE [App::Part] Part082  label="SRM muttern hinten"
  Group = -> [Part__Feature001002002001001050001001002001002001002001002001002001002001001002001002004001001001001002001002001222,Part__Feature001002002001001050001001002001002001002001002001002001002001001002001002004001001001001002001002001221,Part__Feature001002002001001050001001002001002001002001002001002001002001001002001002004001001001001002001002001224]
  Origin = -> Origin116
FEATURE [Part::Feature] Part__Feature001002002001001050001001002001002001002001002001002001002001001002001002004001001001001002001002001225  label="Screw Long SRM umten mitte"
  Placement = pos=(-38,89.5,-19.5) rot=(0,1,0;3.14159rad)
  shape: bbox 5.6 x 5.6 x 12.4 mm, 20 faces (baked)
FEATURE [App::Part] Part076  label="SRM schrauben unten"
  Group = -> [Part__Feature001002002001001050001001002001002001002001002001002001002001001002001002004001001001001002001002001211,Part__Feature001002002001001050001001002001002001002001002001002001002001001002001002004001001001001002001002001212,Part__Feature001002002001001050001001002001002001002001002001002001002001001002001002004001001001001002001002001225]
  Origin = -> Origin110
FEATURE [Part::Feature] Part__Feature001002002001001050001001002001002001002001002001002001002001001002001002004001001001001002001002001226  label="Nut SRM unten mitte"
  Placement = pos=(-38,89.5,-11.55) rot=(0.57735,0.57735,0.57735;0rad)
  shape: bbox 6.352 x 6.351 x 2.4 mm, 30 faces (baked)
FEATURE [App::Part] Part081  label="SRM muttern unten"
  Group = -> [Part__Feature001002002001001050001001002001002001002001002001002001002001001002001002004001001001001002001002001219,Part__Feature001002002001001050001001002001002001002001002001002001002001001002001002004001001001001002001002001220,Part__Feature001002002001001050001001002001002001002001002001002001002001001002001002004001001001001002001002001226]
  Origin = -> Origin115
FEATURE [App::Part] Part078  label="SRM 2020 mounting"
  Group = -> [Part068,Part079,Part074,Part080,Part076,Part081,Part075,Part082]
  Origin = -> Origin112
FEATURE [App::Part] Part059  label="SRM 2020"
  Group = -> [Body026,Fillet037,Body012,Fillet020,Body016,Fillet025,Fillet010,Body006,Fillet,Body007,Fillet011,Fillet012,Body025,Fillet036,Part071,Part072,Part073,Part077,Part078]
  Origin = -> Origin093
FEATURE [App::Part] Part083  label="Back"
  Group = -> [Body015,Fillet028]
  Origin = -> Origin117
  Placement = pos=(0,0,0) rot=(1,0,0;1.5708rad)
